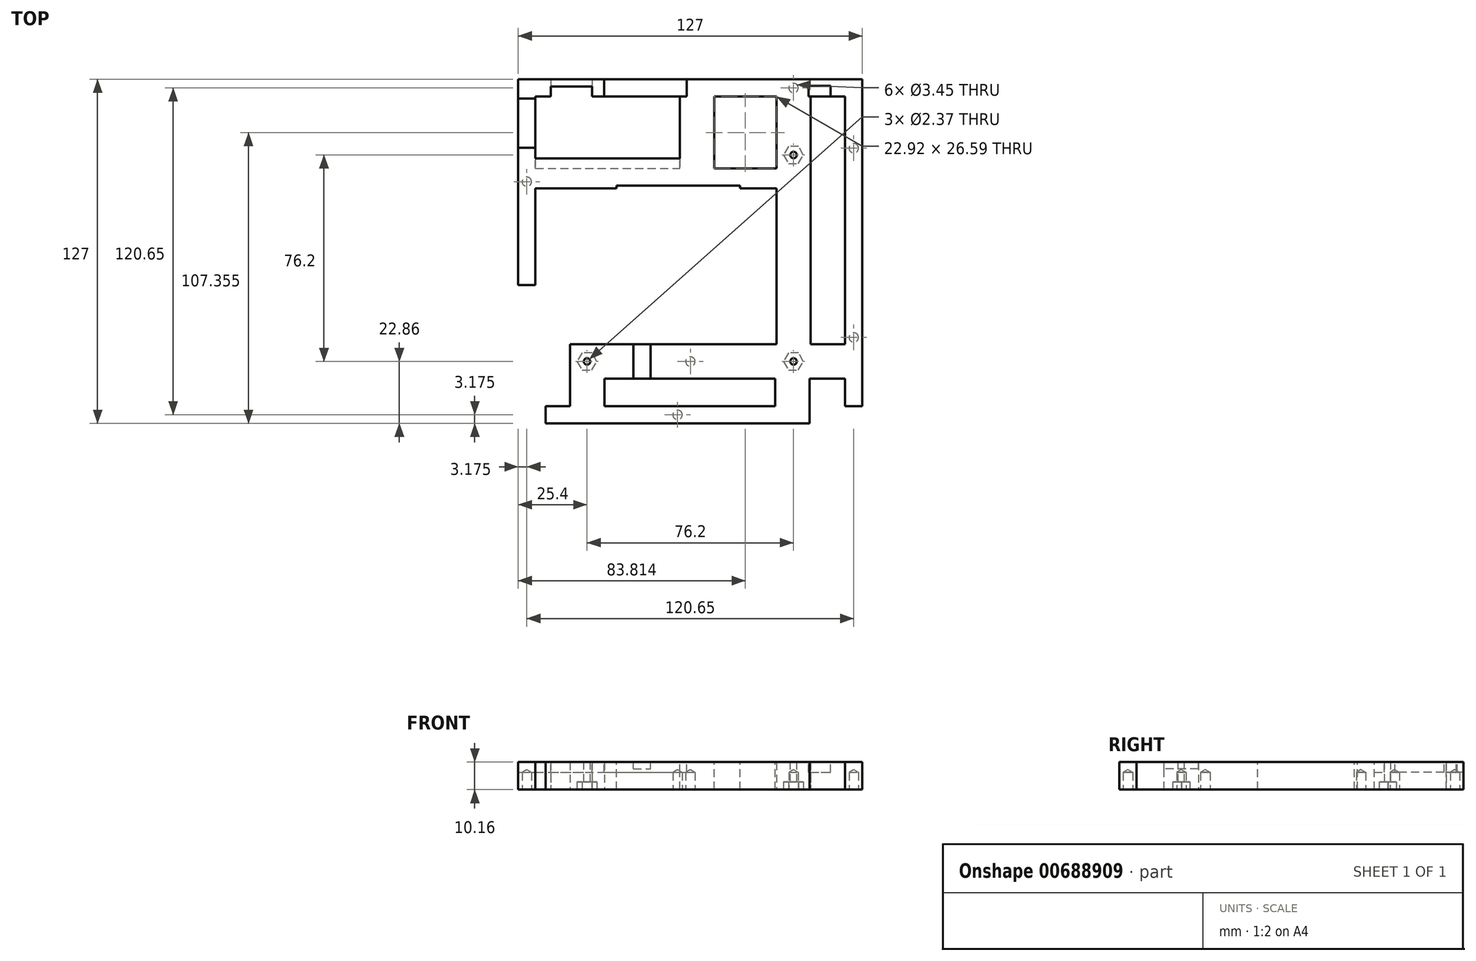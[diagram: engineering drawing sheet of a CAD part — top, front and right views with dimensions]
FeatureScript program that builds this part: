
annotation { "Feature Type Name" : "Feature", "Feature Type Description" : "" }
export const myFeature = defineFeature(function(context is Context, id is Id, definition is map)
    precondition{}
    {
        {
            var Q0;
            Q0=qCreatedBy(makeId("Top.planeOp"),FACE);
            var sketch = newSketch(context, id + "F0", { "sketchPlane" : qUnion([Q0])});
            skLineSegment(sketch, "E0", {"start": v(-9.04, 13.82) * mm, "end": v(-9.04, 13.7) * mm});
            skLineSegment(sketch, "E1", {"start": v(-9.04, 13.7) * mm, "end": v(-9.28, 13.35) * mm});
            skLineSegment(sketch, "E2", {"start": v(-9.28, 13.35) * mm, "end": v(-9.32, 13.32) * mm});
            skLineSegment(sketch, "E3", {"start": v(-9.32, 13.32) * mm, "end": v(-9.37, 13.3) * mm});
            skLineSegment(sketch, "E4", {"start": v(-9.37, 13.3) * mm, "end": v(-9.85, 13.3) * mm});
            skLineSegment(sketch, "E5", {"start": v(-9.85, 13.3) * mm, "end": v(-9.9, 13.32) * mm});
            skLineSegment(sketch, "E6", {"start": v(-9.9, 13.32) * mm, "end": v(-9.94, 13.35) * mm});
            skLineSegment(sketch, "E7", {"start": v(-9.94, 13.35) * mm, "end": v(-10.18, 13.7) * mm});
            skLineSegment(sketch, "E8", {"start": v(-10.18, 13.7) * mm, "end": v(-10.18, 13.82) * mm});
            skLineSegment(sketch, "E9", {"start": v(-10.18, 13.82) * mm, "end": v(-10.18, 13.94) * mm});
            skLineSegment(sketch, "E10", {"start": v(-10.18, 13.94) * mm, "end": v(-9.94, 14.3) * mm});
            skLineSegment(sketch, "E11", {"start": v(-9.94, 14.3) * mm, "end": v(-9.9, 14.31) * mm});
            skLineSegment(sketch, "E12", {"start": v(-9.9, 14.31) * mm, "end": v(-9.85, 14.34) * mm});
            skLineSegment(sketch, "E13", {"start": v(-9.85, 14.34) * mm, "end": v(-9.37, 14.34) * mm});
            skLineSegment(sketch, "E14", {"start": v(-9.37, 14.34) * mm, "end": v(-9.32, 14.31) * mm});
            skLineSegment(sketch, "E15", {"start": v(-9.32, 14.31) * mm, "end": v(-9.28, 14.3) * mm});
            skLineSegment(sketch, "E16", {"start": v(-9.28, 14.3) * mm, "end": v(-9.04, 13.94) * mm});
            skLineSegment(sketch, "E17", {"start": v(-9.04, 13.94) * mm, "end": v(-9.04, 13.82) * mm});
            skLineSegment(sketch, "E18", {"start": v(-52.06, -1.27) * mm, "end": v(-52.06, -1.46) * mm});
            skLineSegment(sketch, "E19", {"start": v(-52.06, -1.46) * mm, "end": v(-52.26, -2.02) * mm});
            skLineSegment(sketch, "E20", {"start": v(-52.26, -2.02) * mm, "end": v(-52.7, -2.5) * mm});
            skLineSegment(sketch, "E21", {"start": v(-52.7, -2.5) * mm, "end": v(-52.8, -2.57) * mm});
            skLineSegment(sketch, "E22", {"start": v(-52.8, -2.57) * mm, "end": v(-52.93, -2.63) * mm});
            skLineSegment(sketch, "E23", {"start": v(-52.93, -2.63) * mm, "end": v(-53.56, -2.77) * mm});
            skLineSegment(sketch, "E24", {"start": v(-53.56, -2.77) * mm, "end": v(-54.2, -2.63) * mm});
            skLineSegment(sketch, "E25", {"start": v(-54.2, -2.63) * mm, "end": v(-54.3, -2.57) * mm});
            skLineSegment(sketch, "E26", {"start": v(-54.3, -2.57) * mm, "end": v(-54.43, -2.5) * mm});
            skLineSegment(sketch, "E27", {"start": v(-54.43, -2.5) * mm, "end": v(-54.86, -2.02) * mm});
            skLineSegment(sketch, "E28", {"start": v(-54.86, -2.02) * mm, "end": v(-55.06, -1.46) * mm});
            skLineSegment(sketch, "E29", {"start": v(-55.06, -1.46) * mm, "end": v(-55.06, -1.27) * mm});
            skLineSegment(sketch, "E30", {"start": v(-55.06, -1.27) * mm, "end": v(-55.06, -1.08) * mm});
            skLineSegment(sketch, "E31", {"start": v(-55.06, -1.08) * mm, "end": v(-54.86, -0.52) * mm});
            skLineSegment(sketch, "E32", {"start": v(-54.86, -0.52) * mm, "end": v(-54.43, -0.04) * mm});
            skLineSegment(sketch, "E33", {"start": v(-54.43, -0.04) * mm, "end": v(-54.3, 0.03) * mm});
            skLineSegment(sketch, "E34", {"start": v(-54.3, 0.03) * mm, "end": v(-54.2, 0.1) * mm});
            skLineSegment(sketch, "E35", {"start": v(-54.2, 0.1) * mm, "end": v(-53.56, 0.23) * mm});
            skLineSegment(sketch, "E36", {"start": v(-53.56, 0.23) * mm, "end": v(-52.93, 0.1) * mm});
            skLineSegment(sketch, "E37", {"start": v(-52.93, 0.1) * mm, "end": v(-52.8, 0.03) * mm});
            skLineSegment(sketch, "E38", {"start": v(-52.8, 0.03) * mm, "end": v(-52.7, -0.04) * mm});
            skLineSegment(sketch, "E39", {"start": v(-52.7, -0.04) * mm, "end": v(-52.26, -0.52) * mm});
            skLineSegment(sketch, "E40", {"start": v(-52.26, -0.52) * mm, "end": v(-52.06, -1.08) * mm});
            skLineSegment(sketch, "E41", {"start": v(-52.06, -1.08) * mm, "end": v(-52.06, -1.27) * mm});
            skLineSegment(sketch, "E42", {"start": v(-52.06, -9.17) * mm, "end": v(-52.06, -9.36) * mm});
            skLineSegment(sketch, "E43", {"start": v(-52.06, -9.36) * mm, "end": v(-52.26, -9.92) * mm});
            skLineSegment(sketch, "E44", {"start": v(-52.26, -9.92) * mm, "end": v(-52.7, -10.4) * mm});
            skLineSegment(sketch, "E45", {"start": v(-52.7, -10.4) * mm, "end": v(-52.8, -10.47) * mm});
            skLineSegment(sketch, "E46", {"start": v(-52.8, -10.47) * mm, "end": v(-52.93, -10.54) * mm});
            skLineSegment(sketch, "E47", {"start": v(-52.93, -10.54) * mm, "end": v(-53.56, -10.67) * mm});
            skLineSegment(sketch, "E48", {"start": v(-53.56, -10.67) * mm, "end": v(-54.2, -10.54) * mm});
            skLineSegment(sketch, "E49", {"start": v(-54.2, -10.54) * mm, "end": v(-54.3, -10.47) * mm});
            skLineSegment(sketch, "E50", {"start": v(-54.3, -10.47) * mm, "end": v(-54.43, -10.4) * mm});
            skLineSegment(sketch, "E51", {"start": v(-54.43, -10.4) * mm, "end": v(-54.86, -9.92) * mm});
            skLineSegment(sketch, "E52", {"start": v(-54.86, -9.92) * mm, "end": v(-55.06, -9.36) * mm});
            skLineSegment(sketch, "E53", {"start": v(-55.06, -9.36) * mm, "end": v(-55.06, -9.17) * mm});
            skLineSegment(sketch, "E54", {"start": v(-55.06, -9.17) * mm, "end": v(-55.06, -8.98) * mm});
            skLineSegment(sketch, "E55", {"start": v(-55.06, -8.98) * mm, "end": v(-54.86, -8.42) * mm});
            skLineSegment(sketch, "E56", {"start": v(-54.86, -8.42) * mm, "end": v(-54.43, -7.94) * mm});
            skLineSegment(sketch, "E57", {"start": v(-54.43, -7.94) * mm, "end": v(-54.3, -7.87) * mm});
            skLineSegment(sketch, "E58", {"start": v(-54.3, -7.87) * mm, "end": v(-54.2, -7.8) * mm});
            skLineSegment(sketch, "E59", {"start": v(-54.2, -7.8) * mm, "end": v(-53.56, -7.67) * mm});
            skLineSegment(sketch, "E60", {"start": v(-53.56, -7.67) * mm, "end": v(-52.93, -7.8) * mm});
            skLineSegment(sketch, "E61", {"start": v(-52.93, -7.8) * mm, "end": v(-52.8, -7.87) * mm});
            skLineSegment(sketch, "E62", {"start": v(-52.8, -7.87) * mm, "end": v(-52.7, -7.94) * mm});
            skLineSegment(sketch, "E63", {"start": v(-52.7, -7.94) * mm, "end": v(-52.26, -8.42) * mm});
            skLineSegment(sketch, "E64", {"start": v(-52.26, -8.42) * mm, "end": v(-52.06, -8.98) * mm});
            skLineSegment(sketch, "E65", {"start": v(-52.06, -8.98) * mm, "end": v(-52.06, -9.17) * mm});
            skLineSegment(sketch, "E66", {"start": v(-38.7, 57.1) * mm, "end": v(-38.7, 56.77) * mm});
            skLineSegment(sketch, "E67", {"start": v(-38.7, 56.77) * mm, "end": v(-38.87, 55.78) * mm});
            skLineSegment(sketch, "E68", {"start": v(-38.87, 55.78) * mm, "end": v(-39.38, 54.56) * mm});
            skLineSegment(sketch, "E69", {"start": v(-39.38, 54.56) * mm, "end": v(-40.18, 53.52) * mm});
            skLineSegment(sketch, "E70", {"start": v(-40.18, 53.52) * mm, "end": v(-40.95, 52.87) * mm});
            skLineSegment(sketch, "E71", {"start": v(-40.95, 52.87) * mm, "end": v(-41.24, 52.7) * mm});
            skLineSegment(sketch, "E72", {"start": v(-41.24, 52.7) * mm, "end": v(-41.52, 52.53) * mm});
            skLineSegment(sketch, "E73", {"start": v(-41.52, 52.53) * mm, "end": v(-42.47, 52.2) * mm});
            skLineSegment(sketch, "E74", {"start": v(-42.47, 52.2) * mm, "end": v(-43.78, 52.02) * mm});
            skLineSegment(sketch, "E75", {"start": v(-43.78, 52.02) * mm, "end": v(-45.08, 52.2) * mm});
            skLineSegment(sketch, "E76", {"start": v(-45.08, 52.2) * mm, "end": v(-46.03, 52.53) * mm});
            skLineSegment(sketch, "E77", {"start": v(-46.03, 52.53) * mm, "end": v(-46.32, 52.7) * mm});
            skLineSegment(sketch, "E78", {"start": v(-46.32, 52.7) * mm, "end": v(-46.6, 52.87) * mm});
            skLineSegment(sketch, "E79", {"start": v(-46.6, 52.87) * mm, "end": v(-47.38, 53.52) * mm});
            skLineSegment(sketch, "E80", {"start": v(-47.38, 53.52) * mm, "end": v(-48.18, 54.56) * mm});
            skLineSegment(sketch, "E81", {"start": v(-48.18, 54.56) * mm, "end": v(-48.68, 55.78) * mm});
            skLineSegment(sketch, "E82", {"start": v(-48.68, 55.78) * mm, "end": v(-48.86, 56.77) * mm});
            skLineSegment(sketch, "E83", {"start": v(-48.86, 56.77) * mm, "end": v(-48.86, 57.1) * mm});
            skLineSegment(sketch, "E84", {"start": v(-48.86, 57.1) * mm, "end": v(-48.86, 57.43) * mm});
            skLineSegment(sketch, "E85", {"start": v(-48.86, 57.43) * mm, "end": v(-48.68, 58.43) * mm});
            skLineSegment(sketch, "E86", {"start": v(-48.68, 58.43) * mm, "end": v(-48.18, 59.64) * mm});
            skLineSegment(sketch, "E87", {"start": v(-48.18, 59.64) * mm, "end": v(-47.38, 60.68) * mm});
            skLineSegment(sketch, "E88", {"start": v(-47.38, 60.68) * mm, "end": v(-46.6, 61.33) * mm});
            skLineSegment(sketch, "E89", {"start": v(-46.6, 61.33) * mm, "end": v(-46.32, 61.5) * mm});
            skLineSegment(sketch, "E90", {"start": v(-46.32, 61.5) * mm, "end": v(-46.03, 61.67) * mm});
            skLineSegment(sketch, "E91", {"start": v(-46.03, 61.67) * mm, "end": v(-45.08, 62.01) * mm});
            skLineSegment(sketch, "E92", {"start": v(-45.08, 62.01) * mm, "end": v(-43.78, 62.18) * mm});
            skLineSegment(sketch, "E93", {"start": v(-43.78, 62.18) * mm, "end": v(-42.47, 62.01) * mm});
            skLineSegment(sketch, "E94", {"start": v(-42.47, 62.01) * mm, "end": v(-41.52, 61.67) * mm});
            skLineSegment(sketch, "E95", {"start": v(-41.52, 61.67) * mm, "end": v(-41.24, 61.5) * mm});
            skLineSegment(sketch, "E96", {"start": v(-41.24, 61.5) * mm, "end": v(-40.95, 61.33) * mm});
            skLineSegment(sketch, "E97", {"start": v(-40.95, 61.33) * mm, "end": v(-40.18, 60.68) * mm});
            skLineSegment(sketch, "E98", {"start": v(-40.18, 60.68) * mm, "end": v(-39.38, 59.64) * mm});
            skLineSegment(sketch, "E99", {"start": v(-39.38, 59.64) * mm, "end": v(-38.87, 58.43) * mm});
            skLineSegment(sketch, "E100", {"start": v(-38.87, 58.43) * mm, "end": v(-38.7, 57.43) * mm});
            skLineSegment(sketch, "E101", {"start": v(-38.7, 57.43) * mm, "end": v(-38.7, 57.1) * mm});
            skLineSegment(sketch, "E102", {"start": v(-38.78, 38.1) * mm, "end": v(-38.78, 37.77) * mm});
            skLineSegment(sketch, "E103", {"start": v(-38.78, 37.77) * mm, "end": v(-38.95, 36.8) * mm});
            skLineSegment(sketch, "E104", {"start": v(-38.95, 36.8) * mm, "end": v(-39.45, 35.6) * mm});
            skLineSegment(sketch, "E105", {"start": v(-39.45, 35.6) * mm, "end": v(-40.23, 34.57) * mm});
            skLineSegment(sketch, "E106", {"start": v(-40.23, 34.57) * mm, "end": v(-41, 33.93) * mm});
            skLineSegment(sketch, "E107", {"start": v(-41, 33.93) * mm, "end": v(-41.28, 33.77) * mm});
            skLineSegment(sketch, "E108", {"start": v(-41.28, 33.77) * mm, "end": v(-41.56, 33.6) * mm});
            skLineSegment(sketch, "E109", {"start": v(-41.56, 33.6) * mm, "end": v(-42.5, 33.27) * mm});
            skLineSegment(sketch, "E110", {"start": v(-42.5, 33.27) * mm, "end": v(-43.78, 33.1) * mm});
            skLineSegment(sketch, "E111", {"start": v(-43.78, 33.1) * mm, "end": v(-45.06, 33.27) * mm});
            skLineSegment(sketch, "E112", {"start": v(-45.06, 33.27) * mm, "end": v(-46, 33.6) * mm});
            skLineSegment(sketch, "E113", {"start": v(-46, 33.6) * mm, "end": v(-46.28, 33.77) * mm});
            skLineSegment(sketch, "E114", {"start": v(-46.28, 33.77) * mm, "end": v(-46.56, 33.93) * mm});
            skLineSegment(sketch, "E115", {"start": v(-46.56, 33.93) * mm, "end": v(-47.32, 34.57) * mm});
            skLineSegment(sketch, "E116", {"start": v(-47.32, 34.57) * mm, "end": v(-48.1, 35.6) * mm});
            skLineSegment(sketch, "E117", {"start": v(-48.1, 35.6) * mm, "end": v(-48.6, 36.8) * mm});
            skLineSegment(sketch, "E118", {"start": v(-48.6, 36.8) * mm, "end": v(-48.78, 37.77) * mm});
            skLineSegment(sketch, "E119", {"start": v(-48.78, 37.77) * mm, "end": v(-48.78, 38.1) * mm});
            skLineSegment(sketch, "E120", {"start": v(-48.78, 38.1) * mm, "end": v(-48.78, 38.43) * mm});
            skLineSegment(sketch, "E121", {"start": v(-48.78, 38.43) * mm, "end": v(-48.6, 39.4) * mm});
            skLineSegment(sketch, "E122", {"start": v(-48.6, 39.4) * mm, "end": v(-48.1, 40.6) * mm});
            skLineSegment(sketch, "E123", {"start": v(-48.1, 40.6) * mm, "end": v(-47.32, 41.63) * mm});
            skLineSegment(sketch, "E124", {"start": v(-47.32, 41.63) * mm, "end": v(-46.56, 42.27) * mm});
            skLineSegment(sketch, "E125", {"start": v(-46.56, 42.27) * mm, "end": v(-46.28, 42.43) * mm});
            skLineSegment(sketch, "E126", {"start": v(-46.28, 42.43) * mm, "end": v(-46, 42.6) * mm});
            skLineSegment(sketch, "E127", {"start": v(-46, 42.6) * mm, "end": v(-45.06, 42.93) * mm});
            skLineSegment(sketch, "E128", {"start": v(-45.06, 42.93) * mm, "end": v(-43.78, 43.1) * mm});
            skLineSegment(sketch, "E129", {"start": v(-43.78, 43.1) * mm, "end": v(-42.5, 42.93) * mm});
            skLineSegment(sketch, "E130", {"start": v(-42.5, 42.93) * mm, "end": v(-41.56, 42.6) * mm});
            skLineSegment(sketch, "E131", {"start": v(-41.56, 42.6) * mm, "end": v(-41.28, 42.43) * mm});
            skLineSegment(sketch, "E132", {"start": v(-41.28, 42.43) * mm, "end": v(-41, 42.27) * mm});
            skLineSegment(sketch, "E133", {"start": v(-41, 42.27) * mm, "end": v(-40.23, 41.63) * mm});
            skLineSegment(sketch, "E134", {"start": v(-40.23, 41.63) * mm, "end": v(-39.45, 40.6) * mm});
            skLineSegment(sketch, "E135", {"start": v(-39.45, 40.6) * mm, "end": v(-38.95, 39.4) * mm});
            skLineSegment(sketch, "E136", {"start": v(-38.95, 39.4) * mm, "end": v(-38.78, 38.43) * mm});
            skLineSegment(sketch, "E137", {"start": v(-38.78, 38.43) * mm, "end": v(-38.78, 38.1) * mm});
            skLineSegment(sketch, "E138", {"start": v(50.96, 58.44) * mm, "end": v(49.45, 58.44) * mm});
            skLineSegment(sketch, "E139", {"start": v(46.74, 53.34) * mm, "end": v(46.74, 53.24) * mm});
            skLineSegment(sketch, "E140", {"start": v(46.74, 53.24) * mm, "end": v(46.63, 52.94) * mm});
            skLineSegment(sketch, "E141", {"start": v(46.63, 52.94) * mm, "end": v(46.4, 52.68) * mm});
            skLineSegment(sketch, "E142", {"start": v(46.4, 52.68) * mm, "end": v(46.34, 52.65) * mm});
            skLineSegment(sketch, "E143", {"start": v(46.34, 52.65) * mm, "end": v(46.28, 52.61) * mm});
            skLineSegment(sketch, "E144", {"start": v(46.28, 52.61) * mm, "end": v(45.6, 52.61) * mm});
            skLineSegment(sketch, "E145", {"start": v(45.6, 52.61) * mm, "end": v(45.54, 52.65) * mm});
            skLineSegment(sketch, "E146", {"start": v(45.54, 52.65) * mm, "end": v(45.48, 52.68) * mm});
            skLineSegment(sketch, "E147", {"start": v(45.48, 52.68) * mm, "end": v(45.25, 52.94) * mm});
            skLineSegment(sketch, "E148", {"start": v(45.25, 52.94) * mm, "end": v(45.14, 53.24) * mm});
            skLineSegment(sketch, "E149", {"start": v(45.14, 53.24) * mm, "end": v(45.14, 53.34) * mm});
            skLineSegment(sketch, "E150", {"start": v(45.14, 53.34) * mm, "end": v(45.14, 53.44) * mm});
            skLineSegment(sketch, "E151", {"start": v(45.14, 53.44) * mm, "end": v(45.25, 53.74) * mm});
            skLineSegment(sketch, "E152", {"start": v(45.25, 53.74) * mm, "end": v(45.48, 54) * mm});
            skLineSegment(sketch, "E153", {"start": v(45.48, 54) * mm, "end": v(45.54, 54.03) * mm});
            skLineSegment(sketch, "E154", {"start": v(45.54, 54.03) * mm, "end": v(45.6, 54.07) * mm});
            skLineSegment(sketch, "E155", {"start": v(45.6, 54.07) * mm, "end": v(46.28, 54.07) * mm});
            skLineSegment(sketch, "E156", {"start": v(46.28, 54.07) * mm, "end": v(46.34, 54.03) * mm});
            skLineSegment(sketch, "E157", {"start": v(46.34, 54.03) * mm, "end": v(46.4, 54) * mm});
            skLineSegment(sketch, "E158", {"start": v(46.4, 54) * mm, "end": v(46.63, 53.74) * mm});
            skLineSegment(sketch, "E159", {"start": v(46.63, 53.74) * mm, "end": v(46.74, 53.44) * mm});
            skLineSegment(sketch, "E160", {"start": v(46.74, 53.44) * mm, "end": v(46.74, 53.34) * mm});
            skLineSegment(sketch, "E161", {"start": v(50.96, 48.24) * mm, "end": v(49.45, 48.24) * mm});
            skLineSegment(sketch, "E162", {"start": v(46.74, 55.84) * mm, "end": v(46.74, 55.74) * mm});
            skLineSegment(sketch, "E163", {"start": v(46.74, 55.74) * mm, "end": v(46.63, 55.44) * mm});
            skLineSegment(sketch, "E164", {"start": v(46.63, 55.44) * mm, "end": v(46.4, 55.18) * mm});
            skLineSegment(sketch, "E165", {"start": v(46.4, 55.18) * mm, "end": v(46.34, 55.15) * mm});
            skLineSegment(sketch, "E166", {"start": v(46.34, 55.15) * mm, "end": v(46.28, 55.11) * mm});
            skLineSegment(sketch, "E167", {"start": v(46.28, 55.11) * mm, "end": v(45.6, 55.11) * mm});
            skLineSegment(sketch, "E168", {"start": v(45.6, 55.11) * mm, "end": v(45.54, 55.15) * mm});
            skLineSegment(sketch, "E169", {"start": v(45.54, 55.15) * mm, "end": v(45.48, 55.18) * mm});
            skLineSegment(sketch, "E170", {"start": v(45.48, 55.18) * mm, "end": v(45.25, 55.44) * mm});
            skLineSegment(sketch, "E171", {"start": v(45.25, 55.44) * mm, "end": v(45.14, 55.74) * mm});
            skLineSegment(sketch, "E172", {"start": v(45.14, 55.74) * mm, "end": v(45.14, 55.84) * mm});
            skLineSegment(sketch, "E173", {"start": v(45.14, 55.84) * mm, "end": v(45.14, 55.94) * mm});
            skLineSegment(sketch, "E174", {"start": v(45.14, 55.94) * mm, "end": v(45.25, 56.24) * mm});
            skLineSegment(sketch, "E175", {"start": v(45.25, 56.24) * mm, "end": v(45.48, 56.5) * mm});
            skLineSegment(sketch, "E176", {"start": v(45.48, 56.5) * mm, "end": v(45.54, 56.53) * mm});
            skLineSegment(sketch, "E177", {"start": v(45.54, 56.53) * mm, "end": v(45.6, 56.57) * mm});
            skLineSegment(sketch, "E178", {"start": v(45.6, 56.57) * mm, "end": v(46.28, 56.57) * mm});
            skLineSegment(sketch, "E179", {"start": v(46.28, 56.57) * mm, "end": v(46.34, 56.53) * mm});
            skLineSegment(sketch, "E180", {"start": v(46.34, 56.53) * mm, "end": v(46.4, 56.5) * mm});
            skLineSegment(sketch, "E181", {"start": v(46.4, 56.5) * mm, "end": v(46.63, 56.24) * mm});
            skLineSegment(sketch, "E182", {"start": v(46.63, 56.24) * mm, "end": v(46.74, 55.94) * mm});
            skLineSegment(sketch, "E183", {"start": v(46.74, 55.94) * mm, "end": v(46.74, 55.84) * mm});
            skLineSegment(sketch, "E184", {"start": v(49.7, -59.2) * mm, "end": v(49.7, -59.51) * mm});
            skLineSegment(sketch, "E185", {"start": v(52.24, -59.2) * mm, "end": v(52.24, -59.51) * mm});
            skLineSegment(sketch, "E186", {"start": v(54.77, -59.2) * mm, "end": v(54.77, -59.51) * mm});
            skLineSegment(sketch, "E187", {"start": v(57.31, -59.2) * mm, "end": v(57.31, -59.51) * mm});
            skLineSegment(sketch, "E188", {"start": v(59.85, -59.2) * mm, "end": v(59.85, -59.51) * mm});
            skLineSegment(sketch, "E189", {"start": v(50.96, 40.66) * mm, "end": v(49.45, 40.66) * mm});
            skLineSegment(sketch, "E190", {"start": v(46.74, 35.56) * mm, "end": v(46.74, 35.46) * mm});
            skLineSegment(sketch, "E191", {"start": v(46.74, 35.46) * mm, "end": v(46.63, 35.16) * mm});
            skLineSegment(sketch, "E192", {"start": v(46.63, 35.16) * mm, "end": v(46.4, 34.9) * mm});
            skLineSegment(sketch, "E193", {"start": v(46.4, 34.9) * mm, "end": v(46.34, 34.87) * mm});
            skLineSegment(sketch, "E194", {"start": v(46.34, 34.87) * mm, "end": v(46.28, 34.83) * mm});
            skLineSegment(sketch, "E195", {"start": v(46.28, 34.83) * mm, "end": v(45.6, 34.83) * mm});
            skLineSegment(sketch, "E196", {"start": v(45.6, 34.83) * mm, "end": v(45.54, 34.87) * mm});
            skLineSegment(sketch, "E197", {"start": v(45.54, 34.87) * mm, "end": v(45.48, 34.9) * mm});
            skLineSegment(sketch, "E198", {"start": v(45.48, 34.9) * mm, "end": v(45.25, 35.16) * mm});
            skLineSegment(sketch, "E199", {"start": v(45.25, 35.16) * mm, "end": v(45.14, 35.46) * mm});
            skLineSegment(sketch, "E200", {"start": v(45.14, 35.46) * mm, "end": v(45.14, 35.56) * mm});
            skLineSegment(sketch, "E201", {"start": v(45.14, 35.56) * mm, "end": v(45.14, 35.66) * mm});
            skLineSegment(sketch, "E202", {"start": v(45.14, 35.66) * mm, "end": v(45.25, 35.96) * mm});
            skLineSegment(sketch, "E203", {"start": v(45.25, 35.96) * mm, "end": v(45.48, 36.22) * mm});
            skLineSegment(sketch, "E204", {"start": v(45.48, 36.22) * mm, "end": v(45.54, 36.25) * mm});
            skLineSegment(sketch, "E205", {"start": v(45.54, 36.25) * mm, "end": v(45.6, 36.29) * mm});
            skLineSegment(sketch, "E206", {"start": v(45.6, 36.29) * mm, "end": v(46.28, 36.29) * mm});
            skLineSegment(sketch, "E207", {"start": v(46.28, 36.29) * mm, "end": v(46.34, 36.25) * mm});
            skLineSegment(sketch, "E208", {"start": v(46.34, 36.25) * mm, "end": v(46.4, 36.22) * mm});
            skLineSegment(sketch, "E209", {"start": v(46.4, 36.22) * mm, "end": v(46.63, 35.96) * mm});
            skLineSegment(sketch, "E210", {"start": v(46.63, 35.96) * mm, "end": v(46.74, 35.66) * mm});
            skLineSegment(sketch, "E211", {"start": v(46.74, 35.66) * mm, "end": v(46.74, 35.56) * mm});
            skLineSegment(sketch, "E212", {"start": v(50.96, 30.46) * mm, "end": v(49.45, 30.46) * mm});
            skLineSegment(sketch, "E213", {"start": v(46.74, 38.06) * mm, "end": v(46.74, 37.96) * mm});
            skLineSegment(sketch, "E214", {"start": v(46.74, 37.96) * mm, "end": v(46.63, 37.66) * mm});
            skLineSegment(sketch, "E215", {"start": v(46.63, 37.66) * mm, "end": v(46.4, 37.4) * mm});
            skLineSegment(sketch, "E216", {"start": v(46.4, 37.4) * mm, "end": v(46.34, 37.37) * mm});
            skLineSegment(sketch, "E217", {"start": v(46.34, 37.37) * mm, "end": v(46.28, 37.33) * mm});
            skLineSegment(sketch, "E218", {"start": v(46.28, 37.33) * mm, "end": v(45.6, 37.33) * mm});
            skLineSegment(sketch, "E219", {"start": v(45.6, 37.33) * mm, "end": v(45.54, 37.37) * mm});
            skLineSegment(sketch, "E220", {"start": v(45.54, 37.37) * mm, "end": v(45.48, 37.4) * mm});
            skLineSegment(sketch, "E221", {"start": v(45.48, 37.4) * mm, "end": v(45.25, 37.66) * mm});
            skLineSegment(sketch, "E222", {"start": v(45.25, 37.66) * mm, "end": v(45.14, 37.96) * mm});
            skLineSegment(sketch, "E223", {"start": v(45.14, 37.96) * mm, "end": v(45.14, 38.06) * mm});
            skLineSegment(sketch, "E224", {"start": v(45.14, 38.06) * mm, "end": v(45.14, 38.16) * mm});
            skLineSegment(sketch, "E225", {"start": v(45.14, 38.16) * mm, "end": v(45.25, 38.46) * mm});
            skLineSegment(sketch, "E226", {"start": v(45.25, 38.46) * mm, "end": v(45.48, 38.72) * mm});
            skLineSegment(sketch, "E227", {"start": v(45.48, 38.72) * mm, "end": v(45.54, 38.75) * mm});
            skLineSegment(sketch, "E228", {"start": v(45.54, 38.75) * mm, "end": v(45.6, 38.79) * mm});
            skLineSegment(sketch, "E229", {"start": v(45.6, 38.79) * mm, "end": v(46.28, 38.79) * mm});
            skLineSegment(sketch, "E230", {"start": v(46.28, 38.79) * mm, "end": v(46.34, 38.75) * mm});
            skLineSegment(sketch, "E231", {"start": v(46.34, 38.75) * mm, "end": v(46.4, 38.72) * mm});
            skLineSegment(sketch, "E232", {"start": v(46.4, 38.72) * mm, "end": v(46.63, 38.46) * mm});
            skLineSegment(sketch, "E233", {"start": v(46.63, 38.46) * mm, "end": v(46.74, 38.16) * mm});
            skLineSegment(sketch, "E234", {"start": v(46.74, 38.16) * mm, "end": v(46.74, 38.06) * mm});
            skLineSegment(sketch, "E235", {"start": v(-60.14, 41.76) * mm, "end": v(-60.14, 41.62) * mm});
            skLineSegment(sketch, "E236", {"start": v(-60.14, 41.62) * mm, "end": v(-60.43, 41.21) * mm});
            skLineSegment(sketch, "E237", {"start": v(-60.43, 41.21) * mm, "end": v(-60.48, 41.18) * mm});
            skLineSegment(sketch, "E238", {"start": v(-60.48, 41.18) * mm, "end": v(-60.53, 41.15) * mm});
            skLineSegment(sketch, "E239", {"start": v(-60.53, 41.15) * mm, "end": v(-61.1, 41.15) * mm});
            skLineSegment(sketch, "E240", {"start": v(-61.1, 41.15) * mm, "end": v(-61.16, 41.18) * mm});
            skLineSegment(sketch, "E241", {"start": v(-61.16, 41.18) * mm, "end": v(-61.2, 41.21) * mm});
            skLineSegment(sketch, "E242", {"start": v(-61.2, 41.21) * mm, "end": v(-61.5, 41.63) * mm});
            skLineSegment(sketch, "E243", {"start": v(-61.5, 41.63) * mm, "end": v(-61.5, 41.76) * mm});
            skLineSegment(sketch, "E244", {"start": v(-61.5, 41.76) * mm, "end": v(-61.5, 41.91) * mm});
            skLineSegment(sketch, "E245", {"start": v(-61.5, 41.91) * mm, "end": v(-61.2, 42.32) * mm});
            skLineSegment(sketch, "E246", {"start": v(-61.2, 42.32) * mm, "end": v(-61.16, 42.35) * mm});
            skLineSegment(sketch, "E247", {"start": v(-61.16, 42.35) * mm, "end": v(-61.1, 42.38) * mm});
            skLineSegment(sketch, "E248", {"start": v(-61.1, 42.38) * mm, "end": v(-60.53, 42.38) * mm});
            skLineSegment(sketch, "E249", {"start": v(-60.53, 42.38) * mm, "end": v(-60.48, 42.35) * mm});
            skLineSegment(sketch, "E250", {"start": v(-60.48, 42.35) * mm, "end": v(-60.43, 42.32) * mm});
            skLineSegment(sketch, "E251", {"start": v(-60.43, 42.32) * mm, "end": v(-60.14, 41.9) * mm});
            skLineSegment(sketch, "E252", {"start": v(-60.14, 41.9) * mm, "end": v(-60.14, 41.76) * mm});
            skLineSegment(sketch, "E253", {"start": v(-60.14, 52.8) * mm, "end": v(-60.14, 52.65) * mm});
            skLineSegment(sketch, "E254", {"start": v(-60.14, 52.65) * mm, "end": v(-60.43, 52.25) * mm});
            skLineSegment(sketch, "E255", {"start": v(-60.43, 52.25) * mm, "end": v(-60.48, 52.22) * mm});
            skLineSegment(sketch, "E256", {"start": v(-60.48, 52.22) * mm, "end": v(-60.53, 52.19) * mm});
            skLineSegment(sketch, "E257", {"start": v(-60.53, 52.19) * mm, "end": v(-61.1, 52.19) * mm});
            skLineSegment(sketch, "E258", {"start": v(-61.1, 52.19) * mm, "end": v(-61.16, 52.22) * mm});
            skLineSegment(sketch, "E259", {"start": v(-61.16, 52.22) * mm, "end": v(-61.2, 52.25) * mm});
            skLineSegment(sketch, "E260", {"start": v(-61.2, 52.25) * mm, "end": v(-61.5, 52.66) * mm});
            skLineSegment(sketch, "E261", {"start": v(-61.5, 52.66) * mm, "end": v(-61.5, 52.8) * mm});
            skLineSegment(sketch, "E262", {"start": v(-61.5, 52.8) * mm, "end": v(-61.5, 52.95) * mm});
            skLineSegment(sketch, "E263", {"start": v(-61.5, 52.95) * mm, "end": v(-61.2, 53.35) * mm});
            skLineSegment(sketch, "E264", {"start": v(-61.2, 53.35) * mm, "end": v(-61.16, 53.39) * mm});
            skLineSegment(sketch, "E265", {"start": v(-61.16, 53.39) * mm, "end": v(-61.1, 53.42) * mm});
            skLineSegment(sketch, "E266", {"start": v(-61.1, 53.42) * mm, "end": v(-60.53, 53.42) * mm});
            skLineSegment(sketch, "E267", {"start": v(-60.53, 53.42) * mm, "end": v(-60.48, 53.39) * mm});
            skLineSegment(sketch, "E268", {"start": v(-60.48, 53.39) * mm, "end": v(-60.43, 53.35) * mm});
            skLineSegment(sketch, "E269", {"start": v(-60.43, 53.35) * mm, "end": v(-60.14, 52.94) * mm});
            skLineSegment(sketch, "E270", {"start": v(-60.14, 52.94) * mm, "end": v(-60.14, 52.8) * mm});
            skLineSegment(sketch, "E271", {"start": v(-3.08, -52.07) * mm, "end": v(-3.08, -52.4) * mm});
            skLineSegment(sketch, "E272", {"start": v(-3.08, -52.4) * mm, "end": v(-3.26, -53.4) * mm});
            skLineSegment(sketch, "E273", {"start": v(-3.26, -53.4) * mm, "end": v(-3.77, -54.61) * mm});
            skLineSegment(sketch, "E274", {"start": v(-3.77, -54.61) * mm, "end": v(-4.56, -55.65) * mm});
            skLineSegment(sketch, "E275", {"start": v(-4.56, -55.65) * mm, "end": v(-5.34, -56.3) * mm});
            skLineSegment(sketch, "E276", {"start": v(-5.34, -56.3) * mm, "end": v(-5.62, -56.47) * mm});
            skLineSegment(sketch, "E277", {"start": v(-5.62, -56.47) * mm, "end": v(-5.91, -56.63) * mm});
            skLineSegment(sketch, "E278", {"start": v(-5.91, -56.63) * mm, "end": v(-6.86, -56.98) * mm});
            skLineSegment(sketch, "E279", {"start": v(-6.86, -56.98) * mm, "end": v(-8.16, -57.15) * mm});
            skLineSegment(sketch, "E280", {"start": v(-8.16, -57.15) * mm, "end": v(-9.47, -56.98) * mm});
            skLineSegment(sketch, "E281", {"start": v(-9.47, -56.98) * mm, "end": v(-10.42, -56.63) * mm});
            skLineSegment(sketch, "E282", {"start": v(-10.42, -56.63) * mm, "end": v(-10.7, -56.47) * mm});
            skLineSegment(sketch, "E283", {"start": v(-10.7, -56.47) * mm, "end": v(-11, -56.3) * mm});
            skLineSegment(sketch, "E284", {"start": v(-11, -56.3) * mm, "end": v(-11.76, -55.65) * mm});
            skLineSegment(sketch, "E285", {"start": v(-11.76, -55.65) * mm, "end": v(-12.56, -54.61) * mm});
            skLineSegment(sketch, "E286", {"start": v(-12.56, -54.61) * mm, "end": v(-13.07, -53.4) * mm});
            skLineSegment(sketch, "E287", {"start": v(-13.07, -53.4) * mm, "end": v(-13.24, -52.4) * mm});
            skLineSegment(sketch, "E288", {"start": v(-13.24, -52.4) * mm, "end": v(-13.24, -52.07) * mm});
            skLineSegment(sketch, "E289", {"start": v(-13.24, -52.07) * mm, "end": v(-13.24, -51.74) * mm});
            skLineSegment(sketch, "E290", {"start": v(-13.24, -51.74) * mm, "end": v(-13.07, -50.74) * mm});
            skLineSegment(sketch, "E291", {"start": v(-13.07, -50.74) * mm, "end": v(-12.56, -49.53) * mm});
            skLineSegment(sketch, "E292", {"start": v(-12.56, -49.53) * mm, "end": v(-11.76, -48.48) * mm});
            skLineSegment(sketch, "E293", {"start": v(-11.76, -48.48) * mm, "end": v(-11, -47.84) * mm});
            skLineSegment(sketch, "E294", {"start": v(-11, -47.84) * mm, "end": v(-10.7, -47.67) * mm});
            skLineSegment(sketch, "E295", {"start": v(-10.7, -47.67) * mm, "end": v(-10.42, -47.5) * mm});
            skLineSegment(sketch, "E296", {"start": v(-10.42, -47.5) * mm, "end": v(-9.47, -47.16) * mm});
            skLineSegment(sketch, "E297", {"start": v(-9.47, -47.16) * mm, "end": v(-8.16, -46.99) * mm});
            skLineSegment(sketch, "E298", {"start": v(-8.16, -46.99) * mm, "end": v(-6.86, -47.16) * mm});
            skLineSegment(sketch, "E299", {"start": v(-6.86, -47.16) * mm, "end": v(-5.91, -47.5) * mm});
            skLineSegment(sketch, "E300", {"start": v(-5.91, -47.5) * mm, "end": v(-5.62, -47.67) * mm});
            skLineSegment(sketch, "E301", {"start": v(-5.62, -47.67) * mm, "end": v(-5.34, -47.84) * mm});
            skLineSegment(sketch, "E302", {"start": v(-5.34, -47.84) * mm, "end": v(-4.56, -48.48) * mm});
            skLineSegment(sketch, "E303", {"start": v(-4.56, -48.48) * mm, "end": v(-3.77, -49.53) * mm});
            skLineSegment(sketch, "E304", {"start": v(-3.77, -49.53) * mm, "end": v(-3.26, -50.74) * mm});
            skLineSegment(sketch, "E305", {"start": v(-3.26, -50.74) * mm, "end": v(-3.08, -51.74) * mm});
            skLineSegment(sketch, "E306", {"start": v(-3.08, -51.74) * mm, "end": v(-3.08, -52.07) * mm});
            skLineSegment(sketch, "E307", {"start": v(-22.16, -52.07) * mm, "end": v(-22.16, -52.4) * mm});
            skLineSegment(sketch, "E308", {"start": v(-22.16, -52.4) * mm, "end": v(-22.34, -53.37) * mm});
            skLineSegment(sketch, "E309", {"start": v(-22.34, -53.37) * mm, "end": v(-22.83, -54.57) * mm});
            skLineSegment(sketch, "E310", {"start": v(-22.83, -54.57) * mm, "end": v(-23.62, -55.6) * mm});
            skLineSegment(sketch, "E311", {"start": v(-23.62, -55.6) * mm, "end": v(-24.38, -56.24) * mm});
            skLineSegment(sketch, "E312", {"start": v(-24.38, -56.24) * mm, "end": v(-24.67, -56.4) * mm});
            skLineSegment(sketch, "E313", {"start": v(-24.67, -56.4) * mm, "end": v(-24.95, -56.56) * mm});
            skLineSegment(sketch, "E314", {"start": v(-24.95, -56.56) * mm, "end": v(-25.88, -56.9) * mm});
            skLineSegment(sketch, "E315", {"start": v(-25.88, -56.9) * mm, "end": v(-27.16, -57.07) * mm});
            skLineSegment(sketch, "E316", {"start": v(-27.16, -57.07) * mm, "end": v(-28.45, -56.9) * mm});
            skLineSegment(sketch, "E317", {"start": v(-28.45, -56.9) * mm, "end": v(-29.38, -56.56) * mm});
            skLineSegment(sketch, "E318", {"start": v(-29.38, -56.56) * mm, "end": v(-29.66, -56.4) * mm});
            skLineSegment(sketch, "E319", {"start": v(-29.66, -56.4) * mm, "end": v(-29.95, -56.24) * mm});
            skLineSegment(sketch, "E320", {"start": v(-29.95, -56.24) * mm, "end": v(-30.7, -55.6) * mm});
            skLineSegment(sketch, "E321", {"start": v(-30.7, -55.6) * mm, "end": v(-31.5, -54.57) * mm});
            skLineSegment(sketch, "E322", {"start": v(-31.5, -54.57) * mm, "end": v(-32, -53.37) * mm});
            skLineSegment(sketch, "E323", {"start": v(-32, -53.37) * mm, "end": v(-32.16, -52.4) * mm});
            skLineSegment(sketch, "E324", {"start": v(-32.16, -52.4) * mm, "end": v(-32.16, -52.07) * mm});
            skLineSegment(sketch, "E325", {"start": v(-32.16, -52.07) * mm, "end": v(-32.16, -51.74) * mm});
            skLineSegment(sketch, "E326", {"start": v(-32.16, -51.74) * mm, "end": v(-32, -50.77) * mm});
            skLineSegment(sketch, "E327", {"start": v(-32, -50.77) * mm, "end": v(-31.5, -49.57) * mm});
            skLineSegment(sketch, "E328", {"start": v(-31.5, -49.57) * mm, "end": v(-30.7, -48.54) * mm});
            skLineSegment(sketch, "E329", {"start": v(-30.7, -48.54) * mm, "end": v(-29.95, -47.9) * mm});
            skLineSegment(sketch, "E330", {"start": v(-29.95, -47.9) * mm, "end": v(-29.66, -47.74) * mm});
            skLineSegment(sketch, "E331", {"start": v(-29.66, -47.74) * mm, "end": v(-29.38, -47.58) * mm});
            skLineSegment(sketch, "E332", {"start": v(-29.38, -47.58) * mm, "end": v(-28.45, -47.24) * mm});
            skLineSegment(sketch, "E333", {"start": v(-28.45, -47.24) * mm, "end": v(-27.16, -47.07) * mm});
            skLineSegment(sketch, "E334", {"start": v(-27.16, -47.07) * mm, "end": v(-25.88, -47.24) * mm});
            skLineSegment(sketch, "E335", {"start": v(-25.88, -47.24) * mm, "end": v(-24.95, -47.58) * mm});
            skLineSegment(sketch, "E336", {"start": v(-24.95, -47.58) * mm, "end": v(-24.67, -47.74) * mm});
            skLineSegment(sketch, "E337", {"start": v(-24.67, -47.74) * mm, "end": v(-24.38, -47.9) * mm});
            skLineSegment(sketch, "E338", {"start": v(-24.38, -47.9) * mm, "end": v(-23.62, -48.54) * mm});
            skLineSegment(sketch, "E339", {"start": v(-23.62, -48.54) * mm, "end": v(-22.83, -49.57) * mm});
            skLineSegment(sketch, "E340", {"start": v(-22.83, -49.57) * mm, "end": v(-22.34, -50.77) * mm});
            skLineSegment(sketch, "E341", {"start": v(-22.34, -50.77) * mm, "end": v(-22.16, -51.74) * mm});
            skLineSegment(sketch, "E342", {"start": v(-22.16, -51.74) * mm, "end": v(-22.16, -52.07) * mm});
            skLineSegment(sketch, "E343", {"start": v(50.96, 5.1) * mm, "end": v(49.45, 5.1) * mm});
            skLineSegment(sketch, "E344", {"start": v(46.74, 0) * mm, "end": v(46.74, -0.1) * mm});
            skLineSegment(sketch, "E345", {"start": v(46.74, -0.1) * mm, "end": v(46.63, -0.4) * mm});
            skLineSegment(sketch, "E346", {"start": v(46.63, -0.4) * mm, "end": v(46.4, -0.66) * mm});
            skLineSegment(sketch, "E347", {"start": v(46.4, -0.66) * mm, "end": v(46.34, -0.7) * mm});
            skLineSegment(sketch, "E348", {"start": v(46.34, -0.7) * mm, "end": v(46.28, -0.73) * mm});
            skLineSegment(sketch, "E349", {"start": v(46.28, -0.73) * mm, "end": v(45.6, -0.73) * mm});
            skLineSegment(sketch, "E350", {"start": v(45.6, -0.73) * mm, "end": v(45.54, -0.7) * mm});
            skLineSegment(sketch, "E351", {"start": v(45.54, -0.7) * mm, "end": v(45.48, -0.66) * mm});
            skLineSegment(sketch, "E352", {"start": v(45.48, -0.66) * mm, "end": v(45.25, -0.4) * mm});
            skLineSegment(sketch, "E353", {"start": v(45.25, -0.4) * mm, "end": v(45.14, -0.1) * mm});
            skLineSegment(sketch, "E354", {"start": v(45.14, -0.1) * mm, "end": v(45.14, 0) * mm});
            skLineSegment(sketch, "E355", {"start": v(45.14, 0) * mm, "end": v(45.14, 0.1) * mm});
            skLineSegment(sketch, "E356", {"start": v(45.14, 0.1) * mm, "end": v(45.25, 0.4) * mm});
            skLineSegment(sketch, "E357", {"start": v(45.25, 0.4) * mm, "end": v(45.48, 0.66) * mm});
            skLineSegment(sketch, "E358", {"start": v(45.48, 0.66) * mm, "end": v(45.54, 0.7) * mm});
            skLineSegment(sketch, "E359", {"start": v(45.54, 0.7) * mm, "end": v(45.6, 0.73) * mm});
            skLineSegment(sketch, "E360", {"start": v(45.6, 0.73) * mm, "end": v(46.28, 0.73) * mm});
            skLineSegment(sketch, "E361", {"start": v(46.28, 0.73) * mm, "end": v(46.34, 0.7) * mm});
            skLineSegment(sketch, "E362", {"start": v(46.34, 0.7) * mm, "end": v(46.4, 0.66) * mm});
            skLineSegment(sketch, "E363", {"start": v(46.4, 0.66) * mm, "end": v(46.63, 0.4) * mm});
            skLineSegment(sketch, "E364", {"start": v(46.63, 0.4) * mm, "end": v(46.74, 0.1) * mm});
            skLineSegment(sketch, "E365", {"start": v(46.74, 0.1) * mm, "end": v(46.74, 0) * mm});
            skLineSegment(sketch, "E366", {"start": v(50.96, -5.1) * mm, "end": v(49.45, -5.1) * mm});
            skLineSegment(sketch, "E367", {"start": v(46.74, 2.5) * mm, "end": v(46.74, 2.4) * mm});
            skLineSegment(sketch, "E368", {"start": v(46.74, 2.4) * mm, "end": v(46.63, 2.1) * mm});
            skLineSegment(sketch, "E369", {"start": v(46.63, 2.1) * mm, "end": v(46.4, 1.84) * mm});
            skLineSegment(sketch, "E370", {"start": v(46.4, 1.84) * mm, "end": v(46.34, 1.8) * mm});
            skLineSegment(sketch, "E371", {"start": v(46.34, 1.8) * mm, "end": v(46.28, 1.77) * mm});
            skLineSegment(sketch, "E372", {"start": v(46.28, 1.77) * mm, "end": v(45.6, 1.77) * mm});
            skLineSegment(sketch, "E373", {"start": v(45.6, 1.77) * mm, "end": v(45.54, 1.8) * mm});
            skLineSegment(sketch, "E374", {"start": v(45.54, 1.8) * mm, "end": v(45.48, 1.84) * mm});
            skLineSegment(sketch, "E375", {"start": v(45.48, 1.84) * mm, "end": v(45.25, 2.1) * mm});
            skLineSegment(sketch, "E376", {"start": v(45.25, 2.1) * mm, "end": v(45.14, 2.4) * mm});
            skLineSegment(sketch, "E377", {"start": v(45.14, 2.4) * mm, "end": v(45.14, 2.5) * mm});
            skLineSegment(sketch, "E378", {"start": v(45.14, 2.5) * mm, "end": v(45.14, 2.6) * mm});
            skLineSegment(sketch, "E379", {"start": v(45.14, 2.6) * mm, "end": v(45.25, 2.9) * mm});
            skLineSegment(sketch, "E380", {"start": v(45.25, 2.9) * mm, "end": v(45.48, 3.16) * mm});
            skLineSegment(sketch, "E381", {"start": v(45.48, 3.16) * mm, "end": v(45.54, 3.2) * mm});
            skLineSegment(sketch, "E382", {"start": v(45.54, 3.2) * mm, "end": v(45.6, 3.23) * mm});
            skLineSegment(sketch, "E383", {"start": v(45.6, 3.23) * mm, "end": v(46.28, 3.23) * mm});
            skLineSegment(sketch, "E384", {"start": v(46.28, 3.23) * mm, "end": v(46.34, 3.2) * mm});
            skLineSegment(sketch, "E385", {"start": v(46.34, 3.2) * mm, "end": v(46.4, 3.16) * mm});
            skLineSegment(sketch, "E386", {"start": v(46.4, 3.16) * mm, "end": v(46.63, 2.9) * mm});
            skLineSegment(sketch, "E387", {"start": v(46.63, 2.9) * mm, "end": v(46.74, 2.6) * mm});
            skLineSegment(sketch, "E388", {"start": v(46.74, 2.6) * mm, "end": v(46.74, 2.5) * mm});
            skLineSegment(sketch, "E389", {"start": v(-22.42, 13.9) * mm, "end": v(-22.42, 13.77) * mm});
            skLineSegment(sketch, "E390", {"start": v(-22.42, 13.77) * mm, "end": v(-22.66, 13.43) * mm});
            skLineSegment(sketch, "E391", {"start": v(-22.66, 13.43) * mm, "end": v(-22.7, 13.4) * mm});
            skLineSegment(sketch, "E392", {"start": v(-22.7, 13.4) * mm, "end": v(-22.75, 13.38) * mm});
            skLineSegment(sketch, "E393", {"start": v(-22.75, 13.38) * mm, "end": v(-23.24, 13.38) * mm});
            skLineSegment(sketch, "E394", {"start": v(-23.24, 13.38) * mm, "end": v(-23.28, 13.4) * mm});
            skLineSegment(sketch, "E395", {"start": v(-23.28, 13.4) * mm, "end": v(-23.32, 13.43) * mm});
            skLineSegment(sketch, "E396", {"start": v(-23.32, 13.43) * mm, "end": v(-23.56, 13.78) * mm});
            skLineSegment(sketch, "E397", {"start": v(-23.56, 13.78) * mm, "end": v(-23.56, 13.9) * mm});
            skLineSegment(sketch, "E398", {"start": v(-23.56, 13.9) * mm, "end": v(-23.56, 14.02) * mm});
            skLineSegment(sketch, "E399", {"start": v(-23.56, 14.02) * mm, "end": v(-23.32, 14.37) * mm});
            skLineSegment(sketch, "E400", {"start": v(-23.32, 14.37) * mm, "end": v(-23.28, 14.4) * mm});
            skLineSegment(sketch, "E401", {"start": v(-23.28, 14.4) * mm, "end": v(-23.24, 14.42) * mm});
            skLineSegment(sketch, "E402", {"start": v(-23.24, 14.42) * mm, "end": v(-22.75, 14.42) * mm});
            skLineSegment(sketch, "E403", {"start": v(-22.75, 14.42) * mm, "end": v(-22.7, 14.4) * mm});
            skLineSegment(sketch, "E404", {"start": v(-22.7, 14.4) * mm, "end": v(-22.66, 14.37) * mm});
            skLineSegment(sketch, "E405", {"start": v(-22.66, 14.37) * mm, "end": v(-22.42, 14.01) * mm});
            skLineSegment(sketch, "E406", {"start": v(-22.42, 14.01) * mm, "end": v(-22.42, 13.9) * mm});
            skLineSegment(sketch, "E407", {"start": v(-22.04, 12.44) * mm, "end": v(-22.04, 12.31) * mm});
            skLineSegment(sketch, "E408", {"start": v(-22.04, 12.31) * mm, "end": v(-22.28, 11.97) * mm});
            skLineSegment(sketch, "E409", {"start": v(-22.28, 11.97) * mm, "end": v(-22.33, 11.94) * mm});
            skLineSegment(sketch, "E410", {"start": v(-22.33, 11.94) * mm, "end": v(-22.37, 11.92) * mm});
            skLineSegment(sketch, "E411", {"start": v(-22.37, 11.92) * mm, "end": v(-22.86, 11.92) * mm});
            skLineSegment(sketch, "E412", {"start": v(-22.86, 11.92) * mm, "end": v(-22.9, 11.94) * mm});
            skLineSegment(sketch, "E413", {"start": v(-22.9, 11.94) * mm, "end": v(-22.94, 11.97) * mm});
            skLineSegment(sketch, "E414", {"start": v(-22.94, 11.97) * mm, "end": v(-23.18, 12.32) * mm});
            skLineSegment(sketch, "E415", {"start": v(-23.18, 12.32) * mm, "end": v(-23.18, 12.44) * mm});
            skLineSegment(sketch, "E416", {"start": v(-23.18, 12.44) * mm, "end": v(-23.18, 12.56) * mm});
            skLineSegment(sketch, "E417", {"start": v(-23.18, 12.56) * mm, "end": v(-22.94, 12.9) * mm});
            skLineSegment(sketch, "E418", {"start": v(-22.94, 12.9) * mm, "end": v(-22.9, 12.93) * mm});
            skLineSegment(sketch, "E419", {"start": v(-22.9, 12.93) * mm, "end": v(-22.86, 12.96) * mm});
            skLineSegment(sketch, "E420", {"start": v(-22.86, 12.96) * mm, "end": v(-22.37, 12.96) * mm});
            skLineSegment(sketch, "E421", {"start": v(-22.37, 12.96) * mm, "end": v(-22.33, 12.93) * mm});
            skLineSegment(sketch, "E422", {"start": v(-22.33, 12.93) * mm, "end": v(-22.28, 12.9) * mm});
            skLineSegment(sketch, "E423", {"start": v(-22.28, 12.9) * mm, "end": v(-22.04, 12.55) * mm});
            skLineSegment(sketch, "E424", {"start": v(-22.04, 12.55) * mm, "end": v(-22.04, 12.44) * mm});
            skLineSegment(sketch, "E425", {"start": v(5.26, 12.63) * mm, "end": v(5.26, 12.5) * mm});
            skLineSegment(sketch, "E426", {"start": v(5.26, 12.5) * mm, "end": v(5.02, 12.16) * mm});
            skLineSegment(sketch, "E427", {"start": v(5.02, 12.16) * mm, "end": v(4.98, 12.13) * mm});
            skLineSegment(sketch, "E428", {"start": v(4.98, 12.13) * mm, "end": v(4.93, 12.1) * mm});
            skLineSegment(sketch, "E429", {"start": v(4.93, 12.1) * mm, "end": v(4.45, 12.1) * mm});
            skLineSegment(sketch, "E430", {"start": v(4.45, 12.1) * mm, "end": v(4.4, 12.13) * mm});
            skLineSegment(sketch, "E431", {"start": v(4.4, 12.13) * mm, "end": v(4.36, 12.16) * mm});
            skLineSegment(sketch, "E432", {"start": v(4.36, 12.16) * mm, "end": v(4.12, 12.5) * mm});
            skLineSegment(sketch, "E433", {"start": v(4.12, 12.5) * mm, "end": v(4.12, 12.63) * mm});
            skLineSegment(sketch, "E434", {"start": v(4.12, 12.63) * mm, "end": v(4.12, 12.75) * mm});
            skLineSegment(sketch, "E435", {"start": v(4.12, 12.75) * mm, "end": v(4.36, 13.1) * mm});
            skLineSegment(sketch, "E436", {"start": v(4.36, 13.1) * mm, "end": v(4.4, 13.12) * mm});
            skLineSegment(sketch, "E437", {"start": v(4.4, 13.12) * mm, "end": v(4.45, 13.15) * mm});
            skLineSegment(sketch, "E438", {"start": v(4.45, 13.15) * mm, "end": v(4.93, 13.15) * mm});
            skLineSegment(sketch, "E439", {"start": v(4.93, 13.15) * mm, "end": v(4.98, 13.12) * mm});
            skLineSegment(sketch, "E440", {"start": v(4.98, 13.12) * mm, "end": v(5.02, 13.1) * mm});
            skLineSegment(sketch, "E441", {"start": v(5.02, 13.1) * mm, "end": v(5.26, 12.74) * mm});
            skLineSegment(sketch, "E442", {"start": v(5.26, 12.74) * mm, "end": v(5.26, 12.63) * mm});
            skLineSegment(sketch, "E443", {"start": v(0.87, 17.98) * mm, "end": v(0.87, 17.86) * mm});
            skLineSegment(sketch, "E444", {"start": v(0.87, 17.86) * mm, "end": v(0.63, 17.52) * mm});
            skLineSegment(sketch, "E445", {"start": v(0.63, 17.52) * mm, "end": v(0.58, 17.49) * mm});
            skLineSegment(sketch, "E446", {"start": v(0.58, 17.49) * mm, "end": v(0.54, 17.47) * mm});
            skLineSegment(sketch, "E447", {"start": v(0.54, 17.47) * mm, "end": v(0.06, 17.47) * mm});
            skLineSegment(sketch, "E448", {"start": v(0.06, 17.47) * mm, "end": v(0.01, 17.49) * mm});
            skLineSegment(sketch, "E449", {"start": v(0.01, 17.49) * mm, "end": v(-0.03, 17.52) * mm});
            skLineSegment(sketch, "E450", {"start": v(-0.03, 17.52) * mm, "end": v(-0.27, 17.87) * mm});
            skLineSegment(sketch, "E451", {"start": v(-0.27, 17.87) * mm, "end": v(-0.27, 17.98) * mm});
            skLineSegment(sketch, "E452", {"start": v(-0.27, 17.98) * mm, "end": v(-0.27, 18.1) * mm});
            skLineSegment(sketch, "E453", {"start": v(-0.27, 18.1) * mm, "end": v(-0.03, 18.45) * mm});
            skLineSegment(sketch, "E454", {"start": v(-0.03, 18.45) * mm, "end": v(0.01, 18.48) * mm});
            skLineSegment(sketch, "E455", {"start": v(0.01, 18.48) * mm, "end": v(0.06, 18.5) * mm});
            skLineSegment(sketch, "E456", {"start": v(0.06, 18.5) * mm, "end": v(0.54, 18.5) * mm});
            skLineSegment(sketch, "E457", {"start": v(0.54, 18.5) * mm, "end": v(0.58, 18.48) * mm});
            skLineSegment(sketch, "E458", {"start": v(0.58, 18.48) * mm, "end": v(0.63, 18.45) * mm});
            skLineSegment(sketch, "E459", {"start": v(0.63, 18.45) * mm, "end": v(0.87, 18.1) * mm});
            skLineSegment(sketch, "E460", {"start": v(0.87, 18.1) * mm, "end": v(0.87, 17.98) * mm});
            skLineSegment(sketch, "E461", {"start": v(-1.21, 19.93) * mm, "end": v(-1.21, 19.8) * mm});
            skLineSegment(sketch, "E462", {"start": v(-1.21, 19.8) * mm, "end": v(-1.46, 19.46) * mm});
            skLineSegment(sketch, "E463", {"start": v(-1.46, 19.46) * mm, "end": v(-1.5, 19.43) * mm});
            skLineSegment(sketch, "E464", {"start": v(-1.5, 19.43) * mm, "end": v(-1.54, 19.4) * mm});
            skLineSegment(sketch, "E465", {"start": v(-1.54, 19.4) * mm, "end": v(-2.03, 19.4) * mm});
            skLineSegment(sketch, "E466", {"start": v(-2.03, 19.4) * mm, "end": v(-2.07, 19.43) * mm});
            skLineSegment(sketch, "E467", {"start": v(-2.07, 19.43) * mm, "end": v(-2.12, 19.46) * mm});
            skLineSegment(sketch, "E468", {"start": v(-2.12, 19.46) * mm, "end": v(-2.36, 19.81) * mm});
            skLineSegment(sketch, "E469", {"start": v(-2.36, 19.81) * mm, "end": v(-2.36, 19.93) * mm});
            skLineSegment(sketch, "E470", {"start": v(-2.36, 19.93) * mm, "end": v(-2.36, 20.05) * mm});
            skLineSegment(sketch, "E471", {"start": v(-2.36, 20.05) * mm, "end": v(-2.12, 20.4) * mm});
            skLineSegment(sketch, "E472", {"start": v(-2.12, 20.4) * mm, "end": v(-2.07, 20.42) * mm});
            skLineSegment(sketch, "E473", {"start": v(-2.07, 20.42) * mm, "end": v(-2.03, 20.45) * mm});
            skLineSegment(sketch, "E474", {"start": v(-2.03, 20.45) * mm, "end": v(-1.54, 20.45) * mm});
            skLineSegment(sketch, "E475", {"start": v(-1.54, 20.45) * mm, "end": v(-1.5, 20.42) * mm});
            skLineSegment(sketch, "E476", {"start": v(-1.5, 20.42) * mm, "end": v(-1.46, 20.4) * mm});
            skLineSegment(sketch, "E477", {"start": v(-1.46, 20.4) * mm, "end": v(-1.21, 20.05) * mm});
            skLineSegment(sketch, "E478", {"start": v(-1.21, 20.05) * mm, "end": v(-1.21, 19.93) * mm});
            skLineSegment(sketch, "E479", {"start": v(2.79, 21.77) * mm, "end": v(2.79, 21.65) * mm});
            skLineSegment(sketch, "E480", {"start": v(2.79, 21.65) * mm, "end": v(2.54, 21.3) * mm});
            skLineSegment(sketch, "E481", {"start": v(2.54, 21.3) * mm, "end": v(2.5, 21.28) * mm});
            skLineSegment(sketch, "E482", {"start": v(2.5, 21.28) * mm, "end": v(2.46, 21.25) * mm});
            skLineSegment(sketch, "E483", {"start": v(2.46, 21.25) * mm, "end": v(1.97, 21.25) * mm});
            skLineSegment(sketch, "E484", {"start": v(1.97, 21.25) * mm, "end": v(1.93, 21.28) * mm});
            skLineSegment(sketch, "E485", {"start": v(1.93, 21.28) * mm, "end": v(1.88, 21.3) * mm});
            skLineSegment(sketch, "E486", {"start": v(1.88, 21.3) * mm, "end": v(1.64, 21.65) * mm});
            skLineSegment(sketch, "E487", {"start": v(1.64, 21.65) * mm, "end": v(1.64, 21.77) * mm});
            skLineSegment(sketch, "E488", {"start": v(1.64, 21.77) * mm, "end": v(1.64, 21.9) * mm});
            skLineSegment(sketch, "E489", {"start": v(1.64, 21.9) * mm, "end": v(1.88, 22.24) * mm});
            skLineSegment(sketch, "E490", {"start": v(1.88, 22.24) * mm, "end": v(1.93, 22.26) * mm});
            skLineSegment(sketch, "E491", {"start": v(1.93, 22.26) * mm, "end": v(1.97, 22.3) * mm});
            skLineSegment(sketch, "E492", {"start": v(1.97, 22.3) * mm, "end": v(2.46, 22.3) * mm});
            skLineSegment(sketch, "E493", {"start": v(2.46, 22.3) * mm, "end": v(2.5, 22.26) * mm});
            skLineSegment(sketch, "E494", {"start": v(2.5, 22.26) * mm, "end": v(2.54, 22.24) * mm});
            skLineSegment(sketch, "E495", {"start": v(2.54, 22.24) * mm, "end": v(2.79, 21.89) * mm});
            skLineSegment(sketch, "E496", {"start": v(2.79, 21.89) * mm, "end": v(2.79, 21.77) * mm});
            skLineSegment(sketch, "E497", {"start": v(12.63, 12.88) * mm, "end": v(12.63, 12.76) * mm});
            skLineSegment(sketch, "E498", {"start": v(12.63, 12.76) * mm, "end": v(12.39, 12.41) * mm});
            skLineSegment(sketch, "E499", {"start": v(12.39, 12.41) * mm, "end": v(12.34, 12.38) * mm});
            skLineSegment(sketch, "E500", {"start": v(12.34, 12.38) * mm, "end": v(12.3, 12.36) * mm});
            skLineSegment(sketch, "E501", {"start": v(12.3, 12.36) * mm, "end": v(11.82, 12.36) * mm});
            skLineSegment(sketch, "E502", {"start": v(11.82, 12.36) * mm, "end": v(11.77, 12.38) * mm});
            skLineSegment(sketch, "E503", {"start": v(11.77, 12.38) * mm, "end": v(11.73, 12.41) * mm});
            skLineSegment(sketch, "E504", {"start": v(11.73, 12.41) * mm, "end": v(11.49, 12.76) * mm});
            skLineSegment(sketch, "E505", {"start": v(11.49, 12.76) * mm, "end": v(11.49, 12.88) * mm});
            skLineSegment(sketch, "E506", {"start": v(11.49, 12.88) * mm, "end": v(11.49, 13) * mm});
            skLineSegment(sketch, "E507", {"start": v(11.49, 13) * mm, "end": v(11.73, 13.35) * mm});
            skLineSegment(sketch, "E508", {"start": v(11.73, 13.35) * mm, "end": v(11.77, 13.38) * mm});
            skLineSegment(sketch, "E509", {"start": v(11.77, 13.38) * mm, "end": v(11.82, 13.4) * mm});
            skLineSegment(sketch, "E510", {"start": v(11.82, 13.4) * mm, "end": v(12.3, 13.4) * mm});
            skLineSegment(sketch, "E511", {"start": v(12.3, 13.4) * mm, "end": v(12.34, 13.38) * mm});
            skLineSegment(sketch, "E512", {"start": v(12.34, 13.38) * mm, "end": v(12.39, 13.35) * mm});
            skLineSegment(sketch, "E513", {"start": v(12.39, 13.35) * mm, "end": v(12.63, 13) * mm});
            skLineSegment(sketch, "E514", {"start": v(12.63, 13) * mm, "end": v(12.63, 12.88) * mm});
            skLineSegment(sketch, "E515", {"start": v(8.44, 22.79) * mm, "end": v(8.44, 22.66) * mm});
            skLineSegment(sketch, "E516", {"start": v(8.44, 22.66) * mm, "end": v(8.2, 22.32) * mm});
            skLineSegment(sketch, "E517", {"start": v(8.2, 22.32) * mm, "end": v(8.15, 22.3) * mm});
            skLineSegment(sketch, "E518", {"start": v(8.15, 22.3) * mm, "end": v(8.1, 22.27) * mm});
            skLineSegment(sketch, "E519", {"start": v(8.1, 22.27) * mm, "end": v(7.63, 22.27) * mm});
            skLineSegment(sketch, "E520", {"start": v(7.63, 22.27) * mm, "end": v(7.58, 22.3) * mm});
            skLineSegment(sketch, "E521", {"start": v(7.58, 22.3) * mm, "end": v(7.54, 22.32) * mm});
            skLineSegment(sketch, "E522", {"start": v(7.54, 22.32) * mm, "end": v(7.3, 22.67) * mm});
            skLineSegment(sketch, "E523", {"start": v(7.3, 22.67) * mm, "end": v(7.3, 22.79) * mm});
            skLineSegment(sketch, "E524", {"start": v(7.3, 22.79) * mm, "end": v(7.3, 22.9) * mm});
            skLineSegment(sketch, "E525", {"start": v(7.3, 22.9) * mm, "end": v(7.54, 23.26) * mm});
            skLineSegment(sketch, "E526", {"start": v(7.54, 23.26) * mm, "end": v(7.58, 23.28) * mm});
            skLineSegment(sketch, "E527", {"start": v(7.58, 23.28) * mm, "end": v(7.63, 23.3) * mm});
            skLineSegment(sketch, "E528", {"start": v(7.63, 23.3) * mm, "end": v(8.1, 23.3) * mm});
            skLineSegment(sketch, "E529", {"start": v(8.1, 23.3) * mm, "end": v(8.15, 23.28) * mm});
            skLineSegment(sketch, "E530", {"start": v(8.15, 23.28) * mm, "end": v(8.2, 23.26) * mm});
            skLineSegment(sketch, "E531", {"start": v(8.2, 23.26) * mm, "end": v(8.44, 22.9) * mm});
            skLineSegment(sketch, "E532", {"start": v(8.44, 22.9) * mm, "end": v(8.44, 22.79) * mm});
            skLineSegment(sketch, "E533", {"start": v(1, 23.3) * mm, "end": v(1, 23.17) * mm});
            skLineSegment(sketch, "E534", {"start": v(1, 23.17) * mm, "end": v(0.77, 22.82) * mm});
            skLineSegment(sketch, "E535", {"start": v(0.77, 22.82) * mm, "end": v(0.72, 22.8) * mm});
            skLineSegment(sketch, "E536", {"start": v(0.72, 22.8) * mm, "end": v(0.68, 22.77) * mm});
            skLineSegment(sketch, "E537", {"start": v(0.68, 22.77) * mm, "end": v(0.2, 22.77) * mm});
            skLineSegment(sketch, "E538", {"start": v(0.2, 22.77) * mm, "end": v(0.15, 22.8) * mm});
            skLineSegment(sketch, "E539", {"start": v(0.15, 22.8) * mm, "end": v(0.1, 22.82) * mm});
            skLineSegment(sketch, "E540", {"start": v(0.1, 22.82) * mm, "end": v(-0.13, 23.18) * mm});
            skLineSegment(sketch, "E541", {"start": v(-0.13, 23.18) * mm, "end": v(-0.13, 23.3) * mm});
            skLineSegment(sketch, "E542", {"start": v(-0.13, 23.3) * mm, "end": v(-0.13, 23.42) * mm});
            skLineSegment(sketch, "E543", {"start": v(-0.13, 23.42) * mm, "end": v(0.1, 23.76) * mm});
            skLineSegment(sketch, "E544", {"start": v(0.1, 23.76) * mm, "end": v(0.15, 23.79) * mm});
            skLineSegment(sketch, "E545", {"start": v(0.15, 23.79) * mm, "end": v(0.2, 23.82) * mm});
            skLineSegment(sketch, "E546", {"start": v(0.2, 23.82) * mm, "end": v(0.68, 23.82) * mm});
            skLineSegment(sketch, "E547", {"start": v(0.68, 23.82) * mm, "end": v(0.72, 23.79) * mm});
            skLineSegment(sketch, "E548", {"start": v(0.72, 23.79) * mm, "end": v(0.77, 23.76) * mm});
            skLineSegment(sketch, "E549", {"start": v(0.77, 23.76) * mm, "end": v(1, 23.41) * mm});
            skLineSegment(sketch, "E550", {"start": v(1, 23.41) * mm, "end": v(1, 23.3) * mm});
            skLineSegment(sketch, "E551", {"start": v(-3.06, 17.83) * mm, "end": v(-3.06, 17.71) * mm});
            skLineSegment(sketch, "E552", {"start": v(-3.06, 17.71) * mm, "end": v(-3.3, 17.36) * mm});
            skLineSegment(sketch, "E553", {"start": v(-3.3, 17.36) * mm, "end": v(-3.34, 17.34) * mm});
            skLineSegment(sketch, "E554", {"start": v(-3.34, 17.34) * mm, "end": v(-3.39, 17.31) * mm});
            skLineSegment(sketch, "E555", {"start": v(-3.39, 17.31) * mm, "end": v(-3.87, 17.31) * mm});
            skLineSegment(sketch, "E556", {"start": v(-3.87, 17.31) * mm, "end": v(-3.91, 17.34) * mm});
            skLineSegment(sketch, "E557", {"start": v(-3.91, 17.34) * mm, "end": v(-3.96, 17.36) * mm});
            skLineSegment(sketch, "E558", {"start": v(-3.96, 17.36) * mm, "end": v(-4.2, 17.72) * mm});
            skLineSegment(sketch, "E559", {"start": v(-4.2, 17.72) * mm, "end": v(-4.2, 17.83) * mm});
            skLineSegment(sketch, "E560", {"start": v(-4.2, 17.83) * mm, "end": v(-4.2, 17.96) * mm});
            skLineSegment(sketch, "E561", {"start": v(-4.2, 17.96) * mm, "end": v(-3.96, 18.3) * mm});
            skLineSegment(sketch, "E562", {"start": v(-3.96, 18.3) * mm, "end": v(-3.91, 18.33) * mm});
            skLineSegment(sketch, "E563", {"start": v(-3.91, 18.33) * mm, "end": v(-3.87, 18.35) * mm});
            skLineSegment(sketch, "E564", {"start": v(-3.87, 18.35) * mm, "end": v(-3.39, 18.35) * mm});
            skLineSegment(sketch, "E565", {"start": v(-3.39, 18.35) * mm, "end": v(-3.34, 18.33) * mm});
            skLineSegment(sketch, "E566", {"start": v(-3.34, 18.33) * mm, "end": v(-3.3, 18.3) * mm});
            skLineSegment(sketch, "E567", {"start": v(-3.3, 18.3) * mm, "end": v(-3.06, 17.95) * mm});
            skLineSegment(sketch, "E568", {"start": v(-3.06, 17.95) * mm, "end": v(-3.06, 17.83) * mm});
            skLineSegment(sketch, "E569", {"start": v(-20.52, 16.18) * mm, "end": v(-20.52, 16.06) * mm});
            skLineSegment(sketch, "E570", {"start": v(-20.52, 16.06) * mm, "end": v(-20.76, 15.71) * mm});
            skLineSegment(sketch, "E571", {"start": v(-20.76, 15.71) * mm, "end": v(-20.8, 15.69) * mm});
            skLineSegment(sketch, "E572", {"start": v(-20.8, 15.69) * mm, "end": v(-20.85, 15.66) * mm});
            skLineSegment(sketch, "E573", {"start": v(-20.85, 15.66) * mm, "end": v(-21.33, 15.66) * mm});
            skLineSegment(sketch, "E574", {"start": v(-21.33, 15.66) * mm, "end": v(-21.38, 15.69) * mm});
            skLineSegment(sketch, "E575", {"start": v(-21.38, 15.69) * mm, "end": v(-21.42, 15.71) * mm});
            skLineSegment(sketch, "E576", {"start": v(-21.42, 15.71) * mm, "end": v(-21.66, 16.07) * mm});
            skLineSegment(sketch, "E577", {"start": v(-21.66, 16.07) * mm, "end": v(-21.66, 16.18) * mm});
            skLineSegment(sketch, "E578", {"start": v(-21.66, 16.18) * mm, "end": v(-21.66, 16.3) * mm});
            skLineSegment(sketch, "E579", {"start": v(-21.66, 16.3) * mm, "end": v(-21.42, 16.65) * mm});
            skLineSegment(sketch, "E580", {"start": v(-21.42, 16.65) * mm, "end": v(-21.38, 16.68) * mm});
            skLineSegment(sketch, "E581", {"start": v(-21.38, 16.68) * mm, "end": v(-21.33, 16.7) * mm});
            skLineSegment(sketch, "E582", {"start": v(-21.33, 16.7) * mm, "end": v(-20.85, 16.7) * mm});
            skLineSegment(sketch, "E583", {"start": v(-20.85, 16.7) * mm, "end": v(-20.8, 16.68) * mm});
            skLineSegment(sketch, "E584", {"start": v(-20.8, 16.68) * mm, "end": v(-20.76, 16.65) * mm});
            skLineSegment(sketch, "E585", {"start": v(-20.76, 16.65) * mm, "end": v(-20.52, 16.3) * mm});
            skLineSegment(sketch, "E586", {"start": v(-20.52, 16.3) * mm, "end": v(-20.52, 16.18) * mm});
            skLineSegment(sketch, "E587", {"start": v(-11.88, 14.66) * mm, "end": v(-11.88, 14.54) * mm});
            skLineSegment(sketch, "E588", {"start": v(-11.88, 14.54) * mm, "end": v(-12.12, 14.19) * mm});
            skLineSegment(sketch, "E589", {"start": v(-12.12, 14.19) * mm, "end": v(-12.17, 14.16) * mm});
            skLineSegment(sketch, "E590", {"start": v(-12.17, 14.16) * mm, "end": v(-12.21, 14.14) * mm});
            skLineSegment(sketch, "E591", {"start": v(-12.21, 14.14) * mm, "end": v(-12.7, 14.14) * mm});
            skLineSegment(sketch, "E592", {"start": v(-12.7, 14.14) * mm, "end": v(-12.74, 14.16) * mm});
            skLineSegment(sketch, "E593", {"start": v(-12.74, 14.16) * mm, "end": v(-12.78, 14.19) * mm});
            skLineSegment(sketch, "E594", {"start": v(-12.78, 14.19) * mm, "end": v(-13.02, 14.54) * mm});
            skLineSegment(sketch, "E595", {"start": v(-13.02, 14.54) * mm, "end": v(-13.02, 14.66) * mm});
            skLineSegment(sketch, "E596", {"start": v(-13.02, 14.66) * mm, "end": v(-13.02, 14.78) * mm});
            skLineSegment(sketch, "E597", {"start": v(-13.02, 14.78) * mm, "end": v(-12.78, 15.13) * mm});
            skLineSegment(sketch, "E598", {"start": v(-12.78, 15.13) * mm, "end": v(-12.74, 15.15) * mm});
            skLineSegment(sketch, "E599", {"start": v(-12.74, 15.15) * mm, "end": v(-12.7, 15.18) * mm});
            skLineSegment(sketch, "E600", {"start": v(-12.7, 15.18) * mm, "end": v(-12.21, 15.18) * mm});
            skLineSegment(sketch, "E601", {"start": v(-12.21, 15.18) * mm, "end": v(-12.17, 15.15) * mm});
            skLineSegment(sketch, "E602", {"start": v(-12.17, 15.15) * mm, "end": v(-12.12, 15.13) * mm});
            skLineSegment(sketch, "E603", {"start": v(-12.12, 15.13) * mm, "end": v(-11.88, 14.78) * mm});
            skLineSegment(sketch, "E604", {"start": v(-11.88, 14.78) * mm, "end": v(-11.88, 14.66) * mm});
            skLineSegment(sketch, "E605", {"start": v(-7.3, 17.13) * mm, "end": v(-7.3, 17.01) * mm});
            skLineSegment(sketch, "E606", {"start": v(-7.3, 17.01) * mm, "end": v(-7.55, 16.67) * mm});
            skLineSegment(sketch, "E607", {"start": v(-7.55, 16.67) * mm, "end": v(-7.6, 16.64) * mm});
            skLineSegment(sketch, "E608", {"start": v(-7.6, 16.64) * mm, "end": v(-7.64, 16.62) * mm});
            skLineSegment(sketch, "E609", {"start": v(-7.64, 16.62) * mm, "end": v(-8.12, 16.62) * mm});
            skLineSegment(sketch, "E610", {"start": v(-8.12, 16.62) * mm, "end": v(-8.17, 16.64) * mm});
            skLineSegment(sketch, "E611", {"start": v(-8.17, 16.64) * mm, "end": v(-8.21, 16.67) * mm});
            skLineSegment(sketch, "E612", {"start": v(-8.21, 16.67) * mm, "end": v(-8.45, 17.02) * mm});
            skLineSegment(sketch, "E613", {"start": v(-8.45, 17.02) * mm, "end": v(-8.45, 17.13) * mm});
            skLineSegment(sketch, "E614", {"start": v(-8.45, 17.13) * mm, "end": v(-8.45, 17.26) * mm});
            skLineSegment(sketch, "E615", {"start": v(-8.45, 17.26) * mm, "end": v(-8.21, 17.6) * mm});
            skLineSegment(sketch, "E616", {"start": v(-8.21, 17.6) * mm, "end": v(-8.17, 17.63) * mm});
            skLineSegment(sketch, "E617", {"start": v(-8.17, 17.63) * mm, "end": v(-8.12, 17.66) * mm});
            skLineSegment(sketch, "E618", {"start": v(-8.12, 17.66) * mm, "end": v(-7.64, 17.66) * mm});
            skLineSegment(sketch, "E619", {"start": v(-7.64, 17.66) * mm, "end": v(-7.6, 17.63) * mm});
            skLineSegment(sketch, "E620", {"start": v(-7.6, 17.63) * mm, "end": v(-7.55, 17.6) * mm});
            skLineSegment(sketch, "E621", {"start": v(-7.55, 17.6) * mm, "end": v(-7.3, 17.25) * mm});
            skLineSegment(sketch, "E622", {"start": v(-7.3, 17.25) * mm, "end": v(-7.3, 17.13) * mm});
            skLineSegment(sketch, "E623", {"start": v(-10.86, 18.98) * mm, "end": v(-10.86, 18.85) * mm});
            skLineSegment(sketch, "E624", {"start": v(-10.86, 18.85) * mm, "end": v(-11.1, 18.5) * mm});
            skLineSegment(sketch, "E625", {"start": v(-11.1, 18.5) * mm, "end": v(-11.15, 18.48) * mm});
            skLineSegment(sketch, "E626", {"start": v(-11.15, 18.48) * mm, "end": v(-11.2, 18.46) * mm});
            skLineSegment(sketch, "E627", {"start": v(-11.2, 18.46) * mm, "end": v(-11.68, 18.46) * mm});
            skLineSegment(sketch, "E628", {"start": v(-11.68, 18.46) * mm, "end": v(-11.72, 18.48) * mm});
            skLineSegment(sketch, "E629", {"start": v(-11.72, 18.48) * mm, "end": v(-11.77, 18.5) * mm});
            skLineSegment(sketch, "E630", {"start": v(-11.77, 18.5) * mm, "end": v(-12, 18.86) * mm});
            skLineSegment(sketch, "E631", {"start": v(-12, 18.86) * mm, "end": v(-12, 18.98) * mm});
            skLineSegment(sketch, "E632", {"start": v(-12, 18.98) * mm, "end": v(-12, 19.1) * mm});
            skLineSegment(sketch, "E633", {"start": v(-12, 19.1) * mm, "end": v(-11.77, 19.45) * mm});
            skLineSegment(sketch, "E634", {"start": v(-11.77, 19.45) * mm, "end": v(-11.72, 19.47) * mm});
            skLineSegment(sketch, "E635", {"start": v(-11.72, 19.47) * mm, "end": v(-11.68, 19.5) * mm});
            skLineSegment(sketch, "E636", {"start": v(-11.68, 19.5) * mm, "end": v(-11.2, 19.5) * mm});
            skLineSegment(sketch, "E637", {"start": v(-11.2, 19.5) * mm, "end": v(-11.15, 19.47) * mm});
            skLineSegment(sketch, "E638", {"start": v(-11.15, 19.47) * mm, "end": v(-11.1, 19.45) * mm});
            skLineSegment(sketch, "E639", {"start": v(-11.1, 19.45) * mm, "end": v(-10.86, 19.1) * mm});
            skLineSegment(sketch, "E640", {"start": v(-10.86, 19.1) * mm, "end": v(-10.86, 18.98) * mm});
            skLineSegment(sketch, "E641", {"start": v(-6.1, 18.91) * mm, "end": v(-6.1, 18.79) * mm});
            skLineSegment(sketch, "E642", {"start": v(-6.1, 18.79) * mm, "end": v(-6.35, 18.44) * mm});
            skLineSegment(sketch, "E643", {"start": v(-6.35, 18.44) * mm, "end": v(-6.39, 18.42) * mm});
            skLineSegment(sketch, "E644", {"start": v(-6.39, 18.42) * mm, "end": v(-6.43, 18.4) * mm});
            skLineSegment(sketch, "E645", {"start": v(-6.43, 18.4) * mm, "end": v(-6.92, 18.4) * mm});
            skLineSegment(sketch, "E646", {"start": v(-6.92, 18.4) * mm, "end": v(-6.96, 18.42) * mm});
            skLineSegment(sketch, "E647", {"start": v(-6.96, 18.42) * mm, "end": v(-7, 18.44) * mm});
            skLineSegment(sketch, "E648", {"start": v(-7, 18.44) * mm, "end": v(-7.25, 18.8) * mm});
            skLineSegment(sketch, "E649", {"start": v(-7.25, 18.8) * mm, "end": v(-7.25, 18.91) * mm});
            skLineSegment(sketch, "E650", {"start": v(-7.25, 18.91) * mm, "end": v(-7.25, 19.04) * mm});
            skLineSegment(sketch, "E651", {"start": v(-7.25, 19.04) * mm, "end": v(-7, 19.38) * mm});
            skLineSegment(sketch, "E652", {"start": v(-7, 19.38) * mm, "end": v(-6.96, 19.4) * mm});
            skLineSegment(sketch, "E653", {"start": v(-6.96, 19.4) * mm, "end": v(-6.92, 19.43) * mm});
            skLineSegment(sketch, "E654", {"start": v(-6.92, 19.43) * mm, "end": v(-6.43, 19.43) * mm});
            skLineSegment(sketch, "E655", {"start": v(-6.43, 19.43) * mm, "end": v(-6.39, 19.4) * mm});
            skLineSegment(sketch, "E656", {"start": v(-6.39, 19.4) * mm, "end": v(-6.35, 19.38) * mm});
            skLineSegment(sketch, "E657", {"start": v(-6.35, 19.38) * mm, "end": v(-6.1, 19.03) * mm});
            skLineSegment(sketch, "E658", {"start": v(-6.1, 19.03) * mm, "end": v(-6.1, 18.91) * mm});
            skLineSegment(sketch, "E659", {"start": v(13.14, 22.66) * mm, "end": v(13.14, 22.54) * mm});
            skLineSegment(sketch, "E660", {"start": v(13.14, 22.54) * mm, "end": v(12.9, 22.2) * mm});
            skLineSegment(sketch, "E661", {"start": v(12.9, 22.2) * mm, "end": v(12.85, 22.16) * mm});
            skLineSegment(sketch, "E662", {"start": v(12.85, 22.16) * mm, "end": v(12.8, 22.14) * mm});
            skLineSegment(sketch, "E663", {"start": v(12.8, 22.14) * mm, "end": v(12.32, 22.14) * mm});
            skLineSegment(sketch, "E664", {"start": v(12.32, 22.14) * mm, "end": v(12.28, 22.16) * mm});
            skLineSegment(sketch, "E665", {"start": v(12.28, 22.16) * mm, "end": v(12.23, 22.2) * mm});
            skLineSegment(sketch, "E666", {"start": v(12.23, 22.2) * mm, "end": v(12, 22.54) * mm});
            skLineSegment(sketch, "E667", {"start": v(12, 22.54) * mm, "end": v(12, 22.66) * mm});
            skLineSegment(sketch, "E668", {"start": v(12, 22.66) * mm, "end": v(12, 22.78) * mm});
            skLineSegment(sketch, "E669", {"start": v(12, 22.78) * mm, "end": v(12.23, 23.13) * mm});
            skLineSegment(sketch, "E670", {"start": v(12.23, 23.13) * mm, "end": v(12.28, 23.15) * mm});
            skLineSegment(sketch, "E671", {"start": v(12.28, 23.15) * mm, "end": v(12.32, 23.18) * mm});
            skLineSegment(sketch, "E672", {"start": v(12.32, 23.18) * mm, "end": v(12.8, 23.18) * mm});
            skLineSegment(sketch, "E673", {"start": v(12.8, 23.18) * mm, "end": v(12.85, 23.15) * mm});
            skLineSegment(sketch, "E674", {"start": v(12.85, 23.15) * mm, "end": v(12.9, 23.13) * mm});
            skLineSegment(sketch, "E675", {"start": v(12.9, 23.13) * mm, "end": v(13.14, 22.78) * mm});
            skLineSegment(sketch, "E676", {"start": v(13.14, 22.78) * mm, "end": v(13.14, 22.66) * mm});
            skLineSegment(sketch, "E677", {"start": v(-8.64, 22.21) * mm, "end": v(-8.64, 22.1) * mm});
            skLineSegment(sketch, "E678", {"start": v(-8.64, 22.1) * mm, "end": v(-8.88, 21.75) * mm});
            skLineSegment(sketch, "E679", {"start": v(-8.88, 21.75) * mm, "end": v(-8.93, 21.72) * mm});
            skLineSegment(sketch, "E680", {"start": v(-8.93, 21.72) * mm, "end": v(-8.97, 21.7) * mm});
            skLineSegment(sketch, "E681", {"start": v(-8.97, 21.7) * mm, "end": v(-9.46, 21.7) * mm});
            skLineSegment(sketch, "E682", {"start": v(-9.46, 21.7) * mm, "end": v(-9.5, 21.72) * mm});
            skLineSegment(sketch, "E683", {"start": v(-9.5, 21.72) * mm, "end": v(-9.54, 21.75) * mm});
            skLineSegment(sketch, "E684", {"start": v(-9.54, 21.75) * mm, "end": v(-9.79, 22.1) * mm});
            skLineSegment(sketch, "E685", {"start": v(-9.79, 22.1) * mm, "end": v(-9.79, 22.21) * mm});
            skLineSegment(sketch, "E686", {"start": v(-9.79, 22.21) * mm, "end": v(-9.79, 22.34) * mm});
            skLineSegment(sketch, "E687", {"start": v(-9.79, 22.34) * mm, "end": v(-9.54, 22.68) * mm});
            skLineSegment(sketch, "E688", {"start": v(-9.54, 22.68) * mm, "end": v(-9.5, 22.7) * mm});
            skLineSegment(sketch, "E689", {"start": v(-9.5, 22.7) * mm, "end": v(-9.46, 22.73) * mm});
            skLineSegment(sketch, "E690", {"start": v(-9.46, 22.73) * mm, "end": v(-8.97, 22.73) * mm});
            skLineSegment(sketch, "E691", {"start": v(-8.97, 22.73) * mm, "end": v(-8.93, 22.7) * mm});
            skLineSegment(sketch, "E692", {"start": v(-8.93, 22.7) * mm, "end": v(-8.88, 22.68) * mm});
            skLineSegment(sketch, "E693", {"start": v(-8.88, 22.68) * mm, "end": v(-8.64, 22.33) * mm});
            skLineSegment(sketch, "E694", {"start": v(-8.64, 22.33) * mm, "end": v(-8.64, 22.21) * mm});
            skLineSegment(sketch, "E695", {"start": v(-12.2, 21.7) * mm, "end": v(-12.2, 21.58) * mm});
            skLineSegment(sketch, "E696", {"start": v(-12.2, 21.58) * mm, "end": v(-12.44, 21.24) * mm});
            skLineSegment(sketch, "E697", {"start": v(-12.44, 21.24) * mm, "end": v(-12.49, 21.21) * mm});
            skLineSegment(sketch, "E698", {"start": v(-12.49, 21.21) * mm, "end": v(-12.53, 21.19) * mm});
            skLineSegment(sketch, "E699", {"start": v(-12.53, 21.19) * mm, "end": v(-13.01, 21.19) * mm});
            skLineSegment(sketch, "E700", {"start": v(-13.01, 21.19) * mm, "end": v(-13.06, 21.21) * mm});
            skLineSegment(sketch, "E701", {"start": v(-13.06, 21.21) * mm, "end": v(-13.1, 21.24) * mm});
            skLineSegment(sketch, "E702", {"start": v(-13.1, 21.24) * mm, "end": v(-13.34, 21.59) * mm});
            skLineSegment(sketch, "E703", {"start": v(-13.34, 21.59) * mm, "end": v(-13.34, 21.7) * mm});
            skLineSegment(sketch, "E704", {"start": v(-13.34, 21.7) * mm, "end": v(-13.34, 21.83) * mm});
            skLineSegment(sketch, "E705", {"start": v(-13.34, 21.83) * mm, "end": v(-13.1, 22.18) * mm});
            skLineSegment(sketch, "E706", {"start": v(-13.1, 22.18) * mm, "end": v(-13.06, 22.2) * mm});
            skLineSegment(sketch, "E707", {"start": v(-13.06, 22.2) * mm, "end": v(-13.01, 22.23) * mm});
            skLineSegment(sketch, "E708", {"start": v(-13.01, 22.23) * mm, "end": v(-12.53, 22.23) * mm});
            skLineSegment(sketch, "E709", {"start": v(-12.53, 22.23) * mm, "end": v(-12.49, 22.2) * mm});
            skLineSegment(sketch, "E710", {"start": v(-12.49, 22.2) * mm, "end": v(-12.44, 22.18) * mm});
            skLineSegment(sketch, "E711", {"start": v(-12.44, 22.18) * mm, "end": v(-12.2, 21.83) * mm});
            skLineSegment(sketch, "E712", {"start": v(-12.2, 21.83) * mm, "end": v(-12.2, 21.7) * mm});
            skLineSegment(sketch, "E713", {"start": v(-22.17, 21.7) * mm, "end": v(-22.17, 21.58) * mm});
            skLineSegment(sketch, "E714", {"start": v(-22.17, 21.58) * mm, "end": v(-22.41, 21.24) * mm});
            skLineSegment(sketch, "E715", {"start": v(-22.41, 21.24) * mm, "end": v(-22.45, 21.21) * mm});
            skLineSegment(sketch, "E716", {"start": v(-22.45, 21.21) * mm, "end": v(-22.5, 21.19) * mm});
            skLineSegment(sketch, "E717", {"start": v(-22.5, 21.19) * mm, "end": v(-22.98, 21.19) * mm});
            skLineSegment(sketch, "E718", {"start": v(-22.98, 21.19) * mm, "end": v(-23.03, 21.21) * mm});
            skLineSegment(sketch, "E719", {"start": v(-23.03, 21.21) * mm, "end": v(-23.07, 21.24) * mm});
            skLineSegment(sketch, "E720", {"start": v(-23.07, 21.24) * mm, "end": v(-23.31, 21.59) * mm});
            skLineSegment(sketch, "E721", {"start": v(-23.31, 21.59) * mm, "end": v(-23.31, 21.7) * mm});
            skLineSegment(sketch, "E722", {"start": v(-23.31, 21.7) * mm, "end": v(-23.31, 21.83) * mm});
            skLineSegment(sketch, "E723", {"start": v(-23.31, 21.83) * mm, "end": v(-23.07, 22.18) * mm});
            skLineSegment(sketch, "E724", {"start": v(-23.07, 22.18) * mm, "end": v(-23.03, 22.2) * mm});
            skLineSegment(sketch, "E725", {"start": v(-23.03, 22.2) * mm, "end": v(-22.98, 22.23) * mm});
            skLineSegment(sketch, "E726", {"start": v(-22.98, 22.23) * mm, "end": v(-22.5, 22.23) * mm});
            skLineSegment(sketch, "E727", {"start": v(-22.5, 22.23) * mm, "end": v(-22.45, 22.2) * mm});
            skLineSegment(sketch, "E728", {"start": v(-22.45, 22.2) * mm, "end": v(-22.41, 22.18) * mm});
            skLineSegment(sketch, "E729", {"start": v(-22.41, 22.18) * mm, "end": v(-22.17, 21.83) * mm});
            skLineSegment(sketch, "E730", {"start": v(-22.17, 21.83) * mm, "end": v(-22.17, 21.7) * mm});
            skLineSegment(sketch, "E731", {"start": v(-22.04, 19.67) * mm, "end": v(-22.04, 19.55) * mm});
            skLineSegment(sketch, "E732", {"start": v(-22.04, 19.55) * mm, "end": v(-22.28, 19.2) * mm});
            skLineSegment(sketch, "E733", {"start": v(-22.28, 19.2) * mm, "end": v(-22.33, 19.18) * mm});
            skLineSegment(sketch, "E734", {"start": v(-22.33, 19.18) * mm, "end": v(-22.37, 19.15) * mm});
            skLineSegment(sketch, "E735", {"start": v(-22.37, 19.15) * mm, "end": v(-22.86, 19.15) * mm});
            skLineSegment(sketch, "E736", {"start": v(-22.86, 19.15) * mm, "end": v(-22.9, 19.18) * mm});
            skLineSegment(sketch, "E737", {"start": v(-22.9, 19.18) * mm, "end": v(-22.94, 19.2) * mm});
            skLineSegment(sketch, "E738", {"start": v(-22.94, 19.2) * mm, "end": v(-23.18, 19.56) * mm});
            skLineSegment(sketch, "E739", {"start": v(-23.18, 19.56) * mm, "end": v(-23.18, 19.67) * mm});
            skLineSegment(sketch, "E740", {"start": v(-23.18, 19.67) * mm, "end": v(-23.18, 19.8) * mm});
            skLineSegment(sketch, "E741", {"start": v(-23.18, 19.8) * mm, "end": v(-22.94, 20.14) * mm});
            skLineSegment(sketch, "E742", {"start": v(-22.94, 20.14) * mm, "end": v(-22.9, 20.17) * mm});
            skLineSegment(sketch, "E743", {"start": v(-22.9, 20.17) * mm, "end": v(-22.86, 20.2) * mm});
            skLineSegment(sketch, "E744", {"start": v(-22.86, 20.2) * mm, "end": v(-22.37, 20.2) * mm});
            skLineSegment(sketch, "E745", {"start": v(-22.37, 20.2) * mm, "end": v(-22.33, 20.17) * mm});
            skLineSegment(sketch, "E746", {"start": v(-22.33, 20.17) * mm, "end": v(-22.28, 20.14) * mm});
            skLineSegment(sketch, "E747", {"start": v(-22.28, 20.14) * mm, "end": v(-22.04, 19.8) * mm});
            skLineSegment(sketch, "E748", {"start": v(-22.04, 19.8) * mm, "end": v(-22.04, 19.67) * mm});
            skLineSegment(sketch, "E749", {"start": v(-22.3, 23.42) * mm, "end": v(-22.3, 23.3) * mm});
            skLineSegment(sketch, "E750", {"start": v(-22.3, 23.3) * mm, "end": v(-22.54, 22.95) * mm});
            skLineSegment(sketch, "E751", {"start": v(-22.54, 22.95) * mm, "end": v(-22.58, 22.93) * mm});
            skLineSegment(sketch, "E752", {"start": v(-22.58, 22.93) * mm, "end": v(-22.63, 22.9) * mm});
            skLineSegment(sketch, "E753", {"start": v(-22.63, 22.9) * mm, "end": v(-23.1, 22.9) * mm});
            skLineSegment(sketch, "E754", {"start": v(-23.1, 22.9) * mm, "end": v(-23.15, 22.93) * mm});
            skLineSegment(sketch, "E755", {"start": v(-23.15, 22.93) * mm, "end": v(-23.2, 22.95) * mm});
            skLineSegment(sketch, "E756", {"start": v(-23.2, 22.95) * mm, "end": v(-23.44, 23.3) * mm});
            skLineSegment(sketch, "E757", {"start": v(-23.44, 23.3) * mm, "end": v(-23.44, 23.42) * mm});
            skLineSegment(sketch, "E758", {"start": v(-23.44, 23.42) * mm, "end": v(-23.44, 23.55) * mm});
            skLineSegment(sketch, "E759", {"start": v(-23.44, 23.55) * mm, "end": v(-23.2, 23.9) * mm});
            skLineSegment(sketch, "E760", {"start": v(-23.2, 23.9) * mm, "end": v(-23.15, 23.92) * mm});
            skLineSegment(sketch, "E761", {"start": v(-23.15, 23.92) * mm, "end": v(-23.1, 23.94) * mm});
            skLineSegment(sketch, "E762", {"start": v(-23.1, 23.94) * mm, "end": v(-22.63, 23.94) * mm});
            skLineSegment(sketch, "E763", {"start": v(-22.63, 23.94) * mm, "end": v(-22.58, 23.92) * mm});
            skLineSegment(sketch, "E764", {"start": v(-22.58, 23.92) * mm, "end": v(-22.54, 23.9) * mm});
            skLineSegment(sketch, "E765", {"start": v(-22.54, 23.9) * mm, "end": v(-22.3, 23.54) * mm});
            skLineSegment(sketch, "E766", {"start": v(-22.3, 23.54) * mm, "end": v(-22.3, 23.42) * mm});
            skLineSegment(sketch, "E767", {"start": v(-52.06, 15.24) * mm, "end": v(-52.06, 15.05) * mm});
            skLineSegment(sketch, "E768", {"start": v(-52.06, 15.05) * mm, "end": v(-52.26, 14.49) * mm});
            skLineSegment(sketch, "E769", {"start": v(-52.26, 14.49) * mm, "end": v(-52.7, 14) * mm});
            skLineSegment(sketch, "E770", {"start": v(-52.7, 14) * mm, "end": v(-52.8, 13.94) * mm});
            skLineSegment(sketch, "E771", {"start": v(-52.8, 13.94) * mm, "end": v(-52.93, 13.88) * mm});
            skLineSegment(sketch, "E772", {"start": v(-52.93, 13.88) * mm, "end": v(-53.56, 13.74) * mm});
            skLineSegment(sketch, "E773", {"start": v(-53.56, 13.74) * mm, "end": v(-54.2, 13.88) * mm});
            skLineSegment(sketch, "E774", {"start": v(-54.2, 13.88) * mm, "end": v(-54.3, 13.94) * mm});
            skLineSegment(sketch, "E775", {"start": v(-54.3, 13.94) * mm, "end": v(-54.43, 14) * mm});
            skLineSegment(sketch, "E776", {"start": v(-54.43, 14) * mm, "end": v(-54.86, 14.49) * mm});
            skLineSegment(sketch, "E777", {"start": v(-54.86, 14.49) * mm, "end": v(-55.06, 15.05) * mm});
            skLineSegment(sketch, "E778", {"start": v(-55.06, 15.05) * mm, "end": v(-55.06, 15.24) * mm});
            skLineSegment(sketch, "E779", {"start": v(-55.06, 15.24) * mm, "end": v(-55.06, 15.43) * mm});
            skLineSegment(sketch, "E780", {"start": v(-55.06, 15.43) * mm, "end": v(-54.86, 16) * mm});
            skLineSegment(sketch, "E781", {"start": v(-54.86, 16) * mm, "end": v(-54.43, 16.47) * mm});
            skLineSegment(sketch, "E782", {"start": v(-54.43, 16.47) * mm, "end": v(-54.3, 16.54) * mm});
            skLineSegment(sketch, "E783", {"start": v(-54.3, 16.54) * mm, "end": v(-54.2, 16.6) * mm});
            skLineSegment(sketch, "E784", {"start": v(-54.2, 16.6) * mm, "end": v(-53.56, 16.74) * mm});
            skLineSegment(sketch, "E785", {"start": v(-53.56, 16.74) * mm, "end": v(-52.93, 16.6) * mm});
            skLineSegment(sketch, "E786", {"start": v(-52.93, 16.6) * mm, "end": v(-52.8, 16.54) * mm});
            skLineSegment(sketch, "E787", {"start": v(-52.8, 16.54) * mm, "end": v(-52.7, 16.47) * mm});
            skLineSegment(sketch, "E788", {"start": v(-52.7, 16.47) * mm, "end": v(-52.26, 16) * mm});
            skLineSegment(sketch, "E789", {"start": v(-52.26, 16) * mm, "end": v(-52.06, 15.43) * mm});
            skLineSegment(sketch, "E790", {"start": v(-52.06, 15.43) * mm, "end": v(-52.06, 15.24) * mm});
            skLineSegment(sketch, "E791", {"start": v(-52.06, 7.34) * mm, "end": v(-52.06, 7.15) * mm});
            skLineSegment(sketch, "E792", {"start": v(-52.06, 7.15) * mm, "end": v(-52.26, 6.6) * mm});
            skLineSegment(sketch, "E793", {"start": v(-52.26, 6.6) * mm, "end": v(-52.7, 6.1) * mm});
            skLineSegment(sketch, "E794", {"start": v(-52.7, 6.1) * mm, "end": v(-52.8, 6.04) * mm});
            skLineSegment(sketch, "E795", {"start": v(-52.8, 6.04) * mm, "end": v(-52.93, 5.98) * mm});
            skLineSegment(sketch, "E796", {"start": v(-52.93, 5.98) * mm, "end": v(-53.56, 5.84) * mm});
            skLineSegment(sketch, "E797", {"start": v(-53.56, 5.84) * mm, "end": v(-54.2, 5.98) * mm});
            skLineSegment(sketch, "E798", {"start": v(-54.2, 5.98) * mm, "end": v(-54.3, 6.04) * mm});
            skLineSegment(sketch, "E799", {"start": v(-54.3, 6.04) * mm, "end": v(-54.43, 6.1) * mm});
            skLineSegment(sketch, "E800", {"start": v(-54.43, 6.1) * mm, "end": v(-54.86, 6.6) * mm});
            skLineSegment(sketch, "E801", {"start": v(-54.86, 6.6) * mm, "end": v(-55.06, 7.15) * mm});
            skLineSegment(sketch, "E802", {"start": v(-55.06, 7.15) * mm, "end": v(-55.06, 7.34) * mm});
            skLineSegment(sketch, "E803", {"start": v(-55.06, 7.34) * mm, "end": v(-55.06, 7.53) * mm});
            skLineSegment(sketch, "E804", {"start": v(-55.06, 7.53) * mm, "end": v(-54.86, 8.1) * mm});
            skLineSegment(sketch, "E805", {"start": v(-54.86, 8.1) * mm, "end": v(-54.43, 8.57) * mm});
            skLineSegment(sketch, "E806", {"start": v(-54.43, 8.57) * mm, "end": v(-54.3, 8.64) * mm});
            skLineSegment(sketch, "E807", {"start": v(-54.3, 8.64) * mm, "end": v(-54.2, 8.7) * mm});
            skLineSegment(sketch, "E808", {"start": v(-54.2, 8.7) * mm, "end": v(-53.56, 8.84) * mm});
            skLineSegment(sketch, "E809", {"start": v(-53.56, 8.84) * mm, "end": v(-52.93, 8.7) * mm});
            skLineSegment(sketch, "E810", {"start": v(-52.93, 8.7) * mm, "end": v(-52.8, 8.64) * mm});
            skLineSegment(sketch, "E811", {"start": v(-52.8, 8.64) * mm, "end": v(-52.7, 8.57) * mm});
            skLineSegment(sketch, "E812", {"start": v(-52.7, 8.57) * mm, "end": v(-52.26, 8.1) * mm});
            skLineSegment(sketch, "E813", {"start": v(-52.26, 8.1) * mm, "end": v(-52.06, 7.53) * mm});
            skLineSegment(sketch, "E814", {"start": v(-52.06, 7.53) * mm, "end": v(-52.06, 7.34) * mm});
            skLineSegment(sketch, "E815", {"start": v(50.96, 23.26) * mm, "end": v(49.45, 23.26) * mm});
            skLineSegment(sketch, "E816", {"start": v(46.74, 18.16) * mm, "end": v(46.74, 18.06) * mm});
            skLineSegment(sketch, "E817", {"start": v(46.74, 18.06) * mm, "end": v(46.63, 17.76) * mm});
            skLineSegment(sketch, "E818", {"start": v(46.63, 17.76) * mm, "end": v(46.4, 17.5) * mm});
            skLineSegment(sketch, "E819", {"start": v(46.4, 17.5) * mm, "end": v(46.34, 17.47) * mm});
            skLineSegment(sketch, "E820", {"start": v(46.34, 17.47) * mm, "end": v(46.28, 17.43) * mm});
            skLineSegment(sketch, "E821", {"start": v(46.28, 17.43) * mm, "end": v(45.6, 17.43) * mm});
            skLineSegment(sketch, "E822", {"start": v(45.6, 17.43) * mm, "end": v(45.54, 17.47) * mm});
            skLineSegment(sketch, "E823", {"start": v(45.54, 17.47) * mm, "end": v(45.48, 17.5) * mm});
            skLineSegment(sketch, "E824", {"start": v(45.48, 17.5) * mm, "end": v(45.25, 17.76) * mm});
            skLineSegment(sketch, "E825", {"start": v(45.25, 17.76) * mm, "end": v(45.14, 18.06) * mm});
            skLineSegment(sketch, "E826", {"start": v(45.14, 18.06) * mm, "end": v(45.14, 18.16) * mm});
            skLineSegment(sketch, "E827", {"start": v(45.14, 18.16) * mm, "end": v(45.14, 18.26) * mm});
            skLineSegment(sketch, "E828", {"start": v(45.14, 18.26) * mm, "end": v(45.25, 18.56) * mm});
            skLineSegment(sketch, "E829", {"start": v(45.25, 18.56) * mm, "end": v(45.48, 18.82) * mm});
            skLineSegment(sketch, "E830", {"start": v(45.48, 18.82) * mm, "end": v(45.54, 18.85) * mm});
            skLineSegment(sketch, "E831", {"start": v(45.54, 18.85) * mm, "end": v(45.6, 18.9) * mm});
            skLineSegment(sketch, "E832", {"start": v(45.6, 18.9) * mm, "end": v(46.28, 18.9) * mm});
            skLineSegment(sketch, "E833", {"start": v(46.28, 18.9) * mm, "end": v(46.34, 18.85) * mm});
            skLineSegment(sketch, "E834", {"start": v(46.34, 18.85) * mm, "end": v(46.4, 18.82) * mm});
            skLineSegment(sketch, "E835", {"start": v(46.4, 18.82) * mm, "end": v(46.63, 18.56) * mm});
            skLineSegment(sketch, "E836", {"start": v(46.63, 18.56) * mm, "end": v(46.74, 18.26) * mm});
            skLineSegment(sketch, "E837", {"start": v(46.74, 18.26) * mm, "end": v(46.74, 18.16) * mm});
            skLineSegment(sketch, "E838", {"start": v(50.96, 13.06) * mm, "end": v(49.45, 13.06) * mm});
            skLineSegment(sketch, "E839", {"start": v(46.74, 20.66) * mm, "end": v(46.74, 20.56) * mm});
            skLineSegment(sketch, "E840", {"start": v(46.74, 20.56) * mm, "end": v(46.63, 20.26) * mm});
            skLineSegment(sketch, "E841", {"start": v(46.63, 20.26) * mm, "end": v(46.4, 20) * mm});
            skLineSegment(sketch, "E842", {"start": v(46.4, 20) * mm, "end": v(46.34, 19.97) * mm});
            skLineSegment(sketch, "E843", {"start": v(46.34, 19.97) * mm, "end": v(46.28, 19.93) * mm});
            skLineSegment(sketch, "E844", {"start": v(46.28, 19.93) * mm, "end": v(45.6, 19.93) * mm});
            skLineSegment(sketch, "E845", {"start": v(45.6, 19.93) * mm, "end": v(45.54, 19.97) * mm});
            skLineSegment(sketch, "E846", {"start": v(45.54, 19.97) * mm, "end": v(45.48, 20) * mm});
            skLineSegment(sketch, "E847", {"start": v(45.48, 20) * mm, "end": v(45.25, 20.26) * mm});
            skLineSegment(sketch, "E848", {"start": v(45.25, 20.26) * mm, "end": v(45.14, 20.56) * mm});
            skLineSegment(sketch, "E849", {"start": v(45.14, 20.56) * mm, "end": v(45.14, 20.66) * mm});
            skLineSegment(sketch, "E850", {"start": v(45.14, 20.66) * mm, "end": v(45.14, 20.76) * mm});
            skLineSegment(sketch, "E851", {"start": v(45.14, 20.76) * mm, "end": v(45.25, 21.06) * mm});
            skLineSegment(sketch, "E852", {"start": v(45.25, 21.06) * mm, "end": v(45.48, 21.32) * mm});
            skLineSegment(sketch, "E853", {"start": v(45.48, 21.32) * mm, "end": v(45.54, 21.35) * mm});
            skLineSegment(sketch, "E854", {"start": v(45.54, 21.35) * mm, "end": v(45.6, 21.39) * mm});
            skLineSegment(sketch, "E855", {"start": v(45.6, 21.39) * mm, "end": v(46.28, 21.39) * mm});
            skLineSegment(sketch, "E856", {"start": v(46.28, 21.39) * mm, "end": v(46.34, 21.35) * mm});
            skLineSegment(sketch, "E857", {"start": v(46.34, 21.35) * mm, "end": v(46.4, 21.32) * mm});
            skLineSegment(sketch, "E858", {"start": v(46.4, 21.32) * mm, "end": v(46.63, 21.06) * mm});
            skLineSegment(sketch, "E859", {"start": v(46.63, 21.06) * mm, "end": v(46.74, 20.76) * mm});
            skLineSegment(sketch, "E860", {"start": v(46.74, 20.76) * mm, "end": v(46.74, 20.66) * mm});
            skLineSegment(sketch, "E861", {"start": v(21.42, -2.25) * mm, "end": v(21.42, -2.4) * mm});
            skLineSegment(sketch, "E862", {"start": v(21.42, -2.4) * mm, "end": v(21.14, -2.8) * mm});
            skLineSegment(sketch, "E863", {"start": v(21.14, -2.8) * mm, "end": v(21.08, -2.84) * mm});
            skLineSegment(sketch, "E864", {"start": v(21.08, -2.84) * mm, "end": v(21.03, -2.87) * mm});
            skLineSegment(sketch, "E865", {"start": v(21.03, -2.87) * mm, "end": v(20.46, -2.87) * mm});
            skLineSegment(sketch, "E866", {"start": v(20.46, -2.87) * mm, "end": v(20.4, -2.84) * mm});
            skLineSegment(sketch, "E867", {"start": v(20.4, -2.84) * mm, "end": v(20.36, -2.8) * mm});
            skLineSegment(sketch, "E868", {"start": v(20.36, -2.8) * mm, "end": v(20.07, -2.4) * mm});
            skLineSegment(sketch, "E869", {"start": v(20.07, -2.4) * mm, "end": v(20.07, -2.25) * mm});
            skLineSegment(sketch, "E870", {"start": v(20.07, -2.25) * mm, "end": v(20.07, -2.1) * mm});
            skLineSegment(sketch, "E871", {"start": v(20.07, -2.1) * mm, "end": v(20.36, -1.7) * mm});
            skLineSegment(sketch, "E872", {"start": v(20.36, -1.7) * mm, "end": v(20.4, -1.67) * mm});
            skLineSegment(sketch, "E873", {"start": v(20.4, -1.67) * mm, "end": v(20.46, -1.64) * mm});
            skLineSegment(sketch, "E874", {"start": v(20.46, -1.64) * mm, "end": v(21.03, -1.64) * mm});
            skLineSegment(sketch, "E875", {"start": v(21.03, -1.64) * mm, "end": v(21.08, -1.67) * mm});
            skLineSegment(sketch, "E876", {"start": v(21.08, -1.67) * mm, "end": v(21.14, -1.7) * mm});
            skLineSegment(sketch, "E877", {"start": v(21.14, -1.7) * mm, "end": v(21.42, -2.12) * mm});
            skLineSegment(sketch, "E878", {"start": v(21.42, -2.12) * mm, "end": v(21.42, -2.25) * mm});
            skLineSegment(sketch, "E879", {"start": v(-59.45, 13.97) * mm, "end": v(-59.45, 13.95) * mm});
            skLineSegment(sketch, "E880", {"start": v(-59.45, 13.95) * mm, "end": v(-59.5, 13.89) * mm});
            skLineSegment(sketch, "E881", {"start": v(-59.5, 13.89) * mm, "end": v(-59.5, 13.88) * mm});
            skLineSegment(sketch, "E882", {"start": v(-59.5, 13.88) * mm, "end": v(-59.5, 13.88) * mm});
            skLineSegment(sketch, "E883", {"start": v(-59.5, 13.88) * mm, "end": v(-59.6, 13.88) * mm});
            skLineSegment(sketch, "E884", {"start": v(-59.6, 13.88) * mm, "end": v(-59.6, 13.88) * mm});
            skLineSegment(sketch, "E885", {"start": v(-59.6, 13.88) * mm, "end": v(-59.6, 13.89) * mm});
            skLineSegment(sketch, "E886", {"start": v(-59.6, 13.89) * mm, "end": v(-59.65, 13.95) * mm});
            skLineSegment(sketch, "E887", {"start": v(-59.65, 13.95) * mm, "end": v(-59.65, 13.97) * mm});
            skLineSegment(sketch, "E888", {"start": v(-59.65, 13.97) * mm, "end": v(-59.65, 14) * mm});
            skLineSegment(sketch, "E889", {"start": v(-59.65, 14) * mm, "end": v(-59.58, 14.07) * mm});
            skLineSegment(sketch, "E890", {"start": v(-59.58, 14.07) * mm, "end": v(-59.55, 14.07) * mm});
            skLineSegment(sketch, "E891", {"start": v(-59.55, 14.07) * mm, "end": v(-59.53, 14.07) * mm});
            skLineSegment(sketch, "E892", {"start": v(-59.53, 14.07) * mm, "end": v(-59.45, 14) * mm});
            skLineSegment(sketch, "E893", {"start": v(-59.45, 14) * mm, "end": v(-59.45, 13.97) * mm});
            skLineSegment(sketch, "E894", {"start": v(-52.59, 30.02) * mm, "end": v(-52.59, 30) * mm});
            skLineSegment(sketch, "E895", {"start": v(-52.59, 30) * mm, "end": v(-52.63, 29.94) * mm});
            skLineSegment(sketch, "E896", {"start": v(-52.63, 29.94) * mm, "end": v(-52.64, 29.93) * mm});
            skLineSegment(sketch, "E897", {"start": v(-52.64, 29.93) * mm, "end": v(-52.65, 29.93) * mm});
            skLineSegment(sketch, "E898", {"start": v(-52.65, 29.93) * mm, "end": v(-52.74, 29.93) * mm});
            skLineSegment(sketch, "E899", {"start": v(-52.74, 29.93) * mm, "end": v(-52.74, 29.93) * mm});
            skLineSegment(sketch, "E900", {"start": v(-52.74, 29.93) * mm, "end": v(-52.75, 29.94) * mm});
            skLineSegment(sketch, "E901", {"start": v(-52.75, 29.94) * mm, "end": v(-52.8, 30) * mm});
            skLineSegment(sketch, "E902", {"start": v(-52.8, 30) * mm, "end": v(-52.8, 30.02) * mm});
            skLineSegment(sketch, "E903", {"start": v(-52.8, 30.02) * mm, "end": v(-52.8, 30.05) * mm});
            skLineSegment(sketch, "E904", {"start": v(-52.8, 30.05) * mm, "end": v(-52.75, 30.1) * mm});
            skLineSegment(sketch, "E905", {"start": v(-52.75, 30.1) * mm, "end": v(-52.74, 30.11) * mm});
            skLineSegment(sketch, "E906", {"start": v(-52.74, 30.11) * mm, "end": v(-52.74, 30.12) * mm});
            skLineSegment(sketch, "E907", {"start": v(-52.74, 30.12) * mm, "end": v(-52.65, 30.12) * mm});
            skLineSegment(sketch, "E908", {"start": v(-52.65, 30.12) * mm, "end": v(-52.64, 30.11) * mm});
            skLineSegment(sketch, "E909", {"start": v(-52.64, 30.11) * mm, "end": v(-52.63, 30.1) * mm});
            skLineSegment(sketch, "E910", {"start": v(-52.63, 30.1) * mm, "end": v(-52.59, 30.04) * mm});
            skLineSegment(sketch, "E911", {"start": v(-52.59, 30.04) * mm, "end": v(-52.59, 30.02) * mm});
            skLineSegment(sketch, "E912", {"start": v(-31.2, 49.2) * mm, "end": v(-31.2, 49.2) * mm});
            skLineSegment(sketch, "E913", {"start": v(-31.2, 49.2) * mm, "end": v(-31.21, 49.18) * mm});
            skLineSegment(sketch, "E914", {"start": v(-31.21, 49.18) * mm, "end": v(-31.22, 49.18) * mm});
            skLineSegment(sketch, "E915", {"start": v(-31.22, 49.18) * mm, "end": v(-31.22, 49.18) * mm});
            skLineSegment(sketch, "E916", {"start": v(-31.22, 49.18) * mm, "end": v(-31.24, 49.18) * mm});
            skLineSegment(sketch, "E917", {"start": v(-31.24, 49.18) * mm, "end": v(-31.24, 49.18) * mm});
            skLineSegment(sketch, "E918", {"start": v(-31.24, 49.18) * mm, "end": v(-31.25, 49.2) * mm});
            skLineSegment(sketch, "E919", {"start": v(-31.25, 49.2) * mm, "end": v(-31.25, 49.2) * mm});
            skLineSegment(sketch, "E920", {"start": v(-31.25, 49.2) * mm, "end": v(-31.24, 49.22) * mm});
            skLineSegment(sketch, "E921", {"start": v(-31.24, 49.22) * mm, "end": v(-31.24, 49.22) * mm});
            skLineSegment(sketch, "E922", {"start": v(-31.24, 49.22) * mm, "end": v(-31.22, 49.22) * mm});
            skLineSegment(sketch, "E923", {"start": v(-31.22, 49.22) * mm, "end": v(-31.22, 49.22) * mm});
            skLineSegment(sketch, "E924", {"start": v(-31.22, 49.22) * mm, "end": v(-31.21, 49.22) * mm});
            skLineSegment(sketch, "E925", {"start": v(-31.21, 49.22) * mm, "end": v(-31.2, 49.2) * mm});
            skLineSegment(sketch, "E926", {"start": v(-42.18, -49.66) * mm, "end": v(-42.18, -49.67) * mm});
            skLineSegment(sketch, "E927", {"start": v(-42.18, -49.67) * mm, "end": v(-42.19, -49.68) * mm});
            skLineSegment(sketch, "E928", {"start": v(-42.19, -49.68) * mm, "end": v(-42.19, -49.68) * mm});
            skLineSegment(sketch, "E929", {"start": v(-42.19, -49.68) * mm, "end": v(-42.2, -49.68) * mm});
            skLineSegment(sketch, "E930", {"start": v(-42.2, -49.68) * mm, "end": v(-42.21, -49.68) * mm});
            skLineSegment(sketch, "E931", {"start": v(-42.21, -49.68) * mm, "end": v(-42.21, -49.68) * mm});
            skLineSegment(sketch, "E932", {"start": v(-42.21, -49.68) * mm, "end": v(-42.22, -49.68) * mm});
            skLineSegment(sketch, "E933", {"start": v(-42.22, -49.68) * mm, "end": v(-42.23, -49.66) * mm});
            skLineSegment(sketch, "E934", {"start": v(-42.23, -49.66) * mm, "end": v(-42.23, -49.66) * mm});
            skLineSegment(sketch, "E935", {"start": v(-42.23, -49.66) * mm, "end": v(-42.23, -49.65) * mm});
            skLineSegment(sketch, "E936", {"start": v(-42.23, -49.65) * mm, "end": v(-42.22, -49.64) * mm});
            skLineSegment(sketch, "E937", {"start": v(-42.22, -49.64) * mm, "end": v(-42.21, -49.64) * mm});
            skLineSegment(sketch, "E938", {"start": v(-42.21, -49.64) * mm, "end": v(-42.21, -49.64) * mm});
            skLineSegment(sketch, "E939", {"start": v(-42.21, -49.64) * mm, "end": v(-42.2, -49.64) * mm});
            skLineSegment(sketch, "E940", {"start": v(-42.2, -49.64) * mm, "end": v(-42.19, -49.64) * mm});
            skLineSegment(sketch, "E941", {"start": v(-42.19, -49.64) * mm, "end": v(-42.19, -49.64) * mm});
            skLineSegment(sketch, "E942", {"start": v(-42.19, -49.64) * mm, "end": v(-42.18, -49.65) * mm});
            skLineSegment(sketch, "E943", {"start": v(-42.18, -49.65) * mm, "end": v(-42.18, -49.66) * mm});
            skLineSegment(sketch, "E944", {"start": v(-46.24, -45.72) * mm, "end": v(-46.24, -45.74) * mm});
            skLineSegment(sketch, "E945", {"start": v(-46.24, -45.74) * mm, "end": v(-46.29, -45.8) * mm});
            skLineSegment(sketch, "E946", {"start": v(-46.29, -45.8) * mm, "end": v(-46.3, -45.8) * mm});
            skLineSegment(sketch, "E947", {"start": v(-46.3, -45.8) * mm, "end": v(-46.3, -45.8) * mm});
            skLineSegment(sketch, "E948", {"start": v(-46.3, -45.8) * mm, "end": v(-46.39, -45.8) * mm});
            skLineSegment(sketch, "E949", {"start": v(-46.39, -45.8) * mm, "end": v(-46.4, -45.8) * mm});
            skLineSegment(sketch, "E950", {"start": v(-46.4, -45.8) * mm, "end": v(-46.4, -45.8) * mm});
            skLineSegment(sketch, "E951", {"start": v(-46.4, -45.8) * mm, "end": v(-46.45, -45.74) * mm});
            skLineSegment(sketch, "E952", {"start": v(-46.45, -45.74) * mm, "end": v(-46.45, -45.72) * mm});
            skLineSegment(sketch, "E953", {"start": v(-46.45, -45.72) * mm, "end": v(-46.45, -45.7) * mm});
            skLineSegment(sketch, "E954", {"start": v(-46.45, -45.7) * mm, "end": v(-46.4, -45.63) * mm});
            skLineSegment(sketch, "E955", {"start": v(-46.4, -45.63) * mm, "end": v(-46.4, -45.63) * mm});
            skLineSegment(sketch, "E956", {"start": v(-46.4, -45.63) * mm, "end": v(-46.39, -45.62) * mm});
            skLineSegment(sketch, "E957", {"start": v(-46.39, -45.62) * mm, "end": v(-46.3, -45.62) * mm});
            skLineSegment(sketch, "E958", {"start": v(-46.3, -45.62) * mm, "end": v(-46.3, -45.63) * mm});
            skLineSegment(sketch, "E959", {"start": v(-46.3, -45.63) * mm, "end": v(-46.29, -45.63) * mm});
            skLineSegment(sketch, "E960", {"start": v(-46.29, -45.63) * mm, "end": v(-46.24, -45.7) * mm});
            skLineSegment(sketch, "E961", {"start": v(-46.24, -45.7) * mm, "end": v(-46.24, -45.72) * mm});
            skLineSegment(sketch, "E962", {"start": v(16.5, 17.3) * mm, "end": v(16.5, 17.3) * mm});
            skLineSegment(sketch, "E963", {"start": v(16.5, 17.3) * mm, "end": v(16.49, 17.28) * mm});
            skLineSegment(sketch, "E964", {"start": v(16.49, 17.28) * mm, "end": v(16.49, 17.28) * mm});
            skLineSegment(sketch, "E965", {"start": v(16.49, 17.28) * mm, "end": v(16.48, 17.28) * mm});
            skLineSegment(sketch, "E966", {"start": v(16.48, 17.28) * mm, "end": v(16.46, 17.28) * mm});
            skLineSegment(sketch, "E967", {"start": v(16.46, 17.28) * mm, "end": v(16.46, 17.28) * mm});
            skLineSegment(sketch, "E968", {"start": v(16.46, 17.28) * mm, "end": v(16.45, 17.3) * mm});
            skLineSegment(sketch, "E969", {"start": v(16.45, 17.3) * mm, "end": v(16.45, 17.3) * mm});
            skLineSegment(sketch, "E970", {"start": v(16.45, 17.3) * mm, "end": v(16.46, 17.32) * mm});
            skLineSegment(sketch, "E971", {"start": v(16.46, 17.32) * mm, "end": v(16.46, 17.32) * mm});
            skLineSegment(sketch, "E972", {"start": v(16.46, 17.32) * mm, "end": v(16.48, 17.32) * mm});
            skLineSegment(sketch, "E973", {"start": v(16.48, 17.32) * mm, "end": v(16.49, 17.32) * mm});
            skLineSegment(sketch, "E974", {"start": v(16.49, 17.32) * mm, "end": v(16.49, 17.32) * mm});
            skLineSegment(sketch, "E975", {"start": v(16.49, 17.32) * mm, "end": v(16.5, 17.3) * mm});
            skLineSegment(sketch, "E976", {"start": v(15.26, -56.34) * mm, "end": v(15.26, -56.34) * mm});
            skLineSegment(sketch, "E977", {"start": v(15.26, -56.34) * mm, "end": v(15.25, -56.36) * mm});
            skLineSegment(sketch, "E978", {"start": v(15.25, -56.36) * mm, "end": v(15.25, -56.36) * mm});
            skLineSegment(sketch, "E979", {"start": v(15.25, -56.36) * mm, "end": v(15.23, -56.36) * mm});
            skLineSegment(sketch, "E980", {"start": v(15.23, -56.36) * mm, "end": v(15.22, -56.36) * mm});
            skLineSegment(sketch, "E981", {"start": v(15.22, -56.36) * mm, "end": v(15.22, -56.36) * mm});
            skLineSegment(sketch, "E982", {"start": v(15.22, -56.36) * mm, "end": v(15.21, -56.34) * mm});
            skLineSegment(sketch, "E983", {"start": v(15.21, -56.34) * mm, "end": v(15.21, -56.34) * mm});
            skLineSegment(sketch, "E984", {"start": v(15.21, -56.34) * mm, "end": v(15.21, -56.33) * mm});
            skLineSegment(sketch, "E985", {"start": v(15.21, -56.33) * mm, "end": v(15.22, -56.32) * mm});
            skLineSegment(sketch, "E986", {"start": v(15.22, -56.32) * mm, "end": v(15.22, -56.31) * mm});
            skLineSegment(sketch, "E987", {"start": v(15.22, -56.31) * mm, "end": v(15.23, -56.31) * mm});
            skLineSegment(sketch, "E988", {"start": v(15.23, -56.31) * mm, "end": v(15.25, -56.31) * mm});
            skLineSegment(sketch, "E989", {"start": v(15.25, -56.31) * mm, "end": v(15.25, -56.31) * mm});
            skLineSegment(sketch, "E990", {"start": v(15.25, -56.31) * mm, "end": v(15.26, -56.33) * mm});
            skLineSegment(sketch, "E991", {"start": v(15.26, -56.33) * mm, "end": v(15.26, -56.34) * mm});
            skLineSegment(sketch, "E992", {"start": v(53.5, -34.29) * mm, "end": v(53.5, -34.3) * mm});
            skLineSegment(sketch, "E993", {"start": v(53.5, -34.3) * mm, "end": v(53.5, -34.31) * mm});
            skLineSegment(sketch, "E994", {"start": v(53.5, -34.31) * mm, "end": v(53.5, -34.31) * mm});
            skLineSegment(sketch, "E995", {"start": v(53.5, -34.31) * mm, "end": v(53.47, -34.31) * mm});
            skLineSegment(sketch, "E996", {"start": v(53.47, -34.31) * mm, "end": v(53.47, -34.31) * mm});
            skLineSegment(sketch, "E997", {"start": v(53.47, -34.31) * mm, "end": v(53.45, -34.3) * mm});
            skLineSegment(sketch, "E998", {"start": v(53.45, -34.3) * mm, "end": v(53.45, -34.29) * mm});
            skLineSegment(sketch, "E999", {"start": v(53.45, -34.29) * mm, "end": v(53.45, -34.28) * mm});
            skLineSegment(sketch, "E1000", {"start": v(53.45, -34.28) * mm, "end": v(53.47, -34.27) * mm});
            skLineSegment(sketch, "E1001", {"start": v(53.47, -34.27) * mm, "end": v(53.47, -34.27) * mm});
            skLineSegment(sketch, "E1002", {"start": v(53.47, -34.27) * mm, "end": v(53.5, -34.27) * mm});
            skLineSegment(sketch, "E1003", {"start": v(53.5, -34.27) * mm, "end": v(53.5, -34.27) * mm});
            skLineSegment(sketch, "E1004", {"start": v(53.5, -34.27) * mm, "end": v(53.5, -34.28) * mm});
            skLineSegment(sketch, "E1005", {"start": v(53.5, -34.28) * mm, "end": v(53.5, -34.29) * mm});
            skLineSegment(sketch, "E1006", {"start": v(13.63, -40.39) * mm, "end": v(13.63, -40.4) * mm});
            skLineSegment(sketch, "E1007", {"start": v(13.63, -40.4) * mm, "end": v(13.62, -40.4) * mm});
            skLineSegment(sketch, "E1008", {"start": v(13.62, -40.4) * mm, "end": v(13.62, -40.4) * mm});
            skLineSegment(sketch, "E1009", {"start": v(13.62, -40.4) * mm, "end": v(13.61, -40.4) * mm});
            skLineSegment(sketch, "E1010", {"start": v(13.61, -40.4) * mm, "end": v(13.6, -40.4) * mm});
            skLineSegment(sketch, "E1011", {"start": v(13.6, -40.4) * mm, "end": v(13.59, -40.4) * mm});
            skLineSegment(sketch, "E1012", {"start": v(13.59, -40.4) * mm, "end": v(13.59, -40.4) * mm});
            skLineSegment(sketch, "E1013", {"start": v(13.59, -40.4) * mm, "end": v(13.58, -40.4) * mm});
            skLineSegment(sketch, "E1014", {"start": v(13.58, -40.4) * mm, "end": v(13.58, -40.39) * mm});
            skLineSegment(sketch, "E1015", {"start": v(13.58, -40.39) * mm, "end": v(13.58, -40.38) * mm});
            skLineSegment(sketch, "E1016", {"start": v(13.58, -40.38) * mm, "end": v(13.59, -40.36) * mm});
            skLineSegment(sketch, "E1017", {"start": v(13.59, -40.36) * mm, "end": v(13.59, -40.36) * mm});
            skLineSegment(sketch, "E1018", {"start": v(13.59, -40.36) * mm, "end": v(13.6, -40.36) * mm});
            skLineSegment(sketch, "E1019", {"start": v(13.6, -40.36) * mm, "end": v(13.61, -40.36) * mm});
            skLineSegment(sketch, "E1020", {"start": v(13.61, -40.36) * mm, "end": v(13.62, -40.36) * mm});
            skLineSegment(sketch, "E1021", {"start": v(13.62, -40.36) * mm, "end": v(13.62, -40.36) * mm});
            skLineSegment(sketch, "E1022", {"start": v(13.62, -40.36) * mm, "end": v(13.63, -40.38) * mm});
            skLineSegment(sketch, "E1023", {"start": v(13.63, -40.38) * mm, "end": v(13.63, -40.39) * mm});
            skLineSegment(sketch, "E1024", {"start": v(-17.38, 35.33) * mm, "end": v(-17.38, 35.33) * mm});
            skLineSegment(sketch, "E1025", {"start": v(-17.38, 35.33) * mm, "end": v(-17.4, 35.31) * mm});
            skLineSegment(sketch, "E1026", {"start": v(-17.4, 35.31) * mm, "end": v(-17.4, 35.3) * mm});
            skLineSegment(sketch, "E1027", {"start": v(-17.4, 35.3) * mm, "end": v(-17.4, 35.3) * mm});
            skLineSegment(sketch, "E1028", {"start": v(-17.4, 35.3) * mm, "end": v(-17.42, 35.3) * mm});
            skLineSegment(sketch, "E1029", {"start": v(-17.42, 35.3) * mm, "end": v(-17.42, 35.3) * mm});
            skLineSegment(sketch, "E1030", {"start": v(-17.42, 35.3) * mm, "end": v(-17.43, 35.31) * mm});
            skLineSegment(sketch, "E1031", {"start": v(-17.43, 35.31) * mm, "end": v(-17.44, 35.33) * mm});
            skLineSegment(sketch, "E1032", {"start": v(-17.44, 35.33) * mm, "end": v(-17.44, 35.33) * mm});
            skLineSegment(sketch, "E1033", {"start": v(-17.44, 35.33) * mm, "end": v(-17.44, 35.34) * mm});
            skLineSegment(sketch, "E1034", {"start": v(-17.44, 35.34) * mm, "end": v(-17.43, 35.35) * mm});
            skLineSegment(sketch, "E1035", {"start": v(-17.43, 35.35) * mm, "end": v(-17.42, 35.35) * mm});
            skLineSegment(sketch, "E1036", {"start": v(-17.42, 35.35) * mm, "end": v(-17.42, 35.36) * mm});
            skLineSegment(sketch, "E1037", {"start": v(-17.42, 35.36) * mm, "end": v(-17.4, 35.36) * mm});
            skLineSegment(sketch, "E1038", {"start": v(-17.4, 35.36) * mm, "end": v(-17.4, 35.35) * mm});
            skLineSegment(sketch, "E1039", {"start": v(-17.4, 35.35) * mm, "end": v(-17.4, 35.35) * mm});
            skLineSegment(sketch, "E1040", {"start": v(-17.4, 35.35) * mm, "end": v(-17.38, 35.34) * mm});
            skLineSegment(sketch, "E1041", {"start": v(-17.38, 35.34) * mm, "end": v(-17.38, 35.33) * mm});
            skLineSegment(sketch, "E1042", {"start": v(-53.94, -17.27) * mm, "end": v(-53.94, -17.28) * mm});
            skLineSegment(sketch, "E1043", {"start": v(-53.94, -17.28) * mm, "end": v(-53.95, -17.3) * mm});
            skLineSegment(sketch, "E1044", {"start": v(-53.95, -17.3) * mm, "end": v(-53.95, -17.3) * mm});
            skLineSegment(sketch, "E1045", {"start": v(-53.95, -17.3) * mm, "end": v(-53.97, -17.3) * mm});
            skLineSegment(sketch, "E1046", {"start": v(-53.97, -17.3) * mm, "end": v(-53.97, -17.3) * mm});
            skLineSegment(sketch, "E1047", {"start": v(-53.97, -17.3) * mm, "end": v(-53.98, -17.3) * mm});
            skLineSegment(sketch, "E1048", {"start": v(-53.98, -17.3) * mm, "end": v(-53.99, -17.28) * mm});
            skLineSegment(sketch, "E1049", {"start": v(-53.99, -17.28) * mm, "end": v(-53.99, -17.27) * mm});
            skLineSegment(sketch, "E1050", {"start": v(-53.99, -17.27) * mm, "end": v(-53.99, -17.27) * mm});
            skLineSegment(sketch, "E1051", {"start": v(-53.99, -17.27) * mm, "end": v(-53.98, -17.25) * mm});
            skLineSegment(sketch, "E1052", {"start": v(-53.98, -17.25) * mm, "end": v(-53.97, -17.25) * mm});
            skLineSegment(sketch, "E1053", {"start": v(-53.97, -17.25) * mm, "end": v(-53.97, -17.25) * mm});
            skLineSegment(sketch, "E1054", {"start": v(-53.97, -17.25) * mm, "end": v(-53.95, -17.25) * mm});
            skLineSegment(sketch, "E1055", {"start": v(-53.95, -17.25) * mm, "end": v(-53.95, -17.25) * mm});
            skLineSegment(sketch, "E1056", {"start": v(-53.95, -17.25) * mm, "end": v(-53.94, -17.27) * mm});
            skLineSegment(sketch, "E1057", {"start": v(-53.94, -17.27) * mm, "end": v(-53.94, -17.27) * mm});
            skLineSegment(sketch, "E1058", {"start": v(12.82, 20.7) * mm, "end": v(12.82, 20.7) * mm});
            skLineSegment(sketch, "E1059", {"start": v(12.82, 20.7) * mm, "end": v(12.8, 20.68) * mm});
            skLineSegment(sketch, "E1060", {"start": v(12.8, 20.68) * mm, "end": v(12.8, 20.68) * mm});
            skLineSegment(sketch, "E1061", {"start": v(12.8, 20.68) * mm, "end": v(12.78, 20.68) * mm});
            skLineSegment(sketch, "E1062", {"start": v(12.78, 20.68) * mm, "end": v(12.78, 20.68) * mm});
            skLineSegment(sketch, "E1063", {"start": v(12.78, 20.68) * mm, "end": v(12.76, 20.7) * mm});
            skLineSegment(sketch, "E1064", {"start": v(12.76, 20.7) * mm, "end": v(12.76, 20.7) * mm});
            skLineSegment(sketch, "E1065", {"start": v(12.76, 20.7) * mm, "end": v(12.78, 20.72) * mm});
            skLineSegment(sketch, "E1066", {"start": v(12.78, 20.72) * mm, "end": v(12.78, 20.72) * mm});
            skLineSegment(sketch, "E1067", {"start": v(12.78, 20.72) * mm, "end": v(12.8, 20.72) * mm});
            skLineSegment(sketch, "E1068", {"start": v(12.8, 20.72) * mm, "end": v(12.8, 20.72) * mm});
            skLineSegment(sketch, "E1069", {"start": v(12.8, 20.72) * mm, "end": v(12.82, 20.7) * mm});
            skLineSegment(sketch, "E1070", {"start": v(-51.9, -23.62) * mm, "end": v(-51.9, -23.63) * mm});
            skLineSegment(sketch, "E1071", {"start": v(-51.9, -23.63) * mm, "end": v(-51.92, -23.64) * mm});
            skLineSegment(sketch, "E1072", {"start": v(-51.92, -23.64) * mm, "end": v(-51.92, -23.64) * mm});
            skLineSegment(sketch, "E1073", {"start": v(-51.92, -23.64) * mm, "end": v(-51.94, -23.64) * mm});
            skLineSegment(sketch, "E1074", {"start": v(-51.94, -23.64) * mm, "end": v(-51.94, -23.64) * mm});
            skLineSegment(sketch, "E1075", {"start": v(-51.94, -23.64) * mm, "end": v(-51.95, -23.63) * mm});
            skLineSegment(sketch, "E1076", {"start": v(-51.95, -23.63) * mm, "end": v(-51.95, -23.62) * mm});
            skLineSegment(sketch, "E1077", {"start": v(-51.95, -23.62) * mm, "end": v(-51.95, -23.62) * mm});
            skLineSegment(sketch, "E1078", {"start": v(-51.95, -23.62) * mm, "end": v(-51.94, -23.6) * mm});
            skLineSegment(sketch, "E1079", {"start": v(-51.94, -23.6) * mm, "end": v(-51.94, -23.6) * mm});
            skLineSegment(sketch, "E1080", {"start": v(-51.94, -23.6) * mm, "end": v(-51.92, -23.6) * mm});
            skLineSegment(sketch, "E1081", {"start": v(-51.92, -23.6) * mm, "end": v(-51.92, -23.6) * mm});
            skLineSegment(sketch, "E1082", {"start": v(-51.92, -23.6) * mm, "end": v(-51.9, -23.62) * mm});
            skLineSegment(sketch, "E1083", {"start": v(-51.9, -23.62) * mm, "end": v(-51.9, -23.62) * mm});
            skLineSegment(sketch, "E1084", {"start": v(-16.2, 33.14) * mm, "end": v(-16.2, 33.13) * mm});
            skLineSegment(sketch, "E1085", {"start": v(-16.2, 33.13) * mm, "end": v(-16.2, 33.12) * mm});
            skLineSegment(sketch, "E1086", {"start": v(-16.2, 33.12) * mm, "end": v(-16.2, 33.12) * mm});
            skLineSegment(sketch, "E1087", {"start": v(-16.2, 33.12) * mm, "end": v(-16.23, 33.12) * mm});
            skLineSegment(sketch, "E1088", {"start": v(-16.23, 33.12) * mm, "end": v(-16.23, 33.12) * mm});
            skLineSegment(sketch, "E1089", {"start": v(-16.23, 33.12) * mm, "end": v(-16.24, 33.13) * mm});
            skLineSegment(sketch, "E1090", {"start": v(-16.24, 33.13) * mm, "end": v(-16.24, 33.14) * mm});
            skLineSegment(sketch, "E1091", {"start": v(-16.24, 33.14) * mm, "end": v(-16.24, 33.14) * mm});
            skLineSegment(sketch, "E1092", {"start": v(-16.24, 33.14) * mm, "end": v(-16.23, 33.16) * mm});
            skLineSegment(sketch, "E1093", {"start": v(-16.23, 33.16) * mm, "end": v(-16.23, 33.16) * mm});
            skLineSegment(sketch, "E1094", {"start": v(-16.23, 33.16) * mm, "end": v(-16.2, 33.16) * mm});
            skLineSegment(sketch, "E1095", {"start": v(-16.2, 33.16) * mm, "end": v(-16.2, 33.16) * mm});
            skLineSegment(sketch, "E1096", {"start": v(-16.2, 33.16) * mm, "end": v(-16.2, 33.14) * mm});
            skLineSegment(sketch, "E1097", {"start": v(-16.2, 33.14) * mm, "end": v(-16.2, 33.14) * mm});
            skLineSegment(sketch, "E1098", {"start": v(-31.63, 32.36) * mm, "end": v(-31.63, 32.35) * mm});
            skLineSegment(sketch, "E1099", {"start": v(-31.63, 32.35) * mm, "end": v(-31.65, 32.34) * mm});
            skLineSegment(sketch, "E1100", {"start": v(-31.65, 32.34) * mm, "end": v(-31.65, 32.34) * mm});
            skLineSegment(sketch, "E1101", {"start": v(-31.65, 32.34) * mm, "end": v(-31.67, 32.34) * mm});
            skLineSegment(sketch, "E1102", {"start": v(-31.67, 32.34) * mm, "end": v(-31.67, 32.34) * mm});
            skLineSegment(sketch, "E1103", {"start": v(-31.67, 32.34) * mm, "end": v(-31.69, 32.36) * mm});
            skLineSegment(sketch, "E1104", {"start": v(-31.69, 32.36) * mm, "end": v(-31.69, 32.36) * mm});
            skLineSegment(sketch, "E1105", {"start": v(-31.69, 32.36) * mm, "end": v(-31.67, 32.38) * mm});
            skLineSegment(sketch, "E1106", {"start": v(-31.67, 32.38) * mm, "end": v(-31.67, 32.38) * mm});
            skLineSegment(sketch, "E1107", {"start": v(-31.67, 32.38) * mm, "end": v(-31.65, 32.38) * mm});
            skLineSegment(sketch, "E1108", {"start": v(-31.65, 32.38) * mm, "end": v(-31.65, 32.38) * mm});
            skLineSegment(sketch, "E1109", {"start": v(-31.65, 32.38) * mm, "end": v(-31.63, 32.36) * mm});
            skLineSegment(sketch, "E1110", {"start": v(-31.63, 32.36) * mm, "end": v(-31.63, 32.36) * mm});
            skLineSegment(sketch, "E1111", {"start": v(-1.76, 23.04) * mm, "end": v(-1.76, 23.03) * mm});
            skLineSegment(sketch, "E1112", {"start": v(-1.76, 23.03) * mm, "end": v(-1.77, 23.02) * mm});
            skLineSegment(sketch, "E1113", {"start": v(-1.77, 23.02) * mm, "end": v(-1.77, 23.02) * mm});
            skLineSegment(sketch, "E1114", {"start": v(-1.77, 23.02) * mm, "end": v(-1.78, 23.02) * mm});
            skLineSegment(sketch, "E1115", {"start": v(-1.78, 23.02) * mm, "end": v(-1.8, 23.02) * mm});
            skLineSegment(sketch, "E1116", {"start": v(-1.8, 23.02) * mm, "end": v(-1.8, 23.02) * mm});
            skLineSegment(sketch, "E1117", {"start": v(-1.8, 23.02) * mm, "end": v(-1.8, 23.03) * mm});
            skLineSegment(sketch, "E1118", {"start": v(-1.8, 23.03) * mm, "end": v(-1.8, 23.04) * mm});
            skLineSegment(sketch, "E1119", {"start": v(-1.8, 23.04) * mm, "end": v(-1.8, 23.04) * mm});
            skLineSegment(sketch, "E1120", {"start": v(-1.8, 23.04) * mm, "end": v(-1.8, 23.06) * mm});
            skLineSegment(sketch, "E1121", {"start": v(-1.8, 23.06) * mm, "end": v(-1.8, 23.06) * mm});
            skLineSegment(sketch, "E1122", {"start": v(-1.8, 23.06) * mm, "end": v(-1.78, 23.06) * mm});
            skLineSegment(sketch, "E1123", {"start": v(-1.78, 23.06) * mm, "end": v(-1.77, 23.06) * mm});
            skLineSegment(sketch, "E1124", {"start": v(-1.77, 23.06) * mm, "end": v(-1.77, 23.06) * mm});
            skLineSegment(sketch, "E1125", {"start": v(-1.77, 23.06) * mm, "end": v(-1.76, 23.04) * mm});
            skLineSegment(sketch, "E1126", {"start": v(-1.76, 23.04) * mm, "end": v(-1.76, 23.04) * mm});
            skLineSegment(sketch, "E1127", {"start": v(-31.74, 34.57) * mm, "end": v(-31.74, 34.56) * mm});
            skLineSegment(sketch, "E1128", {"start": v(-31.74, 34.56) * mm, "end": v(-31.75, 34.55) * mm});
            skLineSegment(sketch, "E1129", {"start": v(-31.75, 34.55) * mm, "end": v(-31.75, 34.55) * mm});
            skLineSegment(sketch, "E1130", {"start": v(-31.75, 34.55) * mm, "end": v(-31.77, 34.55) * mm});
            skLineSegment(sketch, "E1131", {"start": v(-31.77, 34.55) * mm, "end": v(-31.77, 34.55) * mm});
            skLineSegment(sketch, "E1132", {"start": v(-31.77, 34.55) * mm, "end": v(-31.78, 34.55) * mm});
            skLineSegment(sketch, "E1133", {"start": v(-31.78, 34.55) * mm, "end": v(-31.79, 34.57) * mm});
            skLineSegment(sketch, "E1134", {"start": v(-31.79, 34.57) * mm, "end": v(-31.79, 34.57) * mm});
            skLineSegment(sketch, "E1135", {"start": v(-31.79, 34.57) * mm, "end": v(-31.79, 34.58) * mm});
            skLineSegment(sketch, "E1136", {"start": v(-31.79, 34.58) * mm, "end": v(-31.78, 34.6) * mm});
            skLineSegment(sketch, "E1137", {"start": v(-31.78, 34.6) * mm, "end": v(-31.77, 34.6) * mm});
            skLineSegment(sketch, "E1138", {"start": v(-31.77, 34.6) * mm, "end": v(-31.77, 34.6) * mm});
            skLineSegment(sketch, "E1139", {"start": v(-31.77, 34.6) * mm, "end": v(-31.75, 34.6) * mm});
            skLineSegment(sketch, "E1140", {"start": v(-31.75, 34.6) * mm, "end": v(-31.75, 34.6) * mm});
            skLineSegment(sketch, "E1141", {"start": v(-31.75, 34.6) * mm, "end": v(-31.74, 34.58) * mm});
            skLineSegment(sketch, "E1142", {"start": v(-31.74, 34.58) * mm, "end": v(-31.74, 34.57) * mm});
            skLineSegment(sketch, "E1143", {"start": v(55.28, -32) * mm, "end": v(55.28, -32) * mm});
            skLineSegment(sketch, "E1144", {"start": v(55.28, -32) * mm, "end": v(55.27, -32.02) * mm});
            skLineSegment(sketch, "E1145", {"start": v(55.27, -32.02) * mm, "end": v(55.27, -32.03) * mm});
            skLineSegment(sketch, "E1146", {"start": v(55.27, -32.03) * mm, "end": v(55.27, -32.03) * mm});
            skLineSegment(sketch, "E1147", {"start": v(55.27, -32.03) * mm, "end": v(55.25, -32.03) * mm});
            skLineSegment(sketch, "E1148", {"start": v(55.25, -32.03) * mm, "end": v(55.25, -32.03) * mm});
            skLineSegment(sketch, "E1149", {"start": v(55.25, -32.03) * mm, "end": v(55.24, -32.02) * mm});
            skLineSegment(sketch, "E1150", {"start": v(55.24, -32.02) * mm, "end": v(55.23, -32) * mm});
            skLineSegment(sketch, "E1151", {"start": v(55.23, -32) * mm, "end": v(55.23, -32) * mm});
            skLineSegment(sketch, "E1152", {"start": v(55.23, -32) * mm, "end": v(55.24, -31.98) * mm});
            skLineSegment(sketch, "E1153", {"start": v(55.24, -31.98) * mm, "end": v(55.25, -31.98) * mm});
            skLineSegment(sketch, "E1154", {"start": v(55.25, -31.98) * mm, "end": v(55.25, -31.98) * mm});
            skLineSegment(sketch, "E1155", {"start": v(55.25, -31.98) * mm, "end": v(55.27, -31.98) * mm});
            skLineSegment(sketch, "E1156", {"start": v(55.27, -31.98) * mm, "end": v(55.27, -31.98) * mm});
            skLineSegment(sketch, "E1157", {"start": v(55.27, -31.98) * mm, "end": v(55.28, -32) * mm});
            skLineSegment(sketch, "E1158", {"start": v(13.88, -41.91) * mm, "end": v(13.88, -41.92) * mm});
            skLineSegment(sketch, "E1159", {"start": v(13.88, -41.92) * mm, "end": v(13.87, -41.93) * mm});
            skLineSegment(sketch, "E1160", {"start": v(13.87, -41.93) * mm, "end": v(13.87, -41.93) * mm});
            skLineSegment(sketch, "E1161", {"start": v(13.87, -41.93) * mm, "end": v(13.85, -41.93) * mm});
            skLineSegment(sketch, "E1162", {"start": v(13.85, -41.93) * mm, "end": v(13.84, -41.93) * mm});
            skLineSegment(sketch, "E1163", {"start": v(13.84, -41.93) * mm, "end": v(13.84, -41.93) * mm});
            skLineSegment(sketch, "E1164", {"start": v(13.84, -41.93) * mm, "end": v(13.83, -41.91) * mm});
            skLineSegment(sketch, "E1165", {"start": v(13.83, -41.91) * mm, "end": v(13.83, -41.91) * mm});
            skLineSegment(sketch, "E1166", {"start": v(13.83, -41.91) * mm, "end": v(13.83, -41.9) * mm});
            skLineSegment(sketch, "E1167", {"start": v(13.83, -41.9) * mm, "end": v(13.84, -41.89) * mm});
            skLineSegment(sketch, "E1168", {"start": v(13.84, -41.89) * mm, "end": v(13.84, -41.89) * mm});
            skLineSegment(sketch, "E1169", {"start": v(13.84, -41.89) * mm, "end": v(13.85, -41.89) * mm});
            skLineSegment(sketch, "E1170", {"start": v(13.85, -41.89) * mm, "end": v(13.87, -41.89) * mm});
            skLineSegment(sketch, "E1171", {"start": v(13.87, -41.89) * mm, "end": v(13.87, -41.89) * mm});
            skLineSegment(sketch, "E1172", {"start": v(13.87, -41.89) * mm, "end": v(13.88, -41.9) * mm});
            skLineSegment(sketch, "E1173", {"start": v(13.88, -41.9) * mm, "end": v(13.88, -41.91) * mm});
            skLineSegment(sketch, "E1174", {"start": v(-41.95, -49.66) * mm, "end": v(-34.97, -56.64) * mm});
            skLineSegment(sketch, "E1175", {"start": v(49.7, -59.36) * mm, "end": v(49.7, -59.2) * mm});
            skLineSegment(sketch, "E1176", {"start": v(49.7, -59.2) * mm, "end": v(47.9, -57.4) * mm});
            skLineSegment(sketch, "E1177", {"start": v(47.9, -57.4) * mm, "end": v(-34.2, -57.4) * mm});
            skLineSegment(sketch, "E1178", {"start": v(-34.2, -57.4) * mm, "end": v(-34.97, -56.64) * mm});
            skLineSegment(sketch, "E1179", {"start": v(-52.7, 30.02) * mm, "end": v(-52.7, 20.83) * mm});
            skLineSegment(sketch, "E1180", {"start": v(-52.7, 20.83) * mm, "end": v(-59.55, 13.97) * mm});
            skLineSegment(sketch, "E1181", {"start": v(-59.55, -13.97) * mm, "end": v(-59.55, -16.51) * mm});
            skLineSegment(sketch, "E1182", {"start": v(-43.04, -44.45) * mm, "end": v(-43.04, -30.48) * mm});
            skLineSegment(sketch, "E1183", {"start": v(-43.04, -30.48) * mm, "end": v(-59.55, -13.97) * mm});
            skLineSegment(sketch, "E1184", {"start": v(-42.2, -49.66) * mm, "end": v(-41.95, -49.66) * mm});
            skLineSegment(sketch, "E1185", {"start": v(-22.72, 58.42) * mm, "end": v(-31.23, 49.91) * mm});
            skLineSegment(sketch, "E1186", {"start": v(-31.23, 49.91) * mm, "end": v(-31.23, 49.2) * mm});
            skLineSegment(sketch, "E1187", {"start": v(-60.6, -32.26) * mm, "end": v(-60.06, -32.8) * mm});
            skLineSegment(sketch, "E1188", {"start": v(-60.6, -25.62) * mm, "end": v(-60.6, -32.26) * mm});
            skLineSegment(sketch, "E1189", {"start": v(-60.06, -32.8) * mm, "end": v(-59.26, -32.8) * mm});
            skLineSegment(sketch, "E1190", {"start": v(-62.1, -24.13) * mm, "end": v(-60.6, -25.62) * mm});
            skLineSegment(sketch, "E1191", {"start": v(-59.26, -32.8) * mm, "end": v(-46.45, -45.61) * mm});
            skLineSegment(sketch, "E1192", {"start": v(-46.45, -45.61) * mm, "end": v(-46.35, -45.71) * mm});
            skLineSegment(sketch, "E1193", {"start": v(-4.94, 60.96) * mm, "end": v(-6.36, 59.54) * mm});
            skLineSegment(sketch, "E1194", {"start": v(-6.36, 59.54) * mm, "end": v(-10.56, 59.54) * mm});
            skLineSegment(sketch, "E1195", {"start": v(-10.56, 59.54) * mm, "end": v(-11.44, 58.65) * mm});
            skLineSegment(sketch, "E1196", {"start": v(-11.44, 58.65) * mm, "end": v(-11.44, 57.88) * mm});
            skLineSegment(sketch, "E1197", {"start": v(-20.5, 48.82) * mm, "end": v(-31.39, 48.82) * mm});
            skLineSegment(sketch, "E1198", {"start": v(-11.44, 57.88) * mm, "end": v(-20.5, 48.82) * mm});
            skLineSegment(sketch, "E1199", {"start": v(-31.39, 48.82) * mm, "end": v(-31.61, 49.04) * mm});
            skLineSegment(sketch, "E1200", {"start": v(-31.61, 49.04) * mm, "end": v(-31.61, 53.5) * mm});
            skLineSegment(sketch, "E1201", {"start": v(-31.61, 53.5) * mm, "end": v(-27.8, 57.3) * mm});
            skLineSegment(sketch, "E1202", {"start": v(-27.8, 57.3) * mm, "end": v(-27.8, 58.42) * mm});
            skLineSegment(sketch, "E1203", {"start": v(-4.94, 60.96) * mm, "end": v(16.47, 39.55) * mm});
            skLineSegment(sketch, "E1204", {"start": v(16.47, 39.55) * mm, "end": v(16.47, 17.3) * mm});
            skLineSegment(sketch, "E1205", {"start": v(50.2, 5.1) * mm, "end": v(50.2, -5.1) * mm});
            skLineSegment(sketch, "E1206", {"start": v(45.94, 2.5) * mm, "end": v(45.94, 5.48) * mm});
            skLineSegment(sketch, "E1207", {"start": v(45.94, 2.5) * mm, "end": v(48.54, 5.1) * mm});
            skLineSegment(sketch, "E1208", {"start": v(48.54, 5.1) * mm, "end": v(50.2, 5.1) * mm});
            skLineSegment(sketch, "E1209", {"start": v(13.6, -40.39) * mm, "end": v(19.19, -34.8) * mm});
            skLineSegment(sketch, "E1210", {"start": v(19.19, -34.8) * mm, "end": v(52.97, -34.8) * mm});
            skLineSegment(sketch, "E1211", {"start": v(52.97, -34.8) * mm, "end": v(53.48, -34.29) * mm});
            skLineSegment(sketch, "E1212", {"start": v(-17.41, 35.33) * mm, "end": v(-11.67, 29.59) * mm});
            skLineSegment(sketch, "E1213", {"start": v(-11.67, 29.59) * mm, "end": v(-11.67, 21.59) * mm});
            skLineSegment(sketch, "E1214", {"start": v(-11.67, 21.59) * mm, "end": v(-12.64, 20.61) * mm});
            skLineSegment(sketch, "E1215", {"start": v(-12.64, 20.61) * mm, "end": v(-12.64, 18.42) * mm});
            skLineSegment(sketch, "E1216", {"start": v(-12.64, 18.42) * mm, "end": v(-10.53, 16.3) * mm});
            skLineSegment(sketch, "E1217", {"start": v(-10.53, 16.3) * mm, "end": v(1, 16.3) * mm});
            skLineSegment(sketch, "E1218", {"start": v(1, 16.3) * mm, "end": v(4.7, 12.63) * mm});
            skLineSegment(sketch, "E1219", {"start": v(-25.1, 23.72) * mm, "end": v(-23.17, 23.72) * mm});
            skLineSegment(sketch, "E1220", {"start": v(-23.17, 23.72) * mm, "end": v(-22.87, 23.42) * mm});
            skLineSegment(sketch, "E1221", {"start": v(-25.18, 20.57) * mm, "end": v(-23.87, 20.57) * mm});
            skLineSegment(sketch, "E1222", {"start": v(-23.87, 20.57) * mm, "end": v(-22.74, 21.7) * mm});
            skLineSegment(sketch, "E1223", {"start": v(-43.78, 39.06) * mm, "end": v(-55.51, 50.8) * mm});
            skLineSegment(sketch, "E1224", {"start": v(-55.51, 50.8) * mm, "end": v(-60.82, 50.8) * mm});
            skLineSegment(sketch, "E1225", {"start": v(7.87, 22.79) * mm, "end": v(-8.41, 39.06) * mm});
            skLineSegment(sketch, "E1226", {"start": v(-8.41, 39.06) * mm, "end": v(-43.78, 39.06) * mm});
            skLineSegment(sketch, "E1227", {"start": v(-43.78, 58.07) * mm, "end": v(-55.55, 58.07) * mm});
            skLineSegment(sketch, "E1228", {"start": v(-55.55, 58.07) * mm, "end": v(-60.82, 52.8) * mm});
            skLineSegment(sketch, "E1229", {"start": v(12.57, 22.66) * mm, "end": v(-5.24, 40.46) * mm});
            skLineSegment(sketch, "E1230", {"start": v(-5.24, 40.46) * mm, "end": v(-26.18, 40.46) * mm});
            skLineSegment(sketch, "E1231", {"start": v(-26.18, 40.46) * mm, "end": v(-38.7, 52.98) * mm});
            skLineSegment(sketch, "E1232", {"start": v(-38.7, 52.98) * mm, "end": v(-43.78, 58.07) * mm});
            skLineSegment(sketch, "E1233", {"start": v(49.31, -61.67) * mm, "end": v(47.15, -59.51) * mm});
            skLineSegment(sketch, "E1234", {"start": v(60.72, -61.67) * mm, "end": v(49.31, -61.67) * mm});
            skLineSegment(sketch, "E1235", {"start": v(61.35, -61.04) * mm, "end": v(60.72, -61.67) * mm});
            skLineSegment(sketch, "E1236", {"start": v(61.35, -29.88) * mm, "end": v(61.35, -61.04) * mm});
            skLineSegment(sketch, "E1237", {"start": v(47.15, -59.51) * mm, "end": v(47.15, -59.36) * mm});
            skLineSegment(sketch, "E1238", {"start": v(60.56, -29.08) * mm, "end": v(61.35, -29.88) * mm});
            skLineSegment(sketch, "E1239", {"start": v(60.56, -29.08) * mm, "end": v(10.1, 21.37) * mm});
            skLineSegment(sketch, "E1240", {"start": v(60.67, -29.2) * mm, "end": v(60.56, -29.08) * mm});
            skLineSegment(sketch, "E1241", {"start": v(-10.5, 21.13) * mm, "end": v(-12.26, 19.37) * mm});
            skLineSegment(sketch, "E1242", {"start": v(-10.82, 17.13) * mm, "end": v(-8.69, 17.13) * mm});
            skLineSegment(sketch, "E1243", {"start": v(3.83, 21.37) * mm, "end": v(2.61, 22.6) * mm});
            skLineSegment(sketch, "E1244", {"start": v(-12.26, 19.37) * mm, "end": v(-12.26, 18.58) * mm});
            skLineSegment(sketch, "E1245", {"start": v(10.1, 21.37) * mm, "end": v(3.83, 21.37) * mm});
            skLineSegment(sketch, "E1246", {"start": v(2.61, 22.6) * mm, "end": v(0.96, 22.6) * mm});
            skLineSegment(sketch, "E1247", {"start": v(0.96, 22.6) * mm, "end": v(-0.5, 21.13) * mm});
            skLineSegment(sketch, "E1248", {"start": v(-8.69, 17.13) * mm, "end": v(-7.88, 17.13) * mm});
            skLineSegment(sketch, "E1249", {"start": v(-0.5, 21.13) * mm, "end": v(-10.5, 21.13) * mm});
            skLineSegment(sketch, "E1250", {"start": v(-12.26, 18.58) * mm, "end": v(-10.82, 17.13) * mm});
            skLineSegment(sketch, "E1251", {"start": v(60.95, -30) * mm, "end": v(60.7, -29.77) * mm});
            skLineSegment(sketch, "E1252", {"start": v(60.7, -29.77) * mm, "end": v(10.18, 20.75) * mm});
            skLineSegment(sketch, "E1253", {"start": v(54.77, -59.36) * mm, "end": v(54.77, -59.51) * mm});
            skLineSegment(sketch, "E1254", {"start": v(55.9, -60.63) * mm, "end": v(60.32, -60.63) * mm});
            skLineSegment(sketch, "E1255", {"start": v(54.77, -59.51) * mm, "end": v(55.9, -60.63) * mm});
            skLineSegment(sketch, "E1256", {"start": v(60.32, -60.63) * mm, "end": v(60.97, -59.97) * mm});
            skLineSegment(sketch, "E1257", {"start": v(60.97, -59.97) * mm, "end": v(60.97, -30.04) * mm});
            skLineSegment(sketch, "E1258", {"start": v(60.97, -30.04) * mm, "end": v(60.7, -29.77) * mm});
            skLineSegment(sketch, "E1259", {"start": v(10.18, 20.75) * mm, "end": v(-9.66, 20.75) * mm});
            skLineSegment(sketch, "E1260", {"start": v(-9.66, 20.75) * mm, "end": v(-10.87, 19.55) * mm});
            skLineSegment(sketch, "E1261", {"start": v(-10.87, 19.55) * mm, "end": v(-11.44, 18.98) * mm});
            skLineSegment(sketch, "E1262", {"start": v(59.9, -29.5) * mm, "end": v(59.84, -29.44) * mm});
            skLineSegment(sketch, "E1263", {"start": v(60.6, -30.2) * mm, "end": v(59.84, -29.44) * mm});
            skLineSegment(sketch, "E1264", {"start": v(59.84, -29.44) * mm, "end": v(11.48, 18.91) * mm});
            skLineSegment(sketch, "E1265", {"start": v(60.6, -55.93) * mm, "end": v(60.6, -30.2) * mm});
            skLineSegment(sketch, "E1266", {"start": v(57.31, -59.2) * mm, "end": v(60.6, -55.93) * mm});
            skLineSegment(sketch, "E1267", {"start": v(11.48, 18.91) * mm, "end": v(-6.68, 18.91) * mm});
            skLineSegment(sketch, "E1268", {"start": v(57.31, -59.36) * mm, "end": v(57.31, -59.2) * mm});
            skLineSegment(sketch, "E1269", {"start": v(-24.22, 9.7) * mm, "end": v(-26.99, 9.7) * mm});
            skLineSegment(sketch, "E1270", {"start": v(-26.99, 9.7) * mm, "end": v(-53.96, -17.27) * mm});
            skLineSegment(sketch, "E1271", {"start": v(-21.1, 16.18) * mm, "end": v(-21.1, 12.83) * mm});
            skLineSegment(sketch, "E1272", {"start": v(-21.1, 12.83) * mm, "end": v(-24.22, 9.7) * mm});
            skLineSegment(sketch, "E1273", {"start": v(-7.48, 58.42) * mm, "end": v(13.45, 37.49) * mm});
            skLineSegment(sketch, "E1274", {"start": v(13.45, 37.49) * mm, "end": v(13.45, 21.37) * mm});
            skLineSegment(sketch, "E1275", {"start": v(13.45, 21.37) * mm, "end": v(12.79, 20.7) * mm});
            skLineSegment(sketch, "E1276", {"start": v(-9.6, 13.82) * mm, "end": v(6.46, -2.25) * mm});
            skLineSegment(sketch, "E1277", {"start": v(6.46, -2.25) * mm, "end": v(20.75, -2.25) * mm});
            skLineSegment(sketch, "E1278", {"start": v(-10.02, 60.96) * mm, "end": v(-11.14, 59.84) * mm});
            skLineSegment(sketch, "E1279", {"start": v(-11.14, 59.84) * mm, "end": v(-28.34, 59.84) * mm});
            skLineSegment(sketch, "E1280", {"start": v(-28.34, 59.84) * mm, "end": v(-30.93, 62.44) * mm});
            skLineSegment(sketch, "E1281", {"start": v(-30.93, 62.44) * mm, "end": v(-58.1, 62.44) * mm});
            skLineSegment(sketch, "E1282", {"start": v(-58.1, 62.44) * mm, "end": v(-61.75, 58.8) * mm});
            skLineSegment(sketch, "E1283", {"start": v(-61.75, 58.8) * mm, "end": v(-61.75, -7.28) * mm});
            skLineSegment(sketch, "E1284", {"start": v(-61.75, -7.28) * mm, "end": v(-62.1, -7.62) * mm});
            skLineSegment(sketch, "E1285", {"start": v(-62.1, -19.05) * mm, "end": v(-60.97, -20.17) * mm});
            skLineSegment(sketch, "E1286", {"start": v(-60.97, -20.17) * mm, "end": v(-55.39, -20.17) * mm});
            skLineSegment(sketch, "E1287", {"start": v(-55.39, -20.17) * mm, "end": v(-51.93, -23.62) * mm});
            skLineSegment(sketch, "E1288", {"start": v(-31.66, 32.36) * mm, "end": v(-30.88, 33.14) * mm});
            skLineSegment(sketch, "E1289", {"start": v(-30.88, 33.14) * mm, "end": v(-16.22, 33.14) * mm});
            skLineSegment(sketch, "E1290", {"start": v(-31.76, 34.57) * mm, "end": v(-30.62, 35.71) * mm});
            skLineSegment(sketch, "E1291", {"start": v(-30.62, 35.71) * mm, "end": v(-14.46, 35.71) * mm});
            skLineSegment(sketch, "E1292", {"start": v(-14.46, 35.71) * mm, "end": v(-1.79, 23.04) * mm});
            skLineSegment(sketch, "E1293", {"start": v(-3.63, 17.83) * mm, "end": v(-2.42, 16.63) * mm});
            skLineSegment(sketch, "E1294", {"start": v(-2.42, 16.63) * mm, "end": v(1.82, 16.63) * mm});
            skLineSegment(sketch, "E1295", {"start": v(1.82, 16.63) * mm, "end": v(5.45, 13) * mm});
            skLineSegment(sketch, "E1296", {"start": v(5.45, 13) * mm, "end": v(5.45, 12.26) * mm});
            skLineSegment(sketch, "E1297", {"start": v(5.45, 12.26) * mm, "end": v(5.06, 11.86) * mm});
            skLineSegment(sketch, "E1298", {"start": v(-42.09, -17.53) * mm, "end": v(-42.09, -44.9) * mm});
            skLineSegment(sketch, "E1299", {"start": v(-42.09, -44.9) * mm, "end": v(-55.82, -58.64) * mm});
            skLineSegment(sketch, "E1300", {"start": v(-61.04, -58.64) * mm, "end": v(-61.23, -58.83) * mm});
            skLineSegment(sketch, "E1301", {"start": v(5.06, 11.86) * mm, "end": v(-6.53, 11.86) * mm});
            skLineSegment(sketch, "E1302", {"start": v(-6.53, 11.86) * mm, "end": v(-9.24, 14.58) * mm});
            skLineSegment(sketch, "E1303", {"start": v(-9.24, 14.58) * mm, "end": v(-9.97, 14.58) * mm});
            skLineSegment(sketch, "E1304", {"start": v(-9.97, 14.58) * mm, "end": v(-42.09, -17.53) * mm});
            skLineSegment(sketch, "E1305", {"start": v(-61.23, -58.83) * mm, "end": v(-62.1, -59.69) * mm});
            skLineSegment(sketch, "E1306", {"start": v(-55.82, -58.64) * mm, "end": v(-61.04, -58.64) * mm});
            skLineSegment(sketch, "E1307", {"start": v(45.94, 53.34) * mm, "end": v(44.8, 53.34) * mm});
            skLineSegment(sketch, "E1308", {"start": v(44.8, 53.34) * mm, "end": v(36.07, 62.08) * mm});
            skLineSegment(sketch, "E1309", {"start": v(36.07, 62.08) * mm, "end": v(-16.52, 62.08) * mm});
            skLineSegment(sketch, "E1310", {"start": v(-16.52, 62.08) * mm, "end": v(-16.78, 61.82) * mm});
            skLineSegment(sketch, "E1311", {"start": v(-16.78, 61.82) * mm, "end": v(-17.64, 60.96) * mm});
            skLineSegment(sketch, "E1312", {"start": v(20.59, -35.18) * mm, "end": v(53.13, -35.18) * mm});
            skLineSegment(sketch, "E1313", {"start": v(53.13, -35.18) * mm, "end": v(55.26, -33.05) * mm});
            skLineSegment(sketch, "E1314", {"start": v(55.26, -33.05) * mm, "end": v(55.26, -32) * mm});
            skLineSegment(sketch, "E1315", {"start": v(-59.49, 13.97) * mm, "end": v(-59.49, 13.96) * mm});
            skLineSegment(sketch, "E1316", {"start": v(-59.49, 13.96) * mm, "end": v(-59.51, 13.92) * mm});
            skLineSegment(sketch, "E1317", {"start": v(-59.51, 13.92) * mm, "end": v(-59.52, 13.92) * mm});
            skLineSegment(sketch, "E1318", {"start": v(-59.52, 13.92) * mm, "end": v(-59.52, 13.91) * mm});
            skLineSegment(sketch, "E1319", {"start": v(-59.52, 13.91) * mm, "end": v(-59.58, 13.91) * mm});
            skLineSegment(sketch, "E1320", {"start": v(-59.58, 13.91) * mm, "end": v(-59.58, 13.92) * mm});
            skLineSegment(sketch, "E1321", {"start": v(-59.58, 13.92) * mm, "end": v(-59.59, 13.92) * mm});
            skLineSegment(sketch, "E1322", {"start": v(-59.59, 13.92) * mm, "end": v(-59.61, 13.96) * mm});
            skLineSegment(sketch, "E1323", {"start": v(-59.61, 13.96) * mm, "end": v(-59.61, 13.97) * mm});
            skLineSegment(sketch, "E1324", {"start": v(-59.61, 13.97) * mm, "end": v(-59.61, 13.98) * mm});
            skLineSegment(sketch, "E1325", {"start": v(-59.61, 13.98) * mm, "end": v(-59.59, 14.02) * mm});
            skLineSegment(sketch, "E1326", {"start": v(-59.59, 14.02) * mm, "end": v(-59.58, 14.02) * mm});
            skLineSegment(sketch, "E1327", {"start": v(-59.58, 14.02) * mm, "end": v(-59.58, 14.03) * mm});
            skLineSegment(sketch, "E1328", {"start": v(-59.58, 14.03) * mm, "end": v(-59.52, 14.03) * mm});
            skLineSegment(sketch, "E1329", {"start": v(-59.52, 14.03) * mm, "end": v(-59.52, 14.02) * mm});
            skLineSegment(sketch, "E1330", {"start": v(-59.52, 14.02) * mm, "end": v(-59.51, 14.02) * mm});
            skLineSegment(sketch, "E1331", {"start": v(-59.51, 14.02) * mm, "end": v(-59.49, 13.98) * mm});
            skLineSegment(sketch, "E1332", {"start": v(-59.49, 13.98) * mm, "end": v(-59.49, 13.97) * mm});
            skLineSegment(sketch, "E1333", {"start": v(13.86, -41.91) * mm, "end": v(20.59, -35.18) * mm});
            skLineSegment(sketch, "E1334", {"start": v(-52.63, 30.02) * mm, "end": v(-52.63, 30) * mm});
            skLineSegment(sketch, "E1335", {"start": v(-52.63, 30) * mm, "end": v(-52.66, 29.97) * mm});
            skLineSegment(sketch, "E1336", {"start": v(-52.66, 29.97) * mm, "end": v(-52.66, 29.97) * mm});
            skLineSegment(sketch, "E1337", {"start": v(-52.66, 29.97) * mm, "end": v(-52.67, 29.97) * mm});
            skLineSegment(sketch, "E1338", {"start": v(-52.67, 29.97) * mm, "end": v(-52.72, 29.97) * mm});
            skLineSegment(sketch, "E1339", {"start": v(-52.72, 29.97) * mm, "end": v(-52.72, 29.97) * mm});
            skLineSegment(sketch, "E1340", {"start": v(-52.72, 29.97) * mm, "end": v(-52.73, 29.97) * mm});
            skLineSegment(sketch, "E1341", {"start": v(-52.73, 29.97) * mm, "end": v(-52.75, 30.01) * mm});
            skLineSegment(sketch, "E1342", {"start": v(-52.75, 30.01) * mm, "end": v(-52.75, 30.02) * mm});
            skLineSegment(sketch, "E1343", {"start": v(-52.75, 30.02) * mm, "end": v(-52.75, 30.04) * mm});
            skLineSegment(sketch, "E1344", {"start": v(-52.75, 30.04) * mm, "end": v(-52.73, 30.08) * mm});
            skLineSegment(sketch, "E1345", {"start": v(-52.73, 30.08) * mm, "end": v(-52.72, 30.08) * mm});
            skLineSegment(sketch, "E1346", {"start": v(-52.72, 30.08) * mm, "end": v(-52.72, 30.08) * mm});
            skLineSegment(sketch, "E1347", {"start": v(-52.72, 30.08) * mm, "end": v(-52.67, 30.08) * mm});
            skLineSegment(sketch, "E1348", {"start": v(-52.67, 30.08) * mm, "end": v(-52.66, 30.08) * mm});
            skLineSegment(sketch, "E1349", {"start": v(-52.66, 30.08) * mm, "end": v(-52.66, 30.08) * mm});
            skLineSegment(sketch, "E1350", {"start": v(-52.66, 30.08) * mm, "end": v(-52.63, 30.04) * mm});
            skLineSegment(sketch, "E1351", {"start": v(-52.63, 30.04) * mm, "end": v(-52.63, 30.02) * mm});
            skLineSegment(sketch, "E1352", {"start": v(-31.22, 49.2) * mm, "end": v(-31.22, 49.2) * mm});
            skLineSegment(sketch, "E1353", {"start": v(-31.22, 49.2) * mm, "end": v(-31.22, 49.19) * mm});
            skLineSegment(sketch, "E1354", {"start": v(-31.22, 49.19) * mm, "end": v(-31.22, 49.19) * mm});
            skLineSegment(sketch, "E1355", {"start": v(-31.22, 49.19) * mm, "end": v(-31.23, 49.19) * mm});
            skLineSegment(sketch, "E1356", {"start": v(-31.23, 49.19) * mm, "end": v(-31.24, 49.2) * mm});
            skLineSegment(sketch, "E1357", {"start": v(-31.24, 49.2) * mm, "end": v(-31.24, 49.2) * mm});
            skLineSegment(sketch, "E1358", {"start": v(-31.24, 49.2) * mm, "end": v(-31.24, 49.21) * mm});
            skLineSegment(sketch, "E1359", {"start": v(-31.24, 49.21) * mm, "end": v(-31.23, 49.21) * mm});
            skLineSegment(sketch, "E1360", {"start": v(-31.23, 49.21) * mm, "end": v(-31.23, 49.21) * mm});
            skLineSegment(sketch, "E1361", {"start": v(-31.23, 49.21) * mm, "end": v(-31.22, 49.21) * mm});
            skLineSegment(sketch, "E1362", {"start": v(-31.22, 49.21) * mm, "end": v(-31.22, 49.21) * mm});
            skLineSegment(sketch, "E1363", {"start": v(-31.22, 49.21) * mm, "end": v(-31.22, 49.2) * mm});
            skLineSegment(sketch, "E1364", {"start": v(-42.19, -49.66) * mm, "end": v(-42.19, -49.66) * mm});
            skLineSegment(sketch, "E1365", {"start": v(-42.19, -49.66) * mm, "end": v(-42.2, -49.67) * mm});
            skLineSegment(sketch, "E1366", {"start": v(-42.2, -49.67) * mm, "end": v(-42.2, -49.67) * mm});
            skLineSegment(sketch, "E1367", {"start": v(-42.2, -49.67) * mm, "end": v(-42.21, -49.66) * mm});
            skLineSegment(sketch, "E1368", {"start": v(-42.21, -49.66) * mm, "end": v(-42.21, -49.66) * mm});
            skLineSegment(sketch, "E1369", {"start": v(-42.21, -49.66) * mm, "end": v(-42.2, -49.65) * mm});
            skLineSegment(sketch, "E1370", {"start": v(-42.2, -49.65) * mm, "end": v(-42.2, -49.65) * mm});
            skLineSegment(sketch, "E1371", {"start": v(-42.2, -49.65) * mm, "end": v(-42.19, -49.66) * mm});
            skLineSegment(sketch, "E1372", {"start": v(-46.28, -45.72) * mm, "end": v(-46.28, -45.73) * mm});
            skLineSegment(sketch, "E1373", {"start": v(-46.28, -45.73) * mm, "end": v(-46.31, -45.77) * mm});
            skLineSegment(sketch, "E1374", {"start": v(-46.31, -45.77) * mm, "end": v(-46.32, -45.77) * mm});
            skLineSegment(sketch, "E1375", {"start": v(-46.32, -45.77) * mm, "end": v(-46.32, -45.77) * mm});
            skLineSegment(sketch, "E1376", {"start": v(-46.32, -45.77) * mm, "end": v(-46.37, -45.77) * mm});
            skLineSegment(sketch, "E1377", {"start": v(-46.37, -45.77) * mm, "end": v(-46.38, -45.77) * mm});
            skLineSegment(sketch, "E1378", {"start": v(-46.38, -45.77) * mm, "end": v(-46.38, -45.77) * mm});
            skLineSegment(sketch, "E1379", {"start": v(-46.38, -45.77) * mm, "end": v(-46.41, -45.73) * mm});
            skLineSegment(sketch, "E1380", {"start": v(-46.41, -45.73) * mm, "end": v(-46.41, -45.72) * mm});
            skLineSegment(sketch, "E1381", {"start": v(-46.41, -45.72) * mm, "end": v(-46.41, -45.7) * mm});
            skLineSegment(sketch, "E1382", {"start": v(-46.41, -45.7) * mm, "end": v(-46.38, -45.66) * mm});
            skLineSegment(sketch, "E1383", {"start": v(-46.38, -45.66) * mm, "end": v(-46.38, -45.66) * mm});
            skLineSegment(sketch, "E1384", {"start": v(-46.38, -45.66) * mm, "end": v(-46.37, -45.66) * mm});
            skLineSegment(sketch, "E1385", {"start": v(-46.37, -45.66) * mm, "end": v(-46.32, -45.66) * mm});
            skLineSegment(sketch, "E1386", {"start": v(-46.32, -45.66) * mm, "end": v(-46.32, -45.66) * mm});
            skLineSegment(sketch, "E1387", {"start": v(-46.32, -45.66) * mm, "end": v(-46.31, -45.66) * mm});
            skLineSegment(sketch, "E1388", {"start": v(-46.31, -45.66) * mm, "end": v(-46.28, -45.7) * mm});
            skLineSegment(sketch, "E1389", {"start": v(-46.28, -45.7) * mm, "end": v(-46.28, -45.72) * mm});
            skLineSegment(sketch, "E1390", {"start": v(16.49, 17.3) * mm, "end": v(16.49, 17.3) * mm});
            skLineSegment(sketch, "E1391", {"start": v(16.49, 17.3) * mm, "end": v(16.48, 17.29) * mm});
            skLineSegment(sketch, "E1392", {"start": v(16.48, 17.29) * mm, "end": v(16.48, 17.29) * mm});
            skLineSegment(sketch, "E1393", {"start": v(16.48, 17.29) * mm, "end": v(16.47, 17.29) * mm});
            skLineSegment(sketch, "E1394", {"start": v(16.47, 17.29) * mm, "end": v(16.47, 17.29) * mm});
            skLineSegment(sketch, "E1395", {"start": v(16.47, 17.29) * mm, "end": v(16.46, 17.3) * mm});
            skLineSegment(sketch, "E1396", {"start": v(16.46, 17.3) * mm, "end": v(16.46, 17.3) * mm});
            skLineSegment(sketch, "E1397", {"start": v(16.46, 17.3) * mm, "end": v(16.47, 17.3) * mm});
            skLineSegment(sketch, "E1398", {"start": v(16.47, 17.3) * mm, "end": v(16.47, 17.3) * mm});
            skLineSegment(sketch, "E1399", {"start": v(16.47, 17.3) * mm, "end": v(16.48, 17.3) * mm});
            skLineSegment(sketch, "E1400", {"start": v(16.48, 17.3) * mm, "end": v(16.48, 17.3) * mm});
            skLineSegment(sketch, "E1401", {"start": v(16.48, 17.3) * mm, "end": v(16.49, 17.3) * mm});
            skLineSegment(sketch, "E1402", {"start": v(15.25, -56.34) * mm, "end": v(15.25, -56.34) * mm});
            skLineSegment(sketch, "E1403", {"start": v(15.25, -56.34) * mm, "end": v(15.24, -56.35) * mm});
            skLineSegment(sketch, "E1404", {"start": v(15.24, -56.35) * mm, "end": v(15.24, -56.35) * mm});
            skLineSegment(sketch, "E1405", {"start": v(15.24, -56.35) * mm, "end": v(15.23, -56.35) * mm});
            skLineSegment(sketch, "E1406", {"start": v(15.23, -56.35) * mm, "end": v(15.23, -56.35) * mm});
            skLineSegment(sketch, "E1407", {"start": v(15.23, -56.35) * mm, "end": v(15.22, -56.34) * mm});
            skLineSegment(sketch, "E1408", {"start": v(15.22, -56.34) * mm, "end": v(15.22, -56.34) * mm});
            skLineSegment(sketch, "E1409", {"start": v(15.22, -56.34) * mm, "end": v(15.22, -56.33) * mm});
            skLineSegment(sketch, "E1410", {"start": v(15.22, -56.33) * mm, "end": v(15.23, -56.33) * mm});
            skLineSegment(sketch, "E1411", {"start": v(15.23, -56.33) * mm, "end": v(15.23, -56.33) * mm});
            skLineSegment(sketch, "E1412", {"start": v(15.23, -56.33) * mm, "end": v(15.23, -56.32) * mm});
            skLineSegment(sketch, "E1413", {"start": v(15.23, -56.32) * mm, "end": v(15.24, -56.32) * mm});
            skLineSegment(sketch, "E1414", {"start": v(15.24, -56.32) * mm, "end": v(15.24, -56.33) * mm});
            skLineSegment(sketch, "E1415", {"start": v(15.24, -56.33) * mm, "end": v(15.25, -56.33) * mm});
            skLineSegment(sketch, "E1416", {"start": v(15.25, -56.33) * mm, "end": v(15.25, -56.34) * mm});
            skLineSegment(sketch, "E1417", {"start": v(53.5, -34.3) * mm, "end": v(53.49, -34.3) * mm});
            skLineSegment(sketch, "E1418", {"start": v(53.49, -34.3) * mm, "end": v(53.49, -34.3) * mm});
            skLineSegment(sketch, "E1419", {"start": v(53.49, -34.3) * mm, "end": v(53.47, -34.3) * mm});
            skLineSegment(sketch, "E1420", {"start": v(53.47, -34.3) * mm, "end": v(53.47, -34.3) * mm});
            skLineSegment(sketch, "E1421", {"start": v(53.47, -34.3) * mm, "end": v(53.47, -34.29) * mm});
            skLineSegment(sketch, "E1422", {"start": v(53.47, -34.29) * mm, "end": v(53.47, -34.29) * mm});
            skLineSegment(sketch, "E1423", {"start": v(53.47, -34.29) * mm, "end": v(53.47, -34.28) * mm});
            skLineSegment(sketch, "E1424", {"start": v(53.47, -34.28) * mm, "end": v(53.47, -34.28) * mm});
            skLineSegment(sketch, "E1425", {"start": v(53.47, -34.28) * mm, "end": v(53.49, -34.28) * mm});
            skLineSegment(sketch, "E1426", {"start": v(53.49, -34.28) * mm, "end": v(53.49, -34.28) * mm});
            skLineSegment(sketch, "E1427", {"start": v(53.49, -34.28) * mm, "end": v(53.5, -34.29) * mm});
            skLineSegment(sketch, "E1428", {"start": v(53.5, -34.29) * mm, "end": v(53.5, -34.29) * mm});
            skLineSegment(sketch, "E1429", {"start": v(13.62, -40.39) * mm, "end": v(13.62, -40.39) * mm});
            skLineSegment(sketch, "E1430", {"start": v(13.62, -40.39) * mm, "end": v(13.6, -40.4) * mm});
            skLineSegment(sketch, "E1431", {"start": v(13.6, -40.4) * mm, "end": v(13.6, -40.4) * mm});
            skLineSegment(sketch, "E1432", {"start": v(13.6, -40.4) * mm, "end": v(13.59, -40.39) * mm});
            skLineSegment(sketch, "E1433", {"start": v(13.59, -40.39) * mm, "end": v(13.59, -40.39) * mm});
            skLineSegment(sketch, "E1434", {"start": v(13.59, -40.39) * mm, "end": v(13.59, -40.38) * mm});
            skLineSegment(sketch, "E1435", {"start": v(13.59, -40.38) * mm, "end": v(13.6, -40.38) * mm});
            skLineSegment(sketch, "E1436", {"start": v(13.6, -40.38) * mm, "end": v(13.6, -40.38) * mm});
            skLineSegment(sketch, "E1437", {"start": v(13.6, -40.38) * mm, "end": v(13.6, -40.37) * mm});
            skLineSegment(sketch, "E1438", {"start": v(13.6, -40.37) * mm, "end": v(13.6, -40.37) * mm});
            skLineSegment(sketch, "E1439", {"start": v(13.6, -40.37) * mm, "end": v(13.6, -40.38) * mm});
            skLineSegment(sketch, "E1440", {"start": v(13.6, -40.38) * mm, "end": v(13.62, -40.38) * mm});
            skLineSegment(sketch, "E1441", {"start": v(13.62, -40.38) * mm, "end": v(13.62, -40.39) * mm});
            skLineSegment(sketch, "E1442", {"start": v(-17.4, 35.33) * mm, "end": v(-17.4, 35.33) * mm});
            skLineSegment(sketch, "E1443", {"start": v(-17.4, 35.33) * mm, "end": v(-17.4, 35.32) * mm});
            skLineSegment(sketch, "E1444", {"start": v(-17.4, 35.32) * mm, "end": v(-17.4, 35.32) * mm});
            skLineSegment(sketch, "E1445", {"start": v(-17.4, 35.32) * mm, "end": v(-17.42, 35.32) * mm});
            skLineSegment(sketch, "E1446", {"start": v(-17.42, 35.32) * mm, "end": v(-17.42, 35.32) * mm});
            skLineSegment(sketch, "E1447", {"start": v(-17.42, 35.32) * mm, "end": v(-17.42, 35.33) * mm});
            skLineSegment(sketch, "E1448", {"start": v(-17.42, 35.33) * mm, "end": v(-17.42, 35.33) * mm});
            skLineSegment(sketch, "E1449", {"start": v(-17.42, 35.33) * mm, "end": v(-17.42, 35.34) * mm});
            skLineSegment(sketch, "E1450", {"start": v(-17.42, 35.34) * mm, "end": v(-17.42, 35.34) * mm});
            skLineSegment(sketch, "E1451", {"start": v(-17.42, 35.34) * mm, "end": v(-17.4, 35.34) * mm});
            skLineSegment(sketch, "E1452", {"start": v(-17.4, 35.34) * mm, "end": v(-17.4, 35.34) * mm});
            skLineSegment(sketch, "E1453", {"start": v(-17.4, 35.34) * mm, "end": v(-17.4, 35.33) * mm});
            skLineSegment(sketch, "E1454", {"start": v(-53.95, -17.27) * mm, "end": v(-53.95, -17.28) * mm});
            skLineSegment(sketch, "E1455", {"start": v(-53.95, -17.28) * mm, "end": v(-53.96, -17.28) * mm});
            skLineSegment(sketch, "E1456", {"start": v(-53.96, -17.28) * mm, "end": v(-53.96, -17.28) * mm});
            skLineSegment(sketch, "E1457", {"start": v(-53.96, -17.28) * mm, "end": v(-53.97, -17.28) * mm});
            skLineSegment(sketch, "E1458", {"start": v(-53.97, -17.28) * mm, "end": v(-53.97, -17.28) * mm});
            skLineSegment(sketch, "E1459", {"start": v(-53.97, -17.28) * mm, "end": v(-53.97, -17.27) * mm});
            skLineSegment(sketch, "E1460", {"start": v(-53.97, -17.27) * mm, "end": v(-53.97, -17.27) * mm});
            skLineSegment(sketch, "E1461", {"start": v(-53.97, -17.27) * mm, "end": v(-53.97, -17.26) * mm});
            skLineSegment(sketch, "E1462", {"start": v(-53.97, -17.26) * mm, "end": v(-53.97, -17.26) * mm});
            skLineSegment(sketch, "E1463", {"start": v(-53.97, -17.26) * mm, "end": v(-53.96, -17.26) * mm});
            skLineSegment(sketch, "E1464", {"start": v(-53.96, -17.26) * mm, "end": v(-53.96, -17.26) * mm});
            skLineSegment(sketch, "E1465", {"start": v(-53.96, -17.26) * mm, "end": v(-53.95, -17.27) * mm});
            skLineSegment(sketch, "E1466", {"start": v(-53.95, -17.27) * mm, "end": v(-53.95, -17.27) * mm});
            skLineSegment(sketch, "E1467", {"start": v(12.8, 20.7) * mm, "end": v(12.8, 20.7) * mm});
            skLineSegment(sketch, "E1468", {"start": v(12.8, 20.7) * mm, "end": v(12.8, 20.69) * mm});
            skLineSegment(sketch, "E1469", {"start": v(12.8, 20.69) * mm, "end": v(12.8, 20.69) * mm});
            skLineSegment(sketch, "E1470", {"start": v(12.8, 20.69) * mm, "end": v(12.78, 20.69) * mm});
            skLineSegment(sketch, "E1471", {"start": v(12.78, 20.69) * mm, "end": v(12.78, 20.7) * mm});
            skLineSegment(sketch, "E1472", {"start": v(12.78, 20.7) * mm, "end": v(12.78, 20.7) * mm});
            skLineSegment(sketch, "E1473", {"start": v(12.78, 20.7) * mm, "end": v(12.78, 20.71) * mm});
            skLineSegment(sketch, "E1474", {"start": v(12.78, 20.71) * mm, "end": v(12.78, 20.71) * mm});
            skLineSegment(sketch, "E1475", {"start": v(12.78, 20.71) * mm, "end": v(12.8, 20.71) * mm});
            skLineSegment(sketch, "E1476", {"start": v(12.8, 20.71) * mm, "end": v(12.8, 20.71) * mm});
            skLineSegment(sketch, "E1477", {"start": v(12.8, 20.71) * mm, "end": v(12.8, 20.7) * mm});
            skLineSegment(sketch, "E1478", {"start": v(-51.92, -23.62) * mm, "end": v(-51.92, -23.63) * mm});
            skLineSegment(sketch, "E1479", {"start": v(-51.92, -23.63) * mm, "end": v(-51.92, -23.63) * mm});
            skLineSegment(sketch, "E1480", {"start": v(-51.92, -23.63) * mm, "end": v(-51.94, -23.63) * mm});
            skLineSegment(sketch, "E1481", {"start": v(-51.94, -23.63) * mm, "end": v(-51.94, -23.63) * mm});
            skLineSegment(sketch, "E1482", {"start": v(-51.94, -23.63) * mm, "end": v(-51.94, -23.62) * mm});
            skLineSegment(sketch, "E1483", {"start": v(-51.94, -23.62) * mm, "end": v(-51.94, -23.62) * mm});
            skLineSegment(sketch, "E1484", {"start": v(-51.94, -23.62) * mm, "end": v(-51.94, -23.61) * mm});
            skLineSegment(sketch, "E1485", {"start": v(-51.94, -23.61) * mm, "end": v(-51.94, -23.61) * mm});
            skLineSegment(sketch, "E1486", {"start": v(-51.94, -23.61) * mm, "end": v(-51.92, -23.61) * mm});
            skLineSegment(sketch, "E1487", {"start": v(-51.92, -23.61) * mm, "end": v(-51.92, -23.61) * mm});
            skLineSegment(sketch, "E1488", {"start": v(-51.92, -23.61) * mm, "end": v(-51.92, -23.62) * mm});
            skLineSegment(sketch, "E1489", {"start": v(-51.92, -23.62) * mm, "end": v(-51.92, -23.62) * mm});
            skLineSegment(sketch, "E1490", {"start": v(-16.2, 33.14) * mm, "end": v(-16.21, 33.13) * mm});
            skLineSegment(sketch, "E1491", {"start": v(-16.21, 33.13) * mm, "end": v(-16.21, 33.13) * mm});
            skLineSegment(sketch, "E1492", {"start": v(-16.21, 33.13) * mm, "end": v(-16.22, 33.13) * mm});
            skLineSegment(sketch, "E1493", {"start": v(-16.22, 33.13) * mm, "end": v(-16.22, 33.13) * mm});
            skLineSegment(sketch, "E1494", {"start": v(-16.22, 33.13) * mm, "end": v(-16.23, 33.14) * mm});
            skLineSegment(sketch, "E1495", {"start": v(-16.23, 33.14) * mm, "end": v(-16.23, 33.14) * mm});
            skLineSegment(sketch, "E1496", {"start": v(-16.23, 33.14) * mm, "end": v(-16.22, 33.15) * mm});
            skLineSegment(sketch, "E1497", {"start": v(-16.22, 33.15) * mm, "end": v(-16.22, 33.15) * mm});
            skLineSegment(sketch, "E1498", {"start": v(-16.22, 33.15) * mm, "end": v(-16.21, 33.15) * mm});
            skLineSegment(sketch, "E1499", {"start": v(-16.21, 33.15) * mm, "end": v(-16.21, 33.15) * mm});
            skLineSegment(sketch, "E1500", {"start": v(-16.21, 33.15) * mm, "end": v(-16.2, 33.14) * mm});
            skLineSegment(sketch, "E1501", {"start": v(-31.65, 32.36) * mm, "end": v(-31.65, 32.36) * mm});
            skLineSegment(sketch, "E1502", {"start": v(-31.65, 32.36) * mm, "end": v(-31.65, 32.35) * mm});
            skLineSegment(sketch, "E1503", {"start": v(-31.65, 32.35) * mm, "end": v(-31.65, 32.35) * mm});
            skLineSegment(sketch, "E1504", {"start": v(-31.65, 32.35) * mm, "end": v(-31.66, 32.35) * mm});
            skLineSegment(sketch, "E1505", {"start": v(-31.66, 32.35) * mm, "end": v(-31.67, 32.35) * mm});
            skLineSegment(sketch, "E1506", {"start": v(-31.67, 32.35) * mm, "end": v(-31.67, 32.35) * mm});
            skLineSegment(sketch, "E1507", {"start": v(-31.67, 32.35) * mm, "end": v(-31.67, 32.36) * mm});
            skLineSegment(sketch, "E1508", {"start": v(-31.67, 32.36) * mm, "end": v(-31.67, 32.36) * mm});
            skLineSegment(sketch, "E1509", {"start": v(-31.67, 32.36) * mm, "end": v(-31.67, 32.37) * mm});
            skLineSegment(sketch, "E1510", {"start": v(-31.67, 32.37) * mm, "end": v(-31.67, 32.37) * mm});
            skLineSegment(sketch, "E1511", {"start": v(-31.67, 32.37) * mm, "end": v(-31.66, 32.37) * mm});
            skLineSegment(sketch, "E1512", {"start": v(-31.66, 32.37) * mm, "end": v(-31.65, 32.37) * mm});
            skLineSegment(sketch, "E1513", {"start": v(-31.65, 32.37) * mm, "end": v(-31.65, 32.36) * mm});
            skLineSegment(sketch, "E1514", {"start": v(-1.77, 23.04) * mm, "end": v(-1.77, 23.04) * mm});
            skLineSegment(sketch, "E1515", {"start": v(-1.77, 23.04) * mm, "end": v(-1.78, 23.03) * mm});
            skLineSegment(sketch, "E1516", {"start": v(-1.78, 23.03) * mm, "end": v(-1.78, 23.03) * mm});
            skLineSegment(sketch, "E1517", {"start": v(-1.78, 23.03) * mm, "end": v(-1.8, 23.03) * mm});
            skLineSegment(sketch, "E1518", {"start": v(-1.8, 23.03) * mm, "end": v(-1.8, 23.03) * mm});
            skLineSegment(sketch, "E1519", {"start": v(-1.8, 23.04) * mm, "end": v(-1.8, 23.05) * mm});
            skLineSegment(sketch, "E1520", {"start": v(-1.8, 23.05) * mm, "end": v(-1.8, 23.05) * mm});
            skLineSegment(sketch, "E1521", {"start": v(-1.8, 23.05) * mm, "end": v(-1.78, 23.05) * mm});
            skLineSegment(sketch, "E1522", {"start": v(-1.78, 23.05) * mm, "end": v(-1.78, 23.05) * mm});
            skLineSegment(sketch, "E1523", {"start": v(-1.78, 23.05) * mm, "end": v(-1.77, 23.04) * mm});
            skLineSegment(sketch, "E1524", {"start": v(-31.75, 34.57) * mm, "end": v(-31.75, 34.57) * mm});
            skLineSegment(sketch, "E1525", {"start": v(-31.75, 34.57) * mm, "end": v(-31.75, 34.56) * mm});
            skLineSegment(sketch, "E1526", {"start": v(-31.75, 34.56) * mm, "end": v(-31.75, 34.56) * mm});
            skLineSegment(sketch, "E1527", {"start": v(-31.75, 34.56) * mm, "end": v(-31.76, 34.56) * mm});
            skLineSegment(sketch, "E1528", {"start": v(-31.76, 34.56) * mm, "end": v(-31.77, 34.56) * mm});
            skLineSegment(sketch, "E1529", {"start": v(-31.77, 34.56) * mm, "end": v(-31.77, 34.56) * mm});
            skLineSegment(sketch, "E1530", {"start": v(-31.77, 34.56) * mm, "end": v(-31.77, 34.57) * mm});
            skLineSegment(sketch, "E1531", {"start": v(-31.77, 34.57) * mm, "end": v(-31.77, 34.57) * mm});
            skLineSegment(sketch, "E1532", {"start": v(-31.77, 34.57) * mm, "end": v(-31.77, 34.58) * mm});
            skLineSegment(sketch, "E1533", {"start": v(-31.77, 34.58) * mm, "end": v(-31.77, 34.58) * mm});
            skLineSegment(sketch, "E1534", {"start": v(-31.77, 34.58) * mm, "end": v(-31.76, 34.58) * mm});
            skLineSegment(sketch, "E1535", {"start": v(-31.76, 34.58) * mm, "end": v(-31.75, 34.58) * mm});
            skLineSegment(sketch, "E1536", {"start": v(-31.75, 34.58) * mm, "end": v(-31.75, 34.57) * mm});
            skLineSegment(sketch, "E1537", {"start": v(55.27, -32) * mm, "end": v(55.27, -32) * mm});
            skLineSegment(sketch, "E1538", {"start": v(55.27, -32) * mm, "end": v(55.27, -32.01) * mm});
            skLineSegment(sketch, "E1539", {"start": v(55.27, -32.01) * mm, "end": v(55.27, -32.01) * mm});
            skLineSegment(sketch, "E1540", {"start": v(55.27, -32.01) * mm, "end": v(55.26, -32.01) * mm});
            skLineSegment(sketch, "E1541", {"start": v(55.26, -32.01) * mm, "end": v(55.25, -32.01) * mm});
            skLineSegment(sketch, "E1542", {"start": v(55.25, -32.01) * mm, "end": v(55.25, -32.01) * mm});
            skLineSegment(sketch, "E1543", {"start": v(55.25, -32.01) * mm, "end": v(55.25, -32) * mm});
            skLineSegment(sketch, "E1544", {"start": v(55.25, -32) * mm, "end": v(55.25, -32) * mm});
            skLineSegment(sketch, "E1545", {"start": v(55.25, -32) * mm, "end": v(55.26, -32) * mm});
            skLineSegment(sketch, "E1546", {"start": v(55.26, -32) * mm, "end": v(55.27, -32) * mm});
            skLineSegment(sketch, "E1547", {"start": v(13.87, -41.91) * mm, "end": v(13.87, -41.91) * mm});
            skLineSegment(sketch, "E1548", {"start": v(13.87, -41.91) * mm, "end": v(13.86, -41.92) * mm});
            skLineSegment(sketch, "E1549", {"start": v(13.86, -41.92) * mm, "end": v(13.86, -41.92) * mm});
            skLineSegment(sketch, "E1550", {"start": v(13.86, -41.92) * mm, "end": v(13.85, -41.92) * mm});
            skLineSegment(sketch, "E1551", {"start": v(13.85, -41.92) * mm, "end": v(13.85, -41.92) * mm});
            skLineSegment(sketch, "E1552", {"start": v(13.85, -41.92) * mm, "end": v(13.84, -41.91) * mm});
            skLineSegment(sketch, "E1553", {"start": v(13.84, -41.91) * mm, "end": v(13.84, -41.91) * mm});
            skLineSegment(sketch, "E1554", {"start": v(13.84, -41.91) * mm, "end": v(13.84, -41.9) * mm});
            skLineSegment(sketch, "E1555", {"start": v(13.84, -41.9) * mm, "end": v(13.85, -41.9) * mm});
            skLineSegment(sketch, "E1556", {"start": v(13.85, -41.9) * mm, "end": v(13.85, -41.9) * mm});
            skLineSegment(sketch, "E1557", {"start": v(13.85, -41.9) * mm, "end": v(13.86, -41.9) * mm});
            skLineSegment(sketch, "E1558", {"start": v(13.86, -41.9) * mm, "end": v(13.86, -41.9) * mm});
            skLineSegment(sketch, "E1559", {"start": v(13.86, -41.9) * mm, "end": v(13.87, -41.9) * mm});
            skLineSegment(sketch, "E1560", {"start": v(13.87, -41.9) * mm, "end": v(13.87, -41.91) * mm});
            skLineSegment(sketch, "E1561", {"start": v(-24.67, 20.57) * mm, "end": v(-24.67, 20.47) * mm});
            skLineSegment(sketch, "E1562", {"start": v(-24.67, 20.47) * mm, "end": v(-24.9, 20.16) * mm});
            skLineSegment(sketch, "E1563", {"start": v(-24.9, 20.16) * mm, "end": v(-24.93, 20.13) * mm});
            skLineSegment(sketch, "E1564", {"start": v(-24.93, 20.13) * mm, "end": v(-24.97, 20.11) * mm});
            skLineSegment(sketch, "E1565", {"start": v(-24.97, 20.11) * mm, "end": v(-25.4, 20.11) * mm});
            skLineSegment(sketch, "E1566", {"start": v(-25.4, 20.11) * mm, "end": v(-25.44, 20.13) * mm});
            skLineSegment(sketch, "E1567", {"start": v(-25.44, 20.13) * mm, "end": v(-25.48, 20.16) * mm});
            skLineSegment(sketch, "E1568", {"start": v(-25.48, 20.16) * mm, "end": v(-25.7, 20.47) * mm});
            skLineSegment(sketch, "E1569", {"start": v(-25.7, 20.47) * mm, "end": v(-25.7, 20.57) * mm});
            skLineSegment(sketch, "E1570", {"start": v(-25.7, 20.57) * mm, "end": v(-25.7, 20.68) * mm});
            skLineSegment(sketch, "E1571", {"start": v(-25.7, 20.68) * mm, "end": v(-25.48, 21) * mm});
            skLineSegment(sketch, "E1572", {"start": v(-25.48, 21) * mm, "end": v(-25.44, 21.01) * mm});
            skLineSegment(sketch, "E1573", {"start": v(-25.44, 21.01) * mm, "end": v(-25.4, 21.04) * mm});
            skLineSegment(sketch, "E1574", {"start": v(-25.4, 21.04) * mm, "end": v(-24.97, 21.04) * mm});
            skLineSegment(sketch, "E1575", {"start": v(-24.97, 21.04) * mm, "end": v(-24.93, 21.01) * mm});
            skLineSegment(sketch, "E1576", {"start": v(-24.93, 21.01) * mm, "end": v(-24.9, 21) * mm});
            skLineSegment(sketch, "E1577", {"start": v(-24.9, 21) * mm, "end": v(-24.67, 20.68) * mm});
            skLineSegment(sketch, "E1578", {"start": v(-24.67, 20.68) * mm, "end": v(-24.67, 20.57) * mm});
            skLineSegment(sketch, "E1579", {"start": v(-9.23, 13.82) * mm, "end": v(-9.23, 13.74) * mm});
            skLineSegment(sketch, "E1580", {"start": v(-9.23, 13.74) * mm, "end": v(-9.39, 13.5) * mm});
            skLineSegment(sketch, "E1581", {"start": v(-9.39, 13.5) * mm, "end": v(-9.42, 13.49) * mm});
            skLineSegment(sketch, "E1582", {"start": v(-9.42, 13.49) * mm, "end": v(-9.45, 13.47) * mm});
            skLineSegment(sketch, "E1583", {"start": v(-9.45, 13.47) * mm, "end": v(-9.77, 13.47) * mm});
            skLineSegment(sketch, "E1584", {"start": v(-9.77, 13.47) * mm, "end": v(-9.8, 13.49) * mm});
            skLineSegment(sketch, "E1585", {"start": v(-9.8, 13.49) * mm, "end": v(-9.83, 13.5) * mm});
            skLineSegment(sketch, "E1586", {"start": v(-9.83, 13.5) * mm, "end": v(-10, 13.74) * mm});
            skLineSegment(sketch, "E1587", {"start": v(-10, 13.74) * mm, "end": v(-10, 13.82) * mm});
            skLineSegment(sketch, "E1588", {"start": v(-10, 13.82) * mm, "end": v(-10, 13.9) * mm});
            skLineSegment(sketch, "E1589", {"start": v(-10, 13.9) * mm, "end": v(-9.83, 14.13) * mm});
            skLineSegment(sketch, "E1590", {"start": v(-9.83, 14.13) * mm, "end": v(-9.8, 14.15) * mm});
            skLineSegment(sketch, "E1591", {"start": v(-9.8, 14.15) * mm, "end": v(-9.77, 14.17) * mm});
            skLineSegment(sketch, "E1592", {"start": v(-9.77, 14.17) * mm, "end": v(-9.45, 14.17) * mm});
            skLineSegment(sketch, "E1593", {"start": v(-9.45, 14.17) * mm, "end": v(-9.42, 14.15) * mm});
            skLineSegment(sketch, "E1594", {"start": v(-9.42, 14.15) * mm, "end": v(-9.39, 14.13) * mm});
            skLineSegment(sketch, "E1595", {"start": v(-9.39, 14.13) * mm, "end": v(-9.23, 13.9) * mm});
            skLineSegment(sketch, "E1596", {"start": v(-9.23, 13.9) * mm, "end": v(-9.23, 13.82) * mm});
            skLineSegment(sketch, "E1597", {"start": v(-52.56, -1.27) * mm, "end": v(-52.56, -1.4) * mm});
            skLineSegment(sketch, "E1598", {"start": v(-52.56, -1.4) * mm, "end": v(-52.7, -1.77) * mm});
            skLineSegment(sketch, "E1599", {"start": v(-52.7, -1.77) * mm, "end": v(-52.98, -2.1) * mm});
            skLineSegment(sketch, "E1600", {"start": v(-52.98, -2.1) * mm, "end": v(-53.06, -2.14) * mm});
            skLineSegment(sketch, "E1601", {"start": v(-53.06, -2.14) * mm, "end": v(-53.14, -2.18) * mm});
            skLineSegment(sketch, "E1602", {"start": v(-53.14, -2.18) * mm, "end": v(-53.56, -2.27) * mm});
            skLineSegment(sketch, "E1603", {"start": v(-53.56, -2.27) * mm, "end": v(-53.98, -2.18) * mm});
            skLineSegment(sketch, "E1604", {"start": v(-53.98, -2.18) * mm, "end": v(-54.06, -2.14) * mm});
            skLineSegment(sketch, "E1605", {"start": v(-54.06, -2.14) * mm, "end": v(-54.14, -2.1) * mm});
            skLineSegment(sketch, "E1606", {"start": v(-54.14, -2.1) * mm, "end": v(-54.42, -1.77) * mm});
            skLineSegment(sketch, "E1607", {"start": v(-54.42, -1.77) * mm, "end": v(-54.56, -1.4) * mm});
            skLineSegment(sketch, "E1608", {"start": v(-54.56, -1.4) * mm, "end": v(-54.56, -1.27) * mm});
            skLineSegment(sketch, "E1609", {"start": v(-54.56, -1.27) * mm, "end": v(-54.56, -1.15) * mm});
            skLineSegment(sketch, "E1610", {"start": v(-54.56, -1.15) * mm, "end": v(-54.42, -0.77) * mm});
            skLineSegment(sketch, "E1611", {"start": v(-54.42, -0.77) * mm, "end": v(-54.14, -0.45) * mm});
            skLineSegment(sketch, "E1612", {"start": v(-54.14, -0.45) * mm, "end": v(-54.06, -0.4) * mm});
            skLineSegment(sketch, "E1613", {"start": v(-54.06, -0.4) * mm, "end": v(-53.98, -0.36) * mm});
            skLineSegment(sketch, "E1614", {"start": v(-53.98, -0.36) * mm, "end": v(-53.56, -0.27) * mm});
            skLineSegment(sketch, "E1615", {"start": v(-53.56, -0.27) * mm, "end": v(-53.14, -0.36) * mm});
            skLineSegment(sketch, "E1616", {"start": v(-53.14, -0.36) * mm, "end": v(-53.06, -0.4) * mm});
            skLineSegment(sketch, "E1617", {"start": v(-53.06, -0.4) * mm, "end": v(-52.98, -0.45) * mm});
            skLineSegment(sketch, "E1618", {"start": v(-52.98, -0.45) * mm, "end": v(-52.7, -0.77) * mm});
            skLineSegment(sketch, "E1619", {"start": v(-52.7, -0.77) * mm, "end": v(-52.56, -1.15) * mm});
            skLineSegment(sketch, "E1620", {"start": v(-52.56, -1.15) * mm, "end": v(-52.56, -1.27) * mm});
            skLineSegment(sketch, "E1621", {"start": v(-52.56, -9.17) * mm, "end": v(-52.56, -9.3) * mm});
            skLineSegment(sketch, "E1622", {"start": v(-52.56, -9.3) * mm, "end": v(-52.7, -9.67) * mm});
            skLineSegment(sketch, "E1623", {"start": v(-52.7, -9.67) * mm, "end": v(-52.98, -10) * mm});
            skLineSegment(sketch, "E1624", {"start": v(-52.98, -10) * mm, "end": v(-53.06, -10.04) * mm});
            skLineSegment(sketch, "E1625", {"start": v(-53.06, -10.04) * mm, "end": v(-53.14, -10.08) * mm});
            skLineSegment(sketch, "E1626", {"start": v(-53.14, -10.08) * mm, "end": v(-53.56, -10.17) * mm});
            skLineSegment(sketch, "E1627", {"start": v(-53.56, -10.17) * mm, "end": v(-53.98, -10.08) * mm});
            skLineSegment(sketch, "E1628", {"start": v(-53.98, -10.08) * mm, "end": v(-54.06, -10.04) * mm});
            skLineSegment(sketch, "E1629", {"start": v(-54.06, -10.04) * mm, "end": v(-54.14, -10) * mm});
            skLineSegment(sketch, "E1630", {"start": v(-54.14, -10) * mm, "end": v(-54.42, -9.67) * mm});
            skLineSegment(sketch, "E1631", {"start": v(-54.42, -9.67) * mm, "end": v(-54.56, -9.3) * mm});
            skLineSegment(sketch, "E1632", {"start": v(-54.56, -9.3) * mm, "end": v(-54.56, -9.17) * mm});
            skLineSegment(sketch, "E1633", {"start": v(-54.56, -9.17) * mm, "end": v(-54.56, -9.04) * mm});
            skLineSegment(sketch, "E1634", {"start": v(-54.56, -9.04) * mm, "end": v(-54.42, -8.67) * mm});
            skLineSegment(sketch, "E1635", {"start": v(-54.42, -8.67) * mm, "end": v(-54.14, -8.35) * mm});
            skLineSegment(sketch, "E1636", {"start": v(-54.14, -8.35) * mm, "end": v(-54.06, -8.3) * mm});
            skLineSegment(sketch, "E1637", {"start": v(-54.06, -8.3) * mm, "end": v(-53.98, -8.26) * mm});
            skLineSegment(sketch, "E1638", {"start": v(-53.98, -8.26) * mm, "end": v(-53.56, -8.17) * mm});
            skLineSegment(sketch, "E1639", {"start": v(-53.56, -8.17) * mm, "end": v(-53.14, -8.26) * mm});
            skLineSegment(sketch, "E1640", {"start": v(-53.14, -8.26) * mm, "end": v(-53.06, -8.3) * mm});
            skLineSegment(sketch, "E1641", {"start": v(-53.06, -8.3) * mm, "end": v(-52.98, -8.35) * mm});
            skLineSegment(sketch, "E1642", {"start": v(-52.98, -8.35) * mm, "end": v(-52.7, -8.67) * mm});
            skLineSegment(sketch, "E1643", {"start": v(-52.7, -8.67) * mm, "end": v(-52.56, -9.04) * mm});
            skLineSegment(sketch, "E1644", {"start": v(-52.56, -9.04) * mm, "end": v(-52.56, -9.17) * mm});
            skLineSegment(sketch, "E1645", {"start": v(-41.28, 57.1) * mm, "end": v(-41.28, 56.79) * mm});
            skLineSegment(sketch, "E1646", {"start": v(-41.28, 56.79) * mm, "end": v(-41.61, 55.85) * mm});
            skLineSegment(sketch, "E1647", {"start": v(-41.61, 55.85) * mm, "end": v(-42.33, 55.05) * mm});
            skLineSegment(sketch, "E1648", {"start": v(-42.33, 55.05) * mm, "end": v(-42.53, 54.94) * mm});
            skLineSegment(sketch, "E1649", {"start": v(-42.53, 54.94) * mm, "end": v(-42.72, 54.82) * mm});
            skLineSegment(sketch, "E1650", {"start": v(-42.72, 54.82) * mm, "end": v(-43.78, 54.6) * mm});
            skLineSegment(sketch, "E1651", {"start": v(-43.78, 54.6) * mm, "end": v(-44.83, 54.82) * mm});
            skLineSegment(sketch, "E1652", {"start": v(-44.83, 54.82) * mm, "end": v(-45.03, 54.94) * mm});
            skLineSegment(sketch, "E1653", {"start": v(-45.03, 54.94) * mm, "end": v(-45.22, 55.05) * mm});
            skLineSegment(sketch, "E1654", {"start": v(-45.22, 55.05) * mm, "end": v(-45.94, 55.85) * mm});
            skLineSegment(sketch, "E1655", {"start": v(-45.94, 55.85) * mm, "end": v(-46.28, 56.79) * mm});
            skLineSegment(sketch, "E1656", {"start": v(-46.28, 56.79) * mm, "end": v(-46.28, 57.1) * mm});
            skLineSegment(sketch, "E1657", {"start": v(-46.28, 57.1) * mm, "end": v(-46.28, 57.41) * mm});
            skLineSegment(sketch, "E1658", {"start": v(-46.28, 57.41) * mm, "end": v(-45.94, 58.35) * mm});
            skLineSegment(sketch, "E1659", {"start": v(-45.94, 58.35) * mm, "end": v(-45.22, 59.15) * mm});
            skLineSegment(sketch, "E1660", {"start": v(-45.22, 59.15) * mm, "end": v(-45.03, 59.27) * mm});
            skLineSegment(sketch, "E1661", {"start": v(-45.03, 59.27) * mm, "end": v(-44.83, 59.38) * mm});
            skLineSegment(sketch, "E1662", {"start": v(-44.83, 59.38) * mm, "end": v(-43.78, 59.6) * mm});
            skLineSegment(sketch, "E1663", {"start": v(-43.78, 59.6) * mm, "end": v(-42.72, 59.38) * mm});
            skLineSegment(sketch, "E1664", {"start": v(-42.72, 59.38) * mm, "end": v(-42.53, 59.27) * mm});
            skLineSegment(sketch, "E1665", {"start": v(-42.53, 59.27) * mm, "end": v(-42.33, 59.15) * mm});
            skLineSegment(sketch, "E1666", {"start": v(-42.33, 59.15) * mm, "end": v(-41.61, 58.35) * mm});
            skLineSegment(sketch, "E1667", {"start": v(-41.61, 58.35) * mm, "end": v(-41.28, 57.41) * mm});
            skLineSegment(sketch, "E1668", {"start": v(-41.28, 57.41) * mm, "end": v(-41.28, 57.1) * mm});
            skLineSegment(sketch, "E1669", {"start": v(-41.28, 38.1) * mm, "end": v(-41.28, 37.79) * mm});
            skLineSegment(sketch, "E1670", {"start": v(-41.28, 37.79) * mm, "end": v(-41.61, 36.85) * mm});
            skLineSegment(sketch, "E1671", {"start": v(-41.61, 36.85) * mm, "end": v(-42.33, 36.05) * mm});
            skLineSegment(sketch, "E1672", {"start": v(-42.33, 36.05) * mm, "end": v(-42.53, 35.93) * mm});
            skLineSegment(sketch, "E1673", {"start": v(-42.53, 35.93) * mm, "end": v(-42.72, 35.82) * mm});
            skLineSegment(sketch, "E1674", {"start": v(-42.72, 35.82) * mm, "end": v(-43.78, 35.6) * mm});
            skLineSegment(sketch, "E1675", {"start": v(-43.78, 35.6) * mm, "end": v(-44.83, 35.82) * mm});
            skLineSegment(sketch, "E1676", {"start": v(-44.83, 35.82) * mm, "end": v(-45.03, 35.93) * mm});
            skLineSegment(sketch, "E1677", {"start": v(-45.03, 35.93) * mm, "end": v(-45.22, 36.05) * mm});
            skLineSegment(sketch, "E1678", {"start": v(-45.22, 36.05) * mm, "end": v(-45.94, 36.85) * mm});
            skLineSegment(sketch, "E1679", {"start": v(-45.94, 36.85) * mm, "end": v(-46.28, 37.79) * mm});
            skLineSegment(sketch, "E1680", {"start": v(-46.28, 37.79) * mm, "end": v(-46.28, 38.1) * mm});
            skLineSegment(sketch, "E1681", {"start": v(-46.28, 38.1) * mm, "end": v(-46.28, 38.41) * mm});
            skLineSegment(sketch, "E1682", {"start": v(-46.28, 38.41) * mm, "end": v(-45.94, 39.35) * mm});
            skLineSegment(sketch, "E1683", {"start": v(-45.94, 39.35) * mm, "end": v(-45.22, 40.15) * mm});
            skLineSegment(sketch, "E1684", {"start": v(-45.22, 40.15) * mm, "end": v(-45.03, 40.26) * mm});
            skLineSegment(sketch, "E1685", {"start": v(-45.03, 40.26) * mm, "end": v(-44.83, 40.38) * mm});
            skLineSegment(sketch, "E1686", {"start": v(-44.83, 40.38) * mm, "end": v(-43.78, 40.6) * mm});
            skLineSegment(sketch, "E1687", {"start": v(-43.78, 40.6) * mm, "end": v(-42.72, 40.38) * mm});
            skLineSegment(sketch, "E1688", {"start": v(-42.72, 40.38) * mm, "end": v(-42.53, 40.26) * mm});
            skLineSegment(sketch, "E1689", {"start": v(-42.53, 40.26) * mm, "end": v(-42.33, 40.15) * mm});
            skLineSegment(sketch, "E1690", {"start": v(-42.33, 40.15) * mm, "end": v(-41.61, 39.35) * mm});
            skLineSegment(sketch, "E1691", {"start": v(-41.61, 39.35) * mm, "end": v(-41.28, 38.41) * mm});
            skLineSegment(sketch, "E1692", {"start": v(-41.28, 38.41) * mm, "end": v(-41.28, 38.1) * mm});
            skLineSegment(sketch, "E1693", {"start": v(-27.3, 58.42) * mm, "end": v(-27.3, 58.31) * mm});
            skLineSegment(sketch, "E1694", {"start": v(-27.3, 58.31) * mm, "end": v(-27.5, 58) * mm});
            skLineSegment(sketch, "E1695", {"start": v(-27.5, 58) * mm, "end": v(-27.55, 57.98) * mm});
            skLineSegment(sketch, "E1696", {"start": v(-27.55, 57.98) * mm, "end": v(-27.59, 57.96) * mm});
            skLineSegment(sketch, "E1697", {"start": v(-27.59, 57.96) * mm, "end": v(-28.02, 57.96) * mm});
            skLineSegment(sketch, "E1698", {"start": v(-28.02, 57.96) * mm, "end": v(-28.05, 57.98) * mm});
            skLineSegment(sketch, "E1699", {"start": v(-28.05, 57.98) * mm, "end": v(-28.1, 58) * mm});
            skLineSegment(sketch, "E1700", {"start": v(-28.1, 58) * mm, "end": v(-28.3, 58.32) * mm});
            skLineSegment(sketch, "E1701", {"start": v(-28.3, 58.32) * mm, "end": v(-28.3, 58.42) * mm});
            skLineSegment(sketch, "E1702", {"start": v(-28.3, 58.42) * mm, "end": v(-28.3, 58.53) * mm});
            skLineSegment(sketch, "E1703", {"start": v(-28.3, 58.53) * mm, "end": v(-28.1, 58.84) * mm});
            skLineSegment(sketch, "E1704", {"start": v(-28.1, 58.84) * mm, "end": v(-28.05, 58.86) * mm});
            skLineSegment(sketch, "E1705", {"start": v(-28.05, 58.86) * mm, "end": v(-28.02, 58.88) * mm});
            skLineSegment(sketch, "E1706", {"start": v(-28.02, 58.88) * mm, "end": v(-27.59, 58.88) * mm});
            skLineSegment(sketch, "E1707", {"start": v(-27.59, 58.88) * mm, "end": v(-27.55, 58.86) * mm});
            skLineSegment(sketch, "E1708", {"start": v(-27.55, 58.86) * mm, "end": v(-27.5, 58.84) * mm});
            skLineSegment(sketch, "E1709", {"start": v(-27.5, 58.84) * mm, "end": v(-27.3, 58.53) * mm});
            skLineSegment(sketch, "E1710", {"start": v(-27.3, 58.53) * mm, "end": v(-27.3, 58.42) * mm});
            skLineSegment(sketch, "E1711", {"start": v(-27.3, 60.96) * mm, "end": v(-27.3, 60.85) * mm});
            skLineSegment(sketch, "E1712", {"start": v(-27.3, 60.85) * mm, "end": v(-27.5, 60.54) * mm});
            skLineSegment(sketch, "E1713", {"start": v(-27.5, 60.54) * mm, "end": v(-27.55, 60.52) * mm});
            skLineSegment(sketch, "E1714", {"start": v(-27.55, 60.52) * mm, "end": v(-27.59, 60.5) * mm});
            skLineSegment(sketch, "E1715", {"start": v(-27.59, 60.5) * mm, "end": v(-28.02, 60.5) * mm});
            skLineSegment(sketch, "E1716", {"start": v(-28.02, 60.5) * mm, "end": v(-28.05, 60.52) * mm});
            skLineSegment(sketch, "E1717", {"start": v(-28.05, 60.52) * mm, "end": v(-28.1, 60.54) * mm});
            skLineSegment(sketch, "E1718", {"start": v(-28.1, 60.54) * mm, "end": v(-28.3, 60.86) * mm});
            skLineSegment(sketch, "E1719", {"start": v(-28.3, 60.86) * mm, "end": v(-28.3, 60.96) * mm});
            skLineSegment(sketch, "E1720", {"start": v(-28.3, 60.96) * mm, "end": v(-28.3, 61.07) * mm});
            skLineSegment(sketch, "E1721", {"start": v(-28.3, 61.07) * mm, "end": v(-28.1, 61.38) * mm});
            skLineSegment(sketch, "E1722", {"start": v(-28.1, 61.38) * mm, "end": v(-28.05, 61.4) * mm});
            skLineSegment(sketch, "E1723", {"start": v(-28.05, 61.4) * mm, "end": v(-28.02, 61.42) * mm});
            skLineSegment(sketch, "E1724", {"start": v(-28.02, 61.42) * mm, "end": v(-27.59, 61.42) * mm});
            skLineSegment(sketch, "E1725", {"start": v(-27.59, 61.42) * mm, "end": v(-27.55, 61.4) * mm});
            skLineSegment(sketch, "E1726", {"start": v(-27.55, 61.4) * mm, "end": v(-27.5, 61.38) * mm});
            skLineSegment(sketch, "E1727", {"start": v(-27.5, 61.38) * mm, "end": v(-27.3, 61.07) * mm});
            skLineSegment(sketch, "E1728", {"start": v(-27.3, 61.07) * mm, "end": v(-27.3, 60.96) * mm});
            skLineSegment(sketch, "E1729", {"start": v(-24.75, 58.42) * mm, "end": v(-24.75, 58.31) * mm});
            skLineSegment(sketch, "E1730", {"start": v(-24.75, 58.31) * mm, "end": v(-24.97, 58) * mm});
            skLineSegment(sketch, "E1731", {"start": v(-24.97, 58) * mm, "end": v(-25, 57.98) * mm});
            skLineSegment(sketch, "E1732", {"start": v(-25, 57.98) * mm, "end": v(-25.05, 57.96) * mm});
            skLineSegment(sketch, "E1733", {"start": v(-25.05, 57.96) * mm, "end": v(-25.48, 57.96) * mm});
            skLineSegment(sketch, "E1734", {"start": v(-25.48, 57.96) * mm, "end": v(-25.51, 57.98) * mm});
            skLineSegment(sketch, "E1735", {"start": v(-25.51, 57.98) * mm, "end": v(-25.55, 58) * mm});
            skLineSegment(sketch, "E1736", {"start": v(-25.55, 58) * mm, "end": v(-25.77, 58.32) * mm});
            skLineSegment(sketch, "E1737", {"start": v(-25.77, 58.32) * mm, "end": v(-25.77, 58.42) * mm});
            skLineSegment(sketch, "E1738", {"start": v(-25.77, 58.42) * mm, "end": v(-25.77, 58.53) * mm});
            skLineSegment(sketch, "E1739", {"start": v(-25.77, 58.53) * mm, "end": v(-25.55, 58.84) * mm});
            skLineSegment(sketch, "E1740", {"start": v(-25.55, 58.84) * mm, "end": v(-25.51, 58.86) * mm});
            skLineSegment(sketch, "E1741", {"start": v(-25.51, 58.86) * mm, "end": v(-25.48, 58.88) * mm});
            skLineSegment(sketch, "E1742", {"start": v(-25.48, 58.88) * mm, "end": v(-25.05, 58.88) * mm});
            skLineSegment(sketch, "E1743", {"start": v(-25.05, 58.88) * mm, "end": v(-25, 58.86) * mm});
            skLineSegment(sketch, "E1744", {"start": v(-25, 58.86) * mm, "end": v(-24.97, 58.84) * mm});
            skLineSegment(sketch, "E1745", {"start": v(-24.97, 58.84) * mm, "end": v(-24.75, 58.53) * mm});
            skLineSegment(sketch, "E1746", {"start": v(-24.75, 58.53) * mm, "end": v(-24.75, 58.42) * mm});
            skLineSegment(sketch, "E1747", {"start": v(-24.75, 60.96) * mm, "end": v(-24.75, 60.85) * mm});
            skLineSegment(sketch, "E1748", {"start": v(-24.75, 60.85) * mm, "end": v(-24.97, 60.54) * mm});
            skLineSegment(sketch, "E1749", {"start": v(-24.97, 60.54) * mm, "end": v(-25, 60.52) * mm});
            skLineSegment(sketch, "E1750", {"start": v(-25, 60.52) * mm, "end": v(-25.05, 60.5) * mm});
            skLineSegment(sketch, "E1751", {"start": v(-25.05, 60.5) * mm, "end": v(-25.48, 60.5) * mm});
            skLineSegment(sketch, "E1752", {"start": v(-25.48, 60.5) * mm, "end": v(-25.51, 60.52) * mm});
            skLineSegment(sketch, "E1753", {"start": v(-25.51, 60.52) * mm, "end": v(-25.55, 60.54) * mm});
            skLineSegment(sketch, "E1754", {"start": v(-25.55, 60.54) * mm, "end": v(-25.77, 60.86) * mm});
            skLineSegment(sketch, "E1755", {"start": v(-25.77, 60.86) * mm, "end": v(-25.77, 60.96) * mm});
            skLineSegment(sketch, "E1756", {"start": v(-25.77, 60.96) * mm, "end": v(-25.77, 61.07) * mm});
            skLineSegment(sketch, "E1757", {"start": v(-25.77, 61.07) * mm, "end": v(-25.55, 61.38) * mm});
            skLineSegment(sketch, "E1758", {"start": v(-25.55, 61.38) * mm, "end": v(-25.51, 61.4) * mm});
            skLineSegment(sketch, "E1759", {"start": v(-25.51, 61.4) * mm, "end": v(-25.48, 61.42) * mm});
            skLineSegment(sketch, "E1760", {"start": v(-25.48, 61.42) * mm, "end": v(-25.05, 61.42) * mm});
            skLineSegment(sketch, "E1761", {"start": v(-25.05, 61.42) * mm, "end": v(-25, 61.4) * mm});
            skLineSegment(sketch, "E1762", {"start": v(-25, 61.4) * mm, "end": v(-24.97, 61.38) * mm});
            skLineSegment(sketch, "E1763", {"start": v(-24.97, 61.38) * mm, "end": v(-24.75, 61.07) * mm});
            skLineSegment(sketch, "E1764", {"start": v(-24.75, 61.07) * mm, "end": v(-24.75, 60.96) * mm});
            skLineSegment(sketch, "E1765", {"start": v(-22.21, 58.42) * mm, "end": v(-22.21, 58.31) * mm});
            skLineSegment(sketch, "E1766", {"start": v(-22.21, 58.31) * mm, "end": v(-22.43, 58) * mm});
            skLineSegment(sketch, "E1767", {"start": v(-22.43, 58) * mm, "end": v(-22.47, 57.98) * mm});
            skLineSegment(sketch, "E1768", {"start": v(-22.47, 57.98) * mm, "end": v(-22.5, 57.96) * mm});
            skLineSegment(sketch, "E1769", {"start": v(-22.5, 57.96) * mm, "end": v(-22.93, 57.96) * mm});
            skLineSegment(sketch, "E1770", {"start": v(-22.93, 57.96) * mm, "end": v(-22.97, 57.98) * mm});
            skLineSegment(sketch, "E1771", {"start": v(-22.97, 57.98) * mm, "end": v(-23.01, 58) * mm});
            skLineSegment(sketch, "E1772", {"start": v(-23.01, 58) * mm, "end": v(-23.23, 58.32) * mm});
            skLineSegment(sketch, "E1773", {"start": v(-23.23, 58.32) * mm, "end": v(-23.23, 58.42) * mm});
            skLineSegment(sketch, "E1774", {"start": v(-23.23, 58.42) * mm, "end": v(-23.23, 58.53) * mm});
            skLineSegment(sketch, "E1775", {"start": v(-23.23, 58.53) * mm, "end": v(-23.01, 58.84) * mm});
            skLineSegment(sketch, "E1776", {"start": v(-23.01, 58.84) * mm, "end": v(-22.97, 58.86) * mm});
            skLineSegment(sketch, "E1777", {"start": v(-22.97, 58.86) * mm, "end": v(-22.93, 58.88) * mm});
            skLineSegment(sketch, "E1778", {"start": v(-22.93, 58.88) * mm, "end": v(-22.5, 58.88) * mm});
            skLineSegment(sketch, "E1779", {"start": v(-22.5, 58.88) * mm, "end": v(-22.47, 58.86) * mm});
            skLineSegment(sketch, "E1780", {"start": v(-22.47, 58.86) * mm, "end": v(-22.43, 58.84) * mm});
            skLineSegment(sketch, "E1781", {"start": v(-22.43, 58.84) * mm, "end": v(-22.21, 58.53) * mm});
            skLineSegment(sketch, "E1782", {"start": v(-22.21, 58.53) * mm, "end": v(-22.21, 58.42) * mm});
            skLineSegment(sketch, "E1783", {"start": v(-22.21, 60.96) * mm, "end": v(-22.21, 60.85) * mm});
            skLineSegment(sketch, "E1784", {"start": v(-22.21, 60.85) * mm, "end": v(-22.43, 60.54) * mm});
            skLineSegment(sketch, "E1785", {"start": v(-22.43, 60.54) * mm, "end": v(-22.47, 60.52) * mm});
            skLineSegment(sketch, "E1786", {"start": v(-22.47, 60.52) * mm, "end": v(-22.5, 60.5) * mm});
            skLineSegment(sketch, "E1787", {"start": v(-22.5, 60.5) * mm, "end": v(-22.93, 60.5) * mm});
            skLineSegment(sketch, "E1788", {"start": v(-22.93, 60.5) * mm, "end": v(-22.97, 60.52) * mm});
            skLineSegment(sketch, "E1789", {"start": v(-22.97, 60.52) * mm, "end": v(-23.01, 60.54) * mm});
            skLineSegment(sketch, "E1790", {"start": v(-23.01, 60.54) * mm, "end": v(-23.23, 60.86) * mm});
            skLineSegment(sketch, "E1791", {"start": v(-23.23, 60.86) * mm, "end": v(-23.23, 60.96) * mm});
            skLineSegment(sketch, "E1792", {"start": v(-23.23, 60.96) * mm, "end": v(-23.23, 61.07) * mm});
            skLineSegment(sketch, "E1793", {"start": v(-23.23, 61.07) * mm, "end": v(-23.01, 61.38) * mm});
            skLineSegment(sketch, "E1794", {"start": v(-23.01, 61.38) * mm, "end": v(-22.97, 61.4) * mm});
            skLineSegment(sketch, "E1795", {"start": v(-22.97, 61.4) * mm, "end": v(-22.93, 61.42) * mm});
            skLineSegment(sketch, "E1796", {"start": v(-22.93, 61.42) * mm, "end": v(-22.5, 61.42) * mm});
            skLineSegment(sketch, "E1797", {"start": v(-22.5, 61.42) * mm, "end": v(-22.47, 61.4) * mm});
            skLineSegment(sketch, "E1798", {"start": v(-22.47, 61.4) * mm, "end": v(-22.43, 61.38) * mm});
            skLineSegment(sketch, "E1799", {"start": v(-22.43, 61.38) * mm, "end": v(-22.21, 61.07) * mm});
            skLineSegment(sketch, "E1800", {"start": v(-22.21, 61.07) * mm, "end": v(-22.21, 60.96) * mm});
            skLineSegment(sketch, "E1801", {"start": v(-19.67, 58.42) * mm, "end": v(-19.67, 58.31) * mm});
            skLineSegment(sketch, "E1802", {"start": v(-19.67, 58.31) * mm, "end": v(-19.89, 58) * mm});
            skLineSegment(sketch, "E1803", {"start": v(-19.89, 58) * mm, "end": v(-19.93, 57.98) * mm});
            skLineSegment(sketch, "E1804", {"start": v(-19.93, 57.98) * mm, "end": v(-19.97, 57.96) * mm});
            skLineSegment(sketch, "E1805", {"start": v(-19.97, 57.96) * mm, "end": v(-20.4, 57.96) * mm});
            skLineSegment(sketch, "E1806", {"start": v(-20.4, 57.96) * mm, "end": v(-20.43, 57.98) * mm});
            skLineSegment(sketch, "E1807", {"start": v(-20.43, 57.98) * mm, "end": v(-20.47, 58) * mm});
            skLineSegment(sketch, "E1808", {"start": v(-20.47, 58) * mm, "end": v(-20.69, 58.32) * mm});
            skLineSegment(sketch, "E1809", {"start": v(-20.69, 58.32) * mm, "end": v(-20.69, 58.42) * mm});
            skLineSegment(sketch, "E1810", {"start": v(-20.69, 58.42) * mm, "end": v(-20.69, 58.53) * mm});
            skLineSegment(sketch, "E1811", {"start": v(-20.69, 58.53) * mm, "end": v(-20.47, 58.84) * mm});
            skLineSegment(sketch, "E1812", {"start": v(-20.47, 58.84) * mm, "end": v(-20.43, 58.86) * mm});
            skLineSegment(sketch, "E1813", {"start": v(-20.43, 58.86) * mm, "end": v(-20.4, 58.88) * mm});
            skLineSegment(sketch, "E1814", {"start": v(-20.4, 58.88) * mm, "end": v(-19.97, 58.88) * mm});
            skLineSegment(sketch, "E1815", {"start": v(-19.97, 58.88) * mm, "end": v(-19.93, 58.86) * mm});
            skLineSegment(sketch, "E1816", {"start": v(-19.93, 58.86) * mm, "end": v(-19.89, 58.84) * mm});
            skLineSegment(sketch, "E1817", {"start": v(-19.89, 58.84) * mm, "end": v(-19.67, 58.53) * mm});
            skLineSegment(sketch, "E1818", {"start": v(-19.67, 58.53) * mm, "end": v(-19.67, 58.42) * mm});
            skLineSegment(sketch, "E1819", {"start": v(-19.67, 60.96) * mm, "end": v(-19.67, 60.85) * mm});
            skLineSegment(sketch, "E1820", {"start": v(-19.67, 60.85) * mm, "end": v(-19.89, 60.54) * mm});
            skLineSegment(sketch, "E1821", {"start": v(-19.89, 60.54) * mm, "end": v(-19.93, 60.52) * mm});
            skLineSegment(sketch, "E1822", {"start": v(-19.93, 60.52) * mm, "end": v(-19.97, 60.5) * mm});
            skLineSegment(sketch, "E1823", {"start": v(-19.97, 60.5) * mm, "end": v(-20.4, 60.5) * mm});
            skLineSegment(sketch, "E1824", {"start": v(-20.4, 60.5) * mm, "end": v(-20.43, 60.52) * mm});
            skLineSegment(sketch, "E1825", {"start": v(-20.43, 60.52) * mm, "end": v(-20.47, 60.54) * mm});
            skLineSegment(sketch, "E1826", {"start": v(-20.47, 60.54) * mm, "end": v(-20.69, 60.86) * mm});
            skLineSegment(sketch, "E1827", {"start": v(-20.69, 60.86) * mm, "end": v(-20.69, 60.96) * mm});
            skLineSegment(sketch, "E1828", {"start": v(-20.69, 60.96) * mm, "end": v(-20.69, 61.07) * mm});
            skLineSegment(sketch, "E1829", {"start": v(-20.69, 61.07) * mm, "end": v(-20.47, 61.38) * mm});
            skLineSegment(sketch, "E1830", {"start": v(-20.47, 61.38) * mm, "end": v(-20.43, 61.4) * mm});
            skLineSegment(sketch, "E1831", {"start": v(-20.43, 61.4) * mm, "end": v(-20.4, 61.42) * mm});
            skLineSegment(sketch, "E1832", {"start": v(-20.4, 61.42) * mm, "end": v(-19.97, 61.42) * mm});
            skLineSegment(sketch, "E1833", {"start": v(-19.97, 61.42) * mm, "end": v(-19.93, 61.4) * mm});
            skLineSegment(sketch, "E1834", {"start": v(-19.93, 61.4) * mm, "end": v(-19.89, 61.38) * mm});
            skLineSegment(sketch, "E1835", {"start": v(-19.89, 61.38) * mm, "end": v(-19.67, 61.07) * mm});
            skLineSegment(sketch, "E1836", {"start": v(-19.67, 61.07) * mm, "end": v(-19.67, 60.96) * mm});
            skLineSegment(sketch, "E1837", {"start": v(-17.13, 58.42) * mm, "end": v(-17.13, 58.31) * mm});
            skLineSegment(sketch, "E1838", {"start": v(-17.13, 58.31) * mm, "end": v(-17.35, 58) * mm});
            skLineSegment(sketch, "E1839", {"start": v(-17.35, 58) * mm, "end": v(-17.38, 57.98) * mm});
            skLineSegment(sketch, "E1840", {"start": v(-17.38, 57.98) * mm, "end": v(-17.42, 57.96) * mm});
            skLineSegment(sketch, "E1841", {"start": v(-17.42, 57.96) * mm, "end": v(-17.85, 57.96) * mm});
            skLineSegment(sketch, "E1842", {"start": v(-17.85, 57.96) * mm, "end": v(-17.9, 57.98) * mm});
            skLineSegment(sketch, "E1843", {"start": v(-17.9, 57.98) * mm, "end": v(-17.93, 58) * mm});
            skLineSegment(sketch, "E1844", {"start": v(-17.93, 58) * mm, "end": v(-18.15, 58.32) * mm});
            skLineSegment(sketch, "E1845", {"start": v(-18.15, 58.32) * mm, "end": v(-18.15, 58.42) * mm});
            skLineSegment(sketch, "E1846", {"start": v(-18.15, 58.42) * mm, "end": v(-18.15, 58.53) * mm});
            skLineSegment(sketch, "E1847", {"start": v(-18.15, 58.53) * mm, "end": v(-17.93, 58.84) * mm});
            skLineSegment(sketch, "E1848", {"start": v(-17.93, 58.84) * mm, "end": v(-17.9, 58.86) * mm});
            skLineSegment(sketch, "E1849", {"start": v(-17.9, 58.86) * mm, "end": v(-17.85, 58.88) * mm});
            skLineSegment(sketch, "E1850", {"start": v(-17.85, 58.88) * mm, "end": v(-17.42, 58.88) * mm});
            skLineSegment(sketch, "E1851", {"start": v(-17.42, 58.88) * mm, "end": v(-17.38, 58.86) * mm});
            skLineSegment(sketch, "E1852", {"start": v(-17.38, 58.86) * mm, "end": v(-17.35, 58.84) * mm});
            skLineSegment(sketch, "E1853", {"start": v(-17.35, 58.84) * mm, "end": v(-17.13, 58.53) * mm});
            skLineSegment(sketch, "E1854", {"start": v(-17.13, 58.53) * mm, "end": v(-17.13, 58.42) * mm});
            skLineSegment(sketch, "E1855", {"start": v(-17.13, 60.96) * mm, "end": v(-17.13, 60.85) * mm});
            skLineSegment(sketch, "E1856", {"start": v(-17.13, 60.85) * mm, "end": v(-17.35, 60.54) * mm});
            skLineSegment(sketch, "E1857", {"start": v(-17.35, 60.54) * mm, "end": v(-17.38, 60.52) * mm});
            skLineSegment(sketch, "E1858", {"start": v(-17.38, 60.52) * mm, "end": v(-17.42, 60.5) * mm});
            skLineSegment(sketch, "E1859", {"start": v(-17.42, 60.5) * mm, "end": v(-17.85, 60.5) * mm});
            skLineSegment(sketch, "E1860", {"start": v(-17.85, 60.5) * mm, "end": v(-17.9, 60.52) * mm});
            skLineSegment(sketch, "E1861", {"start": v(-17.9, 60.52) * mm, "end": v(-17.93, 60.54) * mm});
            skLineSegment(sketch, "E1862", {"start": v(-17.93, 60.54) * mm, "end": v(-18.15, 60.86) * mm});
            skLineSegment(sketch, "E1863", {"start": v(-18.15, 60.86) * mm, "end": v(-18.15, 60.96) * mm});
            skLineSegment(sketch, "E1864", {"start": v(-18.15, 60.96) * mm, "end": v(-18.15, 61.07) * mm});
            skLineSegment(sketch, "E1865", {"start": v(-18.15, 61.07) * mm, "end": v(-17.93, 61.38) * mm});
            skLineSegment(sketch, "E1866", {"start": v(-17.93, 61.38) * mm, "end": v(-17.9, 61.4) * mm});
            skLineSegment(sketch, "E1867", {"start": v(-17.9, 61.4) * mm, "end": v(-17.85, 61.42) * mm});
            skLineSegment(sketch, "E1868", {"start": v(-17.85, 61.42) * mm, "end": v(-17.42, 61.42) * mm});
            skLineSegment(sketch, "E1869", {"start": v(-17.42, 61.42) * mm, "end": v(-17.38, 61.4) * mm});
            skLineSegment(sketch, "E1870", {"start": v(-17.38, 61.4) * mm, "end": v(-17.35, 61.38) * mm});
            skLineSegment(sketch, "E1871", {"start": v(-17.35, 61.38) * mm, "end": v(-17.13, 61.07) * mm});
            skLineSegment(sketch, "E1872", {"start": v(-17.13, 61.07) * mm, "end": v(-17.13, 60.96) * mm});
            skLineSegment(sketch, "E1873", {"start": v(-14.6, 58.42) * mm, "end": v(-14.6, 58.31) * mm});
            skLineSegment(sketch, "E1874", {"start": v(-14.6, 58.31) * mm, "end": v(-14.8, 58) * mm});
            skLineSegment(sketch, "E1875", {"start": v(-14.8, 58) * mm, "end": v(-14.85, 57.98) * mm});
            skLineSegment(sketch, "E1876", {"start": v(-14.85, 57.98) * mm, "end": v(-14.89, 57.96) * mm});
            skLineSegment(sketch, "E1877", {"start": v(-14.89, 57.96) * mm, "end": v(-15.32, 57.96) * mm});
            skLineSegment(sketch, "E1878", {"start": v(-15.32, 57.96) * mm, "end": v(-15.35, 57.98) * mm});
            skLineSegment(sketch, "E1879", {"start": v(-15.35, 57.98) * mm, "end": v(-15.4, 58) * mm});
            skLineSegment(sketch, "E1880", {"start": v(-15.4, 58) * mm, "end": v(-15.6, 58.32) * mm});
            skLineSegment(sketch, "E1881", {"start": v(-15.6, 58.32) * mm, "end": v(-15.6, 58.42) * mm});
            skLineSegment(sketch, "E1882", {"start": v(-15.6, 58.42) * mm, "end": v(-15.6, 58.53) * mm});
            skLineSegment(sketch, "E1883", {"start": v(-15.6, 58.53) * mm, "end": v(-15.4, 58.84) * mm});
            skLineSegment(sketch, "E1884", {"start": v(-15.4, 58.84) * mm, "end": v(-15.35, 58.86) * mm});
            skLineSegment(sketch, "E1885", {"start": v(-15.35, 58.86) * mm, "end": v(-15.32, 58.88) * mm});
            skLineSegment(sketch, "E1886", {"start": v(-15.32, 58.88) * mm, "end": v(-14.89, 58.88) * mm});
            skLineSegment(sketch, "E1887", {"start": v(-14.89, 58.88) * mm, "end": v(-14.85, 58.86) * mm});
            skLineSegment(sketch, "E1888", {"start": v(-14.85, 58.86) * mm, "end": v(-14.8, 58.84) * mm});
            skLineSegment(sketch, "E1889", {"start": v(-14.8, 58.84) * mm, "end": v(-14.6, 58.53) * mm});
            skLineSegment(sketch, "E1890", {"start": v(-14.6, 58.53) * mm, "end": v(-14.6, 58.42) * mm});
            skLineSegment(sketch, "E1891", {"start": v(-14.6, 60.96) * mm, "end": v(-14.6, 60.85) * mm});
            skLineSegment(sketch, "E1892", {"start": v(-14.6, 60.85) * mm, "end": v(-14.8, 60.54) * mm});
            skLineSegment(sketch, "E1893", {"start": v(-14.8, 60.54) * mm, "end": v(-14.85, 60.52) * mm});
            skLineSegment(sketch, "E1894", {"start": v(-14.85, 60.52) * mm, "end": v(-14.89, 60.5) * mm});
            skLineSegment(sketch, "E1895", {"start": v(-14.89, 60.5) * mm, "end": v(-15.32, 60.5) * mm});
            skLineSegment(sketch, "E1896", {"start": v(-15.32, 60.5) * mm, "end": v(-15.35, 60.52) * mm});
            skLineSegment(sketch, "E1897", {"start": v(-15.35, 60.52) * mm, "end": v(-15.4, 60.54) * mm});
            skLineSegment(sketch, "E1898", {"start": v(-15.4, 60.54) * mm, "end": v(-15.6, 60.86) * mm});
            skLineSegment(sketch, "E1899", {"start": v(-15.6, 60.86) * mm, "end": v(-15.6, 60.96) * mm});
            skLineSegment(sketch, "E1900", {"start": v(-15.6, 60.96) * mm, "end": v(-15.6, 61.07) * mm});
            skLineSegment(sketch, "E1901", {"start": v(-15.6, 61.07) * mm, "end": v(-15.4, 61.38) * mm});
            skLineSegment(sketch, "E1902", {"start": v(-15.4, 61.38) * mm, "end": v(-15.35, 61.4) * mm});
            skLineSegment(sketch, "E1903", {"start": v(-15.35, 61.4) * mm, "end": v(-15.32, 61.42) * mm});
            skLineSegment(sketch, "E1904", {"start": v(-15.32, 61.42) * mm, "end": v(-14.89, 61.42) * mm});
            skLineSegment(sketch, "E1905", {"start": v(-14.89, 61.42) * mm, "end": v(-14.85, 61.4) * mm});
            skLineSegment(sketch, "E1906", {"start": v(-14.85, 61.4) * mm, "end": v(-14.8, 61.38) * mm});
            skLineSegment(sketch, "E1907", {"start": v(-14.8, 61.38) * mm, "end": v(-14.6, 61.07) * mm});
            skLineSegment(sketch, "E1908", {"start": v(-14.6, 61.07) * mm, "end": v(-14.6, 60.96) * mm});
            skLineSegment(sketch, "E1909", {"start": v(-12.05, 58.42) * mm, "end": v(-12.05, 58.31) * mm});
            skLineSegment(sketch, "E1910", {"start": v(-12.05, 58.31) * mm, "end": v(-12.27, 58) * mm});
            skLineSegment(sketch, "E1911", {"start": v(-12.27, 58) * mm, "end": v(-12.3, 57.98) * mm});
            skLineSegment(sketch, "E1912", {"start": v(-12.3, 57.98) * mm, "end": v(-12.35, 57.96) * mm});
            skLineSegment(sketch, "E1913", {"start": v(-12.35, 57.96) * mm, "end": v(-12.78, 57.96) * mm});
            skLineSegment(sketch, "E1914", {"start": v(-12.78, 57.96) * mm, "end": v(-12.81, 57.98) * mm});
            skLineSegment(sketch, "E1915", {"start": v(-12.81, 57.98) * mm, "end": v(-12.85, 58) * mm});
            skLineSegment(sketch, "E1916", {"start": v(-12.85, 58) * mm, "end": v(-13.07, 58.32) * mm});
            skLineSegment(sketch, "E1917", {"start": v(-13.07, 58.32) * mm, "end": v(-13.07, 58.42) * mm});
            skLineSegment(sketch, "E1918", {"start": v(-13.07, 58.42) * mm, "end": v(-13.07, 58.53) * mm});
            skLineSegment(sketch, "E1919", {"start": v(-13.07, 58.53) * mm, "end": v(-12.85, 58.84) * mm});
            skLineSegment(sketch, "E1920", {"start": v(-12.85, 58.84) * mm, "end": v(-12.81, 58.86) * mm});
            skLineSegment(sketch, "E1921", {"start": v(-12.81, 58.86) * mm, "end": v(-12.78, 58.88) * mm});
            skLineSegment(sketch, "E1922", {"start": v(-12.78, 58.88) * mm, "end": v(-12.35, 58.88) * mm});
            skLineSegment(sketch, "E1923", {"start": v(-12.35, 58.88) * mm, "end": v(-12.3, 58.86) * mm});
            skLineSegment(sketch, "E1924", {"start": v(-12.3, 58.86) * mm, "end": v(-12.27, 58.84) * mm});
            skLineSegment(sketch, "E1925", {"start": v(-12.27, 58.84) * mm, "end": v(-12.05, 58.53) * mm});
            skLineSegment(sketch, "E1926", {"start": v(-12.05, 58.53) * mm, "end": v(-12.05, 58.42) * mm});
            skLineSegment(sketch, "E1927", {"start": v(-12.05, 60.96) * mm, "end": v(-12.05, 60.85) * mm});
            skLineSegment(sketch, "E1928", {"start": v(-12.05, 60.85) * mm, "end": v(-12.27, 60.54) * mm});
            skLineSegment(sketch, "E1929", {"start": v(-12.27, 60.54) * mm, "end": v(-12.3, 60.52) * mm});
            skLineSegment(sketch, "E1930", {"start": v(-12.3, 60.52) * mm, "end": v(-12.35, 60.5) * mm});
            skLineSegment(sketch, "E1931", {"start": v(-12.35, 60.5) * mm, "end": v(-12.78, 60.5) * mm});
            skLineSegment(sketch, "E1932", {"start": v(-12.78, 60.5) * mm, "end": v(-12.81, 60.52) * mm});
            skLineSegment(sketch, "E1933", {"start": v(-12.81, 60.52) * mm, "end": v(-12.85, 60.54) * mm});
            skLineSegment(sketch, "E1934", {"start": v(-12.85, 60.54) * mm, "end": v(-13.07, 60.86) * mm});
            skLineSegment(sketch, "E1935", {"start": v(-13.07, 60.86) * mm, "end": v(-13.07, 60.96) * mm});
            skLineSegment(sketch, "E1936", {"start": v(-13.07, 60.96) * mm, "end": v(-13.07, 61.07) * mm});
            skLineSegment(sketch, "E1937", {"start": v(-13.07, 61.07) * mm, "end": v(-12.85, 61.38) * mm});
            skLineSegment(sketch, "E1938", {"start": v(-12.85, 61.38) * mm, "end": v(-12.81, 61.4) * mm});
            skLineSegment(sketch, "E1939", {"start": v(-12.81, 61.4) * mm, "end": v(-12.78, 61.42) * mm});
            skLineSegment(sketch, "E1940", {"start": v(-12.78, 61.42) * mm, "end": v(-12.35, 61.42) * mm});
            skLineSegment(sketch, "E1941", {"start": v(-12.35, 61.42) * mm, "end": v(-12.3, 61.4) * mm});
            skLineSegment(sketch, "E1942", {"start": v(-12.3, 61.4) * mm, "end": v(-12.27, 61.38) * mm});
            skLineSegment(sketch, "E1943", {"start": v(-12.27, 61.38) * mm, "end": v(-12.05, 61.07) * mm});
            skLineSegment(sketch, "E1944", {"start": v(-12.05, 61.07) * mm, "end": v(-12.05, 60.96) * mm});
            skLineSegment(sketch, "E1945", {"start": v(-9.51, 58.42) * mm, "end": v(-9.51, 58.33) * mm});
            skLineSegment(sketch, "E1946", {"start": v(-9.51, 58.33) * mm, "end": v(-9.66, 58.06) * mm});
            skLineSegment(sketch, "E1947", {"start": v(-9.66, 58.06) * mm, "end": v(-9.93, 57.91) * mm});
            skLineSegment(sketch, "E1948", {"start": v(-9.93, 57.91) * mm, "end": v(-10.02, 57.91) * mm});
            skLineSegment(sketch, "E1949", {"start": v(-10.02, 57.91) * mm, "end": v(-10.11, 57.91) * mm});
            skLineSegment(sketch, "E1950", {"start": v(-10.11, 57.91) * mm, "end": v(-10.38, 58.06) * mm});
            skLineSegment(sketch, "E1951", {"start": v(-10.38, 58.06) * mm, "end": v(-10.53, 58.33) * mm});
            skLineSegment(sketch, "E1952", {"start": v(-10.53, 58.33) * mm, "end": v(-10.53, 58.42) * mm});
            skLineSegment(sketch, "E1953", {"start": v(-10.53, 58.42) * mm, "end": v(-10.53, 58.53) * mm});
            skLineSegment(sketch, "E1954", {"start": v(-10.53, 58.53) * mm, "end": v(-10.31, 58.84) * mm});
            skLineSegment(sketch, "E1955", {"start": v(-10.31, 58.84) * mm, "end": v(-10.27, 58.86) * mm});
            skLineSegment(sketch, "E1956", {"start": v(-10.27, 58.86) * mm, "end": v(-10.23, 58.88) * mm});
            skLineSegment(sketch, "E1957", {"start": v(-10.23, 58.88) * mm, "end": v(-9.8, 58.88) * mm});
            skLineSegment(sketch, "E1958", {"start": v(-9.8, 58.88) * mm, "end": v(-9.77, 58.86) * mm});
            skLineSegment(sketch, "E1959", {"start": v(-9.77, 58.86) * mm, "end": v(-9.73, 58.84) * mm});
            skLineSegment(sketch, "E1960", {"start": v(-9.73, 58.84) * mm, "end": v(-9.51, 58.53) * mm});
            skLineSegment(sketch, "E1961", {"start": v(-9.51, 58.53) * mm, "end": v(-9.51, 58.42) * mm});
            skLineSegment(sketch, "E1962", {"start": v(-9.51, 60.96) * mm, "end": v(-9.51, 60.87) * mm});
            skLineSegment(sketch, "E1963", {"start": v(-9.51, 60.87) * mm, "end": v(-9.66, 60.6) * mm});
            skLineSegment(sketch, "E1964", {"start": v(-9.66, 60.6) * mm, "end": v(-9.93, 60.45) * mm});
            skLineSegment(sketch, "E1965", {"start": v(-9.93, 60.45) * mm, "end": v(-10.02, 60.45) * mm});
            skLineSegment(sketch, "E1966", {"start": v(-10.02, 60.45) * mm, "end": v(-10.11, 60.45) * mm});
            skLineSegment(sketch, "E1967", {"start": v(-10.11, 60.45) * mm, "end": v(-10.38, 60.6) * mm});
            skLineSegment(sketch, "E1968", {"start": v(-10.38, 60.6) * mm, "end": v(-10.53, 60.87) * mm});
            skLineSegment(sketch, "E1969", {"start": v(-10.53, 60.87) * mm, "end": v(-10.53, 60.96) * mm});
            skLineSegment(sketch, "E1970", {"start": v(-10.53, 60.96) * mm, "end": v(-10.53, 61.07) * mm});
            skLineSegment(sketch, "E1971", {"start": v(-10.53, 61.07) * mm, "end": v(-10.31, 61.38) * mm});
            skLineSegment(sketch, "E1972", {"start": v(-10.31, 61.38) * mm, "end": v(-10.27, 61.4) * mm});
            skLineSegment(sketch, "E1973", {"start": v(-10.27, 61.4) * mm, "end": v(-10.23, 61.42) * mm});
            skLineSegment(sketch, "E1974", {"start": v(-10.23, 61.42) * mm, "end": v(-9.8, 61.42) * mm});
            skLineSegment(sketch, "E1975", {"start": v(-9.8, 61.42) * mm, "end": v(-9.77, 61.4) * mm});
            skLineSegment(sketch, "E1976", {"start": v(-9.77, 61.4) * mm, "end": v(-9.73, 61.38) * mm});
            skLineSegment(sketch, "E1977", {"start": v(-9.73, 61.38) * mm, "end": v(-9.51, 61.07) * mm});
            skLineSegment(sketch, "E1978", {"start": v(-9.51, 61.07) * mm, "end": v(-9.51, 60.96) * mm});
            skLineSegment(sketch, "E1979", {"start": v(-6.97, 58.42) * mm, "end": v(-6.97, 58.31) * mm});
            skLineSegment(sketch, "E1980", {"start": v(-6.97, 58.31) * mm, "end": v(-7.19, 58) * mm});
            skLineSegment(sketch, "E1981", {"start": v(-7.19, 58) * mm, "end": v(-7.23, 57.98) * mm});
            skLineSegment(sketch, "E1982", {"start": v(-7.23, 57.98) * mm, "end": v(-7.27, 57.96) * mm});
            skLineSegment(sketch, "E1983", {"start": v(-7.27, 57.96) * mm, "end": v(-7.7, 57.96) * mm});
            skLineSegment(sketch, "E1984", {"start": v(-7.7, 57.96) * mm, "end": v(-7.73, 57.98) * mm});
            skLineSegment(sketch, "E1985", {"start": v(-7.73, 57.98) * mm, "end": v(-7.77, 58) * mm});
            skLineSegment(sketch, "E1986", {"start": v(-7.77, 58) * mm, "end": v(-7.99, 58.32) * mm});
            skLineSegment(sketch, "E1987", {"start": v(-7.99, 58.32) * mm, "end": v(-7.99, 58.42) * mm});
            skLineSegment(sketch, "E1988", {"start": v(-7.99, 58.42) * mm, "end": v(-7.99, 58.53) * mm});
            skLineSegment(sketch, "E1989", {"start": v(-7.99, 58.53) * mm, "end": v(-7.77, 58.84) * mm});
            skLineSegment(sketch, "E1990", {"start": v(-7.77, 58.84) * mm, "end": v(-7.73, 58.86) * mm});
            skLineSegment(sketch, "E1991", {"start": v(-7.73, 58.86) * mm, "end": v(-7.7, 58.88) * mm});
            skLineSegment(sketch, "E1992", {"start": v(-7.7, 58.88) * mm, "end": v(-7.27, 58.88) * mm});
            skLineSegment(sketch, "E1993", {"start": v(-7.27, 58.88) * mm, "end": v(-7.23, 58.86) * mm});
            skLineSegment(sketch, "E1994", {"start": v(-7.23, 58.86) * mm, "end": v(-7.19, 58.84) * mm});
            skLineSegment(sketch, "E1995", {"start": v(-7.19, 58.84) * mm, "end": v(-6.97, 58.53) * mm});
            skLineSegment(sketch, "E1996", {"start": v(-6.97, 58.53) * mm, "end": v(-6.97, 58.42) * mm});
            skLineSegment(sketch, "E1997", {"start": v(-6.97, 60.96) * mm, "end": v(-6.97, 60.85) * mm});
            skLineSegment(sketch, "E1998", {"start": v(-6.97, 60.85) * mm, "end": v(-7.19, 60.54) * mm});
            skLineSegment(sketch, "E1999", {"start": v(-7.19, 60.54) * mm, "end": v(-7.23, 60.52) * mm});
            skLineSegment(sketch, "E2000", {"start": v(-7.23, 60.52) * mm, "end": v(-7.27, 60.5) * mm});
            skLineSegment(sketch, "E2001", {"start": v(-7.27, 60.5) * mm, "end": v(-7.7, 60.5) * mm});
            skLineSegment(sketch, "E2002", {"start": v(-7.7, 60.5) * mm, "end": v(-7.73, 60.52) * mm});
            skLineSegment(sketch, "E2003", {"start": v(-7.73, 60.52) * mm, "end": v(-7.77, 60.54) * mm});
            skLineSegment(sketch, "E2004", {"start": v(-7.77, 60.54) * mm, "end": v(-7.99, 60.86) * mm});
            skLineSegment(sketch, "E2005", {"start": v(-7.99, 60.86) * mm, "end": v(-7.99, 60.96) * mm});
            skLineSegment(sketch, "E2006", {"start": v(-7.99, 60.96) * mm, "end": v(-7.99, 61.07) * mm});
            skLineSegment(sketch, "E2007", {"start": v(-7.99, 61.07) * mm, "end": v(-7.77, 61.38) * mm});
            skLineSegment(sketch, "E2008", {"start": v(-7.77, 61.38) * mm, "end": v(-7.73, 61.4) * mm});
            skLineSegment(sketch, "E2009", {"start": v(-7.73, 61.4) * mm, "end": v(-7.7, 61.42) * mm});
            skLineSegment(sketch, "E2010", {"start": v(-7.7, 61.42) * mm, "end": v(-7.27, 61.42) * mm});
            skLineSegment(sketch, "E2011", {"start": v(-7.27, 61.42) * mm, "end": v(-7.23, 61.4) * mm});
            skLineSegment(sketch, "E2012", {"start": v(-7.23, 61.4) * mm, "end": v(-7.19, 61.38) * mm});
            skLineSegment(sketch, "E2013", {"start": v(-7.19, 61.38) * mm, "end": v(-6.97, 61.07) * mm});
            skLineSegment(sketch, "E2014", {"start": v(-6.97, 61.07) * mm, "end": v(-6.97, 60.96) * mm});
            skLineSegment(sketch, "E2015", {"start": v(-4.43, 58.42) * mm, "end": v(-4.43, 58.31) * mm});
            skLineSegment(sketch, "E2016", {"start": v(-4.43, 58.31) * mm, "end": v(-4.65, 58) * mm});
            skLineSegment(sketch, "E2017", {"start": v(-4.65, 58) * mm, "end": v(-4.68, 57.98) * mm});
            skLineSegment(sketch, "E2018", {"start": v(-4.68, 57.98) * mm, "end": v(-4.72, 57.96) * mm});
            skLineSegment(sketch, "E2019", {"start": v(-4.72, 57.96) * mm, "end": v(-5.15, 57.96) * mm});
            skLineSegment(sketch, "E2020", {"start": v(-5.15, 57.96) * mm, "end": v(-5.2, 57.98) * mm});
            skLineSegment(sketch, "E2021", {"start": v(-5.2, 57.98) * mm, "end": v(-5.23, 58) * mm});
            skLineSegment(sketch, "E2022", {"start": v(-5.23, 58) * mm, "end": v(-5.45, 58.32) * mm});
            skLineSegment(sketch, "E2023", {"start": v(-5.45, 58.32) * mm, "end": v(-5.45, 58.42) * mm});
            skLineSegment(sketch, "E2024", {"start": v(-5.45, 58.42) * mm, "end": v(-5.45, 58.53) * mm});
            skLineSegment(sketch, "E2025", {"start": v(-5.45, 58.53) * mm, "end": v(-5.23, 58.84) * mm});
            skLineSegment(sketch, "E2026", {"start": v(-5.23, 58.84) * mm, "end": v(-5.2, 58.86) * mm});
            skLineSegment(sketch, "E2027", {"start": v(-5.2, 58.86) * mm, "end": v(-5.15, 58.88) * mm});
            skLineSegment(sketch, "E2028", {"start": v(-5.15, 58.88) * mm, "end": v(-4.72, 58.88) * mm});
            skLineSegment(sketch, "E2029", {"start": v(-4.72, 58.88) * mm, "end": v(-4.68, 58.86) * mm});
            skLineSegment(sketch, "E2030", {"start": v(-4.68, 58.86) * mm, "end": v(-4.65, 58.84) * mm});
            skLineSegment(sketch, "E2031", {"start": v(-4.65, 58.84) * mm, "end": v(-4.43, 58.53) * mm});
            skLineSegment(sketch, "E2032", {"start": v(-4.43, 58.53) * mm, "end": v(-4.43, 58.42) * mm});
            skLineSegment(sketch, "E2033", {"start": v(-4.43, 60.96) * mm, "end": v(-4.43, 60.85) * mm});
            skLineSegment(sketch, "E2034", {"start": v(-4.43, 60.85) * mm, "end": v(-4.65, 60.54) * mm});
            skLineSegment(sketch, "E2035", {"start": v(-4.65, 60.54) * mm, "end": v(-4.68, 60.52) * mm});
            skLineSegment(sketch, "E2036", {"start": v(-4.68, 60.52) * mm, "end": v(-4.72, 60.5) * mm});
            skLineSegment(sketch, "E2037", {"start": v(-4.72, 60.5) * mm, "end": v(-5.15, 60.5) * mm});
            skLineSegment(sketch, "E2038", {"start": v(-5.15, 60.5) * mm, "end": v(-5.2, 60.52) * mm});
            skLineSegment(sketch, "E2039", {"start": v(-5.2, 60.52) * mm, "end": v(-5.23, 60.54) * mm});
            skLineSegment(sketch, "E2040", {"start": v(-5.23, 60.54) * mm, "end": v(-5.45, 60.86) * mm});
            skLineSegment(sketch, "E2041", {"start": v(-5.45, 60.86) * mm, "end": v(-5.45, 60.96) * mm});
            skLineSegment(sketch, "E2042", {"start": v(-5.45, 60.96) * mm, "end": v(-5.45, 61.07) * mm});
            skLineSegment(sketch, "E2043", {"start": v(-5.45, 61.07) * mm, "end": v(-5.23, 61.38) * mm});
            skLineSegment(sketch, "E2044", {"start": v(-5.23, 61.38) * mm, "end": v(-5.2, 61.4) * mm});
            skLineSegment(sketch, "E2045", {"start": v(-5.2, 61.4) * mm, "end": v(-5.15, 61.42) * mm});
            skLineSegment(sketch, "E2046", {"start": v(-5.15, 61.42) * mm, "end": v(-4.72, 61.42) * mm});
            skLineSegment(sketch, "E2047", {"start": v(-4.72, 61.42) * mm, "end": v(-4.68, 61.4) * mm});
            skLineSegment(sketch, "E2048", {"start": v(-4.68, 61.4) * mm, "end": v(-4.65, 61.38) * mm});
            skLineSegment(sketch, "E2049", {"start": v(-4.65, 61.38) * mm, "end": v(-4.43, 61.07) * mm});
            skLineSegment(sketch, "E2050", {"start": v(-4.43, 61.07) * mm, "end": v(-4.43, 60.96) * mm});
            skLineSegment(sketch, "E2051", {"start": v(51.3, 58.44) * mm, "end": v(51.3, 58.3) * mm});
            skLineSegment(sketch, "E2052", {"start": v(51.3, 58.3) * mm, "end": v(51.16, 57.89) * mm});
            skLineSegment(sketch, "E2053", {"start": v(51.16, 57.89) * mm, "end": v(50.84, 57.53) * mm});
            skLineSegment(sketch, "E2054", {"start": v(50.84, 57.53) * mm, "end": v(50.75, 57.48) * mm});
            skLineSegment(sketch, "E2055", {"start": v(50.75, 57.48) * mm, "end": v(50.67, 57.44) * mm});
            skLineSegment(sketch, "E2056", {"start": v(50.67, 57.44) * mm, "end": v(50.2, 57.34) * mm});
            skLineSegment(sketch, "E2057", {"start": v(50.2, 57.34) * mm, "end": v(49.74, 57.44) * mm});
            skLineSegment(sketch, "E2058", {"start": v(49.74, 57.44) * mm, "end": v(49.65, 57.48) * mm});
            skLineSegment(sketch, "E2059", {"start": v(49.65, 57.48) * mm, "end": v(49.57, 57.53) * mm});
            skLineSegment(sketch, "E2060", {"start": v(49.57, 57.53) * mm, "end": v(49.25, 57.89) * mm});
            skLineSegment(sketch, "E2061", {"start": v(49.25, 57.89) * mm, "end": v(49.1, 58.3) * mm});
            skLineSegment(sketch, "E2062", {"start": v(49.1, 58.3) * mm, "end": v(49.1, 58.44) * mm});
            skLineSegment(sketch, "E2063", {"start": v(49.1, 58.44) * mm, "end": v(49.1, 58.58) * mm});
            skLineSegment(sketch, "E2064", {"start": v(49.1, 58.58) * mm, "end": v(49.25, 58.99) * mm});
            skLineSegment(sketch, "E2065", {"start": v(49.25, 58.99) * mm, "end": v(49.57, 59.34) * mm});
            skLineSegment(sketch, "E2066", {"start": v(49.57, 59.34) * mm, "end": v(49.65, 59.4) * mm});
            skLineSegment(sketch, "E2067", {"start": v(49.65, 59.4) * mm, "end": v(49.74, 59.44) * mm});
            skLineSegment(sketch, "E2068", {"start": v(49.74, 59.44) * mm, "end": v(50.2, 59.54) * mm});
            skLineSegment(sketch, "E2069", {"start": v(50.2, 59.54) * mm, "end": v(50.67, 59.44) * mm});
            skLineSegment(sketch, "E2070", {"start": v(50.67, 59.44) * mm, "end": v(50.75, 59.4) * mm});
            skLineSegment(sketch, "E2071", {"start": v(50.75, 59.4) * mm, "end": v(50.84, 59.34) * mm});
            skLineSegment(sketch, "E2072", {"start": v(50.84, 59.34) * mm, "end": v(51.16, 58.99) * mm});
            skLineSegment(sketch, "E2073", {"start": v(51.16, 58.99) * mm, "end": v(51.3, 58.58) * mm});
            skLineSegment(sketch, "E2074", {"start": v(51.3, 58.58) * mm, "end": v(51.3, 58.44) * mm});
            skLineSegment(sketch, "E2075", {"start": v(51.3, 48.24) * mm, "end": v(51.3, 48.1) * mm});
            skLineSegment(sketch, "E2076", {"start": v(51.3, 48.1) * mm, "end": v(51.16, 47.69) * mm});
            skLineSegment(sketch, "E2077", {"start": v(51.16, 47.69) * mm, "end": v(50.84, 47.34) * mm});
            skLineSegment(sketch, "E2078", {"start": v(50.84, 47.34) * mm, "end": v(50.75, 47.29) * mm});
            skLineSegment(sketch, "E2079", {"start": v(50.75, 47.29) * mm, "end": v(50.67, 47.24) * mm});
            skLineSegment(sketch, "E2080", {"start": v(50.67, 47.24) * mm, "end": v(50.2, 47.14) * mm});
            skLineSegment(sketch, "E2081", {"start": v(50.2, 47.14) * mm, "end": v(49.74, 47.24) * mm});
            skLineSegment(sketch, "E2082", {"start": v(49.74, 47.24) * mm, "end": v(49.65, 47.29) * mm});
            skLineSegment(sketch, "E2083", {"start": v(49.65, 47.29) * mm, "end": v(49.57, 47.34) * mm});
            skLineSegment(sketch, "E2084", {"start": v(49.57, 47.34) * mm, "end": v(49.25, 47.69) * mm});
            skLineSegment(sketch, "E2085", {"start": v(49.25, 47.69) * mm, "end": v(49.1, 48.1) * mm});
            skLineSegment(sketch, "E2086", {"start": v(49.1, 48.1) * mm, "end": v(49.1, 48.24) * mm});
            skLineSegment(sketch, "E2087", {"start": v(49.1, 48.24) * mm, "end": v(49.1, 48.38) * mm});
            skLineSegment(sketch, "E2088", {"start": v(49.1, 48.38) * mm, "end": v(49.25, 48.8) * mm});
            skLineSegment(sketch, "E2089", {"start": v(49.25, 48.8) * mm, "end": v(49.57, 49.14) * mm});
            skLineSegment(sketch, "E2090", {"start": v(49.57, 49.14) * mm, "end": v(49.65, 49.2) * mm});
            skLineSegment(sketch, "E2091", {"start": v(49.65, 49.2) * mm, "end": v(49.74, 49.24) * mm});
            skLineSegment(sketch, "E2092", {"start": v(49.74, 49.24) * mm, "end": v(50.2, 49.34) * mm});
            skLineSegment(sketch, "E2093", {"start": v(50.2, 49.34) * mm, "end": v(50.67, 49.24) * mm});
            skLineSegment(sketch, "E2094", {"start": v(50.67, 49.24) * mm, "end": v(50.75, 49.2) * mm});
            skLineSegment(sketch, "E2095", {"start": v(50.75, 49.2) * mm, "end": v(50.84, 49.14) * mm});
            skLineSegment(sketch, "E2096", {"start": v(50.84, 49.14) * mm, "end": v(51.16, 48.8) * mm});
            skLineSegment(sketch, "E2097", {"start": v(51.16, 48.8) * mm, "end": v(51.3, 48.38) * mm});
            skLineSegment(sketch, "E2098", {"start": v(51.3, 48.38) * mm, "end": v(51.3, 48.24) * mm});
            skLineSegment(sketch, "E2099", {"start": v(46.44, 53.34) * mm, "end": v(46.44, 53.23) * mm});
            skLineSegment(sketch, "E2100", {"start": v(46.44, 53.23) * mm, "end": v(46.23, 52.93) * mm});
            skLineSegment(sketch, "E2101", {"start": v(46.23, 52.93) * mm, "end": v(46.19, 52.9) * mm});
            skLineSegment(sketch, "E2102", {"start": v(46.19, 52.9) * mm, "end": v(46.15, 52.88) * mm});
            skLineSegment(sketch, "E2103", {"start": v(46.15, 52.88) * mm, "end": v(45.73, 52.88) * mm});
            skLineSegment(sketch, "E2104", {"start": v(45.73, 52.88) * mm, "end": v(45.69, 52.9) * mm});
            skLineSegment(sketch, "E2105", {"start": v(45.69, 52.9) * mm, "end": v(45.65, 52.93) * mm});
            skLineSegment(sketch, "E2106", {"start": v(45.65, 52.93) * mm, "end": v(45.44, 53.24) * mm});
            skLineSegment(sketch, "E2107", {"start": v(45.44, 53.24) * mm, "end": v(45.44, 53.34) * mm});
            skLineSegment(sketch, "E2108", {"start": v(45.44, 53.34) * mm, "end": v(45.44, 53.45) * mm});
            skLineSegment(sketch, "E2109", {"start": v(45.44, 53.45) * mm, "end": v(45.65, 53.75) * mm});
            skLineSegment(sketch, "E2110", {"start": v(45.65, 53.75) * mm, "end": v(45.69, 53.77) * mm});
            skLineSegment(sketch, "E2111", {"start": v(45.69, 53.77) * mm, "end": v(45.73, 53.8) * mm});
            skLineSegment(sketch, "E2112", {"start": v(45.73, 53.8) * mm, "end": v(46.15, 53.8) * mm});
            skLineSegment(sketch, "E2113", {"start": v(46.15, 53.8) * mm, "end": v(46.19, 53.77) * mm});
            skLineSegment(sketch, "E2114", {"start": v(46.19, 53.77) * mm, "end": v(46.23, 53.75) * mm});
            skLineSegment(sketch, "E2115", {"start": v(46.23, 53.75) * mm, "end": v(46.44, 53.44) * mm});
            skLineSegment(sketch, "E2116", {"start": v(46.44, 53.44) * mm, "end": v(46.44, 53.34) * mm});
            skLineSegment(sketch, "E2117", {"start": v(46.44, 55.84) * mm, "end": v(46.44, 55.73) * mm});
            skLineSegment(sketch, "E2118", {"start": v(46.44, 55.73) * mm, "end": v(46.23, 55.43) * mm});
            skLineSegment(sketch, "E2119", {"start": v(46.23, 55.43) * mm, "end": v(46.19, 55.4) * mm});
            skLineSegment(sketch, "E2120", {"start": v(46.19, 55.4) * mm, "end": v(46.15, 55.38) * mm});
            skLineSegment(sketch, "E2121", {"start": v(46.15, 55.38) * mm, "end": v(45.73, 55.38) * mm});
            skLineSegment(sketch, "E2122", {"start": v(45.73, 55.38) * mm, "end": v(45.69, 55.4) * mm});
            skLineSegment(sketch, "E2123", {"start": v(45.69, 55.4) * mm, "end": v(45.65, 55.43) * mm});
            skLineSegment(sketch, "E2124", {"start": v(45.65, 55.43) * mm, "end": v(45.44, 55.74) * mm});
            skLineSegment(sketch, "E2125", {"start": v(45.44, 55.74) * mm, "end": v(45.44, 55.84) * mm});
            skLineSegment(sketch, "E2126", {"start": v(45.44, 55.84) * mm, "end": v(45.44, 55.95) * mm});
            skLineSegment(sketch, "E2127", {"start": v(45.44, 55.95) * mm, "end": v(45.65, 56.25) * mm});
            skLineSegment(sketch, "E2128", {"start": v(45.65, 56.25) * mm, "end": v(45.69, 56.27) * mm});
            skLineSegment(sketch, "E2129", {"start": v(45.69, 56.27) * mm, "end": v(45.73, 56.3) * mm});
            skLineSegment(sketch, "E2130", {"start": v(45.73, 56.3) * mm, "end": v(46.15, 56.3) * mm});
            skLineSegment(sketch, "E2131", {"start": v(46.15, 56.3) * mm, "end": v(46.19, 56.27) * mm});
            skLineSegment(sketch, "E2132", {"start": v(46.19, 56.27) * mm, "end": v(46.23, 56.25) * mm});
            skLineSegment(sketch, "E2133", {"start": v(46.23, 56.25) * mm, "end": v(46.44, 55.94) * mm});
            skLineSegment(sketch, "E2134", {"start": v(46.44, 55.94) * mm, "end": v(46.44, 55.84) * mm});
            skLineSegment(sketch, "E2135", {"start": v(47.66, -59.36) * mm, "end": v(47.66, -59.47) * mm});
            skLineSegment(sketch, "E2136", {"start": v(47.66, -59.47) * mm, "end": v(47.45, -59.78) * mm});
            skLineSegment(sketch, "E2137", {"start": v(47.45, -59.78) * mm, "end": v(47.41, -59.8) * mm});
            skLineSegment(sketch, "E2138", {"start": v(47.41, -59.8) * mm, "end": v(47.37, -59.82) * mm});
            skLineSegment(sketch, "E2139", {"start": v(47.37, -59.82) * mm, "end": v(46.94, -59.82) * mm});
            skLineSegment(sketch, "E2140", {"start": v(46.94, -59.82) * mm, "end": v(46.9, -59.8) * mm});
            skLineSegment(sketch, "E2141", {"start": v(46.9, -59.8) * mm, "end": v(46.86, -59.78) * mm});
            skLineSegment(sketch, "E2142", {"start": v(46.86, -59.78) * mm, "end": v(46.65, -59.46) * mm});
            skLineSegment(sketch, "E2143", {"start": v(46.65, -59.46) * mm, "end": v(46.65, -59.36) * mm});
            skLineSegment(sketch, "E2144", {"start": v(46.65, -59.36) * mm, "end": v(46.65, -59.25) * mm});
            skLineSegment(sketch, "E2145", {"start": v(46.65, -59.25) * mm, "end": v(46.86, -58.94) * mm});
            skLineSegment(sketch, "E2146", {"start": v(46.86, -58.94) * mm, "end": v(46.9, -58.92) * mm});
            skLineSegment(sketch, "E2147", {"start": v(46.9, -58.92) * mm, "end": v(46.94, -58.9) * mm});
            skLineSegment(sketch, "E2148", {"start": v(46.94, -58.9) * mm, "end": v(47.37, -58.9) * mm});
            skLineSegment(sketch, "E2149", {"start": v(47.37, -58.9) * mm, "end": v(47.41, -58.92) * mm});
            skLineSegment(sketch, "E2150", {"start": v(47.41, -58.92) * mm, "end": v(47.45, -58.94) * mm});
            skLineSegment(sketch, "E2151", {"start": v(47.45, -58.94) * mm, "end": v(47.66, -59.26) * mm});
            skLineSegment(sketch, "E2152", {"start": v(47.66, -59.26) * mm, "end": v(47.66, -59.36) * mm});
            skLineSegment(sketch, "E2153", {"start": v(50.2, -59.36) * mm, "end": v(50.2, -59.47) * mm});
            skLineSegment(sketch, "E2154", {"start": v(50.2, -59.47) * mm, "end": v(49.99, -59.78) * mm});
            skLineSegment(sketch, "E2155", {"start": v(49.99, -59.78) * mm, "end": v(49.95, -59.8) * mm});
            skLineSegment(sketch, "E2156", {"start": v(49.95, -59.8) * mm, "end": v(49.91, -59.82) * mm});
            skLineSegment(sketch, "E2157", {"start": v(49.91, -59.82) * mm, "end": v(49.48, -59.82) * mm});
            skLineSegment(sketch, "E2158", {"start": v(49.48, -59.82) * mm, "end": v(49.44, -59.8) * mm});
            skLineSegment(sketch, "E2159", {"start": v(49.44, -59.8) * mm, "end": v(49.4, -59.78) * mm});
            skLineSegment(sketch, "E2160", {"start": v(49.4, -59.78) * mm, "end": v(49.19, -59.46) * mm});
            skLineSegment(sketch, "E2161", {"start": v(49.19, -59.46) * mm, "end": v(49.19, -59.36) * mm});
            skLineSegment(sketch, "E2162", {"start": v(49.19, -59.36) * mm, "end": v(49.19, -59.25) * mm});
            skLineSegment(sketch, "E2163", {"start": v(49.19, -59.25) * mm, "end": v(49.4, -58.94) * mm});
            skLineSegment(sketch, "E2164", {"start": v(49.4, -58.94) * mm, "end": v(49.44, -58.92) * mm});
            skLineSegment(sketch, "E2165", {"start": v(49.44, -58.92) * mm, "end": v(49.48, -58.9) * mm});
            skLineSegment(sketch, "E2166", {"start": v(49.48, -58.9) * mm, "end": v(49.91, -58.9) * mm});
            skLineSegment(sketch, "E2167", {"start": v(49.91, -58.9) * mm, "end": v(49.95, -58.92) * mm});
            skLineSegment(sketch, "E2168", {"start": v(49.95, -58.92) * mm, "end": v(49.99, -58.94) * mm});
            skLineSegment(sketch, "E2169", {"start": v(49.99, -58.94) * mm, "end": v(50.2, -59.26) * mm});
            skLineSegment(sketch, "E2170", {"start": v(50.2, -59.26) * mm, "end": v(50.2, -59.36) * mm});
            skLineSegment(sketch, "E2171", {"start": v(52.74, -59.36) * mm, "end": v(52.74, -59.47) * mm});
            skLineSegment(sketch, "E2172", {"start": v(52.74, -59.47) * mm, "end": v(52.53, -59.78) * mm});
            skLineSegment(sketch, "E2173", {"start": v(52.53, -59.78) * mm, "end": v(52.5, -59.8) * mm});
            skLineSegment(sketch, "E2174", {"start": v(52.5, -59.8) * mm, "end": v(52.45, -59.82) * mm});
            skLineSegment(sketch, "E2175", {"start": v(52.45, -59.82) * mm, "end": v(52.02, -59.82) * mm});
            skLineSegment(sketch, "E2176", {"start": v(52.02, -59.82) * mm, "end": v(51.98, -59.8) * mm});
            skLineSegment(sketch, "E2177", {"start": v(51.98, -59.8) * mm, "end": v(51.94, -59.78) * mm});
            skLineSegment(sketch, "E2178", {"start": v(51.94, -59.78) * mm, "end": v(51.73, -59.46) * mm});
            skLineSegment(sketch, "E2179", {"start": v(51.73, -59.46) * mm, "end": v(51.73, -59.36) * mm});
            skLineSegment(sketch, "E2180", {"start": v(51.73, -59.36) * mm, "end": v(51.73, -59.25) * mm});
            skLineSegment(sketch, "E2181", {"start": v(51.73, -59.25) * mm, "end": v(51.94, -58.94) * mm});
            skLineSegment(sketch, "E2182", {"start": v(51.94, -58.94) * mm, "end": v(51.98, -58.92) * mm});
            skLineSegment(sketch, "E2183", {"start": v(51.98, -58.92) * mm, "end": v(52.02, -58.9) * mm});
            skLineSegment(sketch, "E2184", {"start": v(52.02, -58.9) * mm, "end": v(52.45, -58.9) * mm});
            skLineSegment(sketch, "E2185", {"start": v(52.45, -58.9) * mm, "end": v(52.5, -58.92) * mm});
            skLineSegment(sketch, "E2186", {"start": v(52.5, -58.92) * mm, "end": v(52.53, -58.94) * mm});
            skLineSegment(sketch, "E2187", {"start": v(52.53, -58.94) * mm, "end": v(52.74, -59.26) * mm});
            skLineSegment(sketch, "E2188", {"start": v(52.74, -59.26) * mm, "end": v(52.74, -59.36) * mm});
            skLineSegment(sketch, "E2189", {"start": v(55.28, -59.36) * mm, "end": v(55.28, -59.47) * mm});
            skLineSegment(sketch, "E2190", {"start": v(55.28, -59.47) * mm, "end": v(55.07, -59.78) * mm});
            skLineSegment(sketch, "E2191", {"start": v(55.07, -59.78) * mm, "end": v(55.03, -59.8) * mm});
            skLineSegment(sketch, "E2192", {"start": v(55.03, -59.8) * mm, "end": v(54.99, -59.82) * mm});
            skLineSegment(sketch, "E2193", {"start": v(54.99, -59.82) * mm, "end": v(54.56, -59.82) * mm});
            skLineSegment(sketch, "E2194", {"start": v(54.56, -59.82) * mm, "end": v(54.52, -59.8) * mm});
            skLineSegment(sketch, "E2195", {"start": v(54.52, -59.8) * mm, "end": v(54.48, -59.78) * mm});
            skLineSegment(sketch, "E2196", {"start": v(54.48, -59.78) * mm, "end": v(54.27, -59.46) * mm});
            skLineSegment(sketch, "E2197", {"start": v(54.27, -59.46) * mm, "end": v(54.27, -59.36) * mm});
            skLineSegment(sketch, "E2198", {"start": v(54.27, -59.36) * mm, "end": v(54.27, -59.25) * mm});
            skLineSegment(sketch, "E2199", {"start": v(54.27, -59.25) * mm, "end": v(54.48, -58.94) * mm});
            skLineSegment(sketch, "E2200", {"start": v(54.48, -58.94) * mm, "end": v(54.52, -58.92) * mm});
            skLineSegment(sketch, "E2201", {"start": v(54.52, -58.92) * mm, "end": v(54.56, -58.9) * mm});
            skLineSegment(sketch, "E2202", {"start": v(54.56, -58.9) * mm, "end": v(54.99, -58.9) * mm});
            skLineSegment(sketch, "E2203", {"start": v(54.99, -58.9) * mm, "end": v(55.03, -58.92) * mm});
            skLineSegment(sketch, "E2204", {"start": v(55.03, -58.92) * mm, "end": v(55.07, -58.94) * mm});
            skLineSegment(sketch, "E2205", {"start": v(55.07, -58.94) * mm, "end": v(55.28, -59.26) * mm});
            skLineSegment(sketch, "E2206", {"start": v(55.28, -59.26) * mm, "end": v(55.28, -59.36) * mm});
            skLineSegment(sketch, "E2207", {"start": v(57.82, -59.36) * mm, "end": v(57.82, -59.47) * mm});
            skLineSegment(sketch, "E2208", {"start": v(57.82, -59.47) * mm, "end": v(57.6, -59.78) * mm});
            skLineSegment(sketch, "E2209", {"start": v(57.6, -59.78) * mm, "end": v(57.57, -59.8) * mm});
            skLineSegment(sketch, "E2210", {"start": v(57.57, -59.8) * mm, "end": v(57.53, -59.82) * mm});
            skLineSegment(sketch, "E2211", {"start": v(57.53, -59.82) * mm, "end": v(57.1, -59.82) * mm});
            skLineSegment(sketch, "E2212", {"start": v(57.1, -59.82) * mm, "end": v(57.06, -59.8) * mm});
            skLineSegment(sketch, "E2213", {"start": v(57.06, -59.8) * mm, "end": v(57.02, -59.78) * mm});
            skLineSegment(sketch, "E2214", {"start": v(57.02, -59.78) * mm, "end": v(56.8, -59.46) * mm});
            skLineSegment(sketch, "E2215", {"start": v(56.8, -59.46) * mm, "end": v(56.8, -59.36) * mm});
            skLineSegment(sketch, "E2216", {"start": v(56.8, -59.36) * mm, "end": v(56.8, -59.25) * mm});
            skLineSegment(sketch, "E2217", {"start": v(56.8, -59.25) * mm, "end": v(57.02, -58.94) * mm});
            skLineSegment(sketch, "E2218", {"start": v(57.02, -58.94) * mm, "end": v(57.06, -58.92) * mm});
            skLineSegment(sketch, "E2219", {"start": v(57.06, -58.92) * mm, "end": v(57.1, -58.9) * mm});
            skLineSegment(sketch, "E2220", {"start": v(57.1, -58.9) * mm, "end": v(57.53, -58.9) * mm});
            skLineSegment(sketch, "E2221", {"start": v(57.53, -58.9) * mm, "end": v(57.57, -58.92) * mm});
            skLineSegment(sketch, "E2222", {"start": v(57.57, -58.92) * mm, "end": v(57.6, -58.94) * mm});
            skLineSegment(sketch, "E2223", {"start": v(57.6, -58.94) * mm, "end": v(57.82, -59.26) * mm});
            skLineSegment(sketch, "E2224", {"start": v(57.82, -59.26) * mm, "end": v(57.82, -59.36) * mm});
            skLineSegment(sketch, "E2225", {"start": v(60.36, -59.36) * mm, "end": v(60.36, -59.47) * mm});
            skLineSegment(sketch, "E2226", {"start": v(60.36, -59.47) * mm, "end": v(60.15, -59.78) * mm});
            skLineSegment(sketch, "E2227", {"start": v(60.15, -59.78) * mm, "end": v(60.11, -59.8) * mm});
            skLineSegment(sketch, "E2228", {"start": v(60.11, -59.8) * mm, "end": v(60.07, -59.82) * mm});
            skLineSegment(sketch, "E2229", {"start": v(60.07, -59.82) * mm, "end": v(59.64, -59.82) * mm});
            skLineSegment(sketch, "E2230", {"start": v(59.64, -59.82) * mm, "end": v(59.6, -59.8) * mm});
            skLineSegment(sketch, "E2231", {"start": v(59.6, -59.8) * mm, "end": v(59.56, -59.78) * mm});
            skLineSegment(sketch, "E2232", {"start": v(59.56, -59.78) * mm, "end": v(59.35, -59.46) * mm});
            skLineSegment(sketch, "E2233", {"start": v(59.35, -59.46) * mm, "end": v(59.35, -59.36) * mm});
            skLineSegment(sketch, "E2234", {"start": v(59.35, -59.36) * mm, "end": v(59.35, -59.25) * mm});
            skLineSegment(sketch, "E2235", {"start": v(59.35, -59.25) * mm, "end": v(59.56, -58.94) * mm});
            skLineSegment(sketch, "E2236", {"start": v(59.56, -58.94) * mm, "end": v(59.6, -58.92) * mm});
            skLineSegment(sketch, "E2237", {"start": v(59.6, -58.92) * mm, "end": v(59.64, -58.9) * mm});
            skLineSegment(sketch, "E2238", {"start": v(59.64, -58.9) * mm, "end": v(60.07, -58.9) * mm});
            skLineSegment(sketch, "E2239", {"start": v(60.07, -58.9) * mm, "end": v(60.11, -58.92) * mm});
            skLineSegment(sketch, "E2240", {"start": v(60.11, -58.92) * mm, "end": v(60.15, -58.94) * mm});
            skLineSegment(sketch, "E2241", {"start": v(60.15, -58.94) * mm, "end": v(60.36, -59.26) * mm});
            skLineSegment(sketch, "E2242", {"start": v(60.36, -59.26) * mm, "end": v(60.36, -59.36) * mm});
            skLineSegment(sketch, "E2243", {"start": v(-61.58, -13.97) * mm, "end": v(-61.58, -14.08) * mm});
            skLineSegment(sketch, "E2244", {"start": v(-61.58, -14.08) * mm, "end": v(-61.8, -14.39) * mm});
            skLineSegment(sketch, "E2245", {"start": v(-61.8, -14.39) * mm, "end": v(-61.83, -14.41) * mm});
            skLineSegment(sketch, "E2246", {"start": v(-61.83, -14.41) * mm, "end": v(-61.87, -14.43) * mm});
            skLineSegment(sketch, "E2247", {"start": v(-61.87, -14.43) * mm, "end": v(-62.3, -14.43) * mm});
            skLineSegment(sketch, "E2248", {"start": v(-62.3, -14.43) * mm, "end": v(-62.34, -14.41) * mm});
            skLineSegment(sketch, "E2249", {"start": v(-62.34, -14.41) * mm, "end": v(-62.38, -14.39) * mm});
            skLineSegment(sketch, "E2250", {"start": v(-62.38, -14.39) * mm, "end": v(-62.6, -14.07) * mm});
            skLineSegment(sketch, "E2251", {"start": v(-62.6, -14.07) * mm, "end": v(-62.6, -13.97) * mm});
            skLineSegment(sketch, "E2252", {"start": v(-62.6, -13.97) * mm, "end": v(-62.6, -13.86) * mm});
            skLineSegment(sketch, "E2253", {"start": v(-62.6, -13.86) * mm, "end": v(-62.38, -13.55) * mm});
            skLineSegment(sketch, "E2254", {"start": v(-62.38, -13.55) * mm, "end": v(-62.34, -13.53) * mm});
            skLineSegment(sketch, "E2255", {"start": v(-62.34, -13.53) * mm, "end": v(-62.3, -13.5) * mm});
            skLineSegment(sketch, "E2256", {"start": v(-62.3, -13.5) * mm, "end": v(-61.87, -13.5) * mm});
            skLineSegment(sketch, "E2257", {"start": v(-61.87, -13.5) * mm, "end": v(-61.83, -13.53) * mm});
            skLineSegment(sketch, "E2258", {"start": v(-61.83, -13.53) * mm, "end": v(-61.8, -13.55) * mm});
            skLineSegment(sketch, "E2259", {"start": v(-61.8, -13.55) * mm, "end": v(-61.58, -13.87) * mm});
            skLineSegment(sketch, "E2260", {"start": v(-61.58, -13.87) * mm, "end": v(-61.58, -13.97) * mm});
            skLineSegment(sketch, "E2261", {"start": v(-59.04, -13.97) * mm, "end": v(-59.04, -14.08) * mm});
            skLineSegment(sketch, "E2262", {"start": v(-59.04, -14.08) * mm, "end": v(-59.26, -14.39) * mm});
            skLineSegment(sketch, "E2263", {"start": v(-59.26, -14.39) * mm, "end": v(-59.3, -14.41) * mm});
            skLineSegment(sketch, "E2264", {"start": v(-59.3, -14.41) * mm, "end": v(-59.33, -14.43) * mm});
            skLineSegment(sketch, "E2265", {"start": v(-59.33, -14.43) * mm, "end": v(-59.76, -14.43) * mm});
            skLineSegment(sketch, "E2266", {"start": v(-59.76, -14.43) * mm, "end": v(-59.8, -14.41) * mm});
            skLineSegment(sketch, "E2267", {"start": v(-59.8, -14.41) * mm, "end": v(-59.84, -14.39) * mm});
            skLineSegment(sketch, "E2268", {"start": v(-59.84, -14.39) * mm, "end": v(-60.06, -14.07) * mm});
            skLineSegment(sketch, "E2269", {"start": v(-60.06, -14.07) * mm, "end": v(-60.06, -13.97) * mm});
            skLineSegment(sketch, "E2270", {"start": v(-60.06, -13.97) * mm, "end": v(-60.06, -13.86) * mm});
            skLineSegment(sketch, "E2271", {"start": v(-60.06, -13.86) * mm, "end": v(-59.84, -13.55) * mm});
            skLineSegment(sketch, "E2272", {"start": v(-59.84, -13.55) * mm, "end": v(-59.8, -13.53) * mm});
            skLineSegment(sketch, "E2273", {"start": v(-59.8, -13.53) * mm, "end": v(-59.76, -13.5) * mm});
            skLineSegment(sketch, "E2274", {"start": v(-59.76, -13.5) * mm, "end": v(-59.33, -13.5) * mm});
            skLineSegment(sketch, "E2275", {"start": v(-59.33, -13.5) * mm, "end": v(-59.3, -13.53) * mm});
            skLineSegment(sketch, "E2276", {"start": v(-59.3, -13.53) * mm, "end": v(-59.26, -13.55) * mm});
            skLineSegment(sketch, "E2277", {"start": v(-59.26, -13.55) * mm, "end": v(-59.04, -13.87) * mm});
            skLineSegment(sketch, "E2278", {"start": v(-59.04, -13.87) * mm, "end": v(-59.04, -13.97) * mm});
            skLineSegment(sketch, "E2279", {"start": v(-61.58, -16.51) * mm, "end": v(-61.58, -16.62) * mm});
            skLineSegment(sketch, "E2280", {"start": v(-61.58, -16.62) * mm, "end": v(-61.8, -16.93) * mm});
            skLineSegment(sketch, "E2281", {"start": v(-61.8, -16.93) * mm, "end": v(-61.83, -16.95) * mm});
            skLineSegment(sketch, "E2282", {"start": v(-61.83, -16.95) * mm, "end": v(-61.87, -16.97) * mm});
            skLineSegment(sketch, "E2283", {"start": v(-61.87, -16.97) * mm, "end": v(-62.3, -16.97) * mm});
            skLineSegment(sketch, "E2284", {"start": v(-62.3, -16.97) * mm, "end": v(-62.34, -16.95) * mm});
            skLineSegment(sketch, "E2285", {"start": v(-62.34, -16.95) * mm, "end": v(-62.38, -16.93) * mm});
            skLineSegment(sketch, "E2286", {"start": v(-62.38, -16.93) * mm, "end": v(-62.6, -16.61) * mm});
            skLineSegment(sketch, "E2287", {"start": v(-62.6, -16.61) * mm, "end": v(-62.6, -16.51) * mm});
            skLineSegment(sketch, "E2288", {"start": v(-62.6, -16.51) * mm, "end": v(-62.6, -16.4) * mm});
            skLineSegment(sketch, "E2289", {"start": v(-62.6, -16.4) * mm, "end": v(-62.38, -16.1) * mm});
            skLineSegment(sketch, "E2290", {"start": v(-62.38, -16.1) * mm, "end": v(-62.34, -16.07) * mm});
            skLineSegment(sketch, "E2291", {"start": v(-62.34, -16.07) * mm, "end": v(-62.3, -16.05) * mm});
            skLineSegment(sketch, "E2292", {"start": v(-62.3, -16.05) * mm, "end": v(-61.87, -16.05) * mm});
            skLineSegment(sketch, "E2293", {"start": v(-61.87, -16.05) * mm, "end": v(-61.83, -16.07) * mm});
            skLineSegment(sketch, "E2294", {"start": v(-61.83, -16.07) * mm, "end": v(-61.8, -16.1) * mm});
            skLineSegment(sketch, "E2295", {"start": v(-61.8, -16.1) * mm, "end": v(-61.58, -16.4) * mm});
            skLineSegment(sketch, "E2296", {"start": v(-61.58, -16.4) * mm, "end": v(-61.58, -16.51) * mm});
            skLineSegment(sketch, "E2297", {"start": v(-59.04, -16.51) * mm, "end": v(-59.04, -16.62) * mm});
            skLineSegment(sketch, "E2298", {"start": v(-59.04, -16.62) * mm, "end": v(-59.26, -16.93) * mm});
            skLineSegment(sketch, "E2299", {"start": v(-59.26, -16.93) * mm, "end": v(-59.3, -16.95) * mm});
            skLineSegment(sketch, "E2300", {"start": v(-59.3, -16.95) * mm, "end": v(-59.33, -16.97) * mm});
            skLineSegment(sketch, "E2301", {"start": v(-59.33, -16.97) * mm, "end": v(-59.76, -16.97) * mm});
            skLineSegment(sketch, "E2302", {"start": v(-59.76, -16.97) * mm, "end": v(-59.8, -16.95) * mm});
            skLineSegment(sketch, "E2303", {"start": v(-59.8, -16.95) * mm, "end": v(-59.84, -16.93) * mm});
            skLineSegment(sketch, "E2304", {"start": v(-59.84, -16.93) * mm, "end": v(-60.06, -16.61) * mm});
            skLineSegment(sketch, "E2305", {"start": v(-60.06, -16.61) * mm, "end": v(-60.06, -16.51) * mm});
            skLineSegment(sketch, "E2306", {"start": v(-60.06, -16.51) * mm, "end": v(-60.06, -16.4) * mm});
            skLineSegment(sketch, "E2307", {"start": v(-60.06, -16.4) * mm, "end": v(-59.84, -16.1) * mm});
            skLineSegment(sketch, "E2308", {"start": v(-59.84, -16.1) * mm, "end": v(-59.8, -16.07) * mm});
            skLineSegment(sketch, "E2309", {"start": v(-59.8, -16.07) * mm, "end": v(-59.76, -16.05) * mm});
            skLineSegment(sketch, "E2310", {"start": v(-59.76, -16.05) * mm, "end": v(-59.33, -16.05) * mm});
            skLineSegment(sketch, "E2311", {"start": v(-59.33, -16.05) * mm, "end": v(-59.3, -16.07) * mm});
            skLineSegment(sketch, "E2312", {"start": v(-59.3, -16.07) * mm, "end": v(-59.26, -16.1) * mm});
            skLineSegment(sketch, "E2313", {"start": v(-59.26, -16.1) * mm, "end": v(-59.04, -16.4) * mm});
            skLineSegment(sketch, "E2314", {"start": v(-59.04, -16.4) * mm, "end": v(-59.04, -16.51) * mm});
            skLineSegment(sketch, "E2315", {"start": v(-61.58, -19.05) * mm, "end": v(-61.58, -19.16) * mm});
            skLineSegment(sketch, "E2316", {"start": v(-61.58, -19.16) * mm, "end": v(-61.8, -19.47) * mm});
            skLineSegment(sketch, "E2317", {"start": v(-61.8, -19.47) * mm, "end": v(-61.83, -19.49) * mm});
            skLineSegment(sketch, "E2318", {"start": v(-61.83, -19.49) * mm, "end": v(-61.87, -19.51) * mm});
            skLineSegment(sketch, "E2319", {"start": v(-61.87, -19.51) * mm, "end": v(-62.3, -19.51) * mm});
            skLineSegment(sketch, "E2320", {"start": v(-62.3, -19.51) * mm, "end": v(-62.34, -19.49) * mm});
            skLineSegment(sketch, "E2321", {"start": v(-62.34, -19.49) * mm, "end": v(-62.38, -19.47) * mm});
            skLineSegment(sketch, "E2322", {"start": v(-62.38, -19.47) * mm, "end": v(-62.6, -19.15) * mm});
            skLineSegment(sketch, "E2323", {"start": v(-62.6, -19.15) * mm, "end": v(-62.6, -19.05) * mm});
            skLineSegment(sketch, "E2324", {"start": v(-62.6, -19.05) * mm, "end": v(-62.6, -18.94) * mm});
            skLineSegment(sketch, "E2325", {"start": v(-62.6, -18.94) * mm, "end": v(-62.38, -18.63) * mm});
            skLineSegment(sketch, "E2326", {"start": v(-62.38, -18.63) * mm, "end": v(-62.34, -18.61) * mm});
            skLineSegment(sketch, "E2327", {"start": v(-62.34, -18.61) * mm, "end": v(-62.3, -18.59) * mm});
            skLineSegment(sketch, "E2328", {"start": v(-62.3, -18.59) * mm, "end": v(-61.87, -18.59) * mm});
            skLineSegment(sketch, "E2329", {"start": v(-61.87, -18.59) * mm, "end": v(-61.83, -18.61) * mm});
            skLineSegment(sketch, "E2330", {"start": v(-61.83, -18.61) * mm, "end": v(-61.8, -18.63) * mm});
            skLineSegment(sketch, "E2331", {"start": v(-61.8, -18.63) * mm, "end": v(-61.58, -18.95) * mm});
            skLineSegment(sketch, "E2332", {"start": v(-61.58, -18.95) * mm, "end": v(-61.58, -19.05) * mm});
            skLineSegment(sketch, "E2333", {"start": v(-59.04, -19.05) * mm, "end": v(-59.04, -19.16) * mm});
            skLineSegment(sketch, "E2334", {"start": v(-59.04, -19.16) * mm, "end": v(-59.26, -19.47) * mm});
            skLineSegment(sketch, "E2335", {"start": v(-59.26, -19.47) * mm, "end": v(-59.3, -19.49) * mm});
            skLineSegment(sketch, "E2336", {"start": v(-59.3, -19.49) * mm, "end": v(-59.33, -19.51) * mm});
            skLineSegment(sketch, "E2337", {"start": v(-59.33, -19.51) * mm, "end": v(-59.76, -19.51) * mm});
            skLineSegment(sketch, "E2338", {"start": v(-59.76, -19.51) * mm, "end": v(-59.8, -19.49) * mm});
            skLineSegment(sketch, "E2339", {"start": v(-59.8, -19.49) * mm, "end": v(-59.84, -19.47) * mm});
            skLineSegment(sketch, "E2340", {"start": v(-59.84, -19.47) * mm, "end": v(-60.06, -19.15) * mm});
            skLineSegment(sketch, "E2341", {"start": v(-60.06, -19.15) * mm, "end": v(-60.06, -19.05) * mm});
            skLineSegment(sketch, "E2342", {"start": v(-60.06, -19.05) * mm, "end": v(-60.06, -18.94) * mm});
            skLineSegment(sketch, "E2343", {"start": v(-60.06, -18.94) * mm, "end": v(-59.84, -18.63) * mm});
            skLineSegment(sketch, "E2344", {"start": v(-59.84, -18.63) * mm, "end": v(-59.8, -18.61) * mm});
            skLineSegment(sketch, "E2345", {"start": v(-59.8, -18.61) * mm, "end": v(-59.76, -18.59) * mm});
            skLineSegment(sketch, "E2346", {"start": v(-59.76, -18.59) * mm, "end": v(-59.33, -18.59) * mm});
            skLineSegment(sketch, "E2347", {"start": v(-59.33, -18.59) * mm, "end": v(-59.3, -18.61) * mm});
            skLineSegment(sketch, "E2348", {"start": v(-59.3, -18.61) * mm, "end": v(-59.26, -18.63) * mm});
            skLineSegment(sketch, "E2349", {"start": v(-59.26, -18.63) * mm, "end": v(-59.04, -18.95) * mm});
            skLineSegment(sketch, "E2350", {"start": v(-59.04, -18.95) * mm, "end": v(-59.04, -19.05) * mm});
            skLineSegment(sketch, "E2351", {"start": v(-61.58, -21.59) * mm, "end": v(-61.58, -21.7) * mm});
            skLineSegment(sketch, "E2352", {"start": v(-61.58, -21.7) * mm, "end": v(-61.8, -22) * mm});
            skLineSegment(sketch, "E2353", {"start": v(-61.8, -22) * mm, "end": v(-61.83, -22.03) * mm});
            skLineSegment(sketch, "E2354", {"start": v(-61.83, -22.03) * mm, "end": v(-61.87, -22.05) * mm});
            skLineSegment(sketch, "E2355", {"start": v(-61.87, -22.05) * mm, "end": v(-62.3, -22.05) * mm});
            skLineSegment(sketch, "E2356", {"start": v(-62.3, -22.05) * mm, "end": v(-62.34, -22.03) * mm});
            skLineSegment(sketch, "E2357", {"start": v(-62.34, -22.03) * mm, "end": v(-62.38, -22) * mm});
            skLineSegment(sketch, "E2358", {"start": v(-62.38, -22) * mm, "end": v(-62.6, -21.7) * mm});
            skLineSegment(sketch, "E2359", {"start": v(-62.6, -21.7) * mm, "end": v(-62.6, -21.59) * mm});
            skLineSegment(sketch, "E2360", {"start": v(-62.6, -21.59) * mm, "end": v(-62.6, -21.48) * mm});
            skLineSegment(sketch, "E2361", {"start": v(-62.6, -21.48) * mm, "end": v(-62.38, -21.17) * mm});
            skLineSegment(sketch, "E2362", {"start": v(-62.38, -21.17) * mm, "end": v(-62.34, -21.15) * mm});
            skLineSegment(sketch, "E2363", {"start": v(-62.34, -21.15) * mm, "end": v(-62.3, -21.13) * mm});
            skLineSegment(sketch, "E2364", {"start": v(-62.3, -21.13) * mm, "end": v(-61.87, -21.13) * mm});
            skLineSegment(sketch, "E2365", {"start": v(-61.87, -21.13) * mm, "end": v(-61.83, -21.15) * mm});
            skLineSegment(sketch, "E2366", {"start": v(-61.83, -21.15) * mm, "end": v(-61.8, -21.17) * mm});
            skLineSegment(sketch, "E2367", {"start": v(-61.8, -21.17) * mm, "end": v(-61.58, -21.48) * mm});
            skLineSegment(sketch, "E2368", {"start": v(-61.58, -21.48) * mm, "end": v(-61.58, -21.59) * mm});
            skLineSegment(sketch, "E2369", {"start": v(-59.04, -21.59) * mm, "end": v(-59.04, -21.7) * mm});
            skLineSegment(sketch, "E2370", {"start": v(-59.04, -21.7) * mm, "end": v(-59.26, -22) * mm});
            skLineSegment(sketch, "E2371", {"start": v(-59.26, -22) * mm, "end": v(-59.3, -22.03) * mm});
            skLineSegment(sketch, "E2372", {"start": v(-59.3, -22.03) * mm, "end": v(-59.33, -22.05) * mm});
            skLineSegment(sketch, "E2373", {"start": v(-59.33, -22.05) * mm, "end": v(-59.76, -22.05) * mm});
            skLineSegment(sketch, "E2374", {"start": v(-59.76, -22.05) * mm, "end": v(-59.8, -22.03) * mm});
            skLineSegment(sketch, "E2375", {"start": v(-59.8, -22.03) * mm, "end": v(-59.84, -22) * mm});
            skLineSegment(sketch, "E2376", {"start": v(-59.84, -22) * mm, "end": v(-60.06, -21.7) * mm});
            skLineSegment(sketch, "E2377", {"start": v(-60.06, -21.7) * mm, "end": v(-60.06, -21.59) * mm});
            skLineSegment(sketch, "E2378", {"start": v(-60.06, -21.59) * mm, "end": v(-60.06, -21.48) * mm});
            skLineSegment(sketch, "E2379", {"start": v(-60.06, -21.48) * mm, "end": v(-59.84, -21.17) * mm});
            skLineSegment(sketch, "E2380", {"start": v(-59.84, -21.17) * mm, "end": v(-59.8, -21.15) * mm});
            skLineSegment(sketch, "E2381", {"start": v(-59.8, -21.15) * mm, "end": v(-59.76, -21.13) * mm});
            skLineSegment(sketch, "E2382", {"start": v(-59.76, -21.13) * mm, "end": v(-59.33, -21.13) * mm});
            skLineSegment(sketch, "E2383", {"start": v(-59.33, -21.13) * mm, "end": v(-59.3, -21.15) * mm});
            skLineSegment(sketch, "E2384", {"start": v(-59.3, -21.15) * mm, "end": v(-59.26, -21.17) * mm});
            skLineSegment(sketch, "E2385", {"start": v(-59.26, -21.17) * mm, "end": v(-59.04, -21.48) * mm});
            skLineSegment(sketch, "E2386", {"start": v(-59.04, -21.48) * mm, "end": v(-59.04, -21.59) * mm});
            skLineSegment(sketch, "E2387", {"start": v(-61.58, -24.13) * mm, "end": v(-61.58, -24.24) * mm});
            skLineSegment(sketch, "E2388", {"start": v(-61.58, -24.24) * mm, "end": v(-61.8, -24.55) * mm});
            skLineSegment(sketch, "E2389", {"start": v(-61.8, -24.55) * mm, "end": v(-61.83, -24.57) * mm});
            skLineSegment(sketch, "E2390", {"start": v(-61.83, -24.57) * mm, "end": v(-61.87, -24.6) * mm});
            skLineSegment(sketch, "E2391", {"start": v(-61.87, -24.6) * mm, "end": v(-62.3, -24.6) * mm});
            skLineSegment(sketch, "E2392", {"start": v(-62.3, -24.6) * mm, "end": v(-62.34, -24.57) * mm});
            skLineSegment(sketch, "E2393", {"start": v(-62.34, -24.57) * mm, "end": v(-62.38, -24.55) * mm});
            skLineSegment(sketch, "E2394", {"start": v(-62.38, -24.55) * mm, "end": v(-62.6, -24.23) * mm});
            skLineSegment(sketch, "E2395", {"start": v(-62.6, -24.23) * mm, "end": v(-62.6, -24.13) * mm});
            skLineSegment(sketch, "E2396", {"start": v(-62.6, -24.13) * mm, "end": v(-62.6, -24.02) * mm});
            skLineSegment(sketch, "E2397", {"start": v(-62.6, -24.02) * mm, "end": v(-62.38, -23.71) * mm});
            skLineSegment(sketch, "E2398", {"start": v(-62.38, -23.71) * mm, "end": v(-62.34, -23.69) * mm});
            skLineSegment(sketch, "E2399", {"start": v(-62.34, -23.69) * mm, "end": v(-62.3, -23.67) * mm});
            skLineSegment(sketch, "E2400", {"start": v(-62.3, -23.67) * mm, "end": v(-61.87, -23.67) * mm});
            skLineSegment(sketch, "E2401", {"start": v(-61.87, -23.67) * mm, "end": v(-61.83, -23.69) * mm});
            skLineSegment(sketch, "E2402", {"start": v(-61.83, -23.69) * mm, "end": v(-61.8, -23.71) * mm});
            skLineSegment(sketch, "E2403", {"start": v(-61.8, -23.71) * mm, "end": v(-61.58, -24.02) * mm});
            skLineSegment(sketch, "E2404", {"start": v(-61.58, -24.02) * mm, "end": v(-61.58, -24.13) * mm});
            skLineSegment(sketch, "E2405", {"start": v(-59.04, -24.13) * mm, "end": v(-59.04, -24.24) * mm});
            skLineSegment(sketch, "E2406", {"start": v(-59.04, -24.24) * mm, "end": v(-59.26, -24.55) * mm});
            skLineSegment(sketch, "E2407", {"start": v(-59.26, -24.55) * mm, "end": v(-59.3, -24.57) * mm});
            skLineSegment(sketch, "E2408", {"start": v(-59.3, -24.57) * mm, "end": v(-59.33, -24.6) * mm});
            skLineSegment(sketch, "E2409", {"start": v(-59.33, -24.6) * mm, "end": v(-59.76, -24.6) * mm});
            skLineSegment(sketch, "E2410", {"start": v(-59.76, -24.6) * mm, "end": v(-59.8, -24.57) * mm});
            skLineSegment(sketch, "E2411", {"start": v(-59.8, -24.57) * mm, "end": v(-59.84, -24.55) * mm});
            skLineSegment(sketch, "E2412", {"start": v(-59.84, -24.55) * mm, "end": v(-60.06, -24.23) * mm});
            skLineSegment(sketch, "E2413", {"start": v(-60.06, -24.23) * mm, "end": v(-60.06, -24.13) * mm});
            skLineSegment(sketch, "E2414", {"start": v(-60.06, -24.13) * mm, "end": v(-60.06, -24.02) * mm});
            skLineSegment(sketch, "E2415", {"start": v(-60.06, -24.02) * mm, "end": v(-59.84, -23.71) * mm});
            skLineSegment(sketch, "E2416", {"start": v(-59.84, -23.71) * mm, "end": v(-59.8, -23.69) * mm});
            skLineSegment(sketch, "E2417", {"start": v(-59.8, -23.69) * mm, "end": v(-59.76, -23.67) * mm});
            skLineSegment(sketch, "E2418", {"start": v(-59.76, -23.67) * mm, "end": v(-59.33, -23.67) * mm});
            skLineSegment(sketch, "E2419", {"start": v(-59.33, -23.67) * mm, "end": v(-59.3, -23.69) * mm});
            skLineSegment(sketch, "E2420", {"start": v(-59.3, -23.69) * mm, "end": v(-59.26, -23.71) * mm});
            skLineSegment(sketch, "E2421", {"start": v(-59.26, -23.71) * mm, "end": v(-59.04, -24.02) * mm});
            skLineSegment(sketch, "E2422", {"start": v(-59.04, -24.02) * mm, "end": v(-59.04, -24.13) * mm});
            skLineSegment(sketch, "E2423", {"start": v(-61.58, -26.67) * mm, "end": v(-61.58, -26.78) * mm});
            skLineSegment(sketch, "E2424", {"start": v(-61.58, -26.78) * mm, "end": v(-61.8, -27.09) * mm});
            skLineSegment(sketch, "E2425", {"start": v(-61.8, -27.09) * mm, "end": v(-61.83, -27.11) * mm});
            skLineSegment(sketch, "E2426", {"start": v(-61.83, -27.11) * mm, "end": v(-61.87, -27.13) * mm});
            skLineSegment(sketch, "E2427", {"start": v(-61.87, -27.13) * mm, "end": v(-62.3, -27.13) * mm});
            skLineSegment(sketch, "E2428", {"start": v(-62.3, -27.13) * mm, "end": v(-62.34, -27.11) * mm});
            skLineSegment(sketch, "E2429", {"start": v(-62.34, -27.11) * mm, "end": v(-62.38, -27.09) * mm});
            skLineSegment(sketch, "E2430", {"start": v(-62.38, -27.09) * mm, "end": v(-62.6, -26.77) * mm});
            skLineSegment(sketch, "E2431", {"start": v(-62.6, -26.77) * mm, "end": v(-62.6, -26.67) * mm});
            skLineSegment(sketch, "E2432", {"start": v(-62.6, -26.67) * mm, "end": v(-62.6, -26.56) * mm});
            skLineSegment(sketch, "E2433", {"start": v(-62.6, -26.56) * mm, "end": v(-62.38, -26.25) * mm});
            skLineSegment(sketch, "E2434", {"start": v(-62.38, -26.25) * mm, "end": v(-62.34, -26.23) * mm});
            skLineSegment(sketch, "E2435", {"start": v(-62.34, -26.23) * mm, "end": v(-62.3, -26.2) * mm});
            skLineSegment(sketch, "E2436", {"start": v(-62.3, -26.2) * mm, "end": v(-61.87, -26.2) * mm});
            skLineSegment(sketch, "E2437", {"start": v(-61.87, -26.2) * mm, "end": v(-61.83, -26.23) * mm});
            skLineSegment(sketch, "E2438", {"start": v(-61.83, -26.23) * mm, "end": v(-61.8, -26.25) * mm});
            skLineSegment(sketch, "E2439", {"start": v(-61.8, -26.25) * mm, "end": v(-61.58, -26.57) * mm});
            skLineSegment(sketch, "E2440", {"start": v(-61.58, -26.57) * mm, "end": v(-61.58, -26.67) * mm});
            skLineSegment(sketch, "E2441", {"start": v(-59.04, -26.67) * mm, "end": v(-59.04, -26.78) * mm});
            skLineSegment(sketch, "E2442", {"start": v(-59.04, -26.78) * mm, "end": v(-59.26, -27.09) * mm});
            skLineSegment(sketch, "E2443", {"start": v(-59.26, -27.09) * mm, "end": v(-59.3, -27.11) * mm});
            skLineSegment(sketch, "E2444", {"start": v(-59.3, -27.11) * mm, "end": v(-59.33, -27.13) * mm});
            skLineSegment(sketch, "E2445", {"start": v(-59.33, -27.13) * mm, "end": v(-59.76, -27.13) * mm});
            skLineSegment(sketch, "E2446", {"start": v(-59.76, -27.13) * mm, "end": v(-59.8, -27.11) * mm});
            skLineSegment(sketch, "E2447", {"start": v(-59.8, -27.11) * mm, "end": v(-59.84, -27.09) * mm});
            skLineSegment(sketch, "E2448", {"start": v(-59.84, -27.09) * mm, "end": v(-60.06, -26.77) * mm});
            skLineSegment(sketch, "E2449", {"start": v(-60.06, -26.77) * mm, "end": v(-60.06, -26.67) * mm});
            skLineSegment(sketch, "E2450", {"start": v(-60.06, -26.67) * mm, "end": v(-60.06, -26.56) * mm});
            skLineSegment(sketch, "E2451", {"start": v(-60.06, -26.56) * mm, "end": v(-59.84, -26.25) * mm});
            skLineSegment(sketch, "E2452", {"start": v(-59.84, -26.25) * mm, "end": v(-59.8, -26.23) * mm});
            skLineSegment(sketch, "E2453", {"start": v(-59.8, -26.23) * mm, "end": v(-59.76, -26.2) * mm});
            skLineSegment(sketch, "E2454", {"start": v(-59.76, -26.2) * mm, "end": v(-59.33, -26.2) * mm});
            skLineSegment(sketch, "E2455", {"start": v(-59.33, -26.2) * mm, "end": v(-59.3, -26.23) * mm});
            skLineSegment(sketch, "E2456", {"start": v(-59.3, -26.23) * mm, "end": v(-59.26, -26.25) * mm});
            skLineSegment(sketch, "E2457", {"start": v(-59.26, -26.25) * mm, "end": v(-59.04, -26.57) * mm});
            skLineSegment(sketch, "E2458", {"start": v(-59.04, -26.57) * mm, "end": v(-59.04, -26.67) * mm});
            skLineSegment(sketch, "E2459", {"start": v(-61.58, -29.21) * mm, "end": v(-61.58, -29.32) * mm});
            skLineSegment(sketch, "E2460", {"start": v(-61.58, -29.32) * mm, "end": v(-61.8, -29.63) * mm});
            skLineSegment(sketch, "E2461", {"start": v(-61.8, -29.63) * mm, "end": v(-61.83, -29.65) * mm});
            skLineSegment(sketch, "E2462", {"start": v(-61.83, -29.65) * mm, "end": v(-61.87, -29.67) * mm});
            skLineSegment(sketch, "E2463", {"start": v(-61.87, -29.67) * mm, "end": v(-62.3, -29.67) * mm});
            skLineSegment(sketch, "E2464", {"start": v(-62.3, -29.67) * mm, "end": v(-62.34, -29.65) * mm});
            skLineSegment(sketch, "E2465", {"start": v(-62.34, -29.65) * mm, "end": v(-62.38, -29.63) * mm});
            skLineSegment(sketch, "E2466", {"start": v(-62.38, -29.63) * mm, "end": v(-62.6, -29.31) * mm});
            skLineSegment(sketch, "E2467", {"start": v(-62.6, -29.31) * mm, "end": v(-62.6, -29.21) * mm});
            skLineSegment(sketch, "E2468", {"start": v(-62.6, -29.21) * mm, "end": v(-62.6, -29.1) * mm});
            skLineSegment(sketch, "E2469", {"start": v(-62.6, -29.1) * mm, "end": v(-62.38, -28.8) * mm});
            skLineSegment(sketch, "E2470", {"start": v(-62.38, -28.8) * mm, "end": v(-62.34, -28.77) * mm});
            skLineSegment(sketch, "E2471", {"start": v(-62.34, -28.77) * mm, "end": v(-62.3, -28.75) * mm});
            skLineSegment(sketch, "E2472", {"start": v(-62.3, -28.75) * mm, "end": v(-61.87, -28.75) * mm});
            skLineSegment(sketch, "E2473", {"start": v(-61.87, -28.75) * mm, "end": v(-61.83, -28.77) * mm});
            skLineSegment(sketch, "E2474", {"start": v(-61.83, -28.77) * mm, "end": v(-61.8, -28.8) * mm});
            skLineSegment(sketch, "E2475", {"start": v(-61.8, -28.8) * mm, "end": v(-61.58, -29.1) * mm});
            skLineSegment(sketch, "E2476", {"start": v(-61.58, -29.1) * mm, "end": v(-61.58, -29.21) * mm});
            skLineSegment(sketch, "E2477", {"start": v(-59.04, -29.21) * mm, "end": v(-59.04, -29.32) * mm});
            skLineSegment(sketch, "E2478", {"start": v(-59.04, -29.32) * mm, "end": v(-59.26, -29.63) * mm});
            skLineSegment(sketch, "E2479", {"start": v(-59.26, -29.63) * mm, "end": v(-59.3, -29.65) * mm});
            skLineSegment(sketch, "E2480", {"start": v(-59.3, -29.65) * mm, "end": v(-59.33, -29.67) * mm});
            skLineSegment(sketch, "E2481", {"start": v(-59.33, -29.67) * mm, "end": v(-59.76, -29.67) * mm});
            skLineSegment(sketch, "E2482", {"start": v(-59.76, -29.67) * mm, "end": v(-59.8, -29.65) * mm});
            skLineSegment(sketch, "E2483", {"start": v(-59.8, -29.65) * mm, "end": v(-59.84, -29.63) * mm});
            skLineSegment(sketch, "E2484", {"start": v(-59.84, -29.63) * mm, "end": v(-60.06, -29.31) * mm});
            skLineSegment(sketch, "E2485", {"start": v(-60.06, -29.31) * mm, "end": v(-60.06, -29.21) * mm});
            skLineSegment(sketch, "E2486", {"start": v(-60.06, -29.21) * mm, "end": v(-60.06, -29.1) * mm});
            skLineSegment(sketch, "E2487", {"start": v(-60.06, -29.1) * mm, "end": v(-59.84, -28.8) * mm});
            skLineSegment(sketch, "E2488", {"start": v(-59.84, -28.8) * mm, "end": v(-59.8, -28.77) * mm});
            skLineSegment(sketch, "E2489", {"start": v(-59.8, -28.77) * mm, "end": v(-59.76, -28.75) * mm});
            skLineSegment(sketch, "E2490", {"start": v(-59.76, -28.75) * mm, "end": v(-59.33, -28.75) * mm});
            skLineSegment(sketch, "E2491", {"start": v(-59.33, -28.75) * mm, "end": v(-59.3, -28.77) * mm});
            skLineSegment(sketch, "E2492", {"start": v(-59.3, -28.77) * mm, "end": v(-59.26, -28.8) * mm});
            skLineSegment(sketch, "E2493", {"start": v(-59.26, -28.8) * mm, "end": v(-59.04, -29.1) * mm});
            skLineSegment(sketch, "E2494", {"start": v(-59.04, -29.1) * mm, "end": v(-59.04, -29.21) * mm});
            skLineSegment(sketch, "E2495", {"start": v(-61.58, -31.75) * mm, "end": v(-61.58, -31.86) * mm});
            skLineSegment(sketch, "E2496", {"start": v(-61.58, -31.86) * mm, "end": v(-61.8, -32.17) * mm});
            skLineSegment(sketch, "E2497", {"start": v(-61.8, -32.17) * mm, "end": v(-61.83, -32.19) * mm});
            skLineSegment(sketch, "E2498", {"start": v(-61.83, -32.19) * mm, "end": v(-61.87, -32.21) * mm});
            skLineSegment(sketch, "E2499", {"start": v(-61.87, -32.21) * mm, "end": v(-62.3, -32.21) * mm});
            skLineSegment(sketch, "E2500", {"start": v(-62.3, -32.21) * mm, "end": v(-62.34, -32.19) * mm});
            skLineSegment(sketch, "E2501", {"start": v(-62.34, -32.19) * mm, "end": v(-62.38, -32.17) * mm});
            skLineSegment(sketch, "E2502", {"start": v(-62.38, -32.17) * mm, "end": v(-62.6, -31.85) * mm});
            skLineSegment(sketch, "E2503", {"start": v(-62.6, -31.85) * mm, "end": v(-62.6, -31.75) * mm});
            skLineSegment(sketch, "E2504", {"start": v(-62.6, -31.75) * mm, "end": v(-62.6, -31.64) * mm});
            skLineSegment(sketch, "E2505", {"start": v(-62.6, -31.64) * mm, "end": v(-62.38, -31.33) * mm});
            skLineSegment(sketch, "E2506", {"start": v(-62.38, -31.33) * mm, "end": v(-62.34, -31.31) * mm});
            skLineSegment(sketch, "E2507", {"start": v(-62.34, -31.31) * mm, "end": v(-62.3, -31.29) * mm});
            skLineSegment(sketch, "E2508", {"start": v(-62.3, -31.29) * mm, "end": v(-61.87, -31.29) * mm});
            skLineSegment(sketch, "E2509", {"start": v(-61.87, -31.29) * mm, "end": v(-61.83, -31.31) * mm});
            skLineSegment(sketch, "E2510", {"start": v(-61.83, -31.31) * mm, "end": v(-61.8, -31.33) * mm});
            skLineSegment(sketch, "E2511", {"start": v(-61.8, -31.33) * mm, "end": v(-61.58, -31.65) * mm});
            skLineSegment(sketch, "E2512", {"start": v(-61.58, -31.65) * mm, "end": v(-61.58, -31.75) * mm});
            skLineSegment(sketch, "E2513", {"start": v(-59.04, -31.75) * mm, "end": v(-59.04, -31.86) * mm});
            skLineSegment(sketch, "E2514", {"start": v(-59.04, -31.86) * mm, "end": v(-59.26, -32.17) * mm});
            skLineSegment(sketch, "E2515", {"start": v(-59.26, -32.17) * mm, "end": v(-59.3, -32.19) * mm});
            skLineSegment(sketch, "E2516", {"start": v(-59.3, -32.19) * mm, "end": v(-59.33, -32.21) * mm});
            skLineSegment(sketch, "E2517", {"start": v(-59.33, -32.21) * mm, "end": v(-59.76, -32.21) * mm});
            skLineSegment(sketch, "E2518", {"start": v(-59.76, -32.21) * mm, "end": v(-59.8, -32.19) * mm});
            skLineSegment(sketch, "E2519", {"start": v(-59.8, -32.19) * mm, "end": v(-59.84, -32.17) * mm});
            skLineSegment(sketch, "E2520", {"start": v(-59.84, -32.17) * mm, "end": v(-60.06, -31.85) * mm});
            skLineSegment(sketch, "E2521", {"start": v(-60.06, -31.85) * mm, "end": v(-60.06, -31.75) * mm});
            skLineSegment(sketch, "E2522", {"start": v(-60.06, -31.75) * mm, "end": v(-60.06, -31.64) * mm});
            skLineSegment(sketch, "E2523", {"start": v(-60.06, -31.64) * mm, "end": v(-59.84, -31.33) * mm});
            skLineSegment(sketch, "E2524", {"start": v(-59.84, -31.33) * mm, "end": v(-59.8, -31.31) * mm});
            skLineSegment(sketch, "E2525", {"start": v(-59.8, -31.31) * mm, "end": v(-59.76, -31.29) * mm});
            skLineSegment(sketch, "E2526", {"start": v(-59.76, -31.29) * mm, "end": v(-59.33, -31.29) * mm});
            skLineSegment(sketch, "E2527", {"start": v(-59.33, -31.29) * mm, "end": v(-59.3, -31.31) * mm});
            skLineSegment(sketch, "E2528", {"start": v(-59.3, -31.31) * mm, "end": v(-59.26, -31.33) * mm});
            skLineSegment(sketch, "E2529", {"start": v(-59.26, -31.33) * mm, "end": v(-59.04, -31.65) * mm});
            skLineSegment(sketch, "E2530", {"start": v(-59.04, -31.65) * mm, "end": v(-59.04, -31.75) * mm});
            skLineSegment(sketch, "E2531", {"start": v(-61.58, -34.29) * mm, "end": v(-61.58, -34.4) * mm});
            skLineSegment(sketch, "E2532", {"start": v(-61.58, -34.4) * mm, "end": v(-61.8, -34.7) * mm});
            skLineSegment(sketch, "E2533", {"start": v(-61.8, -34.7) * mm, "end": v(-61.83, -34.73) * mm});
            skLineSegment(sketch, "E2534", {"start": v(-61.83, -34.73) * mm, "end": v(-61.87, -34.75) * mm});
            skLineSegment(sketch, "E2535", {"start": v(-61.87, -34.75) * mm, "end": v(-62.3, -34.75) * mm});
            skLineSegment(sketch, "E2536", {"start": v(-62.3, -34.75) * mm, "end": v(-62.34, -34.73) * mm});
            skLineSegment(sketch, "E2537", {"start": v(-62.34, -34.73) * mm, "end": v(-62.38, -34.7) * mm});
            skLineSegment(sketch, "E2538", {"start": v(-62.38, -34.7) * mm, "end": v(-62.6, -34.4) * mm});
            skLineSegment(sketch, "E2539", {"start": v(-62.6, -34.4) * mm, "end": v(-62.6, -34.29) * mm});
            skLineSegment(sketch, "E2540", {"start": v(-62.6, -34.29) * mm, "end": v(-62.6, -34.18) * mm});
            skLineSegment(sketch, "E2541", {"start": v(-62.6, -34.18) * mm, "end": v(-62.38, -33.87) * mm});
            skLineSegment(sketch, "E2542", {"start": v(-62.38, -33.87) * mm, "end": v(-62.34, -33.85) * mm});
            skLineSegment(sketch, "E2543", {"start": v(-62.34, -33.85) * mm, "end": v(-62.3, -33.83) * mm});
            skLineSegment(sketch, "E2544", {"start": v(-62.3, -33.83) * mm, "end": v(-61.87, -33.83) * mm});
            skLineSegment(sketch, "E2545", {"start": v(-61.87, -33.83) * mm, "end": v(-61.83, -33.85) * mm});
            skLineSegment(sketch, "E2546", {"start": v(-61.83, -33.85) * mm, "end": v(-61.8, -33.87) * mm});
            skLineSegment(sketch, "E2547", {"start": v(-61.8, -33.87) * mm, "end": v(-61.58, -34.19) * mm});
            skLineSegment(sketch, "E2548", {"start": v(-61.58, -34.19) * mm, "end": v(-61.58, -34.29) * mm});
            skLineSegment(sketch, "E2549", {"start": v(-59.04, -34.29) * mm, "end": v(-59.04, -34.4) * mm});
            skLineSegment(sketch, "E2550", {"start": v(-59.04, -34.4) * mm, "end": v(-59.26, -34.7) * mm});
            skLineSegment(sketch, "E2551", {"start": v(-59.26, -34.7) * mm, "end": v(-59.3, -34.73) * mm});
            skLineSegment(sketch, "E2552", {"start": v(-59.3, -34.73) * mm, "end": v(-59.33, -34.75) * mm});
            skLineSegment(sketch, "E2553", {"start": v(-59.33, -34.75) * mm, "end": v(-59.76, -34.75) * mm});
            skLineSegment(sketch, "E2554", {"start": v(-59.76, -34.75) * mm, "end": v(-59.8, -34.73) * mm});
            skLineSegment(sketch, "E2555", {"start": v(-59.8, -34.73) * mm, "end": v(-59.84, -34.7) * mm});
            skLineSegment(sketch, "E2556", {"start": v(-59.84, -34.7) * mm, "end": v(-60.06, -34.4) * mm});
            skLineSegment(sketch, "E2557", {"start": v(-60.06, -34.4) * mm, "end": v(-60.06, -34.29) * mm});
            skLineSegment(sketch, "E2558", {"start": v(-60.06, -34.29) * mm, "end": v(-60.06, -34.18) * mm});
            skLineSegment(sketch, "E2559", {"start": v(-60.06, -34.18) * mm, "end": v(-59.84, -33.87) * mm});
            skLineSegment(sketch, "E2560", {"start": v(-59.84, -33.87) * mm, "end": v(-59.8, -33.85) * mm});
            skLineSegment(sketch, "E2561", {"start": v(-59.8, -33.85) * mm, "end": v(-59.76, -33.83) * mm});
            skLineSegment(sketch, "E2562", {"start": v(-59.76, -33.83) * mm, "end": v(-59.33, -33.83) * mm});
            skLineSegment(sketch, "E2563", {"start": v(-59.33, -33.83) * mm, "end": v(-59.3, -33.85) * mm});
            skLineSegment(sketch, "E2564", {"start": v(-59.3, -33.85) * mm, "end": v(-59.26, -33.87) * mm});
            skLineSegment(sketch, "E2565", {"start": v(-59.26, -33.87) * mm, "end": v(-59.04, -34.19) * mm});
            skLineSegment(sketch, "E2566", {"start": v(-59.04, -34.19) * mm, "end": v(-59.04, -34.29) * mm});
            skLineSegment(sketch, "E2567", {"start": v(-61.58, -36.83) * mm, "end": v(-61.58, -36.94) * mm});
            skLineSegment(sketch, "E2568", {"start": v(-61.58, -36.94) * mm, "end": v(-61.8, -37.25) * mm});
            skLineSegment(sketch, "E2569", {"start": v(-61.8, -37.25) * mm, "end": v(-61.83, -37.27) * mm});
            skLineSegment(sketch, "E2570", {"start": v(-61.83, -37.27) * mm, "end": v(-61.87, -37.3) * mm});
            skLineSegment(sketch, "E2571", {"start": v(-61.87, -37.3) * mm, "end": v(-62.3, -37.3) * mm});
            skLineSegment(sketch, "E2572", {"start": v(-62.3, -37.3) * mm, "end": v(-62.34, -37.27) * mm});
            skLineSegment(sketch, "E2573", {"start": v(-62.34, -37.27) * mm, "end": v(-62.38, -37.25) * mm});
            skLineSegment(sketch, "E2574", {"start": v(-62.38, -37.25) * mm, "end": v(-62.6, -36.93) * mm});
            skLineSegment(sketch, "E2575", {"start": v(-62.6, -36.93) * mm, "end": v(-62.6, -36.83) * mm});
            skLineSegment(sketch, "E2576", {"start": v(-62.6, -36.83) * mm, "end": v(-62.6, -36.72) * mm});
            skLineSegment(sketch, "E2577", {"start": v(-62.6, -36.72) * mm, "end": v(-62.38, -36.41) * mm});
            skLineSegment(sketch, "E2578", {"start": v(-62.38, -36.41) * mm, "end": v(-62.34, -36.39) * mm});
            skLineSegment(sketch, "E2579", {"start": v(-62.34, -36.39) * mm, "end": v(-62.3, -36.37) * mm});
            skLineSegment(sketch, "E2580", {"start": v(-62.3, -36.37) * mm, "end": v(-61.87, -36.37) * mm});
            skLineSegment(sketch, "E2581", {"start": v(-61.87, -36.37) * mm, "end": v(-61.83, -36.39) * mm});
            skLineSegment(sketch, "E2582", {"start": v(-61.83, -36.39) * mm, "end": v(-61.8, -36.41) * mm});
            skLineSegment(sketch, "E2583", {"start": v(-61.8, -36.41) * mm, "end": v(-61.58, -36.72) * mm});
            skLineSegment(sketch, "E2584", {"start": v(-61.58, -36.72) * mm, "end": v(-61.58, -36.83) * mm});
            skLineSegment(sketch, "E2585", {"start": v(-59.04, -36.83) * mm, "end": v(-59.04, -36.94) * mm});
            skLineSegment(sketch, "E2586", {"start": v(-59.04, -36.94) * mm, "end": v(-59.26, -37.25) * mm});
            skLineSegment(sketch, "E2587", {"start": v(-59.26, -37.25) * mm, "end": v(-59.3, -37.27) * mm});
            skLineSegment(sketch, "E2588", {"start": v(-59.3, -37.27) * mm, "end": v(-59.33, -37.3) * mm});
            skLineSegment(sketch, "E2589", {"start": v(-59.33, -37.3) * mm, "end": v(-59.76, -37.3) * mm});
            skLineSegment(sketch, "E2590", {"start": v(-59.76, -37.3) * mm, "end": v(-59.8, -37.27) * mm});
            skLineSegment(sketch, "E2591", {"start": v(-59.8, -37.27) * mm, "end": v(-59.84, -37.25) * mm});
            skLineSegment(sketch, "E2592", {"start": v(-59.84, -37.25) * mm, "end": v(-60.06, -36.93) * mm});
            skLineSegment(sketch, "E2593", {"start": v(-60.06, -36.93) * mm, "end": v(-60.06, -36.83) * mm});
            skLineSegment(sketch, "E2594", {"start": v(-60.06, -36.83) * mm, "end": v(-60.06, -36.72) * mm});
            skLineSegment(sketch, "E2595", {"start": v(-60.06, -36.72) * mm, "end": v(-59.84, -36.41) * mm});
            skLineSegment(sketch, "E2596", {"start": v(-59.84, -36.41) * mm, "end": v(-59.8, -36.39) * mm});
            skLineSegment(sketch, "E2597", {"start": v(-59.8, -36.39) * mm, "end": v(-59.76, -36.37) * mm});
            skLineSegment(sketch, "E2598", {"start": v(-59.76, -36.37) * mm, "end": v(-59.33, -36.37) * mm});
            skLineSegment(sketch, "E2599", {"start": v(-59.33, -36.37) * mm, "end": v(-59.3, -36.39) * mm});
            skLineSegment(sketch, "E2600", {"start": v(-59.3, -36.39) * mm, "end": v(-59.26, -36.41) * mm});
            skLineSegment(sketch, "E2601", {"start": v(-59.26, -36.41) * mm, "end": v(-59.04, -36.72) * mm});
            skLineSegment(sketch, "E2602", {"start": v(-59.04, -36.72) * mm, "end": v(-59.04, -36.83) * mm});
            skLineSegment(sketch, "E2603", {"start": v(-61.58, -39.37) * mm, "end": v(-61.58, -39.48) * mm});
            skLineSegment(sketch, "E2604", {"start": v(-61.58, -39.48) * mm, "end": v(-61.8, -39.79) * mm});
            skLineSegment(sketch, "E2605", {"start": v(-61.8, -39.79) * mm, "end": v(-61.83, -39.81) * mm});
            skLineSegment(sketch, "E2606", {"start": v(-61.83, -39.81) * mm, "end": v(-61.87, -39.83) * mm});
            skLineSegment(sketch, "E2607", {"start": v(-61.87, -39.83) * mm, "end": v(-62.3, -39.83) * mm});
            skLineSegment(sketch, "E2608", {"start": v(-62.3, -39.83) * mm, "end": v(-62.34, -39.81) * mm});
            skLineSegment(sketch, "E2609", {"start": v(-62.34, -39.81) * mm, "end": v(-62.38, -39.79) * mm});
            skLineSegment(sketch, "E2610", {"start": v(-62.38, -39.79) * mm, "end": v(-62.6, -39.47) * mm});
            skLineSegment(sketch, "E2611", {"start": v(-62.6, -39.47) * mm, "end": v(-62.6, -39.37) * mm});
            skLineSegment(sketch, "E2612", {"start": v(-62.6, -39.37) * mm, "end": v(-62.6, -39.26) * mm});
            skLineSegment(sketch, "E2613", {"start": v(-62.6, -39.26) * mm, "end": v(-62.38, -38.95) * mm});
            skLineSegment(sketch, "E2614", {"start": v(-62.38, -38.95) * mm, "end": v(-62.34, -38.93) * mm});
            skLineSegment(sketch, "E2615", {"start": v(-62.34, -38.93) * mm, "end": v(-62.3, -38.9) * mm});
            skLineSegment(sketch, "E2616", {"start": v(-62.3, -38.9) * mm, "end": v(-61.87, -38.9) * mm});
            skLineSegment(sketch, "E2617", {"start": v(-61.87, -38.9) * mm, "end": v(-61.83, -38.93) * mm});
            skLineSegment(sketch, "E2618", {"start": v(-61.83, -38.93) * mm, "end": v(-61.8, -38.95) * mm});
            skLineSegment(sketch, "E2619", {"start": v(-61.8, -38.95) * mm, "end": v(-61.58, -39.27) * mm});
            skLineSegment(sketch, "E2620", {"start": v(-61.58, -39.27) * mm, "end": v(-61.58, -39.37) * mm});
            skLineSegment(sketch, "E2621", {"start": v(-59.04, -39.37) * mm, "end": v(-59.04, -39.48) * mm});
            skLineSegment(sketch, "E2622", {"start": v(-59.04, -39.48) * mm, "end": v(-59.26, -39.79) * mm});
            skLineSegment(sketch, "E2623", {"start": v(-59.26, -39.79) * mm, "end": v(-59.3, -39.81) * mm});
            skLineSegment(sketch, "E2624", {"start": v(-59.3, -39.81) * mm, "end": v(-59.33, -39.83) * mm});
            skLineSegment(sketch, "E2625", {"start": v(-59.33, -39.83) * mm, "end": v(-59.76, -39.83) * mm});
            skLineSegment(sketch, "E2626", {"start": v(-59.76, -39.83) * mm, "end": v(-59.8, -39.81) * mm});
            skLineSegment(sketch, "E2627", {"start": v(-59.8, -39.81) * mm, "end": v(-59.84, -39.79) * mm});
            skLineSegment(sketch, "E2628", {"start": v(-59.84, -39.79) * mm, "end": v(-60.06, -39.47) * mm});
            skLineSegment(sketch, "E2629", {"start": v(-60.06, -39.47) * mm, "end": v(-60.06, -39.37) * mm});
            skLineSegment(sketch, "E2630", {"start": v(-60.06, -39.37) * mm, "end": v(-60.06, -39.26) * mm});
            skLineSegment(sketch, "E2631", {"start": v(-60.06, -39.26) * mm, "end": v(-59.84, -38.95) * mm});
            skLineSegment(sketch, "E2632", {"start": v(-59.84, -38.95) * mm, "end": v(-59.8, -38.93) * mm});
            skLineSegment(sketch, "E2633", {"start": v(-59.8, -38.93) * mm, "end": v(-59.76, -38.9) * mm});
            skLineSegment(sketch, "E2634", {"start": v(-59.76, -38.9) * mm, "end": v(-59.33, -38.9) * mm});
            skLineSegment(sketch, "E2635", {"start": v(-59.33, -38.9) * mm, "end": v(-59.3, -38.93) * mm});
            skLineSegment(sketch, "E2636", {"start": v(-59.3, -38.93) * mm, "end": v(-59.26, -38.95) * mm});
            skLineSegment(sketch, "E2637", {"start": v(-59.26, -38.95) * mm, "end": v(-59.04, -39.27) * mm});
            skLineSegment(sketch, "E2638", {"start": v(-59.04, -39.27) * mm, "end": v(-59.04, -39.37) * mm});
            skLineSegment(sketch, "E2639", {"start": v(-61.58, -41.91) * mm, "end": v(-61.58, -42.02) * mm});
            skLineSegment(sketch, "E2640", {"start": v(-61.58, -42.02) * mm, "end": v(-61.8, -42.33) * mm});
            skLineSegment(sketch, "E2641", {"start": v(-61.8, -42.33) * mm, "end": v(-61.83, -42.35) * mm});
            skLineSegment(sketch, "E2642", {"start": v(-61.83, -42.35) * mm, "end": v(-61.87, -42.37) * mm});
            skLineSegment(sketch, "E2643", {"start": v(-61.87, -42.37) * mm, "end": v(-62.3, -42.37) * mm});
            skLineSegment(sketch, "E2644", {"start": v(-62.3, -42.37) * mm, "end": v(-62.34, -42.35) * mm});
            skLineSegment(sketch, "E2645", {"start": v(-62.34, -42.35) * mm, "end": v(-62.38, -42.33) * mm});
            skLineSegment(sketch, "E2646", {"start": v(-62.38, -42.33) * mm, "end": v(-62.6, -42.01) * mm});
            skLineSegment(sketch, "E2647", {"start": v(-62.6, -42.01) * mm, "end": v(-62.6, -41.91) * mm});
            skLineSegment(sketch, "E2648", {"start": v(-62.6, -41.91) * mm, "end": v(-62.6, -41.8) * mm});
            skLineSegment(sketch, "E2649", {"start": v(-62.6, -41.8) * mm, "end": v(-62.38, -41.5) * mm});
            skLineSegment(sketch, "E2650", {"start": v(-62.38, -41.5) * mm, "end": v(-62.34, -41.47) * mm});
            skLineSegment(sketch, "E2651", {"start": v(-62.34, -41.47) * mm, "end": v(-62.3, -41.45) * mm});
            skLineSegment(sketch, "E2652", {"start": v(-62.3, -41.45) * mm, "end": v(-61.87, -41.45) * mm});
            skLineSegment(sketch, "E2653", {"start": v(-61.87, -41.45) * mm, "end": v(-61.83, -41.47) * mm});
            skLineSegment(sketch, "E2654", {"start": v(-61.83, -41.47) * mm, "end": v(-61.8, -41.5) * mm});
            skLineSegment(sketch, "E2655", {"start": v(-61.8, -41.5) * mm, "end": v(-61.58, -41.8) * mm});
            skLineSegment(sketch, "E2656", {"start": v(-61.58, -41.8) * mm, "end": v(-61.58, -41.91) * mm});
            skLineSegment(sketch, "E2657", {"start": v(-59.04, -41.91) * mm, "end": v(-59.04, -42.02) * mm});
            skLineSegment(sketch, "E2658", {"start": v(-59.04, -42.02) * mm, "end": v(-59.26, -42.33) * mm});
            skLineSegment(sketch, "E2659", {"start": v(-59.26, -42.33) * mm, "end": v(-59.3, -42.35) * mm});
            skLineSegment(sketch, "E2660", {"start": v(-59.3, -42.35) * mm, "end": v(-59.33, -42.37) * mm});
            skLineSegment(sketch, "E2661", {"start": v(-59.33, -42.37) * mm, "end": v(-59.76, -42.37) * mm});
            skLineSegment(sketch, "E2662", {"start": v(-59.76, -42.37) * mm, "end": v(-59.8, -42.35) * mm});
            skLineSegment(sketch, "E2663", {"start": v(-59.8, -42.35) * mm, "end": v(-59.84, -42.33) * mm});
            skLineSegment(sketch, "E2664", {"start": v(-59.84, -42.33) * mm, "end": v(-60.06, -42.01) * mm});
            skLineSegment(sketch, "E2665", {"start": v(-60.06, -42.01) * mm, "end": v(-60.06, -41.91) * mm});
            skLineSegment(sketch, "E2666", {"start": v(-60.06, -41.91) * mm, "end": v(-60.06, -41.8) * mm});
            skLineSegment(sketch, "E2667", {"start": v(-60.06, -41.8) * mm, "end": v(-59.84, -41.5) * mm});
            skLineSegment(sketch, "E2668", {"start": v(-59.84, -41.5) * mm, "end": v(-59.8, -41.47) * mm});
            skLineSegment(sketch, "E2669", {"start": v(-59.8, -41.47) * mm, "end": v(-59.76, -41.45) * mm});
            skLineSegment(sketch, "E2670", {"start": v(-59.76, -41.45) * mm, "end": v(-59.33, -41.45) * mm});
            skLineSegment(sketch, "E2671", {"start": v(-59.33, -41.45) * mm, "end": v(-59.3, -41.47) * mm});
            skLineSegment(sketch, "E2672", {"start": v(-59.3, -41.47) * mm, "end": v(-59.26, -41.5) * mm});
            skLineSegment(sketch, "E2673", {"start": v(-59.26, -41.5) * mm, "end": v(-59.04, -41.8) * mm});
            skLineSegment(sketch, "E2674", {"start": v(-59.04, -41.8) * mm, "end": v(-59.04, -41.91) * mm});
            skLineSegment(sketch, "E2675", {"start": v(-61.58, -44.45) * mm, "end": v(-61.58, -44.56) * mm});
            skLineSegment(sketch, "E2676", {"start": v(-61.58, -44.56) * mm, "end": v(-61.8, -44.87) * mm});
            skLineSegment(sketch, "E2677", {"start": v(-61.8, -44.87) * mm, "end": v(-61.83, -44.89) * mm});
            skLineSegment(sketch, "E2678", {"start": v(-61.83, -44.89) * mm, "end": v(-61.87, -44.91) * mm});
            skLineSegment(sketch, "E2679", {"start": v(-61.87, -44.91) * mm, "end": v(-62.3, -44.91) * mm});
            skLineSegment(sketch, "E2680", {"start": v(-62.3, -44.91) * mm, "end": v(-62.34, -44.89) * mm});
            skLineSegment(sketch, "E2681", {"start": v(-62.34, -44.89) * mm, "end": v(-62.38, -44.87) * mm});
            skLineSegment(sketch, "E2682", {"start": v(-62.38, -44.87) * mm, "end": v(-62.6, -44.55) * mm});
            skLineSegment(sketch, "E2683", {"start": v(-62.6, -44.55) * mm, "end": v(-62.6, -44.45) * mm});
            skLineSegment(sketch, "E2684", {"start": v(-62.6, -44.45) * mm, "end": v(-62.6, -44.34) * mm});
            skLineSegment(sketch, "E2685", {"start": v(-62.6, -44.34) * mm, "end": v(-62.38, -44.03) * mm});
            skLineSegment(sketch, "E2686", {"start": v(-62.38, -44.03) * mm, "end": v(-62.34, -44.01) * mm});
            skLineSegment(sketch, "E2687", {"start": v(-62.34, -44.01) * mm, "end": v(-62.3, -43.99) * mm});
            skLineSegment(sketch, "E2688", {"start": v(-62.3, -43.99) * mm, "end": v(-61.87, -43.99) * mm});
            skLineSegment(sketch, "E2689", {"start": v(-61.87, -43.99) * mm, "end": v(-61.83, -44.01) * mm});
            skLineSegment(sketch, "E2690", {"start": v(-61.83, -44.01) * mm, "end": v(-61.8, -44.03) * mm});
            skLineSegment(sketch, "E2691", {"start": v(-61.8, -44.03) * mm, "end": v(-61.58, -44.35) * mm});
            skLineSegment(sketch, "E2692", {"start": v(-61.58, -44.35) * mm, "end": v(-61.58, -44.45) * mm});
            skLineSegment(sketch, "E2693", {"start": v(-59.04, -44.45) * mm, "end": v(-59.04, -44.56) * mm});
            skLineSegment(sketch, "E2694", {"start": v(-59.04, -44.56) * mm, "end": v(-59.26, -44.87) * mm});
            skLineSegment(sketch, "E2695", {"start": v(-59.26, -44.87) * mm, "end": v(-59.3, -44.89) * mm});
            skLineSegment(sketch, "E2696", {"start": v(-59.3, -44.89) * mm, "end": v(-59.33, -44.91) * mm});
            skLineSegment(sketch, "E2697", {"start": v(-59.33, -44.91) * mm, "end": v(-59.76, -44.91) * mm});
            skLineSegment(sketch, "E2698", {"start": v(-59.76, -44.91) * mm, "end": v(-59.8, -44.89) * mm});
            skLineSegment(sketch, "E2699", {"start": v(-59.8, -44.89) * mm, "end": v(-59.84, -44.87) * mm});
            skLineSegment(sketch, "E2700", {"start": v(-59.84, -44.87) * mm, "end": v(-60.06, -44.55) * mm});
            skLineSegment(sketch, "E2701", {"start": v(-60.06, -44.55) * mm, "end": v(-60.06, -44.45) * mm});
            skLineSegment(sketch, "E2702", {"start": v(-60.06, -44.45) * mm, "end": v(-60.06, -44.34) * mm});
            skLineSegment(sketch, "E2703", {"start": v(-60.06, -44.34) * mm, "end": v(-59.84, -44.03) * mm});
            skLineSegment(sketch, "E2704", {"start": v(-59.84, -44.03) * mm, "end": v(-59.8, -44.01) * mm});
            skLineSegment(sketch, "E2705", {"start": v(-59.8, -44.01) * mm, "end": v(-59.76, -43.99) * mm});
            skLineSegment(sketch, "E2706", {"start": v(-59.76, -43.99) * mm, "end": v(-59.33, -43.99) * mm});
            skLineSegment(sketch, "E2707", {"start": v(-59.33, -43.99) * mm, "end": v(-59.3, -44.01) * mm});
            skLineSegment(sketch, "E2708", {"start": v(-59.3, -44.01) * mm, "end": v(-59.26, -44.03) * mm});
            skLineSegment(sketch, "E2709", {"start": v(-59.26, -44.03) * mm, "end": v(-59.04, -44.35) * mm});
            skLineSegment(sketch, "E2710", {"start": v(-59.04, -44.35) * mm, "end": v(-59.04, -44.45) * mm});
            skLineSegment(sketch, "E2711", {"start": v(-61.58, -46.99) * mm, "end": v(-61.58, -47.1) * mm});
            skLineSegment(sketch, "E2712", {"start": v(-61.58, -47.1) * mm, "end": v(-61.8, -47.4) * mm});
            skLineSegment(sketch, "E2713", {"start": v(-61.8, -47.4) * mm, "end": v(-61.83, -47.43) * mm});
            skLineSegment(sketch, "E2714", {"start": v(-61.83, -47.43) * mm, "end": v(-61.87, -47.45) * mm});
            skLineSegment(sketch, "E2715", {"start": v(-61.87, -47.45) * mm, "end": v(-62.3, -47.45) * mm});
            skLineSegment(sketch, "E2716", {"start": v(-62.3, -47.45) * mm, "end": v(-62.34, -47.43) * mm});
            skLineSegment(sketch, "E2717", {"start": v(-62.34, -47.43) * mm, "end": v(-62.38, -47.4) * mm});
            skLineSegment(sketch, "E2718", {"start": v(-62.38, -47.4) * mm, "end": v(-62.6, -47.1) * mm});
            skLineSegment(sketch, "E2719", {"start": v(-62.6, -47.1) * mm, "end": v(-62.6, -46.99) * mm});
            skLineSegment(sketch, "E2720", {"start": v(-62.6, -46.99) * mm, "end": v(-62.6, -46.88) * mm});
            skLineSegment(sketch, "E2721", {"start": v(-62.6, -46.88) * mm, "end": v(-62.38, -46.57) * mm});
            skLineSegment(sketch, "E2722", {"start": v(-62.38, -46.57) * mm, "end": v(-62.34, -46.55) * mm});
            skLineSegment(sketch, "E2723", {"start": v(-62.34, -46.55) * mm, "end": v(-62.3, -46.53) * mm});
            skLineSegment(sketch, "E2724", {"start": v(-62.3, -46.53) * mm, "end": v(-61.87, -46.53) * mm});
            skLineSegment(sketch, "E2725", {"start": v(-61.87, -46.53) * mm, "end": v(-61.83, -46.55) * mm});
            skLineSegment(sketch, "E2726", {"start": v(-61.83, -46.55) * mm, "end": v(-61.8, -46.57) * mm});
            skLineSegment(sketch, "E2727", {"start": v(-61.8, -46.57) * mm, "end": v(-61.58, -46.88) * mm});
            skLineSegment(sketch, "E2728", {"start": v(-61.58, -46.88) * mm, "end": v(-61.58, -46.99) * mm});
            skLineSegment(sketch, "E2729", {"start": v(-59.04, -46.99) * mm, "end": v(-59.04, -47.1) * mm});
            skLineSegment(sketch, "E2730", {"start": v(-59.04, -47.1) * mm, "end": v(-59.26, -47.4) * mm});
            skLineSegment(sketch, "E2731", {"start": v(-59.26, -47.4) * mm, "end": v(-59.3, -47.43) * mm});
            skLineSegment(sketch, "E2732", {"start": v(-59.3, -47.43) * mm, "end": v(-59.33, -47.45) * mm});
            skLineSegment(sketch, "E2733", {"start": v(-59.33, -47.45) * mm, "end": v(-59.76, -47.45) * mm});
            skLineSegment(sketch, "E2734", {"start": v(-59.76, -47.45) * mm, "end": v(-59.8, -47.43) * mm});
            skLineSegment(sketch, "E2735", {"start": v(-59.8, -47.43) * mm, "end": v(-59.84, -47.4) * mm});
            skLineSegment(sketch, "E2736", {"start": v(-59.84, -47.4) * mm, "end": v(-60.06, -47.1) * mm});
            skLineSegment(sketch, "E2737", {"start": v(-60.06, -47.1) * mm, "end": v(-60.06, -46.99) * mm});
            skLineSegment(sketch, "E2738", {"start": v(-60.06, -46.99) * mm, "end": v(-60.06, -46.88) * mm});
            skLineSegment(sketch, "E2739", {"start": v(-60.06, -46.88) * mm, "end": v(-59.84, -46.57) * mm});
            skLineSegment(sketch, "E2740", {"start": v(-59.84, -46.57) * mm, "end": v(-59.8, -46.55) * mm});
            skLineSegment(sketch, "E2741", {"start": v(-59.8, -46.55) * mm, "end": v(-59.76, -46.53) * mm});
            skLineSegment(sketch, "E2742", {"start": v(-59.76, -46.53) * mm, "end": v(-59.33, -46.53) * mm});
            skLineSegment(sketch, "E2743", {"start": v(-59.33, -46.53) * mm, "end": v(-59.3, -46.55) * mm});
            skLineSegment(sketch, "E2744", {"start": v(-59.3, -46.55) * mm, "end": v(-59.26, -46.57) * mm});
            skLineSegment(sketch, "E2745", {"start": v(-59.26, -46.57) * mm, "end": v(-59.04, -46.88) * mm});
            skLineSegment(sketch, "E2746", {"start": v(-59.04, -46.88) * mm, "end": v(-59.04, -46.99) * mm});
            skLineSegment(sketch, "E2747", {"start": v(-61.58, -49.53) * mm, "end": v(-61.58, -49.64) * mm});
            skLineSegment(sketch, "E2748", {"start": v(-61.58, -49.64) * mm, "end": v(-61.8, -49.95) * mm});
            skLineSegment(sketch, "E2749", {"start": v(-61.8, -49.95) * mm, "end": v(-61.83, -49.97) * mm});
            skLineSegment(sketch, "E2750", {"start": v(-61.83, -49.97) * mm, "end": v(-61.87, -50) * mm});
            skLineSegment(sketch, "E2751", {"start": v(-61.87, -50) * mm, "end": v(-62.3, -50) * mm});
            skLineSegment(sketch, "E2752", {"start": v(-62.3, -50) * mm, "end": v(-62.34, -49.97) * mm});
            skLineSegment(sketch, "E2753", {"start": v(-62.34, -49.97) * mm, "end": v(-62.38, -49.95) * mm});
            skLineSegment(sketch, "E2754", {"start": v(-62.38, -49.95) * mm, "end": v(-62.6, -49.63) * mm});
            skLineSegment(sketch, "E2755", {"start": v(-62.6, -49.63) * mm, "end": v(-62.6, -49.53) * mm});
            skLineSegment(sketch, "E2756", {"start": v(-62.6, -49.53) * mm, "end": v(-62.6, -49.42) * mm});
            skLineSegment(sketch, "E2757", {"start": v(-62.6, -49.42) * mm, "end": v(-62.38, -49.11) * mm});
            skLineSegment(sketch, "E2758", {"start": v(-62.38, -49.11) * mm, "end": v(-62.34, -49.09) * mm});
            skLineSegment(sketch, "E2759", {"start": v(-62.34, -49.09) * mm, "end": v(-62.3, -49.07) * mm});
            skLineSegment(sketch, "E2760", {"start": v(-62.3, -49.07) * mm, "end": v(-61.87, -49.07) * mm});
            skLineSegment(sketch, "E2761", {"start": v(-61.87, -49.07) * mm, "end": v(-61.83, -49.09) * mm});
            skLineSegment(sketch, "E2762", {"start": v(-61.83, -49.09) * mm, "end": v(-61.8, -49.11) * mm});
            skLineSegment(sketch, "E2763", {"start": v(-61.8, -49.11) * mm, "end": v(-61.58, -49.42) * mm});
            skLineSegment(sketch, "E2764", {"start": v(-61.58, -49.42) * mm, "end": v(-61.58, -49.53) * mm});
            skLineSegment(sketch, "E2765", {"start": v(-59.04, -49.53) * mm, "end": v(-59.04, -49.64) * mm});
            skLineSegment(sketch, "E2766", {"start": v(-59.04, -49.64) * mm, "end": v(-59.26, -49.95) * mm});
            skLineSegment(sketch, "E2767", {"start": v(-59.26, -49.95) * mm, "end": v(-59.3, -49.97) * mm});
            skLineSegment(sketch, "E2768", {"start": v(-59.3, -49.97) * mm, "end": v(-59.33, -50) * mm});
            skLineSegment(sketch, "E2769", {"start": v(-59.33, -50) * mm, "end": v(-59.76, -50) * mm});
            skLineSegment(sketch, "E2770", {"start": v(-59.76, -50) * mm, "end": v(-59.8, -49.97) * mm});
            skLineSegment(sketch, "E2771", {"start": v(-59.8, -49.97) * mm, "end": v(-59.84, -49.95) * mm});
            skLineSegment(sketch, "E2772", {"start": v(-59.84, -49.95) * mm, "end": v(-60.06, -49.63) * mm});
            skLineSegment(sketch, "E2773", {"start": v(-60.06, -49.63) * mm, "end": v(-60.06, -49.53) * mm});
            skLineSegment(sketch, "E2774", {"start": v(-60.06, -49.53) * mm, "end": v(-60.06, -49.42) * mm});
            skLineSegment(sketch, "E2775", {"start": v(-60.06, -49.42) * mm, "end": v(-59.84, -49.11) * mm});
            skLineSegment(sketch, "E2776", {"start": v(-59.84, -49.11) * mm, "end": v(-59.8, -49.09) * mm});
            skLineSegment(sketch, "E2777", {"start": v(-59.8, -49.09) * mm, "end": v(-59.76, -49.07) * mm});
            skLineSegment(sketch, "E2778", {"start": v(-59.76, -49.07) * mm, "end": v(-59.33, -49.07) * mm});
            skLineSegment(sketch, "E2779", {"start": v(-59.33, -49.07) * mm, "end": v(-59.3, -49.09) * mm});
            skLineSegment(sketch, "E2780", {"start": v(-59.3, -49.09) * mm, "end": v(-59.26, -49.11) * mm});
            skLineSegment(sketch, "E2781", {"start": v(-59.26, -49.11) * mm, "end": v(-59.04, -49.42) * mm});
            skLineSegment(sketch, "E2782", {"start": v(-59.04, -49.42) * mm, "end": v(-59.04, -49.53) * mm});
            skLineSegment(sketch, "E2783", {"start": v(-61.58, -52.07) * mm, "end": v(-61.58, -52.18) * mm});
            skLineSegment(sketch, "E2784", {"start": v(-61.58, -52.18) * mm, "end": v(-61.8, -52.49) * mm});
            skLineSegment(sketch, "E2785", {"start": v(-61.8, -52.49) * mm, "end": v(-61.83, -52.51) * mm});
            skLineSegment(sketch, "E2786", {"start": v(-61.83, -52.51) * mm, "end": v(-61.87, -52.53) * mm});
            skLineSegment(sketch, "E2787", {"start": v(-61.87, -52.53) * mm, "end": v(-62.3, -52.53) * mm});
            skLineSegment(sketch, "E2788", {"start": v(-62.3, -52.53) * mm, "end": v(-62.34, -52.51) * mm});
            skLineSegment(sketch, "E2789", {"start": v(-62.34, -52.51) * mm, "end": v(-62.38, -52.49) * mm});
            skLineSegment(sketch, "E2790", {"start": v(-62.38, -52.49) * mm, "end": v(-62.6, -52.17) * mm});
            skLineSegment(sketch, "E2791", {"start": v(-62.6, -52.17) * mm, "end": v(-62.6, -52.07) * mm});
            skLineSegment(sketch, "E2792", {"start": v(-62.6, -52.07) * mm, "end": v(-62.6, -51.96) * mm});
            skLineSegment(sketch, "E2793", {"start": v(-62.6, -51.96) * mm, "end": v(-62.38, -51.65) * mm});
            skLineSegment(sketch, "E2794", {"start": v(-62.38, -51.65) * mm, "end": v(-62.34, -51.63) * mm});
            skLineSegment(sketch, "E2795", {"start": v(-62.34, -51.63) * mm, "end": v(-62.3, -51.6) * mm});
            skLineSegment(sketch, "E2796", {"start": v(-62.3, -51.6) * mm, "end": v(-61.87, -51.6) * mm});
            skLineSegment(sketch, "E2797", {"start": v(-61.87, -51.6) * mm, "end": v(-61.83, -51.63) * mm});
            skLineSegment(sketch, "E2798", {"start": v(-61.83, -51.63) * mm, "end": v(-61.8, -51.65) * mm});
            skLineSegment(sketch, "E2799", {"start": v(-61.8, -51.65) * mm, "end": v(-61.58, -51.97) * mm});
            skLineSegment(sketch, "E2800", {"start": v(-61.58, -51.97) * mm, "end": v(-61.58, -52.07) * mm});
            skLineSegment(sketch, "E2801", {"start": v(-59.04, -52.07) * mm, "end": v(-59.04, -52.18) * mm});
            skLineSegment(sketch, "E2802", {"start": v(-59.04, -52.18) * mm, "end": v(-59.26, -52.49) * mm});
            skLineSegment(sketch, "E2803", {"start": v(-59.26, -52.49) * mm, "end": v(-59.3, -52.51) * mm});
            skLineSegment(sketch, "E2804", {"start": v(-59.3, -52.51) * mm, "end": v(-59.33, -52.53) * mm});
            skLineSegment(sketch, "E2805", {"start": v(-59.33, -52.53) * mm, "end": v(-59.76, -52.53) * mm});
            skLineSegment(sketch, "E2806", {"start": v(-59.76, -52.53) * mm, "end": v(-59.8, -52.51) * mm});
            skLineSegment(sketch, "E2807", {"start": v(-59.8, -52.51) * mm, "end": v(-59.84, -52.49) * mm});
            skLineSegment(sketch, "E2808", {"start": v(-59.84, -52.49) * mm, "end": v(-60.06, -52.17) * mm});
            skLineSegment(sketch, "E2809", {"start": v(-60.06, -52.17) * mm, "end": v(-60.06, -52.07) * mm});
            skLineSegment(sketch, "E2810", {"start": v(-60.06, -52.07) * mm, "end": v(-60.06, -51.96) * mm});
            skLineSegment(sketch, "E2811", {"start": v(-60.06, -51.96) * mm, "end": v(-59.84, -51.65) * mm});
            skLineSegment(sketch, "E2812", {"start": v(-59.84, -51.65) * mm, "end": v(-59.8, -51.63) * mm});
            skLineSegment(sketch, "E2813", {"start": v(-59.8, -51.63) * mm, "end": v(-59.76, -51.6) * mm});
            skLineSegment(sketch, "E2814", {"start": v(-59.76, -51.6) * mm, "end": v(-59.33, -51.6) * mm});
            skLineSegment(sketch, "E2815", {"start": v(-59.33, -51.6) * mm, "end": v(-59.3, -51.63) * mm});
            skLineSegment(sketch, "E2816", {"start": v(-59.3, -51.63) * mm, "end": v(-59.26, -51.65) * mm});
            skLineSegment(sketch, "E2817", {"start": v(-59.26, -51.65) * mm, "end": v(-59.04, -51.97) * mm});
            skLineSegment(sketch, "E2818", {"start": v(-59.04, -51.97) * mm, "end": v(-59.04, -52.07) * mm});
            skLineSegment(sketch, "E2819", {"start": v(-61.58, -54.61) * mm, "end": v(-61.58, -54.72) * mm});
            skLineSegment(sketch, "E2820", {"start": v(-61.58, -54.72) * mm, "end": v(-61.8, -55.03) * mm});
            skLineSegment(sketch, "E2821", {"start": v(-61.8, -55.03) * mm, "end": v(-61.83, -55.05) * mm});
            skLineSegment(sketch, "E2822", {"start": v(-61.83, -55.05) * mm, "end": v(-61.87, -55.07) * mm});
            skLineSegment(sketch, "E2823", {"start": v(-61.87, -55.07) * mm, "end": v(-62.3, -55.07) * mm});
            skLineSegment(sketch, "E2824", {"start": v(-62.3, -55.07) * mm, "end": v(-62.34, -55.05) * mm});
            skLineSegment(sketch, "E2825", {"start": v(-62.34, -55.05) * mm, "end": v(-62.38, -55.03) * mm});
            skLineSegment(sketch, "E2826", {"start": v(-62.38, -55.03) * mm, "end": v(-62.6, -54.71) * mm});
            skLineSegment(sketch, "E2827", {"start": v(-62.6, -54.71) * mm, "end": v(-62.6, -54.61) * mm});
            skLineSegment(sketch, "E2828", {"start": v(-62.6, -54.61) * mm, "end": v(-62.6, -54.5) * mm});
            skLineSegment(sketch, "E2829", {"start": v(-62.6, -54.5) * mm, "end": v(-62.38, -54.2) * mm});
            skLineSegment(sketch, "E2830", {"start": v(-62.38, -54.2) * mm, "end": v(-62.34, -54.17) * mm});
            skLineSegment(sketch, "E2831", {"start": v(-62.34, -54.17) * mm, "end": v(-62.3, -54.15) * mm});
            skLineSegment(sketch, "E2832", {"start": v(-62.3, -54.15) * mm, "end": v(-61.87, -54.15) * mm});
            skLineSegment(sketch, "E2833", {"start": v(-61.87, -54.15) * mm, "end": v(-61.83, -54.17) * mm});
            skLineSegment(sketch, "E2834", {"start": v(-61.83, -54.17) * mm, "end": v(-61.8, -54.2) * mm});
            skLineSegment(sketch, "E2835", {"start": v(-61.8, -54.2) * mm, "end": v(-61.58, -54.5) * mm});
            skLineSegment(sketch, "E2836", {"start": v(-61.58, -54.5) * mm, "end": v(-61.58, -54.61) * mm});
            skLineSegment(sketch, "E2837", {"start": v(-59.04, -54.61) * mm, "end": v(-59.04, -54.72) * mm});
            skLineSegment(sketch, "E2838", {"start": v(-59.04, -54.72) * mm, "end": v(-59.26, -55.03) * mm});
            skLineSegment(sketch, "E2839", {"start": v(-59.26, -55.03) * mm, "end": v(-59.3, -55.05) * mm});
            skLineSegment(sketch, "E2840", {"start": v(-59.3, -55.05) * mm, "end": v(-59.33, -55.07) * mm});
            skLineSegment(sketch, "E2841", {"start": v(-59.33, -55.07) * mm, "end": v(-59.76, -55.07) * mm});
            skLineSegment(sketch, "E2842", {"start": v(-59.76, -55.07) * mm, "end": v(-59.8, -55.05) * mm});
            skLineSegment(sketch, "E2843", {"start": v(-59.8, -55.05) * mm, "end": v(-59.84, -55.03) * mm});
            skLineSegment(sketch, "E2844", {"start": v(-59.84, -55.03) * mm, "end": v(-60.06, -54.71) * mm});
            skLineSegment(sketch, "E2845", {"start": v(-60.06, -54.71) * mm, "end": v(-60.06, -54.61) * mm});
            skLineSegment(sketch, "E2846", {"start": v(-60.06, -54.61) * mm, "end": v(-60.06, -54.5) * mm});
            skLineSegment(sketch, "E2847", {"start": v(-60.06, -54.5) * mm, "end": v(-59.84, -54.2) * mm});
            skLineSegment(sketch, "E2848", {"start": v(-59.84, -54.2) * mm, "end": v(-59.8, -54.17) * mm});
            skLineSegment(sketch, "E2849", {"start": v(-59.8, -54.17) * mm, "end": v(-59.76, -54.15) * mm});
            skLineSegment(sketch, "E2850", {"start": v(-59.76, -54.15) * mm, "end": v(-59.33, -54.15) * mm});
            skLineSegment(sketch, "E2851", {"start": v(-59.33, -54.15) * mm, "end": v(-59.3, -54.17) * mm});
            skLineSegment(sketch, "E2852", {"start": v(-59.3, -54.17) * mm, "end": v(-59.26, -54.2) * mm});
            skLineSegment(sketch, "E2853", {"start": v(-59.26, -54.2) * mm, "end": v(-59.04, -54.5) * mm});
            skLineSegment(sketch, "E2854", {"start": v(-59.04, -54.5) * mm, "end": v(-59.04, -54.61) * mm});
            skLineSegment(sketch, "E2855", {"start": v(-61.58, -57.15) * mm, "end": v(-61.58, -57.26) * mm});
            skLineSegment(sketch, "E2856", {"start": v(-61.58, -57.26) * mm, "end": v(-61.8, -57.57) * mm});
            skLineSegment(sketch, "E2857", {"start": v(-61.8, -57.57) * mm, "end": v(-61.83, -57.59) * mm});
            skLineSegment(sketch, "E2858", {"start": v(-61.83, -57.59) * mm, "end": v(-61.87, -57.61) * mm});
            skLineSegment(sketch, "E2859", {"start": v(-61.87, -57.61) * mm, "end": v(-62.3, -57.61) * mm});
            skLineSegment(sketch, "E2860", {"start": v(-62.3, -57.61) * mm, "end": v(-62.34, -57.59) * mm});
            skLineSegment(sketch, "E2861", {"start": v(-62.34, -57.59) * mm, "end": v(-62.38, -57.57) * mm});
            skLineSegment(sketch, "E2862", {"start": v(-62.38, -57.57) * mm, "end": v(-62.6, -57.25) * mm});
            skLineSegment(sketch, "E2863", {"start": v(-62.6, -57.25) * mm, "end": v(-62.6, -57.15) * mm});
            skLineSegment(sketch, "E2864", {"start": v(-62.6, -57.15) * mm, "end": v(-62.6, -57.04) * mm});
            skLineSegment(sketch, "E2865", {"start": v(-62.6, -57.04) * mm, "end": v(-62.38, -56.73) * mm});
            skLineSegment(sketch, "E2866", {"start": v(-62.38, -56.73) * mm, "end": v(-62.34, -56.71) * mm});
            skLineSegment(sketch, "E2867", {"start": v(-62.34, -56.71) * mm, "end": v(-62.3, -56.69) * mm});
            skLineSegment(sketch, "E2868", {"start": v(-62.3, -56.69) * mm, "end": v(-61.87, -56.69) * mm});
            skLineSegment(sketch, "E2869", {"start": v(-61.87, -56.69) * mm, "end": v(-61.83, -56.71) * mm});
            skLineSegment(sketch, "E2870", {"start": v(-61.83, -56.71) * mm, "end": v(-61.8, -56.73) * mm});
            skLineSegment(sketch, "E2871", {"start": v(-61.8, -56.73) * mm, "end": v(-61.58, -57.05) * mm});
            skLineSegment(sketch, "E2872", {"start": v(-61.58, -57.05) * mm, "end": v(-61.58, -57.15) * mm});
            skLineSegment(sketch, "E2873", {"start": v(-59.04, -57.15) * mm, "end": v(-59.04, -57.26) * mm});
            skLineSegment(sketch, "E2874", {"start": v(-59.04, -57.26) * mm, "end": v(-59.26, -57.57) * mm});
            skLineSegment(sketch, "E2875", {"start": v(-59.26, -57.57) * mm, "end": v(-59.3, -57.59) * mm});
            skLineSegment(sketch, "E2876", {"start": v(-59.3, -57.59) * mm, "end": v(-59.33, -57.61) * mm});
            skLineSegment(sketch, "E2877", {"start": v(-59.33, -57.61) * mm, "end": v(-59.76, -57.61) * mm});
            skLineSegment(sketch, "E2878", {"start": v(-59.76, -57.61) * mm, "end": v(-59.8, -57.59) * mm});
            skLineSegment(sketch, "E2879", {"start": v(-59.8, -57.59) * mm, "end": v(-59.84, -57.57) * mm});
            skLineSegment(sketch, "E2880", {"start": v(-59.84, -57.57) * mm, "end": v(-60.06, -57.25) * mm});
            skLineSegment(sketch, "E2881", {"start": v(-60.06, -57.25) * mm, "end": v(-60.06, -57.15) * mm});
            skLineSegment(sketch, "E2882", {"start": v(-60.06, -57.15) * mm, "end": v(-60.06, -57.04) * mm});
            skLineSegment(sketch, "E2883", {"start": v(-60.06, -57.04) * mm, "end": v(-59.84, -56.73) * mm});
            skLineSegment(sketch, "E2884", {"start": v(-59.84, -56.73) * mm, "end": v(-59.8, -56.71) * mm});
            skLineSegment(sketch, "E2885", {"start": v(-59.8, -56.71) * mm, "end": v(-59.76, -56.69) * mm});
            skLineSegment(sketch, "E2886", {"start": v(-59.76, -56.69) * mm, "end": v(-59.33, -56.69) * mm});
            skLineSegment(sketch, "E2887", {"start": v(-59.33, -56.69) * mm, "end": v(-59.3, -56.71) * mm});
            skLineSegment(sketch, "E2888", {"start": v(-59.3, -56.71) * mm, "end": v(-59.26, -56.73) * mm});
            skLineSegment(sketch, "E2889", {"start": v(-59.26, -56.73) * mm, "end": v(-59.04, -57.05) * mm});
            skLineSegment(sketch, "E2890", {"start": v(-59.04, -57.05) * mm, "end": v(-59.04, -57.15) * mm});
            skLineSegment(sketch, "E2891", {"start": v(-61.58, -59.69) * mm, "end": v(-61.58, -59.8) * mm});
            skLineSegment(sketch, "E2892", {"start": v(-61.58, -59.8) * mm, "end": v(-61.8, -60.1) * mm});
            skLineSegment(sketch, "E2893", {"start": v(-61.8, -60.1) * mm, "end": v(-61.83, -60.13) * mm});
            skLineSegment(sketch, "E2894", {"start": v(-61.83, -60.13) * mm, "end": v(-61.87, -60.15) * mm});
            skLineSegment(sketch, "E2895", {"start": v(-61.87, -60.15) * mm, "end": v(-62.3, -60.15) * mm});
            skLineSegment(sketch, "E2896", {"start": v(-62.3, -60.15) * mm, "end": v(-62.34, -60.13) * mm});
            skLineSegment(sketch, "E2897", {"start": v(-62.34, -60.13) * mm, "end": v(-62.38, -60.1) * mm});
            skLineSegment(sketch, "E2898", {"start": v(-62.38, -60.1) * mm, "end": v(-62.6, -59.8) * mm});
            skLineSegment(sketch, "E2899", {"start": v(-62.6, -59.8) * mm, "end": v(-62.6, -59.69) * mm});
            skLineSegment(sketch, "E2900", {"start": v(-62.6, -59.69) * mm, "end": v(-62.6, -59.58) * mm});
            skLineSegment(sketch, "E2901", {"start": v(-62.6, -59.58) * mm, "end": v(-62.38, -59.27) * mm});
            skLineSegment(sketch, "E2902", {"start": v(-62.38, -59.27) * mm, "end": v(-62.34, -59.25) * mm});
            skLineSegment(sketch, "E2903", {"start": v(-62.34, -59.25) * mm, "end": v(-62.3, -59.23) * mm});
            skLineSegment(sketch, "E2904", {"start": v(-62.3, -59.23) * mm, "end": v(-61.87, -59.23) * mm});
            skLineSegment(sketch, "E2905", {"start": v(-61.87, -59.23) * mm, "end": v(-61.83, -59.25) * mm});
            skLineSegment(sketch, "E2906", {"start": v(-61.83, -59.25) * mm, "end": v(-61.8, -59.27) * mm});
            skLineSegment(sketch, "E2907", {"start": v(-61.8, -59.27) * mm, "end": v(-61.58, -59.58) * mm});
            skLineSegment(sketch, "E2908", {"start": v(-61.58, -59.58) * mm, "end": v(-61.58, -59.69) * mm});
            skLineSegment(sketch, "E2909", {"start": v(-59.04, -59.69) * mm, "end": v(-59.04, -59.8) * mm});
            skLineSegment(sketch, "E2910", {"start": v(-59.04, -59.8) * mm, "end": v(-59.26, -60.1) * mm});
            skLineSegment(sketch, "E2911", {"start": v(-59.26, -60.1) * mm, "end": v(-59.3, -60.13) * mm});
            skLineSegment(sketch, "E2912", {"start": v(-59.3, -60.13) * mm, "end": v(-59.33, -60.15) * mm});
            skLineSegment(sketch, "E2913", {"start": v(-59.33, -60.15) * mm, "end": v(-59.76, -60.15) * mm});
            skLineSegment(sketch, "E2914", {"start": v(-59.76, -60.15) * mm, "end": v(-59.8, -60.13) * mm});
            skLineSegment(sketch, "E2915", {"start": v(-59.8, -60.13) * mm, "end": v(-59.84, -60.1) * mm});
            skLineSegment(sketch, "E2916", {"start": v(-59.84, -60.1) * mm, "end": v(-60.06, -59.8) * mm});
            skLineSegment(sketch, "E2917", {"start": v(-60.06, -59.8) * mm, "end": v(-60.06, -59.69) * mm});
            skLineSegment(sketch, "E2918", {"start": v(-60.06, -59.69) * mm, "end": v(-60.06, -59.58) * mm});
            skLineSegment(sketch, "E2919", {"start": v(-60.06, -59.58) * mm, "end": v(-59.84, -59.27) * mm});
            skLineSegment(sketch, "E2920", {"start": v(-59.84, -59.27) * mm, "end": v(-59.8, -59.25) * mm});
            skLineSegment(sketch, "E2921", {"start": v(-59.8, -59.25) * mm, "end": v(-59.76, -59.23) * mm});
            skLineSegment(sketch, "E2922", {"start": v(-59.76, -59.23) * mm, "end": v(-59.33, -59.23) * mm});
            skLineSegment(sketch, "E2923", {"start": v(-59.33, -59.23) * mm, "end": v(-59.3, -59.25) * mm});
            skLineSegment(sketch, "E2924", {"start": v(-59.3, -59.25) * mm, "end": v(-59.26, -59.27) * mm});
            skLineSegment(sketch, "E2925", {"start": v(-59.26, -59.27) * mm, "end": v(-59.04, -59.58) * mm});
            skLineSegment(sketch, "E2926", {"start": v(-59.04, -59.58) * mm, "end": v(-59.04, -59.69) * mm});
            skLineSegment(sketch, "E2927", {"start": v(-61.58, -62.23) * mm, "end": v(-61.58, -62.34) * mm});
            skLineSegment(sketch, "E2928", {"start": v(-61.58, -62.34) * mm, "end": v(-61.8, -62.65) * mm});
            skLineSegment(sketch, "E2929", {"start": v(-61.8, -62.65) * mm, "end": v(-61.83, -62.67) * mm});
            skLineSegment(sketch, "E2930", {"start": v(-61.83, -62.67) * mm, "end": v(-61.87, -62.7) * mm});
            skLineSegment(sketch, "E2931", {"start": v(-61.87, -62.7) * mm, "end": v(-62.3, -62.7) * mm});
            skLineSegment(sketch, "E2932", {"start": v(-62.3, -62.7) * mm, "end": v(-62.34, -62.67) * mm});
            skLineSegment(sketch, "E2933", {"start": v(-62.34, -62.67) * mm, "end": v(-62.38, -62.65) * mm});
            skLineSegment(sketch, "E2934", {"start": v(-62.38, -62.65) * mm, "end": v(-62.6, -62.33) * mm});
            skLineSegment(sketch, "E2935", {"start": v(-62.6, -62.33) * mm, "end": v(-62.6, -62.23) * mm});
            skLineSegment(sketch, "E2936", {"start": v(-62.6, -62.23) * mm, "end": v(-62.6, -62.12) * mm});
            skLineSegment(sketch, "E2937", {"start": v(-62.6, -62.12) * mm, "end": v(-62.38, -61.81) * mm});
            skLineSegment(sketch, "E2938", {"start": v(-62.38, -61.81) * mm, "end": v(-62.34, -61.79) * mm});
            skLineSegment(sketch, "E2939", {"start": v(-62.34, -61.79) * mm, "end": v(-62.3, -61.77) * mm});
            skLineSegment(sketch, "E2940", {"start": v(-62.3, -61.77) * mm, "end": v(-61.87, -61.77) * mm});
            skLineSegment(sketch, "E2941", {"start": v(-61.87, -61.77) * mm, "end": v(-61.83, -61.79) * mm});
            skLineSegment(sketch, "E2942", {"start": v(-61.83, -61.79) * mm, "end": v(-61.8, -61.81) * mm});
            skLineSegment(sketch, "E2943", {"start": v(-61.8, -61.81) * mm, "end": v(-61.58, -62.12) * mm});
            skLineSegment(sketch, "E2944", {"start": v(-61.58, -62.12) * mm, "end": v(-61.58, -62.23) * mm});
            skLineSegment(sketch, "E2945", {"start": v(-59.04, -62.23) * mm, "end": v(-59.04, -62.34) * mm});
            skLineSegment(sketch, "E2946", {"start": v(-59.04, -62.34) * mm, "end": v(-59.26, -62.65) * mm});
            skLineSegment(sketch, "E2947", {"start": v(-59.26, -62.65) * mm, "end": v(-59.3, -62.67) * mm});
            skLineSegment(sketch, "E2948", {"start": v(-59.3, -62.67) * mm, "end": v(-59.33, -62.7) * mm});
            skLineSegment(sketch, "E2949", {"start": v(-59.33, -62.7) * mm, "end": v(-59.76, -62.7) * mm});
            skLineSegment(sketch, "E2950", {"start": v(-59.76, -62.7) * mm, "end": v(-59.8, -62.67) * mm});
            skLineSegment(sketch, "E2951", {"start": v(-59.8, -62.67) * mm, "end": v(-59.84, -62.65) * mm});
            skLineSegment(sketch, "E2952", {"start": v(-59.84, -62.65) * mm, "end": v(-60.06, -62.33) * mm});
            skLineSegment(sketch, "E2953", {"start": v(-60.06, -62.33) * mm, "end": v(-60.06, -62.23) * mm});
            skLineSegment(sketch, "E2954", {"start": v(-60.06, -62.23) * mm, "end": v(-60.06, -62.12) * mm});
            skLineSegment(sketch, "E2955", {"start": v(-60.06, -62.12) * mm, "end": v(-59.84, -61.81) * mm});
            skLineSegment(sketch, "E2956", {"start": v(-59.84, -61.81) * mm, "end": v(-59.8, -61.79) * mm});
            skLineSegment(sketch, "E2957", {"start": v(-59.8, -61.79) * mm, "end": v(-59.76, -61.77) * mm});
            skLineSegment(sketch, "E2958", {"start": v(-59.76, -61.77) * mm, "end": v(-59.33, -61.77) * mm});
            skLineSegment(sketch, "E2959", {"start": v(-59.33, -61.77) * mm, "end": v(-59.3, -61.79) * mm});
            skLineSegment(sketch, "E2960", {"start": v(-59.3, -61.79) * mm, "end": v(-59.26, -61.81) * mm});
            skLineSegment(sketch, "E2961", {"start": v(-59.26, -61.81) * mm, "end": v(-59.04, -62.12) * mm});
            skLineSegment(sketch, "E2962", {"start": v(-59.04, -62.12) * mm, "end": v(-59.04, -62.23) * mm});
            skLineSegment(sketch, "E2963", {"start": v(51.3, 40.66) * mm, "end": v(51.3, 40.52) * mm});
            skLineSegment(sketch, "E2964", {"start": v(51.3, 40.52) * mm, "end": v(51.16, 40.1) * mm});
            skLineSegment(sketch, "E2965", {"start": v(51.16, 40.1) * mm, "end": v(50.84, 39.75) * mm});
            skLineSegment(sketch, "E2966", {"start": v(50.84, 39.75) * mm, "end": v(50.75, 39.7) * mm});
            skLineSegment(sketch, "E2967", {"start": v(50.75, 39.7) * mm, "end": v(50.67, 39.66) * mm});
            skLineSegment(sketch, "E2968", {"start": v(50.67, 39.66) * mm, "end": v(50.2, 39.56) * mm});
            skLineSegment(sketch, "E2969", {"start": v(50.2, 39.56) * mm, "end": v(49.74, 39.66) * mm});
            skLineSegment(sketch, "E2970", {"start": v(49.74, 39.66) * mm, "end": v(49.65, 39.7) * mm});
            skLineSegment(sketch, "E2971", {"start": v(49.65, 39.7) * mm, "end": v(49.57, 39.75) * mm});
            skLineSegment(sketch, "E2972", {"start": v(49.57, 39.75) * mm, "end": v(49.25, 40.1) * mm});
            skLineSegment(sketch, "E2973", {"start": v(49.25, 40.1) * mm, "end": v(49.1, 40.52) * mm});
            skLineSegment(sketch, "E2974", {"start": v(49.1, 40.52) * mm, "end": v(49.1, 40.66) * mm});
            skLineSegment(sketch, "E2975", {"start": v(49.1, 40.66) * mm, "end": v(49.1, 40.8) * mm});
            skLineSegment(sketch, "E2976", {"start": v(49.1, 40.8) * mm, "end": v(49.25, 41.2) * mm});
            skLineSegment(sketch, "E2977", {"start": v(49.25, 41.2) * mm, "end": v(49.57, 41.56) * mm});
            skLineSegment(sketch, "E2978", {"start": v(49.57, 41.56) * mm, "end": v(49.65, 41.6) * mm});
            skLineSegment(sketch, "E2979", {"start": v(49.65, 41.6) * mm, "end": v(49.74, 41.66) * mm});
            skLineSegment(sketch, "E2980", {"start": v(49.74, 41.66) * mm, "end": v(50.2, 41.76) * mm});
            skLineSegment(sketch, "E2981", {"start": v(50.2, 41.76) * mm, "end": v(50.67, 41.66) * mm});
            skLineSegment(sketch, "E2982", {"start": v(50.67, 41.66) * mm, "end": v(50.75, 41.6) * mm});
            skLineSegment(sketch, "E2983", {"start": v(50.75, 41.6) * mm, "end": v(50.84, 41.56) * mm});
            skLineSegment(sketch, "E2984", {"start": v(50.84, 41.56) * mm, "end": v(51.16, 41.2) * mm});
            skLineSegment(sketch, "E2985", {"start": v(51.16, 41.2) * mm, "end": v(51.3, 40.8) * mm});
            skLineSegment(sketch, "E2986", {"start": v(51.3, 40.8) * mm, "end": v(51.3, 40.66) * mm});
            skLineSegment(sketch, "E2987", {"start": v(51.3, 30.46) * mm, "end": v(51.3, 30.32) * mm});
            skLineSegment(sketch, "E2988", {"start": v(51.3, 30.32) * mm, "end": v(51.16, 29.91) * mm});
            skLineSegment(sketch, "E2989", {"start": v(51.16, 29.91) * mm, "end": v(50.84, 29.56) * mm});
            skLineSegment(sketch, "E2990", {"start": v(50.84, 29.56) * mm, "end": v(50.75, 29.5) * mm});
            skLineSegment(sketch, "E2991", {"start": v(50.75, 29.5) * mm, "end": v(50.67, 29.46) * mm});
            skLineSegment(sketch, "E2992", {"start": v(50.67, 29.46) * mm, "end": v(50.2, 29.36) * mm});
            skLineSegment(sketch, "E2993", {"start": v(50.2, 29.36) * mm, "end": v(49.74, 29.46) * mm});
            skLineSegment(sketch, "E2994", {"start": v(49.74, 29.46) * mm, "end": v(49.65, 29.5) * mm});
            skLineSegment(sketch, "E2995", {"start": v(49.65, 29.5) * mm, "end": v(49.57, 29.56) * mm});
            skLineSegment(sketch, "E2996", {"start": v(49.57, 29.56) * mm, "end": v(49.25, 29.91) * mm});
            skLineSegment(sketch, "E2997", {"start": v(49.25, 29.91) * mm, "end": v(49.1, 30.32) * mm});
            skLineSegment(sketch, "E2998", {"start": v(49.1, 30.32) * mm, "end": v(49.1, 30.46) * mm});
            skLineSegment(sketch, "E2999", {"start": v(49.1, 30.46) * mm, "end": v(49.1, 30.6) * mm});
            skLineSegment(sketch, "E3000", {"start": v(49.1, 30.6) * mm, "end": v(49.25, 31) * mm});
            skLineSegment(sketch, "E3001", {"start": v(49.25, 31) * mm, "end": v(49.57, 31.36) * mm});
            skLineSegment(sketch, "E3002", {"start": v(49.57, 31.36) * mm, "end": v(49.65, 31.41) * mm});
            skLineSegment(sketch, "E3003", {"start": v(49.65, 31.41) * mm, "end": v(49.74, 31.46) * mm});
            skLineSegment(sketch, "E3004", {"start": v(49.74, 31.46) * mm, "end": v(50.2, 31.56) * mm});
            skLineSegment(sketch, "E3005", {"start": v(50.2, 31.56) * mm, "end": v(50.67, 31.46) * mm});
            skLineSegment(sketch, "E3006", {"start": v(50.67, 31.46) * mm, "end": v(50.75, 31.41) * mm});
            skLineSegment(sketch, "E3007", {"start": v(50.75, 31.41) * mm, "end": v(50.84, 31.36) * mm});
            skLineSegment(sketch, "E3008", {"start": v(50.84, 31.36) * mm, "end": v(51.16, 31) * mm});
            skLineSegment(sketch, "E3009", {"start": v(51.16, 31) * mm, "end": v(51.3, 30.6) * mm});
            skLineSegment(sketch, "E3010", {"start": v(51.3, 30.6) * mm, "end": v(51.3, 30.46) * mm});
            skLineSegment(sketch, "E3011", {"start": v(46.44, 35.56) * mm, "end": v(46.44, 35.45) * mm});
            skLineSegment(sketch, "E3012", {"start": v(46.44, 35.45) * mm, "end": v(46.23, 35.15) * mm});
            skLineSegment(sketch, "E3013", {"start": v(46.23, 35.15) * mm, "end": v(46.19, 35.13) * mm});
            skLineSegment(sketch, "E3014", {"start": v(46.19, 35.13) * mm, "end": v(46.15, 35.1) * mm});
            skLineSegment(sketch, "E3015", {"start": v(46.15, 35.1) * mm, "end": v(45.73, 35.1) * mm});
            skLineSegment(sketch, "E3016", {"start": v(45.73, 35.1) * mm, "end": v(45.69, 35.13) * mm});
            skLineSegment(sketch, "E3017", {"start": v(45.69, 35.13) * mm, "end": v(45.65, 35.15) * mm});
            skLineSegment(sketch, "E3018", {"start": v(45.65, 35.15) * mm, "end": v(45.44, 35.46) * mm});
            skLineSegment(sketch, "E3019", {"start": v(45.44, 35.46) * mm, "end": v(45.44, 35.56) * mm});
            skLineSegment(sketch, "E3020", {"start": v(45.44, 35.56) * mm, "end": v(45.44, 35.67) * mm});
            skLineSegment(sketch, "E3021", {"start": v(45.44, 35.67) * mm, "end": v(45.65, 35.97) * mm});
            skLineSegment(sketch, "E3022", {"start": v(45.65, 35.97) * mm, "end": v(45.69, 36) * mm});
            skLineSegment(sketch, "E3023", {"start": v(45.69, 36) * mm, "end": v(45.73, 36.02) * mm});
            skLineSegment(sketch, "E3024", {"start": v(45.73, 36.02) * mm, "end": v(46.15, 36.02) * mm});
            skLineSegment(sketch, "E3025", {"start": v(46.15, 36.02) * mm, "end": v(46.19, 36) * mm});
            skLineSegment(sketch, "E3026", {"start": v(46.19, 36) * mm, "end": v(46.23, 35.97) * mm});
            skLineSegment(sketch, "E3027", {"start": v(46.23, 35.97) * mm, "end": v(46.44, 35.66) * mm});
            skLineSegment(sketch, "E3028", {"start": v(46.44, 35.66) * mm, "end": v(46.44, 35.56) * mm});
            skLineSegment(sketch, "E3029", {"start": v(46.44, 38.06) * mm, "end": v(46.44, 37.95) * mm});
            skLineSegment(sketch, "E3030", {"start": v(46.44, 37.95) * mm, "end": v(46.23, 37.65) * mm});
            skLineSegment(sketch, "E3031", {"start": v(46.23, 37.65) * mm, "end": v(46.19, 37.63) * mm});
            skLineSegment(sketch, "E3032", {"start": v(46.19, 37.63) * mm, "end": v(46.15, 37.6) * mm});
            skLineSegment(sketch, "E3033", {"start": v(46.15, 37.6) * mm, "end": v(45.73, 37.6) * mm});
            skLineSegment(sketch, "E3034", {"start": v(45.73, 37.6) * mm, "end": v(45.69, 37.63) * mm});
            skLineSegment(sketch, "E3035", {"start": v(45.69, 37.63) * mm, "end": v(45.65, 37.65) * mm});
            skLineSegment(sketch, "E3036", {"start": v(45.65, 37.65) * mm, "end": v(45.44, 37.96) * mm});
            skLineSegment(sketch, "E3037", {"start": v(45.44, 37.96) * mm, "end": v(45.44, 38.06) * mm});
            skLineSegment(sketch, "E3038", {"start": v(45.44, 38.06) * mm, "end": v(45.44, 38.17) * mm});
            skLineSegment(sketch, "E3039", {"start": v(45.44, 38.17) * mm, "end": v(45.65, 38.47) * mm});
            skLineSegment(sketch, "E3040", {"start": v(45.65, 38.47) * mm, "end": v(45.69, 38.5) * mm});
            skLineSegment(sketch, "E3041", {"start": v(45.69, 38.5) * mm, "end": v(45.73, 38.52) * mm});
            skLineSegment(sketch, "E3042", {"start": v(45.73, 38.52) * mm, "end": v(46.15, 38.52) * mm});
            skLineSegment(sketch, "E3043", {"start": v(46.15, 38.52) * mm, "end": v(46.19, 38.5) * mm});
            skLineSegment(sketch, "E3044", {"start": v(46.19, 38.5) * mm, "end": v(46.23, 38.47) * mm});
            skLineSegment(sketch, "E3045", {"start": v(46.23, 38.47) * mm, "end": v(46.44, 38.16) * mm});
            skLineSegment(sketch, "E3046", {"start": v(46.44, 38.16) * mm, "end": v(46.44, 38.06) * mm});
            skLineSegment(sketch, "E3047", {"start": v(-60.42, 43.76) * mm, "end": v(-60.42, 43.7) * mm});
            skLineSegment(sketch, "E3048", {"start": v(-60.42, 43.7) * mm, "end": v(-60.54, 43.48) * mm});
            skLineSegment(sketch, "E3049", {"start": v(-60.54, 43.48) * mm, "end": v(-60.75, 43.36) * mm});
            skLineSegment(sketch, "E3050", {"start": v(-60.75, 43.36) * mm, "end": v(-60.82, 43.36) * mm});
            skLineSegment(sketch, "E3051", {"start": v(-60.82, 43.36) * mm, "end": v(-60.9, 43.36) * mm});
            skLineSegment(sketch, "E3052", {"start": v(-60.9, 43.36) * mm, "end": v(-61.1, 43.48) * mm});
            skLineSegment(sketch, "E3053", {"start": v(-61.1, 43.48) * mm, "end": v(-61.22, 43.7) * mm});
            skLineSegment(sketch, "E3054", {"start": v(-61.22, 43.7) * mm, "end": v(-61.22, 43.76) * mm});
            skLineSegment(sketch, "E3055", {"start": v(-61.22, 43.76) * mm, "end": v(-61.22, 43.84) * mm});
            skLineSegment(sketch, "E3056", {"start": v(-61.22, 43.84) * mm, "end": v(-61.1, 44.05) * mm});
            skLineSegment(sketch, "E3057", {"start": v(-61.1, 44.05) * mm, "end": v(-60.9, 44.16) * mm});
            skLineSegment(sketch, "E3058", {"start": v(-60.9, 44.16) * mm, "end": v(-60.82, 44.16) * mm});
            skLineSegment(sketch, "E3059", {"start": v(-60.82, 44.16) * mm, "end": v(-60.75, 44.16) * mm});
            skLineSegment(sketch, "E3060", {"start": v(-60.75, 44.16) * mm, "end": v(-60.54, 44.05) * mm});
            skLineSegment(sketch, "E3061", {"start": v(-60.54, 44.05) * mm, "end": v(-60.42, 43.84) * mm});
            skLineSegment(sketch, "E3062", {"start": v(-60.42, 43.84) * mm, "end": v(-60.42, 43.76) * mm});
            skLineSegment(sketch, "E3063", {"start": v(-60.42, 41.76) * mm, "end": v(-60.42, 41.7) * mm});
            skLineSegment(sketch, "E3064", {"start": v(-60.42, 41.7) * mm, "end": v(-60.54, 41.48) * mm});
            skLineSegment(sketch, "E3065", {"start": v(-60.54, 41.48) * mm, "end": v(-60.75, 41.36) * mm});
            skLineSegment(sketch, "E3066", {"start": v(-60.75, 41.36) * mm, "end": v(-60.82, 41.36) * mm});
            skLineSegment(sketch, "E3067", {"start": v(-60.82, 41.36) * mm, "end": v(-60.9, 41.36) * mm});
            skLineSegment(sketch, "E3068", {"start": v(-60.9, 41.36) * mm, "end": v(-61.1, 41.48) * mm});
            skLineSegment(sketch, "E3069", {"start": v(-61.1, 41.48) * mm, "end": v(-61.22, 41.7) * mm});
            skLineSegment(sketch, "E3070", {"start": v(-61.22, 41.7) * mm, "end": v(-61.22, 41.76) * mm});
            skLineSegment(sketch, "E3071", {"start": v(-61.22, 41.76) * mm, "end": v(-61.22, 41.84) * mm});
            skLineSegment(sketch, "E3072", {"start": v(-61.22, 41.84) * mm, "end": v(-61.1, 42.05) * mm});
            skLineSegment(sketch, "E3073", {"start": v(-61.1, 42.05) * mm, "end": v(-60.9, 42.16) * mm});
            skLineSegment(sketch, "E3074", {"start": v(-60.9, 42.16) * mm, "end": v(-60.82, 42.16) * mm});
            skLineSegment(sketch, "E3075", {"start": v(-60.82, 42.16) * mm, "end": v(-60.75, 42.16) * mm});
            skLineSegment(sketch, "E3076", {"start": v(-60.75, 42.16) * mm, "end": v(-60.54, 42.05) * mm});
            skLineSegment(sketch, "E3077", {"start": v(-60.54, 42.05) * mm, "end": v(-60.42, 41.84) * mm});
            skLineSegment(sketch, "E3078", {"start": v(-60.42, 41.84) * mm, "end": v(-60.42, 41.76) * mm});
            skLineSegment(sketch, "E3079", {"start": v(-60.42, 52.8) * mm, "end": v(-60.42, 52.73) * mm});
            skLineSegment(sketch, "E3080", {"start": v(-60.42, 52.73) * mm, "end": v(-60.54, 52.52) * mm});
            skLineSegment(sketch, "E3081", {"start": v(-60.54, 52.52) * mm, "end": v(-60.75, 52.4) * mm});
            skLineSegment(sketch, "E3082", {"start": v(-60.75, 52.4) * mm, "end": v(-60.82, 52.4) * mm});
            skLineSegment(sketch, "E3083", {"start": v(-60.82, 52.4) * mm, "end": v(-60.9, 52.4) * mm});
            skLineSegment(sketch, "E3084", {"start": v(-60.9, 52.4) * mm, "end": v(-61.1, 52.52) * mm});
            skLineSegment(sketch, "E3085", {"start": v(-61.1, 52.52) * mm, "end": v(-61.22, 52.73) * mm});
            skLineSegment(sketch, "E3086", {"start": v(-61.22, 52.73) * mm, "end": v(-61.22, 52.8) * mm});
            skLineSegment(sketch, "E3087", {"start": v(-61.22, 52.8) * mm, "end": v(-61.22, 52.87) * mm});
            skLineSegment(sketch, "E3088", {"start": v(-61.22, 52.87) * mm, "end": v(-61.1, 53.08) * mm});
            skLineSegment(sketch, "E3089", {"start": v(-61.1, 53.08) * mm, "end": v(-60.9, 53.2) * mm});
            skLineSegment(sketch, "E3090", {"start": v(-60.9, 53.2) * mm, "end": v(-60.82, 53.2) * mm});
            skLineSegment(sketch, "E3091", {"start": v(-60.82, 53.2) * mm, "end": v(-60.75, 53.2) * mm});
            skLineSegment(sketch, "E3092", {"start": v(-60.75, 53.2) * mm, "end": v(-60.54, 53.08) * mm});
            skLineSegment(sketch, "E3093", {"start": v(-60.54, 53.08) * mm, "end": v(-60.42, 52.87) * mm});
            skLineSegment(sketch, "E3094", {"start": v(-60.42, 52.87) * mm, "end": v(-60.42, 52.8) * mm});
            skLineSegment(sketch, "E3095", {"start": v(-5.66, -52.07) * mm, "end": v(-5.66, -52.38) * mm});
            skLineSegment(sketch, "E3096", {"start": v(-5.66, -52.38) * mm, "end": v(-6, -53.32) * mm});
            skLineSegment(sketch, "E3097", {"start": v(-6, -53.32) * mm, "end": v(-6.72, -54.12) * mm});
            skLineSegment(sketch, "E3098", {"start": v(-6.72, -54.12) * mm, "end": v(-6.91, -54.24) * mm});
            skLineSegment(sketch, "E3099", {"start": v(-6.91, -54.24) * mm, "end": v(-7.1, -54.35) * mm});
            skLineSegment(sketch, "E3100", {"start": v(-7.1, -54.35) * mm, "end": v(-8.16, -54.57) * mm});
            skLineSegment(sketch, "E3101", {"start": v(-8.16, -54.57) * mm, "end": v(-9.22, -54.35) * mm});
            skLineSegment(sketch, "E3102", {"start": v(-9.22, -54.35) * mm, "end": v(-9.41, -54.24) * mm});
            skLineSegment(sketch, "E3103", {"start": v(-9.41, -54.24) * mm, "end": v(-9.6, -54.12) * mm});
            skLineSegment(sketch, "E3104", {"start": v(-9.6, -54.12) * mm, "end": v(-10.33, -53.32) * mm});
            skLineSegment(sketch, "E3105", {"start": v(-10.33, -53.32) * mm, "end": v(-10.66, -52.38) * mm});
            skLineSegment(sketch, "E3106", {"start": v(-10.66, -52.38) * mm, "end": v(-10.66, -52.07) * mm});
            skLineSegment(sketch, "E3107", {"start": v(-10.66, -52.07) * mm, "end": v(-10.66, -51.76) * mm});
            skLineSegment(sketch, "E3108", {"start": v(-10.66, -51.76) * mm, "end": v(-10.33, -50.82) * mm});
            skLineSegment(sketch, "E3109", {"start": v(-10.33, -50.82) * mm, "end": v(-9.6, -50.02) * mm});
            skLineSegment(sketch, "E3110", {"start": v(-9.6, -50.02) * mm, "end": v(-9.41, -49.9) * mm});
            skLineSegment(sketch, "E3111", {"start": v(-9.41, -49.9) * mm, "end": v(-9.22, -49.8) * mm});
            skLineSegment(sketch, "E3112", {"start": v(-9.22, -49.8) * mm, "end": v(-8.16, -49.57) * mm});
            skLineSegment(sketch, "E3113", {"start": v(-8.16, -49.57) * mm, "end": v(-7.1, -49.8) * mm});
            skLineSegment(sketch, "E3114", {"start": v(-7.1, -49.8) * mm, "end": v(-6.91, -49.9) * mm});
            skLineSegment(sketch, "E3115", {"start": v(-6.91, -49.9) * mm, "end": v(-6.72, -50.02) * mm});
            skLineSegment(sketch, "E3116", {"start": v(-6.72, -50.02) * mm, "end": v(-6, -50.82) * mm});
            skLineSegment(sketch, "E3117", {"start": v(-6, -50.82) * mm, "end": v(-5.66, -51.76) * mm});
            skLineSegment(sketch, "E3118", {"start": v(-5.66, -51.76) * mm, "end": v(-5.66, -52.07) * mm});
            skLineSegment(sketch, "E3119", {"start": v(-24.67, -52.07) * mm, "end": v(-24.67, -52.38) * mm});
            skLineSegment(sketch, "E3120", {"start": v(-24.67, -52.38) * mm, "end": v(-25, -53.32) * mm});
            skLineSegment(sketch, "E3121", {"start": v(-25, -53.32) * mm, "end": v(-25.72, -54.12) * mm});
            skLineSegment(sketch, "E3122", {"start": v(-25.72, -54.12) * mm, "end": v(-25.91, -54.24) * mm});
            skLineSegment(sketch, "E3123", {"start": v(-25.91, -54.24) * mm, "end": v(-26.1, -54.35) * mm});
            skLineSegment(sketch, "E3124", {"start": v(-26.1, -54.35) * mm, "end": v(-27.16, -54.57) * mm});
            skLineSegment(sketch, "E3125", {"start": v(-27.16, -54.57) * mm, "end": v(-28.22, -54.35) * mm});
            skLineSegment(sketch, "E3126", {"start": v(-28.22, -54.35) * mm, "end": v(-28.41, -54.24) * mm});
            skLineSegment(sketch, "E3127", {"start": v(-28.41, -54.24) * mm, "end": v(-28.6, -54.12) * mm});
            skLineSegment(sketch, "E3128", {"start": v(-28.6, -54.12) * mm, "end": v(-29.33, -53.32) * mm});
            skLineSegment(sketch, "E3129", {"start": v(-29.33, -53.32) * mm, "end": v(-29.66, -52.38) * mm});
            skLineSegment(sketch, "E3130", {"start": v(-29.66, -52.38) * mm, "end": v(-29.66, -52.07) * mm});
            skLineSegment(sketch, "E3131", {"start": v(-29.66, -52.07) * mm, "end": v(-29.66, -51.76) * mm});
            skLineSegment(sketch, "E3132", {"start": v(-29.66, -51.76) * mm, "end": v(-29.33, -50.82) * mm});
            skLineSegment(sketch, "E3133", {"start": v(-29.33, -50.82) * mm, "end": v(-28.6, -50.02) * mm});
            skLineSegment(sketch, "E3134", {"start": v(-28.6, -50.02) * mm, "end": v(-28.41, -49.9) * mm});
            skLineSegment(sketch, "E3135", {"start": v(-28.41, -49.9) * mm, "end": v(-28.22, -49.8) * mm});
            skLineSegment(sketch, "E3136", {"start": v(-28.22, -49.8) * mm, "end": v(-27.16, -49.57) * mm});
            skLineSegment(sketch, "E3137", {"start": v(-27.16, -49.57) * mm, "end": v(-26.1, -49.8) * mm});
            skLineSegment(sketch, "E3138", {"start": v(-26.1, -49.8) * mm, "end": v(-25.91, -49.9) * mm});
            skLineSegment(sketch, "E3139", {"start": v(-25.91, -49.9) * mm, "end": v(-25.72, -50.02) * mm});
            skLineSegment(sketch, "E3140", {"start": v(-25.72, -50.02) * mm, "end": v(-25, -50.82) * mm});
            skLineSegment(sketch, "E3141", {"start": v(-25, -50.82) * mm, "end": v(-24.67, -51.76) * mm});
            skLineSegment(sketch, "E3142", {"start": v(-24.67, -51.76) * mm, "end": v(-24.67, -52.07) * mm});
            skLineSegment(sketch, "E3143", {"start": v(51.3, 5.1) * mm, "end": v(51.3, 4.96) * mm});
            skLineSegment(sketch, "E3144", {"start": v(51.3, 4.96) * mm, "end": v(51.16, 4.55) * mm});
            skLineSegment(sketch, "E3145", {"start": v(51.16, 4.55) * mm, "end": v(50.84, 4.2) * mm});
            skLineSegment(sketch, "E3146", {"start": v(50.84, 4.2) * mm, "end": v(50.75, 4.15) * mm});
            skLineSegment(sketch, "E3147", {"start": v(50.75, 4.15) * mm, "end": v(50.67, 4.1) * mm});
            skLineSegment(sketch, "E3148", {"start": v(50.67, 4.1) * mm, "end": v(50.2, 4) * mm});
            skLineSegment(sketch, "E3149", {"start": v(50.2, 4) * mm, "end": v(49.74, 4.1) * mm});
            skLineSegment(sketch, "E3150", {"start": v(49.74, 4.1) * mm, "end": v(49.65, 4.15) * mm});
            skLineSegment(sketch, "E3151", {"start": v(49.65, 4.15) * mm, "end": v(49.57, 4.2) * mm});
            skLineSegment(sketch, "E3152", {"start": v(49.57, 4.2) * mm, "end": v(49.25, 4.55) * mm});
            skLineSegment(sketch, "E3153", {"start": v(49.25, 4.55) * mm, "end": v(49.1, 4.96) * mm});
            skLineSegment(sketch, "E3154", {"start": v(49.1, 4.96) * mm, "end": v(49.1, 5.1) * mm});
            skLineSegment(sketch, "E3155", {"start": v(49.1, 5.1) * mm, "end": v(49.1, 5.24) * mm});
            skLineSegment(sketch, "E3156", {"start": v(49.1, 5.24) * mm, "end": v(49.25, 5.65) * mm});
            skLineSegment(sketch, "E3157", {"start": v(49.25, 5.65) * mm, "end": v(49.57, 6) * mm});
            skLineSegment(sketch, "E3158", {"start": v(49.57, 6) * mm, "end": v(49.65, 6.05) * mm});
            skLineSegment(sketch, "E3159", {"start": v(49.65, 6.05) * mm, "end": v(49.74, 6.1) * mm});
            skLineSegment(sketch, "E3160", {"start": v(49.74, 6.1) * mm, "end": v(50.2, 6.2) * mm});
            skLineSegment(sketch, "E3161", {"start": v(50.2, 6.2) * mm, "end": v(50.67, 6.1) * mm});
            skLineSegment(sketch, "E3162", {"start": v(50.67, 6.1) * mm, "end": v(50.75, 6.05) * mm});
            skLineSegment(sketch, "E3163", {"start": v(50.75, 6.05) * mm, "end": v(50.84, 6) * mm});
            skLineSegment(sketch, "E3164", {"start": v(50.84, 6) * mm, "end": v(51.16, 5.65) * mm});
            skLineSegment(sketch, "E3165", {"start": v(51.16, 5.65) * mm, "end": v(51.3, 5.24) * mm});
            skLineSegment(sketch, "E3166", {"start": v(51.3, 5.24) * mm, "end": v(51.3, 5.1) * mm});
            skLineSegment(sketch, "E3167", {"start": v(51.3, -5.1) * mm, "end": v(51.3, -5.24) * mm});
            skLineSegment(sketch, "E3168", {"start": v(51.3, -5.24) * mm, "end": v(51.16, -5.65) * mm});
            skLineSegment(sketch, "E3169", {"start": v(51.16, -5.65) * mm, "end": v(50.84, -6) * mm});
            skLineSegment(sketch, "E3170", {"start": v(50.84, -6) * mm, "end": v(50.75, -6.05) * mm});
            skLineSegment(sketch, "E3171", {"start": v(50.75, -6.05) * mm, "end": v(50.67, -6.1) * mm});
            skLineSegment(sketch, "E3172", {"start": v(50.67, -6.1) * mm, "end": v(50.2, -6.2) * mm});
            skLineSegment(sketch, "E3173", {"start": v(50.2, -6.2) * mm, "end": v(49.74, -6.1) * mm});
            skLineSegment(sketch, "E3174", {"start": v(49.74, -6.1) * mm, "end": v(49.65, -6.05) * mm});
            skLineSegment(sketch, "E3175", {"start": v(49.65, -6.05) * mm, "end": v(49.57, -6) * mm});
            skLineSegment(sketch, "E3176", {"start": v(49.57, -6) * mm, "end": v(49.25, -5.65) * mm});
            skLineSegment(sketch, "E3177", {"start": v(49.25, -5.65) * mm, "end": v(49.1, -5.24) * mm});
            skLineSegment(sketch, "E3178", {"start": v(49.1, -5.24) * mm, "end": v(49.1, -5.1) * mm});
            skLineSegment(sketch, "E3179", {"start": v(49.1, -5.1) * mm, "end": v(49.1, -4.96) * mm});
            skLineSegment(sketch, "E3180", {"start": v(49.1, -4.96) * mm, "end": v(49.25, -4.55) * mm});
            skLineSegment(sketch, "E3181", {"start": v(49.25, -4.55) * mm, "end": v(49.57, -4.2) * mm});
            skLineSegment(sketch, "E3182", {"start": v(49.57, -4.2) * mm, "end": v(49.65, -4.15) * mm});
            skLineSegment(sketch, "E3183", {"start": v(49.65, -4.15) * mm, "end": v(49.74, -4.1) * mm});
            skLineSegment(sketch, "E3184", {"start": v(49.74, -4.1) * mm, "end": v(50.2, -4) * mm});
            skLineSegment(sketch, "E3185", {"start": v(50.2, -4) * mm, "end": v(50.67, -4.1) * mm});
            skLineSegment(sketch, "E3186", {"start": v(50.67, -4.1) * mm, "end": v(50.75, -4.15) * mm});
            skLineSegment(sketch, "E3187", {"start": v(50.75, -4.15) * mm, "end": v(50.84, -4.2) * mm});
            skLineSegment(sketch, "E3188", {"start": v(50.84, -4.2) * mm, "end": v(51.16, -4.55) * mm});
            skLineSegment(sketch, "E3189", {"start": v(51.16, -4.55) * mm, "end": v(51.3, -4.96) * mm});
            skLineSegment(sketch, "E3190", {"start": v(51.3, -4.96) * mm, "end": v(51.3, -5.1) * mm});
            skLineSegment(sketch, "E3191", {"start": v(46.44, 0) * mm, "end": v(46.44, -0.1) * mm});
            skLineSegment(sketch, "E3192", {"start": v(46.44, -0.1) * mm, "end": v(46.23, -0.41) * mm});
            skLineSegment(sketch, "E3193", {"start": v(46.23, -0.41) * mm, "end": v(46.19, -0.43) * mm});
            skLineSegment(sketch, "E3194", {"start": v(46.19, -0.43) * mm, "end": v(46.15, -0.45) * mm});
            skLineSegment(sketch, "E3195", {"start": v(46.15, -0.45) * mm, "end": v(45.73, -0.45) * mm});
            skLineSegment(sketch, "E3196", {"start": v(45.73, -0.45) * mm, "end": v(45.69, -0.43) * mm});
            skLineSegment(sketch, "E3197", {"start": v(45.69, -0.43) * mm, "end": v(45.65, -0.41) * mm});
            skLineSegment(sketch, "E3198", {"start": v(45.65, -0.41) * mm, "end": v(45.44, -0.1) * mm});
            skLineSegment(sketch, "E3199", {"start": v(45.44, -0.1) * mm, "end": v(45.44, 0) * mm});
            skLineSegment(sketch, "E3200", {"start": v(45.44, 0) * mm, "end": v(45.44, 0.1) * mm});
            skLineSegment(sketch, "E3201", {"start": v(45.44, 0.1) * mm, "end": v(45.65, 0.41) * mm});
            skLineSegment(sketch, "E3202", {"start": v(45.65, 0.41) * mm, "end": v(45.69, 0.43) * mm});
            skLineSegment(sketch, "E3203", {"start": v(45.69, 0.43) * mm, "end": v(45.73, 0.46) * mm});
            skLineSegment(sketch, "E3204", {"start": v(45.73, 0.46) * mm, "end": v(46.15, 0.46) * mm});
            skLineSegment(sketch, "E3205", {"start": v(46.15, 0.46) * mm, "end": v(46.19, 0.43) * mm});
            skLineSegment(sketch, "E3206", {"start": v(46.19, 0.43) * mm, "end": v(46.23, 0.41) * mm});
            skLineSegment(sketch, "E3207", {"start": v(46.23, 0.41) * mm, "end": v(46.44, 0.1) * mm});
            skLineSegment(sketch, "E3208", {"start": v(46.44, 0.1) * mm, "end": v(46.44, 0) * mm});
            skLineSegment(sketch, "E3209", {"start": v(46.44, 2.5) * mm, "end": v(46.44, 2.4) * mm});
            skLineSegment(sketch, "E3210", {"start": v(46.44, 2.4) * mm, "end": v(46.23, 2.09) * mm});
            skLineSegment(sketch, "E3211", {"start": v(46.23, 2.09) * mm, "end": v(46.19, 2.07) * mm});
            skLineSegment(sketch, "E3212", {"start": v(46.19, 2.07) * mm, "end": v(46.15, 2.04) * mm});
            skLineSegment(sketch, "E3213", {"start": v(46.15, 2.04) * mm, "end": v(45.73, 2.04) * mm});
            skLineSegment(sketch, "E3214", {"start": v(45.73, 2.04) * mm, "end": v(45.69, 2.07) * mm});
            skLineSegment(sketch, "E3215", {"start": v(45.69, 2.07) * mm, "end": v(45.65, 2.09) * mm});
            skLineSegment(sketch, "E3216", {"start": v(45.65, 2.09) * mm, "end": v(45.44, 2.4) * mm});
            skLineSegment(sketch, "E3217", {"start": v(45.44, 2.4) * mm, "end": v(45.44, 2.5) * mm});
            skLineSegment(sketch, "E3218", {"start": v(45.44, 2.5) * mm, "end": v(45.44, 2.6) * mm});
            skLineSegment(sketch, "E3219", {"start": v(45.44, 2.6) * mm, "end": v(45.65, 2.91) * mm});
            skLineSegment(sketch, "E3220", {"start": v(45.65, 2.91) * mm, "end": v(45.69, 2.93) * mm});
            skLineSegment(sketch, "E3221", {"start": v(45.69, 2.93) * mm, "end": v(45.73, 2.96) * mm});
            skLineSegment(sketch, "E3222", {"start": v(45.73, 2.96) * mm, "end": v(46.15, 2.96) * mm});
            skLineSegment(sketch, "E3223", {"start": v(46.15, 2.96) * mm, "end": v(46.19, 2.93) * mm});
            skLineSegment(sketch, "E3224", {"start": v(46.19, 2.93) * mm, "end": v(46.23, 2.91) * mm});
            skLineSegment(sketch, "E3225", {"start": v(46.23, 2.91) * mm, "end": v(46.44, 2.6) * mm});
            skLineSegment(sketch, "E3226", {"start": v(46.44, 2.6) * mm, "end": v(46.44, 2.5) * mm});
            skLineSegment(sketch, "E3227", {"start": v(-22.61, 13.9) * mm, "end": v(-22.61, 13.81) * mm});
            skLineSegment(sketch, "E3228", {"start": v(-22.61, 13.81) * mm, "end": v(-22.78, 13.58) * mm});
            skLineSegment(sketch, "E3229", {"start": v(-22.78, 13.58) * mm, "end": v(-22.8, 13.57) * mm});
            skLineSegment(sketch, "E3230", {"start": v(-22.8, 13.57) * mm, "end": v(-22.83, 13.55) * mm});
            skLineSegment(sketch, "E3231", {"start": v(-22.83, 13.55) * mm, "end": v(-23.16, 13.55) * mm});
            skLineSegment(sketch, "E3232", {"start": v(-23.16, 13.55) * mm, "end": v(-23.18, 13.57) * mm});
            skLineSegment(sketch, "E3233", {"start": v(-23.18, 13.57) * mm, "end": v(-23.21, 13.58) * mm});
            skLineSegment(sketch, "E3234", {"start": v(-23.21, 13.58) * mm, "end": v(-23.37, 13.82) * mm});
            skLineSegment(sketch, "E3235", {"start": v(-23.37, 13.82) * mm, "end": v(-23.37, 13.9) * mm});
            skLineSegment(sketch, "E3236", {"start": v(-23.37, 13.9) * mm, "end": v(-23.37, 13.98) * mm});
            skLineSegment(sketch, "E3237", {"start": v(-23.37, 13.98) * mm, "end": v(-23.21, 14.2) * mm});
            skLineSegment(sketch, "E3238", {"start": v(-23.21, 14.2) * mm, "end": v(-23.18, 14.23) * mm});
            skLineSegment(sketch, "E3239", {"start": v(-23.18, 14.23) * mm, "end": v(-23.16, 14.24) * mm});
            skLineSegment(sketch, "E3240", {"start": v(-23.16, 14.24) * mm, "end": v(-22.83, 14.24) * mm});
            skLineSegment(sketch, "E3241", {"start": v(-22.83, 14.24) * mm, "end": v(-22.8, 14.23) * mm});
            skLineSegment(sketch, "E3242", {"start": v(-22.8, 14.23) * mm, "end": v(-22.78, 14.2) * mm});
            skLineSegment(sketch, "E3243", {"start": v(-22.78, 14.2) * mm, "end": v(-22.61, 13.97) * mm});
            skLineSegment(sketch, "E3244", {"start": v(-22.61, 13.97) * mm, "end": v(-22.61, 13.9) * mm});
            skLineSegment(sketch, "E3245", {"start": v(-22.23, 12.44) * mm, "end": v(-22.23, 12.35) * mm});
            skLineSegment(sketch, "E3246", {"start": v(-22.23, 12.35) * mm, "end": v(-22.4, 12.12) * mm});
            skLineSegment(sketch, "E3247", {"start": v(-22.4, 12.12) * mm, "end": v(-22.42, 12.1) * mm});
            skLineSegment(sketch, "E3248", {"start": v(-22.42, 12.1) * mm, "end": v(-22.45, 12.09) * mm});
            skLineSegment(sketch, "E3249", {"start": v(-22.45, 12.09) * mm, "end": v(-22.78, 12.09) * mm});
            skLineSegment(sketch, "E3250", {"start": v(-22.78, 12.09) * mm, "end": v(-22.8, 12.1) * mm});
            skLineSegment(sketch, "E3251", {"start": v(-22.8, 12.1) * mm, "end": v(-22.83, 12.12) * mm});
            skLineSegment(sketch, "E3252", {"start": v(-22.83, 12.12) * mm, "end": v(-23, 12.36) * mm});
            skLineSegment(sketch, "E3253", {"start": v(-23, 12.36) * mm, "end": v(-23, 12.44) * mm});
            skLineSegment(sketch, "E3254", {"start": v(-23, 12.44) * mm, "end": v(-23, 12.52) * mm});
            skLineSegment(sketch, "E3255", {"start": v(-23, 12.52) * mm, "end": v(-22.83, 12.75) * mm});
            skLineSegment(sketch, "E3256", {"start": v(-22.83, 12.75) * mm, "end": v(-22.8, 12.76) * mm});
            skLineSegment(sketch, "E3257", {"start": v(-22.8, 12.76) * mm, "end": v(-22.78, 12.78) * mm});
            skLineSegment(sketch, "E3258", {"start": v(-22.78, 12.78) * mm, "end": v(-22.45, 12.78) * mm});
            skLineSegment(sketch, "E3259", {"start": v(-22.45, 12.78) * mm, "end": v(-22.42, 12.76) * mm});
            skLineSegment(sketch, "E3260", {"start": v(-22.42, 12.76) * mm, "end": v(-22.4, 12.75) * mm});
            skLineSegment(sketch, "E3261", {"start": v(-22.4, 12.75) * mm, "end": v(-22.23, 12.51) * mm});
            skLineSegment(sketch, "E3262", {"start": v(-22.23, 12.51) * mm, "end": v(-22.23, 12.44) * mm});
            skLineSegment(sketch, "E3263", {"start": v(5.07, 12.63) * mm, "end": v(5.07, 12.54) * mm});
            skLineSegment(sketch, "E3264", {"start": v(5.07, 12.54) * mm, "end": v(4.91, 12.31) * mm});
            skLineSegment(sketch, "E3265", {"start": v(4.91, 12.31) * mm, "end": v(4.88, 12.3) * mm});
            skLineSegment(sketch, "E3266", {"start": v(4.88, 12.3) * mm, "end": v(4.85, 12.28) * mm});
            skLineSegment(sketch, "E3267", {"start": v(4.85, 12.28) * mm, "end": v(4.53, 12.28) * mm});
            skLineSegment(sketch, "E3268", {"start": v(4.53, 12.28) * mm, "end": v(4.5, 12.3) * mm});
            skLineSegment(sketch, "E3269", {"start": v(4.5, 12.3) * mm, "end": v(4.47, 12.31) * mm});
            skLineSegment(sketch, "E3270", {"start": v(4.47, 12.31) * mm, "end": v(4.31, 12.55) * mm});
            skLineSegment(sketch, "E3271", {"start": v(4.31, 12.55) * mm, "end": v(4.31, 12.63) * mm});
            skLineSegment(sketch, "E3272", {"start": v(4.31, 12.63) * mm, "end": v(4.31, 12.7) * mm});
            skLineSegment(sketch, "E3273", {"start": v(4.31, 12.7) * mm, "end": v(4.47, 12.94) * mm});
            skLineSegment(sketch, "E3274", {"start": v(4.47, 12.94) * mm, "end": v(4.5, 12.96) * mm});
            skLineSegment(sketch, "E3275", {"start": v(4.5, 12.96) * mm, "end": v(4.53, 12.97) * mm});
            skLineSegment(sketch, "E3276", {"start": v(4.53, 12.97) * mm, "end": v(4.85, 12.97) * mm});
            skLineSegment(sketch, "E3277", {"start": v(4.85, 12.97) * mm, "end": v(4.88, 12.96) * mm});
            skLineSegment(sketch, "E3278", {"start": v(4.88, 12.96) * mm, "end": v(4.91, 12.94) * mm});
            skLineSegment(sketch, "E3279", {"start": v(4.91, 12.94) * mm, "end": v(5.07, 12.7) * mm});
            skLineSegment(sketch, "E3280", {"start": v(5.07, 12.7) * mm, "end": v(5.07, 12.63) * mm});
            skLineSegment(sketch, "E3281", {"start": v(0.68, 17.98) * mm, "end": v(0.68, 17.9) * mm});
            skLineSegment(sketch, "E3282", {"start": v(0.68, 17.9) * mm, "end": v(0.52, 17.67) * mm});
            skLineSegment(sketch, "E3283", {"start": v(0.52, 17.67) * mm, "end": v(0.49, 17.66) * mm});
            skLineSegment(sketch, "E3284", {"start": v(0.49, 17.66) * mm, "end": v(0.46, 17.64) * mm});
            skLineSegment(sketch, "E3285", {"start": v(0.46, 17.64) * mm, "end": v(0.14, 17.64) * mm});
            skLineSegment(sketch, "E3286", {"start": v(0.14, 17.64) * mm, "end": v(0.1, 17.66) * mm});
            skLineSegment(sketch, "E3287", {"start": v(0.1, 17.66) * mm, "end": v(0.08, 17.67) * mm});
            skLineSegment(sketch, "E3288", {"start": v(0.08, 17.67) * mm, "end": v(-0.08, 17.9) * mm});
            skLineSegment(sketch, "E3289", {"start": v(-0.08, 17.9) * mm, "end": v(-0.08, 17.98) * mm});
            skLineSegment(sketch, "E3290", {"start": v(-0.08, 17.98) * mm, "end": v(-0.08, 18.05) * mm});
            skLineSegment(sketch, "E3291", {"start": v(-0.08, 18.05) * mm, "end": v(0.03, 18.25) * mm});
            skLineSegment(sketch, "E3292", {"start": v(0.03, 18.25) * mm, "end": v(0.23, 18.37) * mm});
            skLineSegment(sketch, "E3293", {"start": v(0.23, 18.37) * mm, "end": v(0.3, 18.37) * mm});
            skLineSegment(sketch, "E3294", {"start": v(0.3, 18.37) * mm, "end": v(0.36, 18.37) * mm});
            skLineSegment(sketch, "E3295", {"start": v(0.36, 18.37) * mm, "end": v(0.57, 18.25) * mm});
            skLineSegment(sketch, "E3296", {"start": v(0.57, 18.25) * mm, "end": v(0.68, 18.05) * mm});
            skLineSegment(sketch, "E3297", {"start": v(0.68, 18.05) * mm, "end": v(0.68, 17.98) * mm});
            skLineSegment(sketch, "E3298", {"start": v(-1.4, 19.93) * mm, "end": v(-1.4, 19.85) * mm});
            skLineSegment(sketch, "E3299", {"start": v(-1.4, 19.85) * mm, "end": v(-1.57, 19.62) * mm});
            skLineSegment(sketch, "E3300", {"start": v(-1.57, 19.62) * mm, "end": v(-1.6, 19.6) * mm});
            skLineSegment(sketch, "E3301", {"start": v(-1.6, 19.6) * mm, "end": v(-1.63, 19.58) * mm});
            skLineSegment(sketch, "E3302", {"start": v(-1.63, 19.58) * mm, "end": v(-1.95, 19.58) * mm});
            skLineSegment(sketch, "E3303", {"start": v(-1.95, 19.58) * mm, "end": v(-1.98, 19.6) * mm});
            skLineSegment(sketch, "E3304", {"start": v(-1.98, 19.6) * mm, "end": v(-2, 19.62) * mm});
            skLineSegment(sketch, "E3305", {"start": v(-2, 19.62) * mm, "end": v(-2.17, 19.85) * mm});
            skLineSegment(sketch, "E3306", {"start": v(-2.17, 19.85) * mm, "end": v(-2.17, 19.93) * mm});
            skLineSegment(sketch, "E3307", {"start": v(-2.17, 19.93) * mm, "end": v(-2.17, 20.01) * mm});
            skLineSegment(sketch, "E3308", {"start": v(-2.17, 20.01) * mm, "end": v(-2, 20.24) * mm});
            skLineSegment(sketch, "E3309", {"start": v(-2, 20.24) * mm, "end": v(-1.98, 20.26) * mm});
            skLineSegment(sketch, "E3310", {"start": v(-1.98, 20.26) * mm, "end": v(-1.95, 20.28) * mm});
            skLineSegment(sketch, "E3311", {"start": v(-1.95, 20.28) * mm, "end": v(-1.63, 20.28) * mm});
            skLineSegment(sketch, "E3312", {"start": v(-1.63, 20.28) * mm, "end": v(-1.6, 20.26) * mm});
            skLineSegment(sketch, "E3313", {"start": v(-1.6, 20.26) * mm, "end": v(-1.57, 20.24) * mm});
            skLineSegment(sketch, "E3314", {"start": v(-1.57, 20.24) * mm, "end": v(-1.4, 20) * mm});
            skLineSegment(sketch, "E3315", {"start": v(-1.4, 20) * mm, "end": v(-1.4, 19.93) * mm});
            skLineSegment(sketch, "E3316", {"start": v(2.6, 21.77) * mm, "end": v(2.6, 21.69) * mm});
            skLineSegment(sketch, "E3317", {"start": v(2.6, 21.69) * mm, "end": v(2.43, 21.46) * mm});
            skLineSegment(sketch, "E3318", {"start": v(2.43, 21.46) * mm, "end": v(2.4, 21.44) * mm});
            skLineSegment(sketch, "E3319", {"start": v(2.4, 21.44) * mm, "end": v(2.38, 21.42) * mm});
            skLineSegment(sketch, "E3320", {"start": v(2.38, 21.42) * mm, "end": v(2.05, 21.42) * mm});
            skLineSegment(sketch, "E3321", {"start": v(2.05, 21.42) * mm, "end": v(2.03, 21.44) * mm});
            skLineSegment(sketch, "E3322", {"start": v(2.03, 21.44) * mm, "end": v(2, 21.46) * mm});
            skLineSegment(sketch, "E3323", {"start": v(2, 21.46) * mm, "end": v(1.84, 21.7) * mm});
            skLineSegment(sketch, "E3324", {"start": v(1.84, 21.7) * mm, "end": v(1.84, 21.77) * mm});
            skLineSegment(sketch, "E3325", {"start": v(1.84, 21.77) * mm, "end": v(1.84, 21.85) * mm});
            skLineSegment(sketch, "E3326", {"start": v(1.84, 21.85) * mm, "end": v(2, 22.08) * mm});
            skLineSegment(sketch, "E3327", {"start": v(2, 22.08) * mm, "end": v(2.03, 22.1) * mm});
            skLineSegment(sketch, "E3328", {"start": v(2.03, 22.1) * mm, "end": v(2.05, 22.12) * mm});
            skLineSegment(sketch, "E3329", {"start": v(2.05, 22.12) * mm, "end": v(2.38, 22.12) * mm});
            skLineSegment(sketch, "E3330", {"start": v(2.38, 22.12) * mm, "end": v(2.4, 22.1) * mm});
            skLineSegment(sketch, "E3331", {"start": v(2.4, 22.1) * mm, "end": v(2.43, 22.08) * mm});
            skLineSegment(sketch, "E3332", {"start": v(2.43, 22.08) * mm, "end": v(2.6, 21.85) * mm});
            skLineSegment(sketch, "E3333", {"start": v(2.6, 21.85) * mm, "end": v(2.6, 21.77) * mm});
            skLineSegment(sketch, "E3334", {"start": v(12.44, 12.88) * mm, "end": v(12.44, 12.8) * mm});
            skLineSegment(sketch, "E3335", {"start": v(12.44, 12.8) * mm, "end": v(12.28, 12.57) * mm});
            skLineSegment(sketch, "E3336", {"start": v(12.28, 12.57) * mm, "end": v(12.25, 12.55) * mm});
            skLineSegment(sketch, "E3337", {"start": v(12.25, 12.55) * mm, "end": v(12.22, 12.53) * mm});
            skLineSegment(sketch, "E3338", {"start": v(12.22, 12.53) * mm, "end": v(11.9, 12.53) * mm});
            skLineSegment(sketch, "E3339", {"start": v(11.9, 12.53) * mm, "end": v(11.87, 12.55) * mm});
            skLineSegment(sketch, "E3340", {"start": v(11.87, 12.55) * mm, "end": v(11.84, 12.57) * mm});
            skLineSegment(sketch, "E3341", {"start": v(11.84, 12.57) * mm, "end": v(11.68, 12.8) * mm});
            skLineSegment(sketch, "E3342", {"start": v(11.68, 12.8) * mm, "end": v(11.68, 12.88) * mm});
            skLineSegment(sketch, "E3343", {"start": v(11.68, 12.88) * mm, "end": v(11.68, 12.96) * mm});
            skLineSegment(sketch, "E3344", {"start": v(11.68, 12.96) * mm, "end": v(11.84, 13.2) * mm});
            skLineSegment(sketch, "E3345", {"start": v(11.84, 13.2) * mm, "end": v(11.87, 13.2) * mm});
            skLineSegment(sketch, "E3346", {"start": v(11.87, 13.2) * mm, "end": v(11.9, 13.23) * mm});
            skLineSegment(sketch, "E3347", {"start": v(11.9, 13.23) * mm, "end": v(12.22, 13.23) * mm});
            skLineSegment(sketch, "E3348", {"start": v(12.22, 13.23) * mm, "end": v(12.25, 13.2) * mm});
            skLineSegment(sketch, "E3349", {"start": v(12.25, 13.2) * mm, "end": v(12.28, 13.2) * mm});
            skLineSegment(sketch, "E3350", {"start": v(12.28, 13.2) * mm, "end": v(12.44, 12.96) * mm});
            skLineSegment(sketch, "E3351", {"start": v(12.44, 12.96) * mm, "end": v(12.44, 12.88) * mm});
            skLineSegment(sketch, "E3352", {"start": v(8.25, 22.79) * mm, "end": v(8.25, 22.7) * mm});
            skLineSegment(sketch, "E3353", {"start": v(8.25, 22.7) * mm, "end": v(8.09, 22.47) * mm});
            skLineSegment(sketch, "E3354", {"start": v(8.09, 22.47) * mm, "end": v(8.06, 22.46) * mm});
            skLineSegment(sketch, "E3355", {"start": v(8.06, 22.46) * mm, "end": v(8.03, 22.44) * mm});
            skLineSegment(sketch, "E3356", {"start": v(8.03, 22.44) * mm, "end": v(7.7, 22.44) * mm});
            skLineSegment(sketch, "E3357", {"start": v(7.7, 22.44) * mm, "end": v(7.68, 22.46) * mm});
            skLineSegment(sketch, "E3358", {"start": v(7.68, 22.46) * mm, "end": v(7.65, 22.47) * mm});
            skLineSegment(sketch, "E3359", {"start": v(7.65, 22.47) * mm, "end": v(7.49, 22.7) * mm});
            skLineSegment(sketch, "E3360", {"start": v(7.49, 22.7) * mm, "end": v(7.49, 22.79) * mm});
            skLineSegment(sketch, "E3361", {"start": v(7.49, 22.79) * mm, "end": v(7.49, 22.87) * mm});
            skLineSegment(sketch, "E3362", {"start": v(7.49, 22.87) * mm, "end": v(7.65, 23.1) * mm});
            skLineSegment(sketch, "E3363", {"start": v(7.65, 23.1) * mm, "end": v(7.68, 23.12) * mm});
            skLineSegment(sketch, "E3364", {"start": v(7.68, 23.12) * mm, "end": v(7.7, 23.13) * mm});
            skLineSegment(sketch, "E3365", {"start": v(7.7, 23.13) * mm, "end": v(8.03, 23.13) * mm});
            skLineSegment(sketch, "E3366", {"start": v(8.03, 23.13) * mm, "end": v(8.06, 23.12) * mm});
            skLineSegment(sketch, "E3367", {"start": v(8.06, 23.12) * mm, "end": v(8.09, 23.1) * mm});
            skLineSegment(sketch, "E3368", {"start": v(8.09, 23.1) * mm, "end": v(8.25, 22.86) * mm});
            skLineSegment(sketch, "E3369", {"start": v(8.25, 22.86) * mm, "end": v(8.25, 22.79) * mm});
            skLineSegment(sketch, "E3370", {"start": v(0.82, 23.3) * mm, "end": v(0.82, 23.21) * mm});
            skLineSegment(sketch, "E3371", {"start": v(0.82, 23.21) * mm, "end": v(0.66, 22.98) * mm});
            skLineSegment(sketch, "E3372", {"start": v(0.66, 22.98) * mm, "end": v(0.63, 22.96) * mm});
            skLineSegment(sketch, "E3373", {"start": v(0.63, 22.96) * mm, "end": v(0.6, 22.95) * mm});
            skLineSegment(sketch, "E3374", {"start": v(0.6, 22.95) * mm, "end": v(0.28, 22.95) * mm});
            skLineSegment(sketch, "E3375", {"start": v(0.28, 22.95) * mm, "end": v(0.25, 22.96) * mm});
            skLineSegment(sketch, "E3376", {"start": v(0.25, 22.96) * mm, "end": v(0.22, 22.98) * mm});
            skLineSegment(sketch, "E3377", {"start": v(0.22, 22.98) * mm, "end": v(0.06, 23.22) * mm});
            skLineSegment(sketch, "E3378", {"start": v(0.06, 23.22) * mm, "end": v(0.06, 23.3) * mm});
            skLineSegment(sketch, "E3379", {"start": v(0.06, 23.3) * mm, "end": v(0.06, 23.38) * mm});
            skLineSegment(sketch, "E3380", {"start": v(0.06, 23.38) * mm, "end": v(0.22, 23.6) * mm});
            skLineSegment(sketch, "E3381", {"start": v(0.22, 23.6) * mm, "end": v(0.25, 23.62) * mm});
            skLineSegment(sketch, "E3382", {"start": v(0.25, 23.62) * mm, "end": v(0.28, 23.64) * mm});
            skLineSegment(sketch, "E3383", {"start": v(0.28, 23.64) * mm, "end": v(0.6, 23.64) * mm});
            skLineSegment(sketch, "E3384", {"start": v(0.6, 23.64) * mm, "end": v(0.63, 23.62) * mm});
            skLineSegment(sketch, "E3385", {"start": v(0.63, 23.62) * mm, "end": v(0.66, 23.6) * mm});
            skLineSegment(sketch, "E3386", {"start": v(0.66, 23.6) * mm, "end": v(0.82, 23.37) * mm});
            skLineSegment(sketch, "E3387", {"start": v(0.82, 23.37) * mm, "end": v(0.82, 23.3) * mm});
            skLineSegment(sketch, "E3388", {"start": v(-3.25, 17.83) * mm, "end": v(-3.25, 17.75) * mm});
            skLineSegment(sketch, "E3389", {"start": v(-3.25, 17.75) * mm, "end": v(-3.4, 17.52) * mm});
            skLineSegment(sketch, "E3390", {"start": v(-3.4, 17.52) * mm, "end": v(-3.44, 17.5) * mm});
            skLineSegment(sketch, "E3391", {"start": v(-3.44, 17.5) * mm, "end": v(-3.47, 17.49) * mm});
            skLineSegment(sketch, "E3392", {"start": v(-3.47, 17.49) * mm, "end": v(-3.79, 17.49) * mm});
            skLineSegment(sketch, "E3393", {"start": v(-3.79, 17.49) * mm, "end": v(-3.82, 17.5) * mm});
            skLineSegment(sketch, "E3394", {"start": v(-3.82, 17.5) * mm, "end": v(-3.85, 17.52) * mm});
            skLineSegment(sketch, "E3395", {"start": v(-3.85, 17.52) * mm, "end": v(-4, 17.76) * mm});
            skLineSegment(sketch, "E3396", {"start": v(-4, 17.76) * mm, "end": v(-4, 17.83) * mm});
            skLineSegment(sketch, "E3397", {"start": v(-4, 17.83) * mm, "end": v(-4, 17.9) * mm});
            skLineSegment(sketch, "E3398", {"start": v(-4, 17.9) * mm, "end": v(-3.9, 18.1) * mm});
            skLineSegment(sketch, "E3399", {"start": v(-3.9, 18.1) * mm, "end": v(-3.7, 18.21) * mm});
            skLineSegment(sketch, "E3400", {"start": v(-3.7, 18.21) * mm, "end": v(-3.63, 18.21) * mm});
            skLineSegment(sketch, "E3401", {"start": v(-3.63, 18.21) * mm, "end": v(-3.56, 18.21) * mm});
            skLineSegment(sketch, "E3402", {"start": v(-3.56, 18.21) * mm, "end": v(-3.36, 18.1) * mm});
            skLineSegment(sketch, "E3403", {"start": v(-3.36, 18.1) * mm, "end": v(-3.25, 17.9) * mm});
            skLineSegment(sketch, "E3404", {"start": v(-3.25, 17.9) * mm, "end": v(-3.25, 17.83) * mm});
            skLineSegment(sketch, "E3405", {"start": v(-20.7, 16.18) * mm, "end": v(-20.7, 16.1) * mm});
            skLineSegment(sketch, "E3406", {"start": v(-20.7, 16.1) * mm, "end": v(-20.87, 15.87) * mm});
            skLineSegment(sketch, "E3407", {"start": v(-20.87, 15.87) * mm, "end": v(-20.9, 15.85) * mm});
            skLineSegment(sketch, "E3408", {"start": v(-20.9, 15.85) * mm, "end": v(-20.93, 15.84) * mm});
            skLineSegment(sketch, "E3409", {"start": v(-20.93, 15.84) * mm, "end": v(-21.25, 15.84) * mm});
            skLineSegment(sketch, "E3410", {"start": v(-21.25, 15.84) * mm, "end": v(-21.28, 15.85) * mm});
            skLineSegment(sketch, "E3411", {"start": v(-21.28, 15.85) * mm, "end": v(-21.31, 15.87) * mm});
            skLineSegment(sketch, "E3412", {"start": v(-21.31, 15.87) * mm, "end": v(-21.47, 16.1) * mm});
            skLineSegment(sketch, "E3413", {"start": v(-21.47, 16.1) * mm, "end": v(-21.47, 16.18) * mm});
            skLineSegment(sketch, "E3414", {"start": v(-21.47, 16.18) * mm, "end": v(-21.47, 16.26) * mm});
            skLineSegment(sketch, "E3415", {"start": v(-21.47, 16.26) * mm, "end": v(-21.31, 16.5) * mm});
            skLineSegment(sketch, "E3416", {"start": v(-21.31, 16.5) * mm, "end": v(-21.28, 16.51) * mm});
            skLineSegment(sketch, "E3417", {"start": v(-21.28, 16.51) * mm, "end": v(-21.25, 16.53) * mm});
            skLineSegment(sketch, "E3418", {"start": v(-21.25, 16.53) * mm, "end": v(-20.93, 16.53) * mm});
            skLineSegment(sketch, "E3419", {"start": v(-20.93, 16.53) * mm, "end": v(-20.9, 16.51) * mm});
            skLineSegment(sketch, "E3420", {"start": v(-20.9, 16.51) * mm, "end": v(-20.87, 16.5) * mm});
            skLineSegment(sketch, "E3421", {"start": v(-20.87, 16.5) * mm, "end": v(-20.7, 16.26) * mm});
            skLineSegment(sketch, "E3422", {"start": v(-20.7, 16.26) * mm, "end": v(-20.7, 16.18) * mm});
            skLineSegment(sketch, "E3423", {"start": v(-12.07, 14.66) * mm, "end": v(-12.07, 14.58) * mm});
            skLineSegment(sketch, "E3424", {"start": v(-12.07, 14.58) * mm, "end": v(-12.23, 14.35) * mm});
            skLineSegment(sketch, "E3425", {"start": v(-12.23, 14.35) * mm, "end": v(-12.26, 14.33) * mm});
            skLineSegment(sketch, "E3426", {"start": v(-12.26, 14.33) * mm, "end": v(-12.3, 14.31) * mm});
            skLineSegment(sketch, "E3427", {"start": v(-12.3, 14.31) * mm, "end": v(-12.62, 14.31) * mm});
            skLineSegment(sketch, "E3428", {"start": v(-12.62, 14.31) * mm, "end": v(-12.64, 14.33) * mm});
            skLineSegment(sketch, "E3429", {"start": v(-12.64, 14.33) * mm, "end": v(-12.67, 14.35) * mm});
            skLineSegment(sketch, "E3430", {"start": v(-12.67, 14.35) * mm, "end": v(-12.83, 14.58) * mm});
            skLineSegment(sketch, "E3431", {"start": v(-12.83, 14.58) * mm, "end": v(-12.83, 14.66) * mm});
            skLineSegment(sketch, "E3432", {"start": v(-12.83, 14.66) * mm, "end": v(-12.83, 14.74) * mm});
            skLineSegment(sketch, "E3433", {"start": v(-12.83, 14.74) * mm, "end": v(-12.67, 14.97) * mm});
            skLineSegment(sketch, "E3434", {"start": v(-12.67, 14.97) * mm, "end": v(-12.64, 14.99) * mm});
            skLineSegment(sketch, "E3435", {"start": v(-12.64, 14.99) * mm, "end": v(-12.62, 15) * mm});
            skLineSegment(sketch, "E3436", {"start": v(-12.62, 15) * mm, "end": v(-12.3, 15) * mm});
            skLineSegment(sketch, "E3437", {"start": v(-12.3, 15) * mm, "end": v(-12.26, 14.99) * mm});
            skLineSegment(sketch, "E3438", {"start": v(-12.26, 14.99) * mm, "end": v(-12.23, 14.97) * mm});
            skLineSegment(sketch, "E3439", {"start": v(-12.23, 14.97) * mm, "end": v(-12.07, 14.74) * mm});
            skLineSegment(sketch, "E3440", {"start": v(-12.07, 14.74) * mm, "end": v(-12.07, 14.66) * mm});
            skLineSegment(sketch, "E3441", {"start": v(-7.5, 17.13) * mm, "end": v(-7.5, 17.05) * mm});
            skLineSegment(sketch, "E3442", {"start": v(-7.5, 17.05) * mm, "end": v(-7.66, 16.82) * mm});
            skLineSegment(sketch, "E3443", {"start": v(-7.66, 16.82) * mm, "end": v(-7.69, 16.8) * mm});
            skLineSegment(sketch, "E3444", {"start": v(-7.69, 16.8) * mm, "end": v(-7.72, 16.79) * mm});
            skLineSegment(sketch, "E3445", {"start": v(-7.72, 16.79) * mm, "end": v(-8.04, 16.79) * mm});
            skLineSegment(sketch, "E3446", {"start": v(-8.04, 16.79) * mm, "end": v(-8.07, 16.8) * mm});
            skLineSegment(sketch, "E3447", {"start": v(-8.07, 16.8) * mm, "end": v(-8.1, 16.82) * mm});
            skLineSegment(sketch, "E3448", {"start": v(-8.1, 16.82) * mm, "end": v(-8.26, 17.06) * mm});
            skLineSegment(sketch, "E3449", {"start": v(-8.26, 17.06) * mm, "end": v(-8.26, 17.13) * mm});
            skLineSegment(sketch, "E3450", {"start": v(-8.26, 17.13) * mm, "end": v(-8.26, 17.22) * mm});
            skLineSegment(sketch, "E3451", {"start": v(-8.26, 17.22) * mm, "end": v(-8.1, 17.45) * mm});
            skLineSegment(sketch, "E3452", {"start": v(-8.1, 17.45) * mm, "end": v(-8.07, 17.46) * mm});
            skLineSegment(sketch, "E3453", {"start": v(-8.07, 17.46) * mm, "end": v(-8.04, 17.48) * mm});
            skLineSegment(sketch, "E3454", {"start": v(-8.04, 17.48) * mm, "end": v(-7.72, 17.48) * mm});
            skLineSegment(sketch, "E3455", {"start": v(-7.72, 17.48) * mm, "end": v(-7.69, 17.46) * mm});
            skLineSegment(sketch, "E3456", {"start": v(-7.69, 17.46) * mm, "end": v(-7.66, 17.45) * mm});
            skLineSegment(sketch, "E3457", {"start": v(-7.66, 17.45) * mm, "end": v(-7.5, 17.21) * mm});
            skLineSegment(sketch, "E3458", {"start": v(-7.5, 17.21) * mm, "end": v(-7.5, 17.13) * mm});
            skLineSegment(sketch, "E3459", {"start": v(-11.06, 18.98) * mm, "end": v(-11.06, 18.9) * mm});
            skLineSegment(sketch, "E3460", {"start": v(-11.06, 18.9) * mm, "end": v(-11.22, 18.66) * mm});
            skLineSegment(sketch, "E3461", {"start": v(-11.22, 18.66) * mm, "end": v(-11.25, 18.65) * mm});
            skLineSegment(sketch, "E3462", {"start": v(-11.25, 18.65) * mm, "end": v(-11.28, 18.63) * mm});
            skLineSegment(sketch, "E3463", {"start": v(-11.28, 18.63) * mm, "end": v(-11.6, 18.63) * mm});
            skLineSegment(sketch, "E3464", {"start": v(-11.6, 18.63) * mm, "end": v(-11.63, 18.65) * mm});
            skLineSegment(sketch, "E3465", {"start": v(-11.63, 18.65) * mm, "end": v(-11.66, 18.66) * mm});
            skLineSegment(sketch, "E3466", {"start": v(-11.66, 18.66) * mm, "end": v(-11.82, 18.9) * mm});
            skLineSegment(sketch, "E3467", {"start": v(-11.82, 18.9) * mm, "end": v(-11.82, 18.98) * mm});
            skLineSegment(sketch, "E3468", {"start": v(-11.82, 18.98) * mm, "end": v(-11.82, 19.04) * mm});
            skLineSegment(sketch, "E3469", {"start": v(-11.82, 19.04) * mm, "end": v(-11.7, 19.25) * mm});
            skLineSegment(sketch, "E3470", {"start": v(-11.7, 19.25) * mm, "end": v(-11.5, 19.36) * mm});
            skLineSegment(sketch, "E3471", {"start": v(-11.5, 19.36) * mm, "end": v(-11.44, 19.36) * mm});
            skLineSegment(sketch, "E3472", {"start": v(-11.44, 19.36) * mm, "end": v(-11.37, 19.36) * mm});
            skLineSegment(sketch, "E3473", {"start": v(-11.37, 19.36) * mm, "end": v(-11.17, 19.25) * mm});
            skLineSegment(sketch, "E3474", {"start": v(-11.17, 19.25) * mm, "end": v(-11.06, 19.04) * mm});
            skLineSegment(sketch, "E3475", {"start": v(-11.06, 19.04) * mm, "end": v(-11.06, 18.98) * mm});
            skLineSegment(sketch, "E3476", {"start": v(-6.3, 18.91) * mm, "end": v(-6.3, 18.83) * mm});
            skLineSegment(sketch, "E3477", {"start": v(-6.3, 18.83) * mm, "end": v(-6.46, 18.6) * mm});
            skLineSegment(sketch, "E3478", {"start": v(-6.46, 18.6) * mm, "end": v(-6.48, 18.58) * mm});
            skLineSegment(sketch, "E3479", {"start": v(-6.48, 18.58) * mm, "end": v(-6.51, 18.57) * mm});
            skLineSegment(sketch, "E3480", {"start": v(-6.51, 18.57) * mm, "end": v(-6.84, 18.57) * mm});
            skLineSegment(sketch, "E3481", {"start": v(-6.84, 18.57) * mm, "end": v(-6.86, 18.58) * mm});
            skLineSegment(sketch, "E3482", {"start": v(-6.86, 18.58) * mm, "end": v(-6.9, 18.6) * mm});
            skLineSegment(sketch, "E3483", {"start": v(-6.9, 18.6) * mm, "end": v(-7.06, 18.84) * mm});
            skLineSegment(sketch, "E3484", {"start": v(-7.06, 18.84) * mm, "end": v(-7.06, 18.91) * mm});
            skLineSegment(sketch, "E3485", {"start": v(-7.06, 18.91) * mm, "end": v(-7.06, 18.98) * mm});
            skLineSegment(sketch, "E3486", {"start": v(-7.06, 18.98) * mm, "end": v(-6.94, 19.18) * mm});
            skLineSegment(sketch, "E3487", {"start": v(-6.94, 19.18) * mm, "end": v(-6.74, 19.3) * mm});
            skLineSegment(sketch, "E3488", {"start": v(-6.74, 19.3) * mm, "end": v(-6.67, 19.3) * mm});
            skLineSegment(sketch, "E3489", {"start": v(-6.67, 19.3) * mm, "end": v(-6.6, 19.3) * mm});
            skLineSegment(sketch, "E3490", {"start": v(-6.6, 19.3) * mm, "end": v(-6.4, 19.18) * mm});
            skLineSegment(sketch, "E3491", {"start": v(-6.4, 19.18) * mm, "end": v(-6.3, 18.98) * mm});
            skLineSegment(sketch, "E3492", {"start": v(-6.3, 18.98) * mm, "end": v(-6.3, 18.91) * mm});
            skLineSegment(sketch, "E3493", {"start": v(12.95, 22.66) * mm, "end": v(12.95, 22.58) * mm});
            skLineSegment(sketch, "E3494", {"start": v(12.95, 22.58) * mm, "end": v(12.78, 22.35) * mm});
            skLineSegment(sketch, "E3495", {"start": v(12.78, 22.35) * mm, "end": v(12.76, 22.33) * mm});
            skLineSegment(sketch, "E3496", {"start": v(12.76, 22.33) * mm, "end": v(12.73, 22.31) * mm});
            skLineSegment(sketch, "E3497", {"start": v(12.73, 22.31) * mm, "end": v(12.4, 22.31) * mm});
            skLineSegment(sketch, "E3498", {"start": v(12.4, 22.31) * mm, "end": v(12.38, 22.33) * mm});
            skLineSegment(sketch, "E3499", {"start": v(12.38, 22.33) * mm, "end": v(12.35, 22.35) * mm});
            skLineSegment(sketch, "E3500", {"start": v(12.35, 22.35) * mm, "end": v(12.19, 22.58) * mm});
            skLineSegment(sketch, "E3501", {"start": v(12.19, 22.58) * mm, "end": v(12.19, 22.66) * mm});
            skLineSegment(sketch, "E3502", {"start": v(12.19, 22.66) * mm, "end": v(12.19, 22.73) * mm});
            skLineSegment(sketch, "E3503", {"start": v(12.19, 22.73) * mm, "end": v(12.3, 22.93) * mm});
            skLineSegment(sketch, "E3504", {"start": v(12.3, 22.93) * mm, "end": v(12.5, 23.04) * mm});
            skLineSegment(sketch, "E3505", {"start": v(12.5, 23.04) * mm, "end": v(12.57, 23.04) * mm});
            skLineSegment(sketch, "E3506", {"start": v(12.57, 23.04) * mm, "end": v(12.63, 23.04) * mm});
            skLineSegment(sketch, "E3507", {"start": v(12.63, 23.04) * mm, "end": v(12.83, 22.93) * mm});
            skLineSegment(sketch, "E3508", {"start": v(12.83, 22.93) * mm, "end": v(12.95, 22.73) * mm});
            skLineSegment(sketch, "E3509", {"start": v(12.95, 22.73) * mm, "end": v(12.95, 22.66) * mm});
            skLineSegment(sketch, "E3510", {"start": v(-8.83, 22.21) * mm, "end": v(-8.83, 22.13) * mm});
            skLineSegment(sketch, "E3511", {"start": v(-8.83, 22.13) * mm, "end": v(-9, 21.9) * mm});
            skLineSegment(sketch, "E3512", {"start": v(-9, 21.9) * mm, "end": v(-9.02, 21.88) * mm});
            skLineSegment(sketch, "E3513", {"start": v(-9.02, 21.88) * mm, "end": v(-9.05, 21.87) * mm});
            skLineSegment(sketch, "E3514", {"start": v(-9.05, 21.87) * mm, "end": v(-9.38, 21.87) * mm});
            skLineSegment(sketch, "E3515", {"start": v(-9.38, 21.87) * mm, "end": v(-9.4, 21.88) * mm});
            skLineSegment(sketch, "E3516", {"start": v(-9.4, 21.88) * mm, "end": v(-9.44, 21.9) * mm});
            skLineSegment(sketch, "E3517", {"start": v(-9.44, 21.9) * mm, "end": v(-9.6, 22.14) * mm});
            skLineSegment(sketch, "E3518", {"start": v(-9.6, 22.14) * mm, "end": v(-9.6, 22.21) * mm});
            skLineSegment(sketch, "E3519", {"start": v(-9.6, 22.21) * mm, "end": v(-9.6, 22.3) * mm});
            skLineSegment(sketch, "E3520", {"start": v(-9.6, 22.3) * mm, "end": v(-9.44, 22.53) * mm});
            skLineSegment(sketch, "E3521", {"start": v(-9.44, 22.53) * mm, "end": v(-9.4, 22.54) * mm});
            skLineSegment(sketch, "E3522", {"start": v(-9.4, 22.54) * mm, "end": v(-9.38, 22.56) * mm});
            skLineSegment(sketch, "E3523", {"start": v(-9.38, 22.56) * mm, "end": v(-9.05, 22.56) * mm});
            skLineSegment(sketch, "E3524", {"start": v(-9.05, 22.56) * mm, "end": v(-9.02, 22.54) * mm});
            skLineSegment(sketch, "E3525", {"start": v(-9.02, 22.54) * mm, "end": v(-9, 22.53) * mm});
            skLineSegment(sketch, "E3526", {"start": v(-9, 22.53) * mm, "end": v(-8.83, 22.3) * mm});
            skLineSegment(sketch, "E3527", {"start": v(-8.83, 22.3) * mm, "end": v(-8.83, 22.21) * mm});
            skLineSegment(sketch, "E3528", {"start": v(-12.39, 21.7) * mm, "end": v(-12.39, 21.62) * mm});
            skLineSegment(sketch, "E3529", {"start": v(-12.39, 21.62) * mm, "end": v(-12.55, 21.4) * mm});
            skLineSegment(sketch, "E3530", {"start": v(-12.55, 21.4) * mm, "end": v(-12.58, 21.38) * mm});
            skLineSegment(sketch, "E3531", {"start": v(-12.58, 21.38) * mm, "end": v(-12.61, 21.36) * mm});
            skLineSegment(sketch, "E3532", {"start": v(-12.61, 21.36) * mm, "end": v(-12.93, 21.36) * mm});
            skLineSegment(sketch, "E3533", {"start": v(-12.93, 21.36) * mm, "end": v(-12.96, 21.38) * mm});
            skLineSegment(sketch, "E3534", {"start": v(-12.96, 21.38) * mm, "end": v(-13, 21.4) * mm});
            skLineSegment(sketch, "E3535", {"start": v(-13, 21.4) * mm, "end": v(-13.15, 21.63) * mm});
            skLineSegment(sketch, "E3536", {"start": v(-13.15, 21.63) * mm, "end": v(-13.15, 21.7) * mm});
            skLineSegment(sketch, "E3537", {"start": v(-13.15, 21.7) * mm, "end": v(-13.15, 21.77) * mm});
            skLineSegment(sketch, "E3538", {"start": v(-13.15, 21.77) * mm, "end": v(-13.04, 21.98) * mm});
            skLineSegment(sketch, "E3539", {"start": v(-13.04, 21.98) * mm, "end": v(-12.84, 22.09) * mm});
            skLineSegment(sketch, "E3540", {"start": v(-12.84, 22.09) * mm, "end": v(-12.77, 22.09) * mm});
            skLineSegment(sketch, "E3541", {"start": v(-12.77, 22.09) * mm, "end": v(-12.7, 22.09) * mm});
            skLineSegment(sketch, "E3542", {"start": v(-12.7, 22.09) * mm, "end": v(-12.5, 21.98) * mm});
            skLineSegment(sketch, "E3543", {"start": v(-12.5, 21.98) * mm, "end": v(-12.39, 21.77) * mm});
            skLineSegment(sketch, "E3544", {"start": v(-12.39, 21.77) * mm, "end": v(-12.39, 21.7) * mm});
            skLineSegment(sketch, "E3545", {"start": v(-22.36, 21.7) * mm, "end": v(-22.36, 21.62) * mm});
            skLineSegment(sketch, "E3546", {"start": v(-22.36, 21.62) * mm, "end": v(-22.52, 21.4) * mm});
            skLineSegment(sketch, "E3547", {"start": v(-22.52, 21.4) * mm, "end": v(-22.55, 21.38) * mm});
            skLineSegment(sketch, "E3548", {"start": v(-22.55, 21.38) * mm, "end": v(-22.58, 21.36) * mm});
            skLineSegment(sketch, "E3549", {"start": v(-22.58, 21.36) * mm, "end": v(-22.9, 21.36) * mm});
            skLineSegment(sketch, "E3550", {"start": v(-22.9, 21.36) * mm, "end": v(-22.93, 21.38) * mm});
            skLineSegment(sketch, "E3551", {"start": v(-22.93, 21.38) * mm, "end": v(-22.96, 21.4) * mm});
            skLineSegment(sketch, "E3552", {"start": v(-22.96, 21.4) * mm, "end": v(-23.12, 21.63) * mm});
            skLineSegment(sketch, "E3553", {"start": v(-23.12, 21.63) * mm, "end": v(-23.12, 21.7) * mm});
            skLineSegment(sketch, "E3554", {"start": v(-23.12, 21.7) * mm, "end": v(-23.12, 21.79) * mm});
            skLineSegment(sketch, "E3555", {"start": v(-23.12, 21.79) * mm, "end": v(-22.96, 22.02) * mm});
            skLineSegment(sketch, "E3556", {"start": v(-22.96, 22.02) * mm, "end": v(-22.93, 22.04) * mm});
            skLineSegment(sketch, "E3557", {"start": v(-22.93, 22.04) * mm, "end": v(-22.9, 22.05) * mm});
            skLineSegment(sketch, "E3558", {"start": v(-22.9, 22.05) * mm, "end": v(-22.58, 22.05) * mm});
            skLineSegment(sketch, "E3559", {"start": v(-22.58, 22.05) * mm, "end": v(-22.55, 22.04) * mm});
            skLineSegment(sketch, "E3560", {"start": v(-22.55, 22.04) * mm, "end": v(-22.52, 22.02) * mm});
            skLineSegment(sketch, "E3561", {"start": v(-22.52, 22.02) * mm, "end": v(-22.36, 21.79) * mm});
            skLineSegment(sketch, "E3562", {"start": v(-22.36, 21.79) * mm, "end": v(-22.36, 21.7) * mm});
            skLineSegment(sketch, "E3563", {"start": v(-22.23, 19.67) * mm, "end": v(-22.23, 19.6) * mm});
            skLineSegment(sketch, "E3564", {"start": v(-22.23, 19.6) * mm, "end": v(-22.4, 19.36) * mm});
            skLineSegment(sketch, "E3565", {"start": v(-22.4, 19.36) * mm, "end": v(-22.42, 19.34) * mm});
            skLineSegment(sketch, "E3566", {"start": v(-22.42, 19.34) * mm, "end": v(-22.45, 19.33) * mm});
            skLineSegment(sketch, "E3567", {"start": v(-22.45, 19.33) * mm, "end": v(-22.78, 19.33) * mm});
            skLineSegment(sketch, "E3568", {"start": v(-22.78, 19.33) * mm, "end": v(-22.8, 19.34) * mm});
            skLineSegment(sketch, "E3569", {"start": v(-22.8, 19.34) * mm, "end": v(-22.83, 19.36) * mm});
            skLineSegment(sketch, "E3570", {"start": v(-22.83, 19.36) * mm, "end": v(-23, 19.6) * mm});
            skLineSegment(sketch, "E3571", {"start": v(-23, 19.6) * mm, "end": v(-23, 19.67) * mm});
            skLineSegment(sketch, "E3572", {"start": v(-23, 19.67) * mm, "end": v(-23, 19.76) * mm});
            skLineSegment(sketch, "E3573", {"start": v(-23, 19.76) * mm, "end": v(-22.83, 19.99) * mm});
            skLineSegment(sketch, "E3574", {"start": v(-22.83, 19.99) * mm, "end": v(-22.8, 20) * mm});
            skLineSegment(sketch, "E3575", {"start": v(-22.8, 20) * mm, "end": v(-22.78, 20.02) * mm});
            skLineSegment(sketch, "E3576", {"start": v(-22.78, 20.02) * mm, "end": v(-22.45, 20.02) * mm});
            skLineSegment(sketch, "E3577", {"start": v(-22.45, 20.02) * mm, "end": v(-22.42, 20) * mm});
            skLineSegment(sketch, "E3578", {"start": v(-22.42, 20) * mm, "end": v(-22.4, 19.99) * mm});
            skLineSegment(sketch, "E3579", {"start": v(-22.4, 19.99) * mm, "end": v(-22.23, 19.75) * mm});
            skLineSegment(sketch, "E3580", {"start": v(-22.23, 19.75) * mm, "end": v(-22.23, 19.67) * mm});
            skLineSegment(sketch, "E3581", {"start": v(-22.49, 23.42) * mm, "end": v(-22.49, 23.34) * mm});
            skLineSegment(sketch, "E3582", {"start": v(-22.49, 23.34) * mm, "end": v(-22.65, 23.1) * mm});
            skLineSegment(sketch, "E3583", {"start": v(-22.65, 23.1) * mm, "end": v(-22.68, 23.1) * mm});
            skLineSegment(sketch, "E3584", {"start": v(-22.68, 23.1) * mm, "end": v(-22.7, 23.07) * mm});
            skLineSegment(sketch, "E3585", {"start": v(-22.7, 23.07) * mm, "end": v(-23.03, 23.07) * mm});
            skLineSegment(sketch, "E3586", {"start": v(-23.03, 23.07) * mm, "end": v(-23.06, 23.1) * mm});
            skLineSegment(sketch, "E3587", {"start": v(-23.06, 23.1) * mm, "end": v(-23.09, 23.1) * mm});
            skLineSegment(sketch, "E3588", {"start": v(-23.09, 23.1) * mm, "end": v(-23.25, 23.34) * mm});
            skLineSegment(sketch, "E3589", {"start": v(-23.25, 23.34) * mm, "end": v(-23.25, 23.42) * mm});
            skLineSegment(sketch, "E3590", {"start": v(-23.25, 23.42) * mm, "end": v(-23.25, 23.49) * mm});
            skLineSegment(sketch, "E3591", {"start": v(-23.25, 23.49) * mm, "end": v(-23.14, 23.69) * mm});
            skLineSegment(sketch, "E3592", {"start": v(-23.14, 23.69) * mm, "end": v(-22.94, 23.8) * mm});
            skLineSegment(sketch, "E3593", {"start": v(-22.94, 23.8) * mm, "end": v(-22.87, 23.8) * mm});
            skLineSegment(sketch, "E3594", {"start": v(-22.87, 23.8) * mm, "end": v(-22.8, 23.8) * mm});
            skLineSegment(sketch, "E3595", {"start": v(-22.8, 23.8) * mm, "end": v(-22.6, 23.69) * mm});
            skLineSegment(sketch, "E3596", {"start": v(-22.6, 23.69) * mm, "end": v(-22.49, 23.49) * mm});
            skLineSegment(sketch, "E3597", {"start": v(-22.49, 23.49) * mm, "end": v(-22.49, 23.42) * mm});
            skLineSegment(sketch, "E3598", {"start": v(-52.56, 15.24) * mm, "end": v(-52.56, 15.12) * mm});
            skLineSegment(sketch, "E3599", {"start": v(-52.56, 15.12) * mm, "end": v(-52.7, 14.74) * mm});
            skLineSegment(sketch, "E3600", {"start": v(-52.7, 14.74) * mm, "end": v(-52.98, 14.42) * mm});
            skLineSegment(sketch, "E3601", {"start": v(-52.98, 14.42) * mm, "end": v(-53.06, 14.37) * mm});
            skLineSegment(sketch, "E3602", {"start": v(-53.06, 14.37) * mm, "end": v(-53.14, 14.33) * mm});
            skLineSegment(sketch, "E3603", {"start": v(-53.14, 14.33) * mm, "end": v(-53.56, 14.24) * mm});
            skLineSegment(sketch, "E3604", {"start": v(-53.56, 14.24) * mm, "end": v(-53.98, 14.33) * mm});
            skLineSegment(sketch, "E3605", {"start": v(-53.98, 14.33) * mm, "end": v(-54.06, 14.37) * mm});
            skLineSegment(sketch, "E3606", {"start": v(-54.06, 14.37) * mm, "end": v(-54.14, 14.42) * mm});
            skLineSegment(sketch, "E3607", {"start": v(-54.14, 14.42) * mm, "end": v(-54.42, 14.74) * mm});
            skLineSegment(sketch, "E3608", {"start": v(-54.42, 14.74) * mm, "end": v(-54.56, 15.12) * mm});
            skLineSegment(sketch, "E3609", {"start": v(-54.56, 15.12) * mm, "end": v(-54.56, 15.24) * mm});
            skLineSegment(sketch, "E3610", {"start": v(-54.56, 15.24) * mm, "end": v(-54.56, 15.37) * mm});
            skLineSegment(sketch, "E3611", {"start": v(-54.56, 15.37) * mm, "end": v(-54.42, 15.74) * mm});
            skLineSegment(sketch, "E3612", {"start": v(-54.42, 15.74) * mm, "end": v(-54.14, 16.06) * mm});
            skLineSegment(sketch, "E3613", {"start": v(-54.14, 16.06) * mm, "end": v(-54.06, 16.1) * mm});
            skLineSegment(sketch, "E3614", {"start": v(-54.06, 16.1) * mm, "end": v(-53.98, 16.15) * mm});
            skLineSegment(sketch, "E3615", {"start": v(-53.98, 16.15) * mm, "end": v(-53.56, 16.24) * mm});
            skLineSegment(sketch, "E3616", {"start": v(-53.56, 16.24) * mm, "end": v(-53.14, 16.15) * mm});
            skLineSegment(sketch, "E3617", {"start": v(-53.14, 16.15) * mm, "end": v(-53.06, 16.1) * mm});
            skLineSegment(sketch, "E3618", {"start": v(-53.06, 16.1) * mm, "end": v(-52.98, 16.06) * mm});
            skLineSegment(sketch, "E3619", {"start": v(-52.98, 16.06) * mm, "end": v(-52.7, 15.74) * mm});
            skLineSegment(sketch, "E3620", {"start": v(-52.7, 15.74) * mm, "end": v(-52.56, 15.37) * mm});
            skLineSegment(sketch, "E3621", {"start": v(-52.56, 15.37) * mm, "end": v(-52.56, 15.24) * mm});
            skLineSegment(sketch, "E3622", {"start": v(-52.56, 7.34) * mm, "end": v(-52.56, 7.22) * mm});
            skLineSegment(sketch, "E3623", {"start": v(-52.56, 7.22) * mm, "end": v(-52.7, 6.84) * mm});
            skLineSegment(sketch, "E3624", {"start": v(-52.7, 6.84) * mm, "end": v(-52.98, 6.52) * mm});
            skLineSegment(sketch, "E3625", {"start": v(-52.98, 6.52) * mm, "end": v(-53.06, 6.47) * mm});
            skLineSegment(sketch, "E3626", {"start": v(-53.06, 6.47) * mm, "end": v(-53.14, 6.43) * mm});
            skLineSegment(sketch, "E3627", {"start": v(-53.14, 6.43) * mm, "end": v(-53.56, 6.34) * mm});
            skLineSegment(sketch, "E3628", {"start": v(-53.56, 6.34) * mm, "end": v(-53.98, 6.43) * mm});
            skLineSegment(sketch, "E3629", {"start": v(-53.98, 6.43) * mm, "end": v(-54.06, 6.47) * mm});
            skLineSegment(sketch, "E3630", {"start": v(-54.06, 6.47) * mm, "end": v(-54.14, 6.52) * mm});
            skLineSegment(sketch, "E3631", {"start": v(-54.14, 6.52) * mm, "end": v(-54.42, 6.84) * mm});
            skLineSegment(sketch, "E3632", {"start": v(-54.42, 6.84) * mm, "end": v(-54.56, 7.22) * mm});
            skLineSegment(sketch, "E3633", {"start": v(-54.56, 7.22) * mm, "end": v(-54.56, 7.34) * mm});
            skLineSegment(sketch, "E3634", {"start": v(-54.56, 7.34) * mm, "end": v(-54.56, 7.46) * mm});
            skLineSegment(sketch, "E3635", {"start": v(-54.56, 7.46) * mm, "end": v(-54.42, 7.84) * mm});
            skLineSegment(sketch, "E3636", {"start": v(-54.42, 7.84) * mm, "end": v(-54.14, 8.16) * mm});
            skLineSegment(sketch, "E3637", {"start": v(-54.14, 8.16) * mm, "end": v(-54.06, 8.2) * mm});
            skLineSegment(sketch, "E3638", {"start": v(-54.06, 8.2) * mm, "end": v(-53.98, 8.25) * mm});
            skLineSegment(sketch, "E3639", {"start": v(-53.98, 8.25) * mm, "end": v(-53.56, 8.34) * mm});
            skLineSegment(sketch, "E3640", {"start": v(-53.56, 8.34) * mm, "end": v(-53.14, 8.25) * mm});
            skLineSegment(sketch, "E3641", {"start": v(-53.14, 8.25) * mm, "end": v(-53.06, 8.2) * mm});
            skLineSegment(sketch, "E3642", {"start": v(-53.06, 8.2) * mm, "end": v(-52.98, 8.16) * mm});
            skLineSegment(sketch, "E3643", {"start": v(-52.98, 8.16) * mm, "end": v(-52.7, 7.84) * mm});
            skLineSegment(sketch, "E3644", {"start": v(-52.7, 7.84) * mm, "end": v(-52.56, 7.46) * mm});
            skLineSegment(sketch, "E3645", {"start": v(-52.56, 7.46) * mm, "end": v(-52.56, 7.34) * mm});
            skLineSegment(sketch, "E3646", {"start": v(39.5, -40.64) * mm, "end": v(39.5, -40.76) * mm});
            skLineSegment(sketch, "E3647", {"start": v(39.5, -40.76) * mm, "end": v(39.4, -41.13) * mm});
            skLineSegment(sketch, "E3648", {"start": v(39.4, -41.13) * mm, "end": v(39.12, -41.52) * mm});
            skLineSegment(sketch, "E3649", {"start": v(39.12, -41.52) * mm, "end": v(38.73, -41.8) * mm});
            skLineSegment(sketch, "E3650", {"start": v(38.73, -41.8) * mm, "end": v(38.36, -41.89) * mm});
            skLineSegment(sketch, "E3651", {"start": v(38.36, -41.89) * mm, "end": v(38.24, -41.89) * mm});
            skLineSegment(sketch, "E3652", {"start": v(38.24, -41.89) * mm, "end": v(38.12, -41.89) * mm});
            skLineSegment(sketch, "E3653", {"start": v(38.12, -41.89) * mm, "end": v(37.75, -41.8) * mm});
            skLineSegment(sketch, "E3654", {"start": v(37.75, -41.8) * mm, "end": v(37.36, -41.52) * mm});
            skLineSegment(sketch, "E3655", {"start": v(37.36, -41.52) * mm, "end": v(37.09, -41.13) * mm});
            skLineSegment(sketch, "E3656", {"start": v(37.09, -41.13) * mm, "end": v(37, -40.76) * mm});
            skLineSegment(sketch, "E3657", {"start": v(37, -40.76) * mm, "end": v(37, -40.64) * mm});
            skLineSegment(sketch, "E3658", {"start": v(37, -40.64) * mm, "end": v(37, -40.48) * mm});
            skLineSegment(sketch, "E3659", {"start": v(37, -40.48) * mm, "end": v(37.16, -40.01) * mm});
            skLineSegment(sketch, "E3660", {"start": v(37.16, -40.01) * mm, "end": v(37.52, -39.61) * mm});
            skLineSegment(sketch, "E3661", {"start": v(37.52, -39.61) * mm, "end": v(37.62, -39.56) * mm});
            skLineSegment(sketch, "E3662", {"start": v(37.62, -39.56) * mm, "end": v(37.71, -39.5) * mm});
            skLineSegment(sketch, "E3663", {"start": v(37.71, -39.5) * mm, "end": v(38.24, -39.39) * mm});
            skLineSegment(sketch, "E3664", {"start": v(38.24, -39.39) * mm, "end": v(38.77, -39.5) * mm});
            skLineSegment(sketch, "E3665", {"start": v(38.77, -39.5) * mm, "end": v(38.87, -39.56) * mm});
            skLineSegment(sketch, "E3666", {"start": v(38.87, -39.56) * mm, "end": v(38.96, -39.61) * mm});
            skLineSegment(sketch, "E3667", {"start": v(38.96, -39.61) * mm, "end": v(39.32, -40.01) * mm});
            skLineSegment(sketch, "E3668", {"start": v(39.32, -40.01) * mm, "end": v(39.5, -40.48) * mm});
            skLineSegment(sketch, "E3669", {"start": v(39.5, -40.48) * mm, "end": v(39.5, -40.64) * mm});
            skLineSegment(sketch, "E3670", {"start": v(-36.7, -40.64) * mm, "end": v(-36.7, -40.8) * mm});
            skLineSegment(sketch, "E3671", {"start": v(-36.7, -40.8) * mm, "end": v(-36.88, -41.26) * mm});
            skLineSegment(sketch, "E3672", {"start": v(-36.88, -41.26) * mm, "end": v(-37.24, -41.67) * mm});
            skLineSegment(sketch, "E3673", {"start": v(-37.24, -41.67) * mm, "end": v(-37.33, -41.72) * mm});
            skLineSegment(sketch, "E3674", {"start": v(-37.33, -41.72) * mm, "end": v(-37.43, -41.78) * mm});
            skLineSegment(sketch, "E3675", {"start": v(-37.43, -41.78) * mm, "end": v(-37.96, -41.89) * mm});
            skLineSegment(sketch, "E3676", {"start": v(-37.96, -41.89) * mm, "end": v(-38.49, -41.78) * mm});
            skLineSegment(sketch, "E3677", {"start": v(-38.49, -41.78) * mm, "end": v(-38.58, -41.72) * mm});
            skLineSegment(sketch, "E3678", {"start": v(-38.58, -41.72) * mm, "end": v(-38.68, -41.67) * mm});
            skLineSegment(sketch, "E3679", {"start": v(-38.68, -41.67) * mm, "end": v(-39.04, -41.26) * mm});
            skLineSegment(sketch, "E3680", {"start": v(-39.04, -41.26) * mm, "end": v(-39.2, -40.8) * mm});
            skLineSegment(sketch, "E3681", {"start": v(-39.2, -40.8) * mm, "end": v(-39.2, -40.64) * mm});
            skLineSegment(sketch, "E3682", {"start": v(-39.2, -40.64) * mm, "end": v(-39.2, -40.48) * mm});
            skLineSegment(sketch, "E3683", {"start": v(-39.2, -40.48) * mm, "end": v(-39.04, -40.01) * mm});
            skLineSegment(sketch, "E3684", {"start": v(-39.04, -40.01) * mm, "end": v(-38.68, -39.61) * mm});
            skLineSegment(sketch, "E3685", {"start": v(-38.68, -39.61) * mm, "end": v(-38.58, -39.56) * mm});
            skLineSegment(sketch, "E3686", {"start": v(-38.58, -39.56) * mm, "end": v(-38.49, -39.5) * mm});
            skLineSegment(sketch, "E3687", {"start": v(-38.49, -39.5) * mm, "end": v(-37.96, -39.39) * mm});
            skLineSegment(sketch, "E3688", {"start": v(-37.96, -39.39) * mm, "end": v(-37.43, -39.5) * mm});
            skLineSegment(sketch, "E3689", {"start": v(-37.43, -39.5) * mm, "end": v(-37.33, -39.56) * mm});
            skLineSegment(sketch, "E3690", {"start": v(-37.33, -39.56) * mm, "end": v(-37.24, -39.61) * mm});
            skLineSegment(sketch, "E3691", {"start": v(-37.24, -39.61) * mm, "end": v(-36.88, -40.01) * mm});
            skLineSegment(sketch, "E3692", {"start": v(-36.88, -40.01) * mm, "end": v(-36.7, -40.48) * mm});
            skLineSegment(sketch, "E3693", {"start": v(-36.7, -40.48) * mm, "end": v(-36.7, -40.64) * mm});
            skLineSegment(sketch, "E3694", {"start": v(39.5, 35.56) * mm, "end": v(39.5, 35.44) * mm});
            skLineSegment(sketch, "E3695", {"start": v(39.5, 35.44) * mm, "end": v(39.4, 35.07) * mm});
            skLineSegment(sketch, "E3696", {"start": v(39.4, 35.07) * mm, "end": v(39.12, 34.68) * mm});
            skLineSegment(sketch, "E3697", {"start": v(39.12, 34.68) * mm, "end": v(38.73, 34.4) * mm});
            skLineSegment(sketch, "E3698", {"start": v(38.73, 34.4) * mm, "end": v(38.36, 34.31) * mm});
            skLineSegment(sketch, "E3699", {"start": v(38.36, 34.31) * mm, "end": v(38.24, 34.31) * mm});
            skLineSegment(sketch, "E3700", {"start": v(38.24, 34.31) * mm, "end": v(38.12, 34.31) * mm});
            skLineSegment(sketch, "E3701", {"start": v(38.12, 34.31) * mm, "end": v(37.75, 34.4) * mm});
            skLineSegment(sketch, "E3702", {"start": v(37.75, 34.4) * mm, "end": v(37.36, 34.68) * mm});
            skLineSegment(sketch, "E3703", {"start": v(37.36, 34.68) * mm, "end": v(37.09, 35.07) * mm});
            skLineSegment(sketch, "E3704", {"start": v(37.09, 35.07) * mm, "end": v(37, 35.44) * mm});
            skLineSegment(sketch, "E3705", {"start": v(37, 35.44) * mm, "end": v(37, 35.56) * mm});
            skLineSegment(sketch, "E3706", {"start": v(37, 35.56) * mm, "end": v(37, 35.72) * mm});
            skLineSegment(sketch, "E3707", {"start": v(37, 35.72) * mm, "end": v(37.16, 36.19) * mm});
            skLineSegment(sketch, "E3708", {"start": v(37.16, 36.19) * mm, "end": v(37.52, 36.59) * mm});
            skLineSegment(sketch, "E3709", {"start": v(37.52, 36.59) * mm, "end": v(37.62, 36.64) * mm});
            skLineSegment(sketch, "E3710", {"start": v(37.62, 36.64) * mm, "end": v(37.71, 36.7) * mm});
            skLineSegment(sketch, "E3711", {"start": v(37.71, 36.7) * mm, "end": v(38.24, 36.81) * mm});
            skLineSegment(sketch, "E3712", {"start": v(38.24, 36.81) * mm, "end": v(38.77, 36.7) * mm});
            skLineSegment(sketch, "E3713", {"start": v(38.77, 36.7) * mm, "end": v(38.87, 36.64) * mm});
            skLineSegment(sketch, "E3714", {"start": v(38.87, 36.64) * mm, "end": v(38.96, 36.59) * mm});
            skLineSegment(sketch, "E3715", {"start": v(38.96, 36.59) * mm, "end": v(39.32, 36.19) * mm});
            skLineSegment(sketch, "E3716", {"start": v(39.32, 36.19) * mm, "end": v(39.5, 35.72) * mm});
            skLineSegment(sketch, "E3717", {"start": v(39.5, 35.72) * mm, "end": v(39.5, 35.56) * mm});
            skLineSegment(sketch, "E3718", {"start": v(51.3, 23.26) * mm, "end": v(51.3, 23.12) * mm});
            skLineSegment(sketch, "E3719", {"start": v(51.3, 23.12) * mm, "end": v(51.16, 22.71) * mm});
            skLineSegment(sketch, "E3720", {"start": v(51.16, 22.71) * mm, "end": v(50.84, 22.36) * mm});
            skLineSegment(sketch, "E3721", {"start": v(50.84, 22.36) * mm, "end": v(50.75, 22.3) * mm});
            skLineSegment(sketch, "E3722", {"start": v(50.75, 22.3) * mm, "end": v(50.67, 22.26) * mm});
            skLineSegment(sketch, "E3723", {"start": v(50.67, 22.26) * mm, "end": v(50.2, 22.16) * mm});
            skLineSegment(sketch, "E3724", {"start": v(50.2, 22.16) * mm, "end": v(49.74, 22.26) * mm});
            skLineSegment(sketch, "E3725", {"start": v(49.74, 22.26) * mm, "end": v(49.65, 22.3) * mm});
            skLineSegment(sketch, "E3726", {"start": v(49.65, 22.3) * mm, "end": v(49.57, 22.36) * mm});
            skLineSegment(sketch, "E3727", {"start": v(49.57, 22.36) * mm, "end": v(49.25, 22.71) * mm});
            skLineSegment(sketch, "E3728", {"start": v(49.25, 22.71) * mm, "end": v(49.1, 23.12) * mm});
            skLineSegment(sketch, "E3729", {"start": v(49.1, 23.12) * mm, "end": v(49.1, 23.26) * mm});
            skLineSegment(sketch, "E3730", {"start": v(49.1, 23.26) * mm, "end": v(49.1, 23.4) * mm});
            skLineSegment(sketch, "E3731", {"start": v(49.1, 23.4) * mm, "end": v(49.25, 23.8) * mm});
            skLineSegment(sketch, "E3732", {"start": v(49.25, 23.8) * mm, "end": v(49.57, 24.16) * mm});
            skLineSegment(sketch, "E3733", {"start": v(49.57, 24.16) * mm, "end": v(49.65, 24.21) * mm});
            skLineSegment(sketch, "E3734", {"start": v(49.65, 24.21) * mm, "end": v(49.74, 24.26) * mm});
            skLineSegment(sketch, "E3735", {"start": v(49.74, 24.26) * mm, "end": v(50.2, 24.36) * mm});
            skLineSegment(sketch, "E3736", {"start": v(50.2, 24.36) * mm, "end": v(50.67, 24.26) * mm});
            skLineSegment(sketch, "E3737", {"start": v(50.67, 24.26) * mm, "end": v(50.75, 24.21) * mm});
            skLineSegment(sketch, "E3738", {"start": v(50.75, 24.21) * mm, "end": v(50.84, 24.16) * mm});
            skLineSegment(sketch, "E3739", {"start": v(50.84, 24.16) * mm, "end": v(51.16, 23.8) * mm});
            skLineSegment(sketch, "E3740", {"start": v(51.16, 23.8) * mm, "end": v(51.3, 23.4) * mm});
            skLineSegment(sketch, "E3741", {"start": v(51.3, 23.4) * mm, "end": v(51.3, 23.26) * mm});
            skLineSegment(sketch, "E3742", {"start": v(51.3, 13.06) * mm, "end": v(51.3, 12.92) * mm});
            skLineSegment(sketch, "E3743", {"start": v(51.3, 12.92) * mm, "end": v(51.16, 12.51) * mm});
            skLineSegment(sketch, "E3744", {"start": v(51.16, 12.51) * mm, "end": v(50.84, 12.16) * mm});
            skLineSegment(sketch, "E3745", {"start": v(50.84, 12.16) * mm, "end": v(50.75, 12.1) * mm});
            skLineSegment(sketch, "E3746", {"start": v(50.75, 12.1) * mm, "end": v(50.67, 12.06) * mm});
            skLineSegment(sketch, "E3747", {"start": v(50.67, 12.06) * mm, "end": v(50.2, 11.96) * mm});
            skLineSegment(sketch, "E3748", {"start": v(50.2, 11.96) * mm, "end": v(49.74, 12.06) * mm});
            skLineSegment(sketch, "E3749", {"start": v(49.74, 12.06) * mm, "end": v(49.65, 12.1) * mm});
            skLineSegment(sketch, "E3750", {"start": v(49.65, 12.1) * mm, "end": v(49.57, 12.16) * mm});
            skLineSegment(sketch, "E3751", {"start": v(49.57, 12.16) * mm, "end": v(49.25, 12.51) * mm});
            skLineSegment(sketch, "E3752", {"start": v(49.25, 12.51) * mm, "end": v(49.1, 12.92) * mm});
            skLineSegment(sketch, "E3753", {"start": v(49.1, 12.92) * mm, "end": v(49.1, 13.06) * mm});
            skLineSegment(sketch, "E3754", {"start": v(49.1, 13.06) * mm, "end": v(49.1, 13.2) * mm});
            skLineSegment(sketch, "E3755", {"start": v(49.1, 13.2) * mm, "end": v(49.25, 13.61) * mm});
            skLineSegment(sketch, "E3756", {"start": v(49.25, 13.61) * mm, "end": v(49.57, 13.96) * mm});
            skLineSegment(sketch, "E3757", {"start": v(49.57, 13.96) * mm, "end": v(49.65, 14.01) * mm});
            skLineSegment(sketch, "E3758", {"start": v(49.65, 14.01) * mm, "end": v(49.74, 14.06) * mm});
            skLineSegment(sketch, "E3759", {"start": v(49.74, 14.06) * mm, "end": v(50.2, 14.16) * mm});
            skLineSegment(sketch, "E3760", {"start": v(50.2, 14.16) * mm, "end": v(50.67, 14.06) * mm});
            skLineSegment(sketch, "E3761", {"start": v(50.67, 14.06) * mm, "end": v(50.75, 14.01) * mm});
            skLineSegment(sketch, "E3762", {"start": v(50.75, 14.01) * mm, "end": v(50.84, 13.96) * mm});
            skLineSegment(sketch, "E3763", {"start": v(50.84, 13.96) * mm, "end": v(51.16, 13.61) * mm});
            skLineSegment(sketch, "E3764", {"start": v(51.16, 13.61) * mm, "end": v(51.3, 13.2) * mm});
            skLineSegment(sketch, "E3765", {"start": v(51.3, 13.2) * mm, "end": v(51.3, 13.06) * mm});
            skLineSegment(sketch, "E3766", {"start": v(46.44, 18.16) * mm, "end": v(46.44, 18.05) * mm});
            skLineSegment(sketch, "E3767", {"start": v(46.44, 18.05) * mm, "end": v(46.23, 17.75) * mm});
            skLineSegment(sketch, "E3768", {"start": v(46.23, 17.75) * mm, "end": v(46.19, 17.73) * mm});
            skLineSegment(sketch, "E3769", {"start": v(46.19, 17.73) * mm, "end": v(46.15, 17.7) * mm});
            skLineSegment(sketch, "E3770", {"start": v(46.15, 17.7) * mm, "end": v(45.73, 17.7) * mm});
            skLineSegment(sketch, "E3771", {"start": v(45.73, 17.7) * mm, "end": v(45.69, 17.73) * mm});
            skLineSegment(sketch, "E3772", {"start": v(45.69, 17.73) * mm, "end": v(45.65, 17.75) * mm});
            skLineSegment(sketch, "E3773", {"start": v(45.65, 17.75) * mm, "end": v(45.44, 18.06) * mm});
            skLineSegment(sketch, "E3774", {"start": v(45.44, 18.06) * mm, "end": v(45.44, 18.16) * mm});
            skLineSegment(sketch, "E3775", {"start": v(45.44, 18.16) * mm, "end": v(45.44, 18.27) * mm});
            skLineSegment(sketch, "E3776", {"start": v(45.44, 18.27) * mm, "end": v(45.65, 18.57) * mm});
            skLineSegment(sketch, "E3777", {"start": v(45.65, 18.57) * mm, "end": v(45.69, 18.6) * mm});
            skLineSegment(sketch, "E3778", {"start": v(45.69, 18.6) * mm, "end": v(45.73, 18.62) * mm});
            skLineSegment(sketch, "E3779", {"start": v(45.73, 18.62) * mm, "end": v(46.15, 18.62) * mm});
            skLineSegment(sketch, "E3780", {"start": v(46.15, 18.62) * mm, "end": v(46.19, 18.6) * mm});
            skLineSegment(sketch, "E3781", {"start": v(46.19, 18.6) * mm, "end": v(46.23, 18.57) * mm});
            skLineSegment(sketch, "E3782", {"start": v(46.23, 18.57) * mm, "end": v(46.44, 18.26) * mm});
            skLineSegment(sketch, "E3783", {"start": v(46.44, 18.26) * mm, "end": v(46.44, 18.16) * mm});
            skLineSegment(sketch, "E3784", {"start": v(46.44, 20.66) * mm, "end": v(46.44, 20.55) * mm});
            skLineSegment(sketch, "E3785", {"start": v(46.44, 20.55) * mm, "end": v(46.23, 20.25) * mm});
            skLineSegment(sketch, "E3786", {"start": v(46.23, 20.25) * mm, "end": v(46.19, 20.23) * mm});
            skLineSegment(sketch, "E3787", {"start": v(46.19, 20.23) * mm, "end": v(46.15, 20.2) * mm});
            skLineSegment(sketch, "E3788", {"start": v(46.15, 20.2) * mm, "end": v(45.73, 20.2) * mm});
            skLineSegment(sketch, "E3789", {"start": v(45.73, 20.2) * mm, "end": v(45.69, 20.23) * mm});
            skLineSegment(sketch, "E3790", {"start": v(45.69, 20.23) * mm, "end": v(45.65, 20.25) * mm});
            skLineSegment(sketch, "E3791", {"start": v(45.65, 20.25) * mm, "end": v(45.44, 20.56) * mm});
            skLineSegment(sketch, "E3792", {"start": v(45.44, 20.56) * mm, "end": v(45.44, 20.66) * mm});
            skLineSegment(sketch, "E3793", {"start": v(45.44, 20.66) * mm, "end": v(45.44, 20.77) * mm});
            skLineSegment(sketch, "E3794", {"start": v(45.44, 20.77) * mm, "end": v(45.65, 21.07) * mm});
            skLineSegment(sketch, "E3795", {"start": v(45.65, 21.07) * mm, "end": v(45.69, 21.1) * mm});
            skLineSegment(sketch, "E3796", {"start": v(45.69, 21.1) * mm, "end": v(45.73, 21.12) * mm});
            skLineSegment(sketch, "E3797", {"start": v(45.73, 21.12) * mm, "end": v(46.15, 21.12) * mm});
            skLineSegment(sketch, "E3798", {"start": v(46.15, 21.12) * mm, "end": v(46.19, 21.1) * mm});
            skLineSegment(sketch, "E3799", {"start": v(46.19, 21.1) * mm, "end": v(46.23, 21.07) * mm});
            skLineSegment(sketch, "E3800", {"start": v(46.23, 21.07) * mm, "end": v(46.44, 20.76) * mm});
            skLineSegment(sketch, "E3801", {"start": v(46.44, 20.76) * mm, "end": v(46.44, 20.66) * mm});
            skLineSegment(sketch, "E3802", {"start": v(21.15, -2.25) * mm, "end": v(21.15, -2.34) * mm});
            skLineSegment(sketch, "E3803", {"start": v(21.15, -2.34) * mm, "end": v(20.98, -2.58) * mm});
            skLineSegment(sketch, "E3804", {"start": v(20.98, -2.58) * mm, "end": v(20.95, -2.6) * mm});
            skLineSegment(sketch, "E3805", {"start": v(20.95, -2.6) * mm, "end": v(20.92, -2.62) * mm});
            skLineSegment(sketch, "E3806", {"start": v(20.92, -2.62) * mm, "end": v(20.58, -2.62) * mm});
            skLineSegment(sketch, "E3807", {"start": v(20.58, -2.62) * mm, "end": v(20.55, -2.6) * mm});
            skLineSegment(sketch, "E3808", {"start": v(20.55, -2.6) * mm, "end": v(20.52, -2.58) * mm});
            skLineSegment(sketch, "E3809", {"start": v(20.52, -2.58) * mm, "end": v(20.35, -2.34) * mm});
            skLineSegment(sketch, "E3810", {"start": v(20.35, -2.34) * mm, "end": v(20.35, -2.25) * mm});
            skLineSegment(sketch, "E3811", {"start": v(20.35, -2.25) * mm, "end": v(20.35, -2.17) * mm});
            skLineSegment(sketch, "E3812", {"start": v(20.35, -2.17) * mm, "end": v(20.52, -1.93) * mm});
            skLineSegment(sketch, "E3813", {"start": v(20.52, -1.93) * mm, "end": v(20.55, -1.9) * mm});
            skLineSegment(sketch, "E3814", {"start": v(20.55, -1.9) * mm, "end": v(20.58, -1.89) * mm});
            skLineSegment(sketch, "E3815", {"start": v(20.58, -1.89) * mm, "end": v(20.92, -1.89) * mm});
            skLineSegment(sketch, "E3816", {"start": v(20.92, -1.89) * mm, "end": v(20.95, -1.9) * mm});
            skLineSegment(sketch, "E3817", {"start": v(20.95, -1.9) * mm, "end": v(20.98, -1.93) * mm});
            skLineSegment(sketch, "E3818", {"start": v(20.98, -1.93) * mm, "end": v(21.15, -2.17) * mm});
            skLineSegment(sketch, "E3819", {"start": v(21.15, -2.17) * mm, "end": v(21.15, -2.25) * mm});
            skLineSegment(sketch, "E3820", {"start": v(-24.6, 23.72) * mm, "end": v(-24.6, 23.61) * mm});
            skLineSegment(sketch, "E3821", {"start": v(-24.6, 23.61) * mm, "end": v(-24.81, 23.3) * mm});
            skLineSegment(sketch, "E3822", {"start": v(-24.81, 23.3) * mm, "end": v(-24.85, 23.28) * mm});
            skLineSegment(sketch, "E3823", {"start": v(-24.85, 23.28) * mm, "end": v(-24.9, 23.26) * mm});
            skLineSegment(sketch, "E3824", {"start": v(-24.9, 23.26) * mm, "end": v(-25.32, 23.26) * mm});
            skLineSegment(sketch, "E3825", {"start": v(-25.32, 23.26) * mm, "end": v(-25.36, 23.28) * mm});
            skLineSegment(sketch, "E3826", {"start": v(-25.36, 23.28) * mm, "end": v(-25.4, 23.3) * mm});
            skLineSegment(sketch, "E3827", {"start": v(-25.4, 23.3) * mm, "end": v(-25.61, 23.62) * mm});
            skLineSegment(sketch, "E3828", {"start": v(-25.61, 23.62) * mm, "end": v(-25.61, 23.72) * mm});
            skLineSegment(sketch, "E3829", {"start": v(-25.61, 23.72) * mm, "end": v(-25.61, 23.83) * mm});
            skLineSegment(sketch, "E3830", {"start": v(-25.61, 23.83) * mm, "end": v(-25.4, 24.14) * mm});
            skLineSegment(sketch, "E3831", {"start": v(-25.4, 24.14) * mm, "end": v(-25.36, 24.16) * mm});
            skLineSegment(sketch, "E3832", {"start": v(-25.36, 24.16) * mm, "end": v(-25.32, 24.19) * mm});
            skLineSegment(sketch, "E3833", {"start": v(-25.32, 24.19) * mm, "end": v(-24.9, 24.19) * mm});
            skLineSegment(sketch, "E3834", {"start": v(-24.9, 24.19) * mm, "end": v(-24.85, 24.16) * mm});
            skLineSegment(sketch, "E3835", {"start": v(-24.85, 24.16) * mm, "end": v(-24.81, 24.14) * mm});
            skLineSegment(sketch, "E3836", {"start": v(-24.81, 24.14) * mm, "end": v(-24.6, 23.83) * mm});
            skLineSegment(sketch, "E3837", {"start": v(-24.6, 23.83) * mm, "end": v(-24.6, 23.72) * mm});
            skLineSegment(sketch, "E3838", {"start": v(-24.45, 14.58) * mm, "end": v(-24.45, 14.47) * mm});
            skLineSegment(sketch, "E3839", {"start": v(-24.45, 14.47) * mm, "end": v(-24.66, 14.16) * mm});
            skLineSegment(sketch, "E3840", {"start": v(-24.66, 14.16) * mm, "end": v(-24.7, 14.14) * mm});
            skLineSegment(sketch, "E3841", {"start": v(-24.7, 14.14) * mm, "end": v(-24.74, 14.12) * mm});
            skLineSegment(sketch, "E3842", {"start": v(-24.74, 14.12) * mm, "end": v(-25.17, 14.12) * mm});
            skLineSegment(sketch, "E3843", {"start": v(-25.17, 14.12) * mm, "end": v(-25.2, 14.14) * mm});
            skLineSegment(sketch, "E3844", {"start": v(-25.2, 14.14) * mm, "end": v(-25.25, 14.16) * mm});
            skLineSegment(sketch, "E3845", {"start": v(-25.25, 14.16) * mm, "end": v(-25.46, 14.48) * mm});
            skLineSegment(sketch, "E3846", {"start": v(-25.46, 14.48) * mm, "end": v(-25.46, 14.58) * mm});
            skLineSegment(sketch, "E3847", {"start": v(-25.46, 14.58) * mm, "end": v(-25.46, 14.7) * mm});
            skLineSegment(sketch, "E3848", {"start": v(-25.46, 14.7) * mm, "end": v(-25.25, 15) * mm});
            skLineSegment(sketch, "E3849", {"start": v(-25.25, 15) * mm, "end": v(-25.2, 15.02) * mm});
            skLineSegment(sketch, "E3850", {"start": v(-25.2, 15.02) * mm, "end": v(-25.17, 15.04) * mm});
            skLineSegment(sketch, "E3851", {"start": v(-25.17, 15.04) * mm, "end": v(-24.74, 15.04) * mm});
            skLineSegment(sketch, "E3852", {"start": v(-24.74, 15.04) * mm, "end": v(-24.7, 15.02) * mm});
            skLineSegment(sketch, "E3853", {"start": v(-24.7, 15.02) * mm, "end": v(-24.66, 15) * mm});
            skLineSegment(sketch, "E3854", {"start": v(-24.66, 15) * mm, "end": v(-24.45, 14.68) * mm});
            skLineSegment(sketch, "E3855", {"start": v(-24.45, 14.68) * mm, "end": v(-24.45, 14.58) * mm});
            skLineSegment(sketch, "E3856", {"start": v(-24.5, 11.74) * mm, "end": v(-24.5, 11.63) * mm});
            skLineSegment(sketch, "E3857", {"start": v(-24.5, 11.63) * mm, "end": v(-24.71, 11.32) * mm});
            skLineSegment(sketch, "E3858", {"start": v(-24.71, 11.32) * mm, "end": v(-24.75, 11.3) * mm});
            skLineSegment(sketch, "E3859", {"start": v(-24.75, 11.3) * mm, "end": v(-24.8, 11.27) * mm});
            skLineSegment(sketch, "E3860", {"start": v(-24.8, 11.27) * mm, "end": v(-25.22, 11.27) * mm});
            skLineSegment(sketch, "E3861", {"start": v(-25.22, 11.27) * mm, "end": v(-25.26, 11.3) * mm});
            skLineSegment(sketch, "E3862", {"start": v(-25.26, 11.3) * mm, "end": v(-25.3, 11.32) * mm});
            skLineSegment(sketch, "E3863", {"start": v(-25.3, 11.32) * mm, "end": v(-25.51, 11.63) * mm});
            skLineSegment(sketch, "E3864", {"start": v(-25.51, 11.63) * mm, "end": v(-25.51, 11.74) * mm});
            skLineSegment(sketch, "E3865", {"start": v(-25.51, 11.74) * mm, "end": v(-25.51, 11.85) * mm});
            skLineSegment(sketch, "E3866", {"start": v(-25.51, 11.85) * mm, "end": v(-25.3, 12.15) * mm});
            skLineSegment(sketch, "E3867", {"start": v(-25.3, 12.15) * mm, "end": v(-25.26, 12.18) * mm});
            skLineSegment(sketch, "E3868", {"start": v(-25.26, 12.18) * mm, "end": v(-25.22, 12.2) * mm});
            skLineSegment(sketch, "E3869", {"start": v(-25.22, 12.2) * mm, "end": v(-24.8, 12.2) * mm});
            skLineSegment(sketch, "E3870", {"start": v(-24.8, 12.2) * mm, "end": v(-24.75, 12.18) * mm});
            skLineSegment(sketch, "E3871", {"start": v(-24.75, 12.18) * mm, "end": v(-24.71, 12.15) * mm});
            skLineSegment(sketch, "E3872", {"start": v(-24.71, 12.15) * mm, "end": v(-24.5, 11.84) * mm});
            skLineSegment(sketch, "E3873", {"start": v(-24.5, 11.84) * mm, "end": v(-24.5, 11.74) * mm});
            skLineSegment(sketch, "E3874", {"start": v(-33.76, 15.24) * mm, "end": v(-33.76, 14.97) * mm});
            skLineSegment(sketch, "E3875", {"start": v(-33.76, 14.97) * mm, "end": v(-33.9, 14.14) * mm});
            skLineSegment(sketch, "E3876", {"start": v(-33.9, 14.14) * mm, "end": v(-34.32, 13.14) * mm});
            skLineSegment(sketch, "E3877", {"start": v(-34.32, 13.14) * mm, "end": v(-34.98, 12.28) * mm});
            skLineSegment(sketch, "E3878", {"start": v(-34.98, 12.28) * mm, "end": v(-35.62, 11.74) * mm});
            skLineSegment(sketch, "E3879", {"start": v(-35.62, 11.74) * mm, "end": v(-35.86, 11.6) * mm});
            skLineSegment(sketch, "E3880", {"start": v(-35.86, 11.6) * mm, "end": v(-36.1, 11.47) * mm});
            skLineSegment(sketch, "E3881", {"start": v(-36.1, 11.47) * mm, "end": v(-36.88, 11.18) * mm});
            skLineSegment(sketch, "E3882", {"start": v(-36.88, 11.18) * mm, "end": v(-37.96, 11.04) * mm});
            skLineSegment(sketch, "E3883", {"start": v(-37.96, 11.04) * mm, "end": v(-39.04, 11.18) * mm});
            skLineSegment(sketch, "E3884", {"start": v(-39.04, 11.18) * mm, "end": v(-39.82, 11.47) * mm});
            skLineSegment(sketch, "E3885", {"start": v(-39.82, 11.47) * mm, "end": v(-40.06, 11.6) * mm});
            skLineSegment(sketch, "E3886", {"start": v(-40.06, 11.6) * mm, "end": v(-40.3, 11.74) * mm});
            skLineSegment(sketch, "E3887", {"start": v(-40.3, 11.74) * mm, "end": v(-40.94, 12.28) * mm});
            skLineSegment(sketch, "E3888", {"start": v(-40.94, 12.28) * mm, "end": v(-41.6, 13.14) * mm});
            skLineSegment(sketch, "E3889", {"start": v(-41.6, 13.14) * mm, "end": v(-42.01, 14.14) * mm});
            skLineSegment(sketch, "E3890", {"start": v(-42.01, 14.14) * mm, "end": v(-42.16, 14.97) * mm});
            skLineSegment(sketch, "E3891", {"start": v(-42.16, 14.97) * mm, "end": v(-42.16, 15.24) * mm});
            skLineSegment(sketch, "E3892", {"start": v(-42.16, 15.24) * mm, "end": v(-42.16, 15.51) * mm});
            skLineSegment(sketch, "E3893", {"start": v(-42.16, 15.51) * mm, "end": v(-42.01, 16.34) * mm});
            skLineSegment(sketch, "E3894", {"start": v(-42.01, 16.34) * mm, "end": v(-41.6, 17.34) * mm});
            skLineSegment(sketch, "E3895", {"start": v(-41.6, 17.34) * mm, "end": v(-40.94, 18.2) * mm});
            skLineSegment(sketch, "E3896", {"start": v(-40.94, 18.2) * mm, "end": v(-40.3, 18.74) * mm});
            skLineSegment(sketch, "E3897", {"start": v(-40.3, 18.74) * mm, "end": v(-40.06, 18.88) * mm});
            skLineSegment(sketch, "E3898", {"start": v(-40.06, 18.88) * mm, "end": v(-39.82, 19.02) * mm});
            skLineSegment(sketch, "E3899", {"start": v(-39.82, 19.02) * mm, "end": v(-39.04, 19.3) * mm});
            skLineSegment(sketch, "E3900", {"start": v(-39.04, 19.3) * mm, "end": v(-37.96, 19.44) * mm});
            skLineSegment(sketch, "E3901", {"start": v(-37.96, 19.44) * mm, "end": v(-36.88, 19.3) * mm});
            skLineSegment(sketch, "E3902", {"start": v(-36.88, 19.3) * mm, "end": v(-36.1, 19.02) * mm});
            skLineSegment(sketch, "E3903", {"start": v(-36.1, 19.02) * mm, "end": v(-35.86, 18.88) * mm});
            skLineSegment(sketch, "E3904", {"start": v(-35.86, 18.88) * mm, "end": v(-35.62, 18.74) * mm});
            skLineSegment(sketch, "E3905", {"start": v(-35.62, 18.74) * mm, "end": v(-34.98, 18.2) * mm});
            skLineSegment(sketch, "E3906", {"start": v(-34.98, 18.2) * mm, "end": v(-34.32, 17.34) * mm});
            skLineSegment(sketch, "E3907", {"start": v(-34.32, 17.34) * mm, "end": v(-33.9, 16.34) * mm});
            skLineSegment(sketch, "E3908", {"start": v(-33.9, 16.34) * mm, "end": v(-33.76, 15.51) * mm});
            skLineSegment(sketch, "E3909", {"start": v(-33.76, 15.51) * mm, "end": v(-33.76, 15.24) * mm});
            skLineSegment(sketch, "E3910", {"start": v(34.82, -20.32) * mm, "end": v(34.82, -20.6) * mm});
            skLineSegment(sketch, "E3911", {"start": v(34.82, -20.6) * mm, "end": v(34.67, -21.41) * mm});
            skLineSegment(sketch, "E3912", {"start": v(34.67, -21.41) * mm, "end": v(34.26, -22.42) * mm});
            skLineSegment(sketch, "E3913", {"start": v(34.26, -22.42) * mm, "end": v(33.6, -23.28) * mm});
            skLineSegment(sketch, "E3914", {"start": v(33.6, -23.28) * mm, "end": v(32.96, -23.82) * mm});
            skLineSegment(sketch, "E3915", {"start": v(32.96, -23.82) * mm, "end": v(32.72, -23.96) * mm});
            skLineSegment(sketch, "E3916", {"start": v(32.72, -23.96) * mm, "end": v(32.48, -24.1) * mm});
            skLineSegment(sketch, "E3917", {"start": v(32.48, -24.1) * mm, "end": v(31.7, -24.38) * mm});
            skLineSegment(sketch, "E3918", {"start": v(31.7, -24.38) * mm, "end": v(30.62, -24.52) * mm});
            skLineSegment(sketch, "E3919", {"start": v(30.62, -24.52) * mm, "end": v(29.54, -24.38) * mm});
            skLineSegment(sketch, "E3920", {"start": v(29.54, -24.38) * mm, "end": v(28.76, -24.1) * mm});
            skLineSegment(sketch, "E3921", {"start": v(28.76, -24.1) * mm, "end": v(28.52, -23.96) * mm});
            skLineSegment(sketch, "E3922", {"start": v(28.52, -23.96) * mm, "end": v(28.28, -23.82) * mm});
            skLineSegment(sketch, "E3923", {"start": v(28.28, -23.82) * mm, "end": v(27.64, -23.28) * mm});
            skLineSegment(sketch, "E3924", {"start": v(27.64, -23.28) * mm, "end": v(26.98, -22.42) * mm});
            skLineSegment(sketch, "E3925", {"start": v(26.98, -22.42) * mm, "end": v(26.56, -21.41) * mm});
            skLineSegment(sketch, "E3926", {"start": v(26.56, -21.41) * mm, "end": v(26.42, -20.6) * mm});
            skLineSegment(sketch, "E3927", {"start": v(26.42, -20.6) * mm, "end": v(26.42, -20.32) * mm});
            skLineSegment(sketch, "E3928", {"start": v(26.42, -20.32) * mm, "end": v(26.42, -20.05) * mm});
            skLineSegment(sketch, "E3929", {"start": v(26.42, -20.05) * mm, "end": v(26.56, -19.22) * mm});
            skLineSegment(sketch, "E3930", {"start": v(26.56, -19.22) * mm, "end": v(26.98, -18.22) * mm});
            skLineSegment(sketch, "E3931", {"start": v(26.98, -18.22) * mm, "end": v(27.64, -17.36) * mm});
            skLineSegment(sketch, "E3932", {"start": v(27.64, -17.36) * mm, "end": v(28.28, -16.82) * mm});
            skLineSegment(sketch, "E3933", {"start": v(28.28, -16.82) * mm, "end": v(28.52, -16.68) * mm});
            skLineSegment(sketch, "E3934", {"start": v(28.52, -16.68) * mm, "end": v(28.76, -16.54) * mm});
            skLineSegment(sketch, "E3935", {"start": v(28.76, -16.54) * mm, "end": v(29.54, -16.26) * mm});
            skLineSegment(sketch, "E3936", {"start": v(29.54, -16.26) * mm, "end": v(30.62, -16.12) * mm});
            skLineSegment(sketch, "E3937", {"start": v(30.62, -16.12) * mm, "end": v(31.7, -16.26) * mm});
            skLineSegment(sketch, "E3938", {"start": v(31.7, -16.26) * mm, "end": v(32.48, -16.54) * mm});
            skLineSegment(sketch, "E3939", {"start": v(32.48, -16.54) * mm, "end": v(32.72, -16.68) * mm});
            skLineSegment(sketch, "E3940", {"start": v(32.72, -16.68) * mm, "end": v(32.96, -16.82) * mm});
            skLineSegment(sketch, "E3941", {"start": v(32.96, -16.82) * mm, "end": v(33.6, -17.36) * mm});
            skLineSegment(sketch, "E3942", {"start": v(33.6, -17.36) * mm, "end": v(34.26, -18.22) * mm});
            skLineSegment(sketch, "E3943", {"start": v(34.26, -18.22) * mm, "end": v(34.67, -19.22) * mm});
            skLineSegment(sketch, "E3944", {"start": v(34.67, -19.22) * mm, "end": v(34.82, -20.05) * mm});
            skLineSegment(sketch, "E3945", {"start": v(34.82, -20.05) * mm, "end": v(34.82, -20.32) * mm});
            skLineSegment(sketch, "E3946", {"start": v(-13.44, -20.32) * mm, "end": v(-13.44, -20.6) * mm});
            skLineSegment(sketch, "E3947", {"start": v(-13.44, -20.6) * mm, "end": v(-13.59, -21.41) * mm});
            skLineSegment(sketch, "E3948", {"start": v(-13.59, -21.41) * mm, "end": v(-14, -22.42) * mm});
            skLineSegment(sketch, "E3949", {"start": v(-14, -22.42) * mm, "end": v(-14.66, -23.28) * mm});
            skLineSegment(sketch, "E3950", {"start": v(-14.66, -23.28) * mm, "end": v(-15.3, -23.82) * mm});
            skLineSegment(sketch, "E3951", {"start": v(-15.3, -23.82) * mm, "end": v(-15.54, -23.96) * mm});
            skLineSegment(sketch, "E3952", {"start": v(-15.54, -23.96) * mm, "end": v(-15.78, -24.1) * mm});
            skLineSegment(sketch, "E3953", {"start": v(-15.78, -24.1) * mm, "end": v(-16.56, -24.38) * mm});
            skLineSegment(sketch, "E3954", {"start": v(-16.56, -24.38) * mm, "end": v(-17.64, -24.52) * mm});
            skLineSegment(sketch, "E3955", {"start": v(-17.64, -24.52) * mm, "end": v(-18.72, -24.38) * mm});
            skLineSegment(sketch, "E3956", {"start": v(-18.72, -24.38) * mm, "end": v(-19.5, -24.1) * mm});
            skLineSegment(sketch, "E3957", {"start": v(-19.5, -24.1) * mm, "end": v(-19.74, -23.96) * mm});
            skLineSegment(sketch, "E3958", {"start": v(-19.74, -23.96) * mm, "end": v(-19.98, -23.82) * mm});
            skLineSegment(sketch, "E3959", {"start": v(-19.98, -23.82) * mm, "end": v(-20.62, -23.28) * mm});
            skLineSegment(sketch, "E3960", {"start": v(-20.62, -23.28) * mm, "end": v(-21.28, -22.42) * mm});
            skLineSegment(sketch, "E3961", {"start": v(-21.28, -22.42) * mm, "end": v(-21.7, -21.41) * mm});
            skLineSegment(sketch, "E3962", {"start": v(-21.7, -21.41) * mm, "end": v(-21.84, -20.6) * mm});
            skLineSegment(sketch, "E3963", {"start": v(-21.84, -20.6) * mm, "end": v(-21.84, -20.32) * mm});
            skLineSegment(sketch, "E3964", {"start": v(-21.84, -20.32) * mm, "end": v(-21.84, -20.05) * mm});
            skLineSegment(sketch, "E3965", {"start": v(-21.84, -20.05) * mm, "end": v(-21.7, -19.22) * mm});
            skLineSegment(sketch, "E3966", {"start": v(-21.7, -19.22) * mm, "end": v(-21.28, -18.22) * mm});
            skLineSegment(sketch, "E3967", {"start": v(-21.28, -18.22) * mm, "end": v(-20.62, -17.36) * mm});
            skLineSegment(sketch, "E3968", {"start": v(-20.62, -17.36) * mm, "end": v(-19.98, -16.82) * mm});
            skLineSegment(sketch, "E3969", {"start": v(-19.98, -16.82) * mm, "end": v(-19.74, -16.68) * mm});
            skLineSegment(sketch, "E3970", {"start": v(-19.74, -16.68) * mm, "end": v(-19.5, -16.54) * mm});
            skLineSegment(sketch, "E3971", {"start": v(-19.5, -16.54) * mm, "end": v(-18.72, -16.26) * mm});
            skLineSegment(sketch, "E3972", {"start": v(-18.72, -16.26) * mm, "end": v(-17.64, -16.12) * mm});
            skLineSegment(sketch, "E3973", {"start": v(-17.64, -16.12) * mm, "end": v(-16.56, -16.26) * mm});
            skLineSegment(sketch, "E3974", {"start": v(-16.56, -16.26) * mm, "end": v(-15.78, -16.54) * mm});
            skLineSegment(sketch, "E3975", {"start": v(-15.78, -16.54) * mm, "end": v(-15.54, -16.68) * mm});
            skLineSegment(sketch, "E3976", {"start": v(-15.54, -16.68) * mm, "end": v(-15.3, -16.82) * mm});
            skLineSegment(sketch, "E3977", {"start": v(-15.3, -16.82) * mm, "end": v(-14.66, -17.36) * mm});
            skLineSegment(sketch, "E3978", {"start": v(-14.66, -17.36) * mm, "end": v(-14, -18.22) * mm});
            skLineSegment(sketch, "E3979", {"start": v(-14, -18.22) * mm, "end": v(-13.59, -19.22) * mm});
            skLineSegment(sketch, "E3980", {"start": v(-13.59, -19.22) * mm, "end": v(-13.44, -20.05) * mm});
            skLineSegment(sketch, "E3981", {"start": v(-13.44, -20.05) * mm, "end": v(-13.44, -20.32) * mm});
            skLineSegment(sketch, "E3982", {"start": v(34.82, 48.26) * mm, "end": v(34.82, 47.99) * mm});
            skLineSegment(sketch, "E3983", {"start": v(34.82, 47.99) * mm, "end": v(34.67, 47.16) * mm});
            skLineSegment(sketch, "E3984", {"start": v(34.67, 47.16) * mm, "end": v(34.26, 46.16) * mm});
            skLineSegment(sketch, "E3985", {"start": v(34.26, 46.16) * mm, "end": v(33.6, 45.3) * mm});
            skLineSegment(sketch, "E3986", {"start": v(33.6, 45.3) * mm, "end": v(32.96, 44.76) * mm});
            skLineSegment(sketch, "E3987", {"start": v(32.96, 44.76) * mm, "end": v(32.72, 44.62) * mm});
            skLineSegment(sketch, "E3988", {"start": v(32.72, 44.62) * mm, "end": v(32.48, 44.49) * mm});
            skLineSegment(sketch, "E3989", {"start": v(32.48, 44.49) * mm, "end": v(31.7, 44.2) * mm});
            skLineSegment(sketch, "E3990", {"start": v(31.7, 44.2) * mm, "end": v(30.62, 44.06) * mm});
            skLineSegment(sketch, "E3991", {"start": v(30.62, 44.06) * mm, "end": v(29.54, 44.2) * mm});
            skLineSegment(sketch, "E3992", {"start": v(29.54, 44.2) * mm, "end": v(28.76, 44.49) * mm});
            skLineSegment(sketch, "E3993", {"start": v(28.76, 44.49) * mm, "end": v(28.52, 44.62) * mm});
            skLineSegment(sketch, "E3994", {"start": v(28.52, 44.62) * mm, "end": v(28.28, 44.76) * mm});
            skLineSegment(sketch, "E3995", {"start": v(28.28, 44.76) * mm, "end": v(27.64, 45.3) * mm});
            skLineSegment(sketch, "E3996", {"start": v(27.64, 45.3) * mm, "end": v(26.98, 46.16) * mm});
            skLineSegment(sketch, "E3997", {"start": v(26.98, 46.16) * mm, "end": v(26.56, 47.16) * mm});
            skLineSegment(sketch, "E3998", {"start": v(26.56, 47.16) * mm, "end": v(26.42, 47.99) * mm});
            skLineSegment(sketch, "E3999", {"start": v(26.42, 47.99) * mm, "end": v(26.42, 48.26) * mm});
            skLineSegment(sketch, "E4000", {"start": v(26.42, 48.26) * mm, "end": v(26.42, 48.53) * mm});
            skLineSegment(sketch, "E4001", {"start": v(26.42, 48.53) * mm, "end": v(26.56, 49.36) * mm});
            skLineSegment(sketch, "E4002", {"start": v(26.56, 49.36) * mm, "end": v(26.98, 50.36) * mm});
            skLineSegment(sketch, "E4003", {"start": v(26.98, 50.36) * mm, "end": v(27.64, 51.22) * mm});
            skLineSegment(sketch, "E4004", {"start": v(27.64, 51.22) * mm, "end": v(28.28, 51.76) * mm});
            skLineSegment(sketch, "E4005", {"start": v(28.28, 51.76) * mm, "end": v(28.52, 51.9) * mm});
            skLineSegment(sketch, "E4006", {"start": v(28.52, 51.9) * mm, "end": v(28.76, 52.03) * mm});
            skLineSegment(sketch, "E4007", {"start": v(28.76, 52.03) * mm, "end": v(29.54, 52.32) * mm});
            skLineSegment(sketch, "E4008", {"start": v(29.54, 52.32) * mm, "end": v(30.62, 52.46) * mm});
            skLineSegment(sketch, "E4009", {"start": v(30.62, 52.46) * mm, "end": v(31.7, 52.32) * mm});
            skLineSegment(sketch, "E4010", {"start": v(31.7, 52.32) * mm, "end": v(32.48, 52.03) * mm});
            skLineSegment(sketch, "E4011", {"start": v(32.48, 52.03) * mm, "end": v(32.72, 51.9) * mm});
            skLineSegment(sketch, "E4012", {"start": v(32.72, 51.9) * mm, "end": v(32.96, 51.76) * mm});
            skLineSegment(sketch, "E4013", {"start": v(32.96, 51.76) * mm, "end": v(33.6, 51.22) * mm});
            skLineSegment(sketch, "E4014", {"start": v(33.6, 51.22) * mm, "end": v(34.26, 50.36) * mm});
            skLineSegment(sketch, "E4015", {"start": v(34.26, 50.36) * mm, "end": v(34.67, 49.36) * mm});
            skLineSegment(sketch, "E4016", {"start": v(34.67, 49.36) * mm, "end": v(34.82, 48.53) * mm});
            skLineSegment(sketch, "E4017", {"start": v(34.82, 48.53) * mm, "end": v(34.82, 48.26) * mm});
            skLineSegment(sketch, "E4018", {"start": v(38.24, -40.64) * mm, "end": v(38.24, -41.73) * mm});
            skLineSegment(sketch, "E4019", {"start": v(38.24, 35.56) * mm, "end": v(38.24, 35.13) * mm});
            skLineSegment(sketch, "E4020", {"start": v(-37.96, -40.64) * mm, "end": v(-37.05, -41.55) * mm});
            skLineSegment(sketch, "E4021", {"start": v(30.62, 48.26) * mm, "end": v(30.62, 43.92) * mm});
            skLineSegment(sketch, "E4022", {"start": v(-37.96, 15.24) * mm, "end": v(-37.96, 11.35) * mm});
            skLineSegment(sketch, "E4023", {"start": v(30.62, -20.32) * mm, "end": v(29.4, -20.32) * mm});
            skLineSegment(sketch, "E4024", {"start": v(-17.64, -20.32) * mm, "end": v(-21.27, -20.32) * mm});
            skLineSegment(sketch, "E4025", {"start": v(-59.55, 13.97) * mm, "end": v(-59.55, -13.97) * mm});
            skLineSegment(sketch, "E4026", {"start": v(-42.4, -47.26) * mm, "end": v(-42.4, -46.2) * mm});
            skLineSegment(sketch, "E4027", {"start": v(-42.4, -46.2) * mm, "end": v(-43.04, -45.56) * mm});
            skLineSegment(sketch, "E4028", {"start": v(-42.4, -47.26) * mm, "end": v(-42.4, -49.46) * mm});
            skLineSegment(sketch, "E4029", {"start": v(-42.4, -49.46) * mm, "end": v(-42.2, -49.66) * mm});
            skLineSegment(sketch, "E4030", {"start": v(-31.23, 49.2) * mm, "end": v(-41.42, 49.2) * mm});
            skLineSegment(sketch, "E4031", {"start": v(-41.42, 49.2) * mm, "end": v(-52.7, 37.93) * mm});
            skLineSegment(sketch, "E4032", {"start": v(-52.7, 37.93) * mm, "end": v(-52.7, 30.02) * mm});
            skLineSegment(sketch, "E4033", {"start": v(12.06, 12.88) * mm, "end": v(15.38, 9.56) * mm});
            skLineSegment(sketch, "E4034", {"start": v(15.38, 9.56) * mm, "end": v(15.38, -55.48) * mm});
            skLineSegment(sketch, "E4035", {"start": v(15.38, -55.48) * mm, "end": v(15.23, -55.63) * mm});
            skLineSegment(sketch, "E4036", {"start": v(-27.17, -52.07) * mm, "end": v(-20.69, -58.55) * mm});
            skLineSegment(sketch, "E4037", {"start": v(-20.69, -58.55) * mm, "end": v(12.31, -58.55) * mm});
            skLineSegment(sketch, "E4038", {"start": v(12.31, -58.55) * mm, "end": v(15.23, -55.63) * mm});
            skLineSegment(sketch, "E4039", {"start": v(52.24, -59.36) * mm, "end": v(52.24, -59.2) * mm});
            skLineSegment(sketch, "E4040", {"start": v(52.24, -59.2) * mm, "end": v(48.65, -55.63) * mm});
            skLineSegment(sketch, "E4041", {"start": v(48.65, -55.63) * mm, "end": v(15.23, -55.63) * mm});
            skLineSegment(sketch, "E4042", {"start": v(-46.67, -56.56) * mm, "end": v(-46.47, -56.56) * mm});
            skLineSegment(sketch, "E4043", {"start": v(-46.47, -56.56) * mm, "end": v(-44.9, -58.12) * mm});
            skLineSegment(sketch, "E4044", {"start": v(-44.9, -58.12) * mm, "end": v(-33.22, -58.12) * mm});
            skLineSegment(sketch, "E4045", {"start": v(-33.22, -58.12) * mm, "end": v(-32.16, -57.07) * mm});
            skLineSegment(sketch, "E4046", {"start": v(-32.16, -57.07) * mm, "end": v(-27.17, -52.07) * mm});
            skLineSegment(sketch, "E4047", {"start": v(44.02, 8.86) * mm, "end": v(43.94, 8.95) * mm});
            skLineSegment(sketch, "E4048", {"start": v(43.94, 8.95) * mm, "end": v(43.94, 22.2) * mm});
            skLineSegment(sketch, "E4049", {"start": v(43.94, 22.2) * mm, "end": v(50.2, 28.46) * mm});
            skLineSegment(sketch, "E4050", {"start": v(50.2, 28.46) * mm, "end": v(50.2, 30.46) * mm});
            skLineSegment(sketch, "E4051", {"start": v(22.75, -1.32) * mm, "end": v(19.13, 2.29) * mm});
            skLineSegment(sketch, "E4052", {"start": v(19.13, 2.29) * mm, "end": v(15.23, 2.29) * mm});
            skLineSegment(sketch, "E4053", {"start": v(-46.4, -46.48) * mm, "end": v(-46.35, -46.43) * mm});
            skLineSegment(sketch, "E4054", {"start": v(-46.35, -45.86) * mm, "end": v(-46.35, -45.71) * mm});
            skLineSegment(sketch, "E4055", {"start": v(-46.35, -46.43) * mm, "end": v(-46.35, -45.86) * mm});
            skLineSegment(sketch, "E4056", {"start": v(-46.4, -46.2) * mm, "end": v(-46.4, -47.26) * mm});
            skLineSegment(sketch, "E4057", {"start": v(35.59, 17.3) * mm, "end": v(16.47, 17.3) * mm});
            skLineSegment(sketch, "E4058", {"start": v(16.47, 17.3) * mm, "end": v(12.06, 12.88) * mm});
            skLineSegment(sketch, "E4059", {"start": v(44.02, 8.86) * mm, "end": v(35.59, 17.3) * mm});
            skLineSegment(sketch, "E4060", {"start": v(50.2, 40.66) * mm, "end": v(48.54, 40.66) * mm});
            skLineSegment(sketch, "E4061", {"start": v(48.54, 40.66) * mm, "end": v(46.74, 38.86) * mm});
            skLineSegment(sketch, "E4062", {"start": v(46.74, 38.86) * mm, "end": v(45.94, 38.06) * mm});
            skLineSegment(sketch, "E4063", {"start": v(50.2, 58.44) * mm, "end": v(48.54, 58.44) * mm});
            skLineSegment(sketch, "E4064", {"start": v(48.54, 58.44) * mm, "end": v(45.94, 55.84) * mm});
            skLineSegment(sketch, "E4065", {"start": v(50.2, 48.24) * mm, "end": v(50.2, 58.44) * mm});
            skLineSegment(sketch, "E4066", {"start": v(50.2, 40.66) * mm, "end": v(50.2, 48.24) * mm});
            skLineSegment(sketch, "E4067", {"start": v(50.2, 32.46) * mm, "end": v(50.2, 40.66) * mm});
            skLineSegment(sketch, "E4068", {"start": v(50.2, 30.46) * mm, "end": v(50.2, 32.46) * mm});
            skLineSegment(sketch, "E4069", {"start": v(-48.5, -51.96) * mm, "end": v(-48.5, -49.37) * mm});
            skLineSegment(sketch, "E4070", {"start": v(-48.5, -49.37) * mm, "end": v(-46.4, -47.26) * mm});
            skLineSegment(sketch, "E4071", {"start": v(-48.5, -51.96) * mm, "end": v(-42.2, -51.96) * mm});
            skLineSegment(sketch, "E4072", {"start": v(-46.67, -56.56) * mm, "end": v(-46.67, -53.79) * mm});
            skLineSegment(sketch, "E4073", {"start": v(-46.67, -53.79) * mm, "end": v(-48.5, -51.96) * mm});
            skLineSegment(sketch, "E4074", {"start": v(7.28, -45.67) * mm, "end": v(7.28, 10.04) * mm});
            skLineSegment(sketch, "E4075", {"start": v(7.28, 10.04) * mm, "end": v(5.08, 12.24) * mm});
            skLineSegment(sketch, "E4076", {"start": v(45.94, 20.66) * mm, "end": v(44.88, 19.6) * mm});
            skLineSegment(sketch, "E4077", {"start": v(44.88, 19.6) * mm, "end": v(44.88, 17.63) * mm});
            skLineSegment(sketch, "E4078", {"start": v(44.88, 17.63) * mm, "end": v(49.45, 13.06) * mm});
            skLineSegment(sketch, "E4079", {"start": v(49.45, 13.06) * mm, "end": v(50.2, 13.06) * mm});
            skLineSegment(sketch, "E4080", {"start": v(50.2, 23.26) * mm, "end": v(48.54, 23.26) * mm});
            skLineSegment(sketch, "E4081", {"start": v(48.54, 23.26) * mm, "end": v(46.74, 21.46) * mm});
            skLineSegment(sketch, "E4082", {"start": v(46.74, 21.46) * mm, "end": v(45.94, 20.66) * mm});
            skLineSegment(sketch, "E4083", {"start": v(49.99, 13.06) * mm, "end": v(50.74, 13.06) * mm});
            skLineSegment(sketch, "E4084", {"start": v(49.07, 23.26) * mm, "end": v(50.74, 23.26) * mm});
            skLineSegment(sketch, "E4085", {"start": v(49.99, 13.06) * mm, "end": v(46.51, 9.59) * mm});
            skLineSegment(sketch, "E4086", {"start": v(46.51, 9.59) * mm, "end": v(46.51, 8.74) * mm});
            skLineSegment(sketch, "E4087", {"start": v(53.48, -34.29) * mm, "end": v(53.48, 10.32) * mm});
            skLineSegment(sketch, "E4088", {"start": v(53.48, 10.32) * mm, "end": v(53.5, 10.33) * mm});
            skLineSegment(sketch, "E4089", {"start": v(53.5, 10.33) * mm, "end": v(53.5, 11.06) * mm});
            skLineSegment(sketch, "E4090", {"start": v(53.5, 11.06) * mm, "end": v(51.49, 13.06) * mm});
            skLineSegment(sketch, "E4091", {"start": v(51.49, 13.06) * mm, "end": v(50.74, 13.06) * mm});
            skLineSegment(sketch, "E4092", {"start": v(7.28, -45.67) * mm, "end": v(8.38, -45.67) * mm});
            skLineSegment(sketch, "E4093", {"start": v(8.38, -45.67) * mm, "end": v(13.6, -40.44) * mm});
            skLineSegment(sketch, "E4094", {"start": v(13.6, -40.44) * mm, "end": v(13.6, -40.39) * mm});
            skLineSegment(sketch, "E4095", {"start": v(-17.41, 35.33) * mm, "end": v(-17.41, 58.2) * mm});
            skLineSegment(sketch, "E4096", {"start": v(-17.41, 58.2) * mm, "end": v(-17.64, 58.42) * mm});
            skLineSegment(sketch, "E4097", {"start": v(-17.7, 58.37) * mm, "end": v(-17.64, 58.42) * mm});
            skLineSegment(sketch, "E4098", {"start": v(-42.67, -56.56) * mm, "end": v(-42.67, -54.73) * mm});
            skLineSegment(sketch, "E4099", {"start": v(-42.67, -54.73) * mm, "end": v(-42.2, -54.26) * mm});
            skLineSegment(sketch, "E4100", {"start": v(-42.2, -54.26) * mm, "end": v(-39.93, -54.26) * mm});
            skLineSegment(sketch, "E4101", {"start": v(-39.93, -54.26) * mm, "end": v(-31.98, -46.3) * mm});
            skLineSegment(sketch, "E4102", {"start": v(-13.93, -46.3) * mm, "end": v(-13.25, -46.99) * mm});
            skLineSegment(sketch, "E4103", {"start": v(-31.98, -46.3) * mm, "end": v(-13.93, -46.3) * mm});
            skLineSegment(sketch, "E4104", {"start": v(4.7, 12.63) * mm, "end": v(7.28, 10.04) * mm});
            skLineSegment(sketch, "E4105", {"start": v(-23, 13.9) * mm, "end": v(-24.27, 13.9) * mm});
            skLineSegment(sketch, "E4106", {"start": v(-24.27, 13.9) * mm, "end": v(-24.96, 14.58) * mm});
            skLineSegment(sketch, "E4107", {"start": v(-25, 11.74) * mm, "end": v(-23.31, 11.74) * mm});
            skLineSegment(sketch, "E4108", {"start": v(-23.31, 11.74) * mm, "end": v(-22.61, 12.44) * mm});
            skLineSegment(sketch, "E4109", {"start": v(-43.78, 57.1) * mm, "end": v(-43.78, 52.48) * mm});
            skLineSegment(sketch, "E4110", {"start": v(12.57, 22.66) * mm, "end": v(33.04, 22.66) * mm});
            skLineSegment(sketch, "E4111", {"start": v(41.93, 25.4) * mm, "end": v(41.48, 25.4) * mm});
            skLineSegment(sketch, "E4112", {"start": v(41.48, 25.4) * mm, "end": v(38.73, 22.66) * mm});
            skLineSegment(sketch, "E4113", {"start": v(38.73, 22.66) * mm, "end": v(32.9, 22.66) * mm});
            skLineSegment(sketch, "E4114", {"start": v(-21.1, 16.18) * mm, "end": v(-21.1, 17) * mm});
            skLineSegment(sketch, "E4115", {"start": v(-21.1, 17) * mm, "end": v(-23.38, 19.28) * mm});
            skLineSegment(sketch, "E4116", {"start": v(-4.39, 18.15) * mm, "end": v(-4.39, 17.47) * mm});
            skLineSegment(sketch, "E4117", {"start": v(-5.8, 59.28) * mm, "end": v(-4.94, 58.42) * mm});
            skLineSegment(sketch, "E4118", {"start": v(-23.38, 19.28) * mm, "end": v(-23.38, 20.04) * mm});
            skLineSegment(sketch, "E4119", {"start": v(-23.38, 20.04) * mm, "end": v(-22.47, 20.94) * mm});
            skLineSegment(sketch, "E4120", {"start": v(-22.47, 20.94) * mm, "end": v(-22.37, 20.94) * mm});
            skLineSegment(sketch, "E4121", {"start": v(-22.37, 20.94) * mm, "end": v(-15.33, 13.9) * mm});
            skLineSegment(sketch, "E4122", {"start": v(-15.33, 13.9) * mm, "end": v(-12.09, 13.9) * mm});
            skLineSegment(sketch, "E4123", {"start": v(-12.09, 13.9) * mm, "end": v(-11.7, 14.3) * mm});
            skLineSegment(sketch, "E4124", {"start": v(-11.7, 14.3) * mm, "end": v(-11.7, 18.1) * mm});
            skLineSegment(sketch, "E4125", {"start": v(-11.7, 18.1) * mm, "end": v(-12.4, 18.82) * mm});
            skLineSegment(sketch, "E4126", {"start": v(-12.4, 18.82) * mm, "end": v(-12.4, 20.94) * mm});
            skLineSegment(sketch, "E4127", {"start": v(-12.4, 20.94) * mm, "end": v(-12, 21.34) * mm});
            skLineSegment(sketch, "E4128", {"start": v(-2.87, 19.34) * mm, "end": v(-16.54, 33) * mm});
            skLineSegment(sketch, "E4129", {"start": v(-12, 21.34) * mm, "end": v(-7.58, 21.34) * mm});
            skLineSegment(sketch, "E4130", {"start": v(-7.58, 21.34) * mm, "end": v(-4.39, 18.15) * mm});
            skLineSegment(sketch, "E4131", {"start": v(-11.5, 60.45) * mm, "end": v(-10.53, 59.47) * mm});
            skLineSegment(sketch, "E4132", {"start": v(-4.39, 17.47) * mm, "end": v(-4, 17.07) * mm});
            skLineSegment(sketch, "E4133", {"start": v(-15.6, 62.01) * mm, "end": v(-14.6, 62.01) * mm});
            skLineSegment(sketch, "E4134", {"start": v(-4, 17.07) * mm, "end": v(-3.26, 17.07) * mm});
            skLineSegment(sketch, "E4135", {"start": v(-14.05, 61.47) * mm, "end": v(-14.05, 61.04) * mm});
            skLineSegment(sketch, "E4136", {"start": v(-3.26, 17.07) * mm, "end": v(-2.87, 17.47) * mm});
            skLineSegment(sketch, "E4137", {"start": v(-2.87, 17.47) * mm, "end": v(-2.87, 19.34) * mm});
            skLineSegment(sketch, "E4138", {"start": v(-16.54, 33) * mm, "end": v(-16.54, 61.09) * mm});
            skLineSegment(sketch, "E4139", {"start": v(-16.54, 61.09) * mm, "end": v(-15.6, 62.01) * mm});
            skLineSegment(sketch, "E4140", {"start": v(-14.6, 62.01) * mm, "end": v(-14.05, 61.47) * mm});
            skLineSegment(sketch, "E4141", {"start": v(-14.05, 61.04) * mm, "end": v(-13.07, 62.01) * mm});
            skLineSegment(sketch, "E4142", {"start": v(-13.07, 62.01) * mm, "end": v(-12.05, 62.01) * mm});
            skLineSegment(sketch, "E4143", {"start": v(-12.05, 62.01) * mm, "end": v(-11.5, 61.47) * mm});
            skLineSegment(sketch, "E4144", {"start": v(-11.5, 61.47) * mm, "end": v(-11.5, 60.45) * mm});
            skLineSegment(sketch, "E4145", {"start": v(-10.53, 59.47) * mm, "end": v(-6, 59.47) * mm});
            skLineSegment(sketch, "E4146", {"start": v(-6, 59.47) * mm, "end": v(-5.8, 59.28) * mm});
            skLineSegment(sketch, "E4147", {"start": v(-59.55, -62.23) * mm, "end": v(-53.96, -56.64) * mm});
            skLineSegment(sketch, "E4148", {"start": v(-53.96, -56.64) * mm, "end": v(-53.96, -17.27) * mm});
            skLineSegment(sketch, "E4149", {"start": v(-15.82, 12.88) * mm, "end": v(-15.88, 12.88) * mm});
            skLineSegment(sketch, "E4150", {"start": v(-15.88, 12.88) * mm, "end": v(-45.78, -17.02) * mm});
            skLineSegment(sketch, "E4151", {"start": v(-45.78, -17.02) * mm, "end": v(-54.07, -17.02) * mm});
            skLineSegment(sketch, "E4152", {"start": v(-54.07, -17.02) * mm, "end": v(-58.24, -21.2) * mm});
            skLineSegment(sketch, "E4153", {"start": v(-58.69, -58.83) * mm, "end": v(-59.55, -59.69) * mm});
            skLineSegment(sketch, "E4154", {"start": v(-58.24, -21.2) * mm, "end": v(-58.24, -58.38) * mm});
            skLineSegment(sketch, "E4155", {"start": v(-58.24, -58.38) * mm, "end": v(-58.69, -58.83) * mm});
            skLineSegment(sketch, "E4156", {"start": v(12.79, 20.7) * mm, "end": v(10.85, 20.7) * mm});
            skLineSegment(sketch, "E4157", {"start": v(10.85, 20.7) * mm, "end": v(3.02, 12.88) * mm});
            skLineSegment(sketch, "E4158", {"start": v(3.02, 12.88) * mm, "end": v(-15.82, 12.88) * mm});
            skLineSegment(sketch, "E4159", {"start": v(-15.82, 12.88) * mm, "end": v(-22.04, 19.1) * mm});
            skLineSegment(sketch, "E4160", {"start": v(-22.04, 19.1) * mm, "end": v(-22.61, 19.67) * mm});
            skLineSegment(sketch, "E4161", {"start": v(-62.1, -16.51) * mm, "end": v(-61.04, -15.46) * mm});
            skLineSegment(sketch, "E4162", {"start": v(-61.04, -15.46) * mm, "end": v(-61.04, -8.67) * mm});
            skLineSegment(sketch, "E4163", {"start": v(-61.04, -8.67) * mm, "end": v(-62.1, -7.62) * mm});
            skLineSegment(sketch, "E4164", {"start": v(2.22, 57.87) * mm, "end": v(-2, 62.08) * mm});
            skLineSegment(sketch, "E4165", {"start": v(-2, 62.08) * mm, "end": v(-8.9, 62.08) * mm});
            skLineSegment(sketch, "E4166", {"start": v(-8.9, 62.08) * mm, "end": v(-9.16, 61.82) * mm});
            skLineSegment(sketch, "E4167", {"start": v(-9.16, 61.82) * mm, "end": v(-10.02, 60.96) * mm});
            skLineSegment(sketch, "E4168", {"start": v(2.22, 21.77) * mm, "end": v(2.22, 57.87) * mm});
            skLineSegment(sketch, "E4169", {"start": v(-51.93, -23.62) * mm, "end": v(-15.81, 12.5) * mm});
            skLineSegment(sketch, "E4170", {"start": v(-15.81, 12.5) * mm, "end": v(3.18, 12.5) * mm});
            skLineSegment(sketch, "E4171", {"start": v(3.18, 12.5) * mm, "end": v(11, 20.32) * mm});
            skLineSegment(sketch, "E4172", {"start": v(11, 20.32) * mm, "end": v(12.95, 20.32) * mm});
            skLineSegment(sketch, "E4173", {"start": v(12.95, 20.32) * mm, "end": v(13.17, 20.54) * mm});
            skLineSegment(sketch, "E4174", {"start": v(13.17, 20.54) * mm, "end": v(13.17, 20.86) * mm});
            skLineSegment(sketch, "E4175", {"start": v(13.17, 20.86) * mm, "end": v(12.95, 21.08) * mm});
            skLineSegment(sketch, "E4176", {"start": v(12.95, 21.08) * mm, "end": v(3.4, 21.08) * mm});
            skLineSegment(sketch, "E4177", {"start": v(0.87, 18.56) * mm, "end": v(0.3, 17.99) * mm});
            skLineSegment(sketch, "E4178", {"start": v(3.4, 21.08) * mm, "end": v(0.87, 18.56) * mm});
            skLineSegment(sketch, "E4179", {"start": v(0.3, 17.99) * mm, "end": v(1.26, 18.95) * mm});
            skLineSegment(sketch, "E4180", {"start": v(-4.59, 59.84) * mm, "end": v(-6.36, 59.84) * mm});
            skLineSegment(sketch, "E4181", {"start": v(1.26, 18.95) * mm, "end": v(1.26, 54) * mm});
            skLineSegment(sketch, "E4182", {"start": v(1.26, 54) * mm, "end": v(-4.59, 59.84) * mm});
            skLineSegment(sketch, "E4183", {"start": v(-6.36, 59.84) * mm, "end": v(-7.48, 60.96) * mm});
            skLineSegment(sketch, "E4184", {"start": v(-58.5, 14.06) * mm, "end": v(-58.5, -17.63) * mm});
            skLineSegment(sketch, "E4185", {"start": v(-59.05, -20.1) * mm, "end": v(-58.5, -20.65) * mm});
            skLineSegment(sketch, "E4186", {"start": v(-60.06, -20.1) * mm, "end": v(-59.05, -20.1) * mm});
            skLineSegment(sketch, "E4187", {"start": v(-58.5, -20.65) * mm, "end": v(-58.5, -23.08) * mm});
            skLineSegment(sketch, "E4188", {"start": v(-52.7, 19.86) * mm, "end": v(-58.5, 14.06) * mm});
            skLineSegment(sketch, "E4189", {"start": v(-60.6, -18.54) * mm, "end": v(-60.6, -19.56) * mm});
            skLineSegment(sketch, "E4190", {"start": v(-58.5, -23.08) * mm, "end": v(-58.69, -23.27) * mm});
            skLineSegment(sketch, "E4191", {"start": v(-58.69, -23.27) * mm, "end": v(-59.55, -24.13) * mm});
            skLineSegment(sketch, "E4192", {"start": v(-58.5, -17.63) * mm, "end": v(-59.7, -17.63) * mm});
            skLineSegment(sketch, "E4193", {"start": v(-59.7, -17.63) * mm, "end": v(-60.6, -18.54) * mm});
            skLineSegment(sketch, "E4194", {"start": v(-60.6, -19.56) * mm, "end": v(-60.06, -20.1) * mm});
            skLineSegment(sketch, "E4195", {"start": v(-52.7, 19.86) * mm, "end": v(-44.16, 19.86) * mm});
            skLineSegment(sketch, "E4196", {"start": v(-44.16, 19.86) * mm, "end": v(-31.66, 32.36) * mm});
            skLineSegment(sketch, "E4197", {"start": v(0.44, 23.3) * mm, "end": v(-0.96, 21.9) * mm});
            skLineSegment(sketch, "E4198", {"start": v(-0.96, 21.9) * mm, "end": v(-0.96, 19.53) * mm});
            skLineSegment(sketch, "E4199", {"start": v(-0.96, 19.53) * mm, "end": v(-1.39, 19.1) * mm});
            skLineSegment(sketch, "E4200", {"start": v(-16.22, 33.14) * mm, "end": v(-16.22, 59.84) * mm});
            skLineSegment(sketch, "E4201", {"start": v(-1.39, 19.1) * mm, "end": v(-2.18, 19.1) * mm});
            skLineSegment(sketch, "E4202", {"start": v(-2.18, 19.1) * mm, "end": v(-16.22, 33.14) * mm});
            skLineSegment(sketch, "E4203", {"start": v(-16.22, 59.84) * mm, "end": v(-15.1, 60.96) * mm});
            skLineSegment(sketch, "E4204", {"start": v(-60.86, -20.28) * mm, "end": v(-60.41, -20.73) * mm});
            skLineSegment(sketch, "E4205", {"start": v(-60.86, -18.44) * mm, "end": v(-60.86, -20.28) * mm});
            skLineSegment(sketch, "E4206", {"start": v(-52.7, 22.4) * mm, "end": v(-60.6, 14.49) * mm});
            skLineSegment(sketch, "E4207", {"start": v(-60.6, 14.49) * mm, "end": v(-60.6, -18.18) * mm});
            skLineSegment(sketch, "E4208", {"start": v(-60.6, -18.18) * mm, "end": v(-60.86, -18.44) * mm});
            skLineSegment(sketch, "E4209", {"start": v(-60.41, -20.73) * mm, "end": v(-59.55, -21.59) * mm});
            skLineSegment(sketch, "E4210", {"start": v(-1.79, 19.93) * mm, "end": v(-1.79, 54.4) * mm});
            skLineSegment(sketch, "E4211", {"start": v(-52.7, 22.4) * mm, "end": v(-43.93, 22.4) * mm});
            skLineSegment(sketch, "E4212", {"start": v(-43.93, 22.4) * mm, "end": v(-31.76, 34.57) * mm});
            skLineSegment(sketch, "E4213", {"start": v(-1.79, 54.4) * mm, "end": v(-4.69, 57.3) * mm});
            skLineSegment(sketch, "E4214", {"start": v(-4.69, 57.3) * mm, "end": v(-13.1, 57.3) * mm});
            skLineSegment(sketch, "E4215", {"start": v(-13.68, 57.88) * mm, "end": v(-13.68, 59.84) * mm});
            skLineSegment(sketch, "E4216", {"start": v(-13.1, 57.3) * mm, "end": v(-13.68, 57.88) * mm});
            skLineSegment(sketch, "E4217", {"start": v(-13.68, 59.84) * mm, "end": v(-12.56, 60.96) * mm});
            skLineSegment(sketch, "E4218", {"start": v(-3.63, 17.83) * mm, "end": v(-18.76, 32.96) * mm});
            skLineSegment(sketch, "E4219", {"start": v(-18.76, 32.96) * mm, "end": v(-18.76, 59.84) * mm});
            skLineSegment(sketch, "E4220", {"start": v(-18.76, 59.84) * mm, "end": v(-18.5, 60.1) * mm});
            skLineSegment(sketch, "E4221", {"start": v(-18.5, 60.1) * mm, "end": v(-17.64, 60.96) * mm});
            skLineSegment(sketch, "E4222", {"start": v(-12.45, 14.66) * mm, "end": v(-29.84, 32.05) * mm});
            skLineSegment(sketch, "E4223", {"start": v(-21.04, 61.82) * mm, "end": v(-20.18, 60.96) * mm});
            skLineSegment(sketch, "E4224", {"start": v(-29.84, 32.05) * mm, "end": v(-29.84, 60.48) * mm});
            skLineSegment(sketch, "E4225", {"start": v(-29.84, 60.48) * mm, "end": v(-27.93, 62.4) * mm});
            skLineSegment(sketch, "E4226", {"start": v(-27.93, 62.4) * mm, "end": v(-21.62, 62.4) * mm});
            skLineSegment(sketch, "E4227", {"start": v(-21.62, 62.4) * mm, "end": v(-21.04, 61.82) * mm});
            skLineSegment(sketch, "E4228", {"start": v(-12.77, 21.7) * mm, "end": v(-12.77, 22.52) * mm});
            skLineSegment(sketch, "E4229", {"start": v(-12.77, 22.52) * mm, "end": v(-28.92, 38.66) * mm});
            skLineSegment(sketch, "E4230", {"start": v(-28.92, 38.66) * mm, "end": v(-28.92, 59.49) * mm});
            skLineSegment(sketch, "E4231", {"start": v(-28.92, 59.49) * mm, "end": v(-28.87, 59.54) * mm});
            skLineSegment(sketch, "E4232", {"start": v(-28.87, 59.54) * mm, "end": v(-27.27, 59.54) * mm});
            skLineSegment(sketch, "E4233", {"start": v(-27.27, 59.54) * mm, "end": v(-26.38, 60.42) * mm});
            skLineSegment(sketch, "E4234", {"start": v(-26.38, 60.42) * mm, "end": v(-26.38, 61.5) * mm});
            skLineSegment(sketch, "E4235", {"start": v(-26.38, 61.5) * mm, "end": v(-25.8, 62.08) * mm});
            skLineSegment(sketch, "E4236", {"start": v(-25.8, 62.08) * mm, "end": v(-23.84, 62.08) * mm});
            skLineSegment(sketch, "E4237", {"start": v(-23.84, 62.08) * mm, "end": v(-23.58, 61.82) * mm});
            skLineSegment(sketch, "E4238", {"start": v(-23.58, 61.82) * mm, "end": v(-22.72, 60.96) * mm});
            skLineSegment(sketch, "E4239", {"start": v(-9.22, 22.22) * mm, "end": v(-26.38, 39.38) * mm});
            skLineSegment(sketch, "E4240", {"start": v(-26.38, 39.38) * mm, "end": v(-26.38, 59.84) * mm});
            skLineSegment(sketch, "E4241", {"start": v(-26.38, 59.84) * mm, "end": v(-25.26, 60.96) * mm});
            skLineSegment(sketch, "E4242", {"start": v(45.94, 0) * mm, "end": v(47, 1.05) * mm});
            skLineSegment(sketch, "E4243", {"start": v(47, 1.05) * mm, "end": v(47, 6.14) * mm});
            skLineSegment(sketch, "E4244", {"start": v(47, 6.14) * mm, "end": v(44.92, 8.2) * mm});
            skLineSegment(sketch, "E4245", {"start": v(44.92, 8.2) * mm, "end": v(44.92, 8.76) * mm});
            skLineSegment(sketch, "E4246", {"start": v(-8.17, -52.07) * mm, "end": v(7.08, -52.07) * mm});
            skLineSegment(sketch, "E4247", {"start": v(7.08, -52.07) * mm, "end": v(7.28, -51.87) * mm});
            skLineSegment(sketch, "E4248", {"start": v(55.26, -32) * mm, "end": v(55.26, 12.13) * mm});
            skLineSegment(sketch, "E4249", {"start": v(55.26, 12.13) * mm, "end": v(49.22, 18.16) * mm});
            skLineSegment(sketch, "E4250", {"start": v(49.22, 18.16) * mm, "end": v(46.47, 18.16) * mm});
            skLineSegment(sketch, "E4251", {"start": v(7.28, -48.49) * mm, "end": v(13.86, -41.91) * mm});
            skLineSegment(sketch, "E4252", {"start": v(7.28, -51.87) * mm, "end": v(7.28, -48.49) * mm});
            skLineSegment(sketch, "E4253", {"start": v(-13.25, -46.99) * mm, "end": v(-8.17, -52.07) * mm});
            skLineSegment(sketch, "E4254", {"start": v(42.83, 25.4) * mm, "end": v(42.83, 32.45) * mm});
            skLineSegment(sketch, "E4255", {"start": v(42.83, 32.45) * mm, "end": v(45.94, 35.56) * mm});
            skLineSegment(sketch, "E4256", {"start": v(-57.91, -62.17) * mm, "end": v(-57.92, -62.16) * mm});
            skLineSegment(sketch, "E4257", {"start": v(-57.92, -62.16) * mm, "end": v(-57.94, -62.16) * mm});
            skLineSegment(sketch, "E4258", {"start": v(-57.94, -62.16) * mm, "end": v(-57.96, -62.17) * mm});
            skLineSegment(sketch, "E4259", {"start": v(-57.96, -62.17) * mm, "end": v(-57.97, -62.18) * mm});
            skLineSegment(sketch, "E4260", {"start": v(-57.97, -62.18) * mm, "end": v(-57.98, -62.19) * mm});
            skLineSegment(sketch, "E4261", {"start": v(-57.98, -62.19) * mm, "end": v(-57.98, -62.21) * mm});
            skLineSegment(sketch, "E4262", {"start": v(-57.98, -62.21) * mm, "end": v(-57.98, -62.23) * mm});
            skLineSegment(sketch, "E4263", {"start": v(-57.98, -62.23) * mm, "end": v(-57.98, -62.26) * mm});
            skLineSegment(sketch, "E4264", {"start": v(-57.98, -62.26) * mm, "end": v(-57.97, -62.27) * mm});
            skLineSegment(sketch, "E4265", {"start": v(-57.97, -62.27) * mm, "end": v(-57.96, -62.28) * mm});
            skLineSegment(sketch, "E4266", {"start": v(-57.96, -62.28) * mm, "end": v(-57.94, -62.29) * mm});
            skLineSegment(sketch, "E4267", {"start": v(-57.94, -62.29) * mm, "end": v(-57.93, -62.29) * mm});
            skLineSegment(sketch, "E4268", {"start": v(-57.93, -62.29) * mm, "end": v(-57.91, -62.28) * mm});
            skLineSegment(sketch, "E4269", {"start": v(-57.91, -62.28) * mm, "end": v(-57.9, -62.27) * mm});
            skLineSegment(sketch, "E4270", {"start": v(-57.9, -62.27) * mm, "end": v(-57.9, -62.23) * mm});
            skLineSegment(sketch, "E4271", {"start": v(-57.9, -62.23) * mm, "end": v(-57.93, -62.23) * mm});
            skLineSegment(sketch, "E4272", {"start": v(-51.04, 57.59) * mm, "end": v(-50.28, 57.59) * mm});
            skLineSegment(sketch, "E4273", {"start": v(-28.15, 56.15) * mm, "end": v(-28.16, 56.16) * mm});
            skLineSegment(sketch, "E4274", {"start": v(-28.16, 56.16) * mm, "end": v(-28.18, 56.16) * mm});
            skLineSegment(sketch, "E4275", {"start": v(-28.18, 56.16) * mm, "end": v(-28.2, 56.15) * mm});
            skLineSegment(sketch, "E4276", {"start": v(-28.2, 56.15) * mm, "end": v(-28.21, 56.14) * mm});
            skLineSegment(sketch, "E4277", {"start": v(-28.21, 56.14) * mm, "end": v(-28.22, 56.12) * mm});
            skLineSegment(sketch, "E4278", {"start": v(-28.22, 56.12) * mm, "end": v(-28.22, 56.1) * mm});
            skLineSegment(sketch, "E4279", {"start": v(-28.22, 56.1) * mm, "end": v(-28.22, 56.08) * mm});
            skLineSegment(sketch, "E4280", {"start": v(-28.22, 56.08) * mm, "end": v(-28.22, 56.06) * mm});
            skLineSegment(sketch, "E4281", {"start": v(-28.22, 56.06) * mm, "end": v(-28.21, 56.04) * mm});
            skLineSegment(sketch, "E4282", {"start": v(-28.21, 56.04) * mm, "end": v(-28.2, 56.03) * mm});
            skLineSegment(sketch, "E4283", {"start": v(-28.2, 56.03) * mm, "end": v(-28.18, 56.03) * mm});
            skLineSegment(sketch, "E4284", {"start": v(-28.18, 56.03) * mm, "end": v(-28.17, 56.03) * mm});
            skLineSegment(sketch, "E4285", {"start": v(-28.17, 56.03) * mm, "end": v(-28.15, 56.03) * mm});
            skLineSegment(sketch, "E4286", {"start": v(-28.15, 56.03) * mm, "end": v(-28.15, 56.04) * mm});
            skLineSegment(sketch, "E4287", {"start": v(-28.15, 56.04) * mm, "end": v(-28.15, 56.08) * mm});
            skLineSegment(sketch, "E4288", {"start": v(-28.15, 56.08) * mm, "end": v(-28.17, 56.08) * mm});
            skLineSegment(sketch, "E4289", {"start": v(-28.1, 56.03) * mm, "end": v(-28.1, 56.15) * mm});
            skLineSegment(sketch, "E4290", {"start": v(-28.1, 56.15) * mm, "end": v(-28.02, 56.03) * mm});
            skLineSegment(sketch, "E4291", {"start": v(-28.02, 56.03) * mm, "end": v(-28.02, 56.15) * mm});
            skLineSegment(sketch, "E4292", {"start": v(-27.96, 56.03) * mm, "end": v(-27.96, 56.15) * mm});
            skLineSegment(sketch, "E4293", {"start": v(-27.96, 56.15) * mm, "end": v(-27.93, 56.15) * mm});
            skLineSegment(sketch, "E4294", {"start": v(-27.93, 56.15) * mm, "end": v(-27.91, 56.15) * mm});
            skLineSegment(sketch, "E4295", {"start": v(-27.91, 56.15) * mm, "end": v(-27.9, 56.14) * mm});
            skLineSegment(sketch, "E4296", {"start": v(-27.9, 56.14) * mm, "end": v(-27.9, 56.12) * mm});
            skLineSegment(sketch, "E4297", {"start": v(-27.9, 56.12) * mm, "end": v(-27.88, 56.1) * mm});
            skLineSegment(sketch, "E4298", {"start": v(-27.88, 56.1) * mm, "end": v(-27.88, 56.08) * mm});
            skLineSegment(sketch, "E4299", {"start": v(-27.88, 56.08) * mm, "end": v(-27.9, 56.06) * mm});
            skLineSegment(sketch, "E4300", {"start": v(-27.9, 56.06) * mm, "end": v(-27.9, 56.04) * mm});
            skLineSegment(sketch, "E4301", {"start": v(-27.9, 56.04) * mm, "end": v(-27.91, 56.03) * mm});
            skLineSegment(sketch, "E4302", {"start": v(-27.91, 56.03) * mm, "end": v(-27.93, 56.03) * mm});
            skLineSegment(sketch, "E4303", {"start": v(-27.93, 56.03) * mm, "end": v(-27.96, 56.03) * mm});
            skLineSegment(sketch, "E4304", {"start": v(-23.04, 56.74) * mm, "end": v(-22.94, 56.74) * mm});
            skLineSegment(sketch, "E4305", {"start": v(-22.99, 56.7) * mm, "end": v(-22.99, 56.79) * mm});
            skLineSegment(sketch, "E4306", {"start": v(-22.82, 56.82) * mm, "end": v(-22.88, 56.82) * mm});
            skLineSegment(sketch, "E4307", {"start": v(-22.88, 56.82) * mm, "end": v(-22.89, 56.76) * mm});
            skLineSegment(sketch, "E4308", {"start": v(-22.89, 56.76) * mm, "end": v(-22.88, 56.77) * mm});
            skLineSegment(sketch, "E4309", {"start": v(-22.88, 56.77) * mm, "end": v(-22.87, 56.77) * mm});
            skLineSegment(sketch, "E4310", {"start": v(-22.87, 56.77) * mm, "end": v(-22.84, 56.77) * mm});
            skLineSegment(sketch, "E4311", {"start": v(-22.84, 56.77) * mm, "end": v(-22.83, 56.77) * mm});
            skLineSegment(sketch, "E4312", {"start": v(-22.83, 56.77) * mm, "end": v(-22.82, 56.76) * mm});
            skLineSegment(sketch, "E4313", {"start": v(-22.82, 56.76) * mm, "end": v(-22.81, 56.75) * mm});
            skLineSegment(sketch, "E4314", {"start": v(-22.81, 56.75) * mm, "end": v(-22.81, 56.72) * mm});
            skLineSegment(sketch, "E4315", {"start": v(-22.81, 56.72) * mm, "end": v(-22.82, 56.7) * mm});
            skLineSegment(sketch, "E4316", {"start": v(-22.82, 56.7) * mm, "end": v(-22.83, 56.7) * mm});
            skLineSegment(sketch, "E4317", {"start": v(-22.83, 56.7) * mm, "end": v(-22.84, 56.7) * mm});
            skLineSegment(sketch, "E4318", {"start": v(-22.84, 56.7) * mm, "end": v(-22.87, 56.7) * mm});
            skLineSegment(sketch, "E4319", {"start": v(-22.87, 56.7) * mm, "end": v(-22.88, 56.7) * mm});
            skLineSegment(sketch, "E4320", {"start": v(-22.88, 56.7) * mm, "end": v(-22.89, 56.7) * mm});
            skLineSegment(sketch, "E4321", {"start": v(-22.78, 56.82) * mm, "end": v(-22.73, 56.7) * mm});
            skLineSegment(sketch, "E4322", {"start": v(-22.73, 56.7) * mm, "end": v(-22.7, 56.82) * mm});
            skLineSegment(sketch, "E4323", {"start": v(-17.81, 56.76) * mm, "end": v(-17.8, 56.75) * mm});
            skLineSegment(sketch, "E4324", {"start": v(-17.8, 56.75) * mm, "end": v(-17.79, 56.75) * mm});
            skLineSegment(sketch, "E4325", {"start": v(-17.79, 56.75) * mm, "end": v(-17.78, 56.74) * mm});
            skLineSegment(sketch, "E4326", {"start": v(-17.78, 56.74) * mm, "end": v(-17.78, 56.72) * mm});
            skLineSegment(sketch, "E4327", {"start": v(-17.78, 56.72) * mm, "end": v(-17.79, 56.7) * mm});
            skLineSegment(sketch, "E4328", {"start": v(-17.79, 56.7) * mm, "end": v(-17.8, 56.7) * mm});
            skLineSegment(sketch, "E4329", {"start": v(-17.8, 56.7) * mm, "end": v(-17.8, 56.7) * mm});
            skLineSegment(sketch, "E4330", {"start": v(-17.8, 56.7) * mm, "end": v(-17.85, 56.7) * mm});
            skLineSegment(sketch, "E4331", {"start": v(-17.85, 56.7) * mm, "end": v(-17.85, 56.82) * mm});
            skLineSegment(sketch, "E4332", {"start": v(-17.85, 56.82) * mm, "end": v(-17.81, 56.82) * mm});
            skLineSegment(sketch, "E4333", {"start": v(-17.81, 56.82) * mm, "end": v(-17.8, 56.82) * mm});
            skLineSegment(sketch, "E4334", {"start": v(-17.8, 56.82) * mm, "end": v(-17.8, 56.8) * mm});
            skLineSegment(sketch, "E4335", {"start": v(-17.8, 56.8) * mm, "end": v(-17.79, 56.8) * mm});
            skLineSegment(sketch, "E4336", {"start": v(-17.79, 56.8) * mm, "end": v(-17.79, 56.78) * mm});
            skLineSegment(sketch, "E4337", {"start": v(-17.79, 56.78) * mm, "end": v(-17.8, 56.77) * mm});
            skLineSegment(sketch, "E4338", {"start": v(-17.8, 56.77) * mm, "end": v(-17.8, 56.77) * mm});
            skLineSegment(sketch, "E4339", {"start": v(-17.8, 56.77) * mm, "end": v(-17.81, 56.76) * mm});
            skLineSegment(sketch, "E4340", {"start": v(-17.81, 56.76) * mm, "end": v(-17.85, 56.76) * mm});
            skLineSegment(sketch, "E4341", {"start": v(-17.73, 56.73) * mm, "end": v(-17.67, 56.73) * mm});
            skLineSegment(sketch, "E4342", {"start": v(-17.74, 56.7) * mm, "end": v(-17.7, 56.82) * mm});
            skLineSegment(sketch, "E4343", {"start": v(-17.7, 56.82) * mm, "end": v(-17.66, 56.7) * mm});
            skLineSegment(sketch, "E4344", {"start": v(-17.64, 56.82) * mm, "end": v(-17.56, 56.82) * mm});
            skLineSegment(sketch, "E4345", {"start": v(-17.6, 56.7) * mm, "end": v(-17.6, 56.82) * mm});
            skLineSegment(sketch, "E4346", {"start": v(-17.54, 56.82) * mm, "end": v(-17.46, 56.82) * mm});
            skLineSegment(sketch, "E4347", {"start": v(-17.5, 56.7) * mm, "end": v(-17.5, 56.82) * mm});
            skLineSegment(sketch, "E4348", {"start": v(-17.42, 56.74) * mm, "end": v(-17.33, 56.74) * mm});
            skLineSegment(sketch, "E4349", {"start": v(-17.37, 56.7) * mm, "end": v(-17.37, 56.79) * mm});
            skLineSegment(sketch, "E4350", {"start": v(-7.62, 56.76) * mm, "end": v(-7.6, 56.75) * mm});
            skLineSegment(sketch, "E4351", {"start": v(-7.6, 56.75) * mm, "end": v(-7.6, 56.75) * mm});
            skLineSegment(sketch, "E4352", {"start": v(-7.6, 56.75) * mm, "end": v(-7.58, 56.74) * mm});
            skLineSegment(sketch, "E4353", {"start": v(-7.58, 56.74) * mm, "end": v(-7.58, 56.72) * mm});
            skLineSegment(sketch, "E4354", {"start": v(-7.58, 56.72) * mm, "end": v(-7.6, 56.7) * mm});
            skLineSegment(sketch, "E4355", {"start": v(-7.6, 56.7) * mm, "end": v(-7.6, 56.7) * mm});
            skLineSegment(sketch, "E4356", {"start": v(-7.6, 56.7) * mm, "end": v(-7.61, 56.7) * mm});
            skLineSegment(sketch, "E4357", {"start": v(-7.61, 56.7) * mm, "end": v(-7.66, 56.7) * mm});
            skLineSegment(sketch, "E4358", {"start": v(-7.66, 56.7) * mm, "end": v(-7.66, 56.82) * mm});
            skLineSegment(sketch, "E4359", {"start": v(-7.66, 56.82) * mm, "end": v(-7.62, 56.82) * mm});
            skLineSegment(sketch, "E4360", {"start": v(-7.62, 56.82) * mm, "end": v(-7.6, 56.82) * mm});
            skLineSegment(sketch, "E4361", {"start": v(-7.6, 56.82) * mm, "end": v(-7.6, 56.8) * mm});
            skLineSegment(sketch, "E4362", {"start": v(-7.6, 56.8) * mm, "end": v(-7.6, 56.8) * mm});
            skLineSegment(sketch, "E4363", {"start": v(-7.6, 56.8) * mm, "end": v(-7.6, 56.78) * mm});
            skLineSegment(sketch, "E4364", {"start": v(-7.6, 56.78) * mm, "end": v(-7.6, 56.77) * mm});
            skLineSegment(sketch, "E4365", {"start": v(-7.6, 56.77) * mm, "end": v(-7.6, 56.77) * mm});
            skLineSegment(sketch, "E4366", {"start": v(-7.6, 56.77) * mm, "end": v(-7.62, 56.76) * mm});
            skLineSegment(sketch, "E4367", {"start": v(-7.62, 56.76) * mm, "end": v(-7.66, 56.76) * mm});
            skLineSegment(sketch, "E4368", {"start": v(-7.56, 56.68) * mm, "end": v(-7.47, 56.68) * mm});
            skLineSegment(sketch, "E4369", {"start": v(-7.37, 56.7) * mm, "end": v(-7.44, 56.7) * mm});
            skLineSegment(sketch, "E4370", {"start": v(-7.44, 56.7) * mm, "end": v(-7.44, 56.82) * mm});
            skLineSegment(sketch, "E4371", {"start": v(-7.33, 56.76) * mm, "end": v(-7.3, 56.76) * mm});
            skLineSegment(sketch, "E4372", {"start": v(-7.27, 56.7) * mm, "end": v(-7.33, 56.7) * mm});
            skLineSegment(sketch, "E4373", {"start": v(-7.33, 56.7) * mm, "end": v(-7.33, 56.82) * mm});
            skLineSegment(sketch, "E4374", {"start": v(-7.33, 56.82) * mm, "end": v(-7.27, 56.82) * mm});
            skLineSegment(sketch, "E4375", {"start": v(-7.22, 56.7) * mm, "end": v(-7.22, 56.82) * mm});
            skLineSegment(sketch, "E4376", {"start": v(-7.22, 56.82) * mm, "end": v(-7.19, 56.82) * mm});
            skLineSegment(sketch, "E4377", {"start": v(-7.19, 56.82) * mm, "end": v(-7.17, 56.82) * mm});
            skLineSegment(sketch, "E4378", {"start": v(-7.17, 56.82) * mm, "end": v(-7.16, 56.8) * mm});
            skLineSegment(sketch, "E4379", {"start": v(-7.16, 56.8) * mm, "end": v(-7.15, 56.79) * mm});
            skLineSegment(sketch, "E4380", {"start": v(-7.15, 56.79) * mm, "end": v(-7.15, 56.77) * mm});
            skLineSegment(sketch, "E4381", {"start": v(-7.15, 56.77) * mm, "end": v(-7.15, 56.75) * mm});
            skLineSegment(sketch, "E4382", {"start": v(-7.15, 56.75) * mm, "end": v(-7.15, 56.72) * mm});
            skLineSegment(sketch, "E4383", {"start": v(-7.15, 56.72) * mm, "end": v(-7.16, 56.71) * mm});
            skLineSegment(sketch, "E4384", {"start": v(-7.16, 56.71) * mm, "end": v(-7.17, 56.7) * mm});
            skLineSegment(sketch, "E4385", {"start": v(-7.17, 56.7) * mm, "end": v(-7.19, 56.7) * mm});
            skLineSegment(sketch, "E4386", {"start": v(-7.19, 56.7) * mm, "end": v(-7.22, 56.7) * mm});
            skLineSegment(sketch, "E4387", {"start": v(-5.1, 56.82) * mm, "end": v(-5.12, 56.82) * mm});
            skLineSegment(sketch, "E4388", {"start": v(-5.12, 56.82) * mm, "end": v(-5.13, 56.82) * mm});
            skLineSegment(sketch, "E4389", {"start": v(-5.13, 56.82) * mm, "end": v(-5.15, 56.82) * mm});
            skLineSegment(sketch, "E4390", {"start": v(-5.15, 56.82) * mm, "end": v(-5.16, 56.8) * mm});
            skLineSegment(sketch, "E4391", {"start": v(-5.16, 56.8) * mm, "end": v(-5.17, 56.79) * mm});
            skLineSegment(sketch, "E4392", {"start": v(-5.17, 56.79) * mm, "end": v(-5.17, 56.77) * mm});
            skLineSegment(sketch, "E4393", {"start": v(-5.17, 56.77) * mm, "end": v(-5.17, 56.75) * mm});
            skLineSegment(sketch, "E4394", {"start": v(-5.17, 56.75) * mm, "end": v(-5.17, 56.72) * mm});
            skLineSegment(sketch, "E4395", {"start": v(-5.17, 56.72) * mm, "end": v(-5.16, 56.71) * mm});
            skLineSegment(sketch, "E4396", {"start": v(-5.16, 56.71) * mm, "end": v(-5.15, 56.7) * mm});
            skLineSegment(sketch, "E4397", {"start": v(-5.15, 56.7) * mm, "end": v(-5.13, 56.7) * mm});
            skLineSegment(sketch, "E4398", {"start": v(-5.13, 56.7) * mm, "end": v(-5.12, 56.7) * mm});
            skLineSegment(sketch, "E4399", {"start": v(-5.12, 56.7) * mm, "end": v(-5.1, 56.7) * mm});
            skLineSegment(sketch, "E4400", {"start": v(-5.1, 56.7) * mm, "end": v(-5.1, 56.7) * mm});
            skLineSegment(sketch, "E4401", {"start": v(-5.1, 56.7) * mm, "end": v(-5.1, 56.75) * mm});
            skLineSegment(sketch, "E4402", {"start": v(-5.1, 56.75) * mm, "end": v(-5.12, 56.75) * mm});
            skLineSegment(sketch, "E4403", {"start": v(-5.07, 56.68) * mm, "end": v(-4.98, 56.68) * mm});
            skLineSegment(sketch, "E4404", {"start": v(-4.88, 56.7) * mm, "end": v(-4.94, 56.7) * mm});
            skLineSegment(sketch, "E4405", {"start": v(-4.94, 56.7) * mm, "end": v(-4.94, 56.82) * mm});
            skLineSegment(sketch, "E4406", {"start": v(-4.84, 56.76) * mm, "end": v(-4.8, 56.76) * mm});
            skLineSegment(sketch, "E4407", {"start": v(-4.78, 56.7) * mm, "end": v(-4.84, 56.7) * mm});
            skLineSegment(sketch, "E4408", {"start": v(-4.84, 56.7) * mm, "end": v(-4.84, 56.82) * mm});
            skLineSegment(sketch, "E4409", {"start": v(-4.84, 56.82) * mm, "end": v(-4.78, 56.82) * mm});
            skLineSegment(sketch, "E4410", {"start": v(-4.73, 56.7) * mm, "end": v(-4.73, 56.82) * mm});
            skLineSegment(sketch, "E4411", {"start": v(-4.73, 56.82) * mm, "end": v(-4.7, 56.82) * mm});
            skLineSegment(sketch, "E4412", {"start": v(-4.7, 56.82) * mm, "end": v(-4.68, 56.82) * mm});
            skLineSegment(sketch, "E4413", {"start": v(-4.68, 56.82) * mm, "end": v(-4.67, 56.8) * mm});
            skLineSegment(sketch, "E4414", {"start": v(-4.67, 56.8) * mm, "end": v(-4.66, 56.79) * mm});
            skLineSegment(sketch, "E4415", {"start": v(-4.66, 56.79) * mm, "end": v(-4.66, 56.77) * mm});
            skLineSegment(sketch, "E4416", {"start": v(-4.66, 56.77) * mm, "end": v(-4.66, 56.75) * mm});
            skLineSegment(sketch, "E4417", {"start": v(-4.66, 56.75) * mm, "end": v(-4.66, 56.72) * mm});
            skLineSegment(sketch, "E4418", {"start": v(-4.66, 56.72) * mm, "end": v(-4.67, 56.71) * mm});
            skLineSegment(sketch, "E4419", {"start": v(-4.67, 56.71) * mm, "end": v(-4.68, 56.7) * mm});
            skLineSegment(sketch, "E4420", {"start": v(-4.68, 56.7) * mm, "end": v(-4.7, 56.7) * mm});
            skLineSegment(sketch, "E4421", {"start": v(-4.7, 56.7) * mm, "end": v(-4.73, 56.7) * mm});
            skLineSegment(sketch, "E4422", {"start": v(-4.99, 62.52) * mm, "end": v(-5, 62.53) * mm});
            skLineSegment(sketch, "E4423", {"start": v(-5, 62.53) * mm, "end": v(-5.02, 62.53) * mm});
            skLineSegment(sketch, "E4424", {"start": v(-5.02, 62.53) * mm, "end": v(-5.03, 62.52) * mm});
            skLineSegment(sketch, "E4425", {"start": v(-5.03, 62.52) * mm, "end": v(-5.05, 62.51) * mm});
            skLineSegment(sketch, "E4426", {"start": v(-5.05, 62.51) * mm, "end": v(-5.05, 62.5) * mm});
            skLineSegment(sketch, "E4427", {"start": v(-5.05, 62.5) * mm, "end": v(-5.06, 62.48) * mm});
            skLineSegment(sketch, "E4428", {"start": v(-5.06, 62.48) * mm, "end": v(-5.06, 62.46) * mm});
            skLineSegment(sketch, "E4429", {"start": v(-5.06, 62.46) * mm, "end": v(-5.05, 62.43) * mm});
            skLineSegment(sketch, "E4430", {"start": v(-5.05, 62.43) * mm, "end": v(-5.05, 62.42) * mm});
            skLineSegment(sketch, "E4431", {"start": v(-5.05, 62.42) * mm, "end": v(-5.03, 62.4) * mm});
            skLineSegment(sketch, "E4432", {"start": v(-5.03, 62.4) * mm, "end": v(-5.02, 62.4) * mm});
            skLineSegment(sketch, "E4433", {"start": v(-5.02, 62.4) * mm, "end": v(-5, 62.4) * mm});
            skLineSegment(sketch, "E4434", {"start": v(-5, 62.4) * mm, "end": v(-4.99, 62.4) * mm});
            skLineSegment(sketch, "E4435", {"start": v(-4.99, 62.4) * mm, "end": v(-4.98, 62.42) * mm});
            skLineSegment(sketch, "E4436", {"start": v(-4.98, 62.42) * mm, "end": v(-4.98, 62.46) * mm});
            skLineSegment(sketch, "E4437", {"start": v(-4.98, 62.46) * mm, "end": v(-5, 62.46) * mm});
            skLineSegment(sketch, "E4438", {"start": v(-4.93, 62.4) * mm, "end": v(-4.93, 62.53) * mm});
            skLineSegment(sketch, "E4439", {"start": v(-4.93, 62.53) * mm, "end": v(-4.85, 62.4) * mm});
            skLineSegment(sketch, "E4440", {"start": v(-4.85, 62.4) * mm, "end": v(-4.85, 62.53) * mm});
            skLineSegment(sketch, "E4441", {"start": v(-4.8, 62.4) * mm, "end": v(-4.8, 62.53) * mm});
            skLineSegment(sketch, "E4442", {"start": v(-4.8, 62.53) * mm, "end": v(-4.76, 62.53) * mm});
            skLineSegment(sketch, "E4443", {"start": v(-4.76, 62.53) * mm, "end": v(-4.75, 62.52) * mm});
            skLineSegment(sketch, "E4444", {"start": v(-4.75, 62.52) * mm, "end": v(-4.73, 62.51) * mm});
            skLineSegment(sketch, "E4445", {"start": v(-4.73, 62.51) * mm, "end": v(-4.73, 62.5) * mm});
            skLineSegment(sketch, "E4446", {"start": v(-4.73, 62.5) * mm, "end": v(-4.72, 62.48) * mm});
            skLineSegment(sketch, "E4447", {"start": v(-4.72, 62.48) * mm, "end": v(-4.72, 62.46) * mm});
            skLineSegment(sketch, "E4448", {"start": v(-4.72, 62.46) * mm, "end": v(-4.73, 62.43) * mm});
            skLineSegment(sketch, "E4449", {"start": v(-4.73, 62.43) * mm, "end": v(-4.73, 62.42) * mm});
            skLineSegment(sketch, "E4450", {"start": v(-4.73, 62.42) * mm, "end": v(-4.75, 62.4) * mm});
            skLineSegment(sketch, "E4451", {"start": v(-4.75, 62.4) * mm, "end": v(-4.76, 62.4) * mm});
            skLineSegment(sketch, "E4452", {"start": v(-4.76, 62.4) * mm, "end": v(-4.8, 62.4) * mm});
            skLineSegment(sketch, "E4453", {"start": v(-7.73, 62.4) * mm, "end": v(-7.71, 62.4) * mm});
            skLineSegment(sketch, "E4454", {"start": v(-7.71, 62.4) * mm, "end": v(-7.68, 62.4) * mm});
            skLineSegment(sketch, "E4455", {"start": v(-7.68, 62.4) * mm, "end": v(-7.67, 62.4) * mm});
            skLineSegment(sketch, "E4456", {"start": v(-7.67, 62.4) * mm, "end": v(-7.67, 62.42) * mm});
            skLineSegment(sketch, "E4457", {"start": v(-7.67, 62.42) * mm, "end": v(-7.66, 62.43) * mm});
            skLineSegment(sketch, "E4458", {"start": v(-7.66, 62.43) * mm, "end": v(-7.66, 62.44) * mm});
            skLineSegment(sketch, "E4459", {"start": v(-7.66, 62.44) * mm, "end": v(-7.67, 62.45) * mm});
            skLineSegment(sketch, "E4460", {"start": v(-7.67, 62.45) * mm, "end": v(-7.67, 62.46) * mm});
            skLineSegment(sketch, "E4461", {"start": v(-7.67, 62.46) * mm, "end": v(-7.68, 62.46) * mm});
            skLineSegment(sketch, "E4462", {"start": v(-7.68, 62.46) * mm, "end": v(-7.7, 62.47) * mm});
            skLineSegment(sketch, "E4463", {"start": v(-7.7, 62.47) * mm, "end": v(-7.72, 62.48) * mm});
            skLineSegment(sketch, "E4464", {"start": v(-7.72, 62.48) * mm, "end": v(-7.73, 62.48) * mm});
            skLineSegment(sketch, "E4465", {"start": v(-7.73, 62.48) * mm, "end": v(-7.73, 62.5) * mm});
            skLineSegment(sketch, "E4466", {"start": v(-7.73, 62.5) * mm, "end": v(-7.73, 62.5) * mm});
            skLineSegment(sketch, "E4467", {"start": v(-7.73, 62.5) * mm, "end": v(-7.73, 62.52) * mm});
            skLineSegment(sketch, "E4468", {"start": v(-7.73, 62.52) * mm, "end": v(-7.72, 62.52) * mm});
            skLineSegment(sketch, "E4469", {"start": v(-7.72, 62.52) * mm, "end": v(-7.7, 62.53) * mm});
            skLineSegment(sketch, "E4470", {"start": v(-7.7, 62.53) * mm, "end": v(-7.68, 62.53) * mm});
            skLineSegment(sketch, "E4471", {"start": v(-7.68, 62.53) * mm, "end": v(-7.66, 62.52) * mm});
            skLineSegment(sketch, "E4472", {"start": v(-7.53, 62.42) * mm, "end": v(-7.54, 62.4) * mm});
            skLineSegment(sketch, "E4473", {"start": v(-7.54, 62.4) * mm, "end": v(-7.56, 62.4) * mm});
            skLineSegment(sketch, "E4474", {"start": v(-7.56, 62.4) * mm, "end": v(-7.57, 62.4) * mm});
            skLineSegment(sketch, "E4475", {"start": v(-7.57, 62.4) * mm, "end": v(-7.59, 62.4) * mm});
            skLineSegment(sketch, "E4476", {"start": v(-7.59, 62.4) * mm, "end": v(-7.6, 62.42) * mm});
            skLineSegment(sketch, "E4477", {"start": v(-7.6, 62.42) * mm, "end": v(-7.6, 62.43) * mm});
            skLineSegment(sketch, "E4478", {"start": v(-7.6, 62.43) * mm, "end": v(-7.61, 62.46) * mm});
            skLineSegment(sketch, "E4479", {"start": v(-7.61, 62.46) * mm, "end": v(-7.61, 62.48) * mm});
            skLineSegment(sketch, "E4480", {"start": v(-7.61, 62.48) * mm, "end": v(-7.6, 62.5) * mm});
            skLineSegment(sketch, "E4481", {"start": v(-7.6, 62.5) * mm, "end": v(-7.6, 62.51) * mm});
            skLineSegment(sketch, "E4482", {"start": v(-7.6, 62.51) * mm, "end": v(-7.59, 62.52) * mm});
            skLineSegment(sketch, "E4483", {"start": v(-7.59, 62.52) * mm, "end": v(-7.57, 62.53) * mm});
            skLineSegment(sketch, "E4484", {"start": v(-7.57, 62.53) * mm, "end": v(-7.56, 62.53) * mm});
            skLineSegment(sketch, "E4485", {"start": v(-7.56, 62.53) * mm, "end": v(-7.54, 62.52) * mm});
            skLineSegment(sketch, "E4486", {"start": v(-7.54, 62.52) * mm, "end": v(-7.53, 62.52) * mm});
            skLineSegment(sketch, "E4487", {"start": v(-7.42, 62.4) * mm, "end": v(-7.48, 62.4) * mm});
            skLineSegment(sketch, "E4488", {"start": v(-7.48, 62.4) * mm, "end": v(-7.48, 62.53) * mm});
            skLineSegment(sketch, "E4489", {"start": v(-10.2, 62.4) * mm, "end": v(-10.18, 62.4) * mm});
            skLineSegment(sketch, "E4490", {"start": v(-10.18, 62.4) * mm, "end": v(-10.15, 62.4) * mm});
            skLineSegment(sketch, "E4491", {"start": v(-10.15, 62.4) * mm, "end": v(-10.14, 62.4) * mm});
            skLineSegment(sketch, "E4492", {"start": v(-10.14, 62.4) * mm, "end": v(-10.13, 62.42) * mm});
            skLineSegment(sketch, "E4493", {"start": v(-10.13, 62.42) * mm, "end": v(-10.13, 62.43) * mm});
            skLineSegment(sketch, "E4494", {"start": v(-10.13, 62.43) * mm, "end": v(-10.13, 62.44) * mm});
            skLineSegment(sketch, "E4495", {"start": v(-10.13, 62.44) * mm, "end": v(-10.13, 62.45) * mm});
            skLineSegment(sketch, "E4496", {"start": v(-10.13, 62.45) * mm, "end": v(-10.14, 62.46) * mm});
            skLineSegment(sketch, "E4497", {"start": v(-10.14, 62.46) * mm, "end": v(-10.15, 62.46) * mm});
            skLineSegment(sketch, "E4498", {"start": v(-10.15, 62.46) * mm, "end": v(-10.17, 62.47) * mm});
            skLineSegment(sketch, "E4499", {"start": v(-10.17, 62.47) * mm, "end": v(-10.19, 62.48) * mm});
            skLineSegment(sketch, "E4500", {"start": v(-10.19, 62.48) * mm, "end": v(-10.2, 62.48) * mm});
            skLineSegment(sketch, "E4501", {"start": v(-10.2, 62.48) * mm, "end": v(-10.2, 62.5) * mm});
            skLineSegment(sketch, "E4502", {"start": v(-10.2, 62.5) * mm, "end": v(-10.2, 62.5) * mm});
            skLineSegment(sketch, "E4503", {"start": v(-10.2, 62.5) * mm, "end": v(-10.2, 62.52) * mm});
            skLineSegment(sketch, "E4504", {"start": v(-10.2, 62.52) * mm, "end": v(-10.19, 62.52) * mm});
            skLineSegment(sketch, "E4505", {"start": v(-10.19, 62.52) * mm, "end": v(-10.17, 62.53) * mm});
            skLineSegment(sketch, "E4506", {"start": v(-10.17, 62.53) * mm, "end": v(-10.14, 62.53) * mm});
            skLineSegment(sketch, "E4507", {"start": v(-10.14, 62.53) * mm, "end": v(-10.13, 62.52) * mm});
            skLineSegment(sketch, "E4508", {"start": v(-10.07, 62.4) * mm, "end": v(-10.07, 62.53) * mm});
            skLineSegment(sketch, "E4509", {"start": v(-10.07, 62.53) * mm, "end": v(-10.04, 62.53) * mm});
            skLineSegment(sketch, "E4510", {"start": v(-10.04, 62.53) * mm, "end": v(-10.03, 62.52) * mm});
            skLineSegment(sketch, "E4511", {"start": v(-10.03, 62.52) * mm, "end": v(-10.01, 62.51) * mm});
            skLineSegment(sketch, "E4512", {"start": v(-10.01, 62.51) * mm, "end": v(-10, 62.5) * mm});
            skLineSegment(sketch, "E4513", {"start": v(-10, 62.5) * mm, "end": v(-10, 62.48) * mm});
            skLineSegment(sketch, "E4514", {"start": v(-10, 62.48) * mm, "end": v(-10, 62.46) * mm});
            skLineSegment(sketch, "E4515", {"start": v(-10, 62.46) * mm, "end": v(-10, 62.43) * mm});
            skLineSegment(sketch, "E4516", {"start": v(-10, 62.43) * mm, "end": v(-10.01, 62.42) * mm});
            skLineSegment(sketch, "E4517", {"start": v(-10.01, 62.42) * mm, "end": v(-10.03, 62.4) * mm});
            skLineSegment(sketch, "E4518", {"start": v(-10.03, 62.4) * mm, "end": v(-10.04, 62.4) * mm});
            skLineSegment(sketch, "E4519", {"start": v(-10.04, 62.4) * mm, "end": v(-10.07, 62.4) * mm});
            skLineSegment(sketch, "E4520", {"start": v(-9.95, 62.44) * mm, "end": v(-9.9, 62.44) * mm});
            skLineSegment(sketch, "E4521", {"start": v(-9.96, 62.4) * mm, "end": v(-9.92, 62.53) * mm});
            skLineSegment(sketch, "E4522", {"start": v(-9.92, 62.53) * mm, "end": v(-9.88, 62.4) * mm});
            skLineSegment(sketch, "E4523", {"start": v(-12.58, 62.4) * mm, "end": v(-12.62, 62.46) * mm});
            skLineSegment(sketch, "E4524", {"start": v(-12.65, 62.4) * mm, "end": v(-12.65, 62.53) * mm});
            skLineSegment(sketch, "E4525", {"start": v(-12.65, 62.53) * mm, "end": v(-12.6, 62.53) * mm});
            skLineSegment(sketch, "E4526", {"start": v(-12.6, 62.53) * mm, "end": v(-12.6, 62.52) * mm});
            skLineSegment(sketch, "E4527", {"start": v(-12.6, 62.52) * mm, "end": v(-12.59, 62.52) * mm});
            skLineSegment(sketch, "E4528", {"start": v(-12.59, 62.52) * mm, "end": v(-12.58, 62.5) * mm});
            skLineSegment(sketch, "E4529", {"start": v(-12.58, 62.5) * mm, "end": v(-12.58, 62.49) * mm});
            skLineSegment(sketch, "E4530", {"start": v(-12.58, 62.49) * mm, "end": v(-12.59, 62.48) * mm});
            skLineSegment(sketch, "E4531", {"start": v(-12.59, 62.48) * mm, "end": v(-12.6, 62.47) * mm});
            skLineSegment(sketch, "E4532", {"start": v(-12.6, 62.47) * mm, "end": v(-12.6, 62.46) * mm});
            skLineSegment(sketch, "E4533", {"start": v(-12.6, 62.46) * mm, "end": v(-12.65, 62.46) * mm});
            skLineSegment(sketch, "E4534", {"start": v(-12.54, 62.53) * mm, "end": v(-12.45, 62.4) * mm});
            skLineSegment(sketch, "E4535", {"start": v(-12.45, 62.53) * mm, "end": v(-12.54, 62.4) * mm});
            skLineSegment(sketch, "E4536", {"start": v(-15.32, 62.53) * mm, "end": v(-15.25, 62.53) * mm});
            skLineSegment(sketch, "E4537", {"start": v(-15.29, 62.4) * mm, "end": v(-15.29, 62.53) * mm});
            skLineSegment(sketch, "E4538", {"start": v(-15.22, 62.53) * mm, "end": v(-15.14, 62.4) * mm});
            skLineSegment(sketch, "E4539", {"start": v(-15.14, 62.53) * mm, "end": v(-15.22, 62.4) * mm});
            skLineSegment(sketch, "E4540", {"start": v(-17.9, 62.47) * mm, "end": v(-17.94, 62.47) * mm});
            skLineSegment(sketch, "E4541", {"start": v(-17.94, 62.4) * mm, "end": v(-17.94, 62.53) * mm});
            skLineSegment(sketch, "E4542", {"start": v(-17.94, 62.53) * mm, "end": v(-17.88, 62.53) * mm});
            skLineSegment(sketch, "E4543", {"start": v(-17.83, 62.47) * mm, "end": v(-17.8, 62.47) * mm});
            skLineSegment(sketch, "E4544", {"start": v(-17.77, 62.4) * mm, "end": v(-17.83, 62.4) * mm});
            skLineSegment(sketch, "E4545", {"start": v(-17.83, 62.4) * mm, "end": v(-17.83, 62.53) * mm});
            skLineSegment(sketch, "E4546", {"start": v(-17.83, 62.53) * mm, "end": v(-17.77, 62.53) * mm});
            skLineSegment(sketch, "E4547", {"start": v(-17.74, 62.53) * mm, "end": v(-17.67, 62.53) * mm});
            skLineSegment(sketch, "E4548", {"start": v(-17.7, 62.4) * mm, "end": v(-17.7, 62.53) * mm});
            skLineSegment(sketch, "E4549", {"start": v(-17.65, 62.4) * mm, "end": v(-17.56, 62.4) * mm});
            skLineSegment(sketch, "E4550", {"start": v(-17.53, 62.4) * mm, "end": v(-17.53, 62.53) * mm});
            skLineSegment(sketch, "E4551", {"start": v(-17.46, 62.4) * mm, "end": v(-17.46, 62.53) * mm});
            skLineSegment(sketch, "E4552", {"start": v(-17.46, 62.53) * mm, "end": v(-17.4, 62.4) * mm});
            skLineSegment(sketch, "E4553", {"start": v(-17.4, 62.4) * mm, "end": v(-17.4, 62.53) * mm});
            skLineSegment(sketch, "E4554", {"start": v(-17.33, 62.45) * mm, "end": v(-17.24, 62.45) * mm});
            skLineSegment(sketch, "E4555", {"start": v(-17.29, 62.4) * mm, "end": v(-17.29, 62.5) * mm});
            skLineSegment(sketch, "E4556", {"start": v(-20.5, 62.4) * mm, "end": v(-20.48, 62.4) * mm});
            skLineSegment(sketch, "E4557", {"start": v(-20.48, 62.4) * mm, "end": v(-20.45, 62.4) * mm});
            skLineSegment(sketch, "E4558", {"start": v(-20.45, 62.4) * mm, "end": v(-20.44, 62.4) * mm});
            skLineSegment(sketch, "E4559", {"start": v(-20.44, 62.4) * mm, "end": v(-20.43, 62.42) * mm});
            skLineSegment(sketch, "E4560", {"start": v(-20.43, 62.42) * mm, "end": v(-20.42, 62.43) * mm});
            skLineSegment(sketch, "E4561", {"start": v(-20.42, 62.43) * mm, "end": v(-20.42, 62.44) * mm});
            skLineSegment(sketch, "E4562", {"start": v(-20.42, 62.44) * mm, "end": v(-20.43, 62.45) * mm});
            skLineSegment(sketch, "E4563", {"start": v(-20.43, 62.45) * mm, "end": v(-20.44, 62.46) * mm});
            skLineSegment(sketch, "E4564", {"start": v(-20.44, 62.46) * mm, "end": v(-20.45, 62.46) * mm});
            skLineSegment(sketch, "E4565", {"start": v(-20.45, 62.46) * mm, "end": v(-20.47, 62.47) * mm});
            skLineSegment(sketch, "E4566", {"start": v(-20.47, 62.47) * mm, "end": v(-20.49, 62.48) * mm});
            skLineSegment(sketch, "E4567", {"start": v(-20.49, 62.48) * mm, "end": v(-20.5, 62.48) * mm});
            skLineSegment(sketch, "E4568", {"start": v(-20.5, 62.48) * mm, "end": v(-20.5, 62.5) * mm});
            skLineSegment(sketch, "E4569", {"start": v(-20.5, 62.5) * mm, "end": v(-20.5, 62.5) * mm});
            skLineSegment(sketch, "E4570", {"start": v(-20.5, 62.5) * mm, "end": v(-20.5, 62.52) * mm});
            skLineSegment(sketch, "E4571", {"start": v(-20.5, 62.52) * mm, "end": v(-20.49, 62.52) * mm});
            skLineSegment(sketch, "E4572", {"start": v(-20.49, 62.52) * mm, "end": v(-20.47, 62.53) * mm});
            skLineSegment(sketch, "E4573", {"start": v(-20.47, 62.53) * mm, "end": v(-20.44, 62.53) * mm});
            skLineSegment(sketch, "E4574", {"start": v(-20.44, 62.53) * mm, "end": v(-20.42, 62.52) * mm});
            skLineSegment(sketch, "E4575", {"start": v(-20.3, 62.42) * mm, "end": v(-20.3, 62.4) * mm});
            skLineSegment(sketch, "E4576", {"start": v(-20.3, 62.4) * mm, "end": v(-20.32, 62.4) * mm});
            skLineSegment(sketch, "E4577", {"start": v(-20.32, 62.4) * mm, "end": v(-20.33, 62.4) * mm});
            skLineSegment(sketch, "E4578", {"start": v(-20.33, 62.4) * mm, "end": v(-20.35, 62.4) * mm});
            skLineSegment(sketch, "E4579", {"start": v(-20.35, 62.4) * mm, "end": v(-20.36, 62.42) * mm});
            skLineSegment(sketch, "E4580", {"start": v(-20.36, 62.42) * mm, "end": v(-20.37, 62.43) * mm});
            skLineSegment(sketch, "E4581", {"start": v(-20.37, 62.43) * mm, "end": v(-20.38, 62.46) * mm});
            skLineSegment(sketch, "E4582", {"start": v(-20.38, 62.46) * mm, "end": v(-20.38, 62.48) * mm});
            skLineSegment(sketch, "E4583", {"start": v(-20.38, 62.48) * mm, "end": v(-20.37, 62.5) * mm});
            skLineSegment(sketch, "E4584", {"start": v(-20.37, 62.5) * mm, "end": v(-20.36, 62.51) * mm});
            skLineSegment(sketch, "E4585", {"start": v(-20.36, 62.51) * mm, "end": v(-20.35, 62.52) * mm});
            skLineSegment(sketch, "E4586", {"start": v(-20.35, 62.52) * mm, "end": v(-20.33, 62.53) * mm});
            skLineSegment(sketch, "E4587", {"start": v(-20.33, 62.53) * mm, "end": v(-20.32, 62.53) * mm});
            skLineSegment(sketch, "E4588", {"start": v(-20.32, 62.53) * mm, "end": v(-20.3, 62.52) * mm});
            skLineSegment(sketch, "E4589", {"start": v(-20.3, 62.52) * mm, "end": v(-20.3, 62.52) * mm});
            skLineSegment(sketch, "E4590", {"start": v(-20.18, 62.4) * mm, "end": v(-20.24, 62.4) * mm});
            skLineSegment(sketch, "E4591", {"start": v(-20.24, 62.4) * mm, "end": v(-20.24, 62.53) * mm});
            skLineSegment(sketch, "E4592", {"start": v(-20.14, 62.4) * mm, "end": v(-20.14, 62.53) * mm});
            skLineSegment(sketch, "E4593", {"start": v(-20.07, 62.4) * mm, "end": v(-20.12, 62.48) * mm});
            skLineSegment(sketch, "E4594", {"start": v(-20.07, 62.53) * mm, "end": v(-20.14, 62.46) * mm});
            skLineSegment(sketch, "E4595", {"start": v(-22.85, 62.4) * mm, "end": v(-22.83, 62.4) * mm});
            skLineSegment(sketch, "E4596", {"start": v(-22.83, 62.4) * mm, "end": v(-22.8, 62.4) * mm});
            skLineSegment(sketch, "E4597", {"start": v(-22.8, 62.4) * mm, "end": v(-22.79, 62.4) * mm});
            skLineSegment(sketch, "E4598", {"start": v(-22.79, 62.4) * mm, "end": v(-22.78, 62.42) * mm});
            skLineSegment(sketch, "E4599", {"start": v(-22.78, 62.42) * mm, "end": v(-22.78, 62.43) * mm});
            skLineSegment(sketch, "E4600", {"start": v(-22.78, 62.43) * mm, "end": v(-22.78, 62.44) * mm});
            skLineSegment(sketch, "E4601", {"start": v(-22.78, 62.44) * mm, "end": v(-22.78, 62.45) * mm});
            skLineSegment(sketch, "E4602", {"start": v(-22.78, 62.45) * mm, "end": v(-22.79, 62.46) * mm});
            skLineSegment(sketch, "E4603", {"start": v(-22.79, 62.46) * mm, "end": v(-22.8, 62.46) * mm});
            skLineSegment(sketch, "E4604", {"start": v(-22.8, 62.46) * mm, "end": v(-22.83, 62.47) * mm});
            skLineSegment(sketch, "E4605", {"start": v(-22.83, 62.47) * mm, "end": v(-22.84, 62.48) * mm});
            skLineSegment(sketch, "E4606", {"start": v(-22.84, 62.48) * mm, "end": v(-22.84, 62.48) * mm});
            skLineSegment(sketch, "E4607", {"start": v(-22.84, 62.48) * mm, "end": v(-22.85, 62.5) * mm});
            skLineSegment(sketch, "E4608", {"start": v(-22.85, 62.5) * mm, "end": v(-22.85, 62.5) * mm});
            skLineSegment(sketch, "E4609", {"start": v(-22.85, 62.5) * mm, "end": v(-22.84, 62.52) * mm});
            skLineSegment(sketch, "E4610", {"start": v(-22.84, 62.52) * mm, "end": v(-22.84, 62.52) * mm});
            skLineSegment(sketch, "E4611", {"start": v(-22.84, 62.52) * mm, "end": v(-22.83, 62.53) * mm});
            skLineSegment(sketch, "E4612", {"start": v(-22.83, 62.53) * mm, "end": v(-22.8, 62.53) * mm});
            skLineSegment(sketch, "E4613", {"start": v(-22.8, 62.53) * mm, "end": v(-22.78, 62.52) * mm});
            skLineSegment(sketch, "E4614", {"start": v(-22.72, 62.4) * mm, "end": v(-22.72, 62.53) * mm});
            skLineSegment(sketch, "E4615", {"start": v(-22.72, 62.53) * mm, "end": v(-22.7, 62.53) * mm});
            skLineSegment(sketch, "E4616", {"start": v(-22.7, 62.53) * mm, "end": v(-22.67, 62.52) * mm});
            skLineSegment(sketch, "E4617", {"start": v(-22.67, 62.52) * mm, "end": v(-22.66, 62.51) * mm});
            skLineSegment(sketch, "E4618", {"start": v(-22.66, 62.51) * mm, "end": v(-22.66, 62.5) * mm});
            skLineSegment(sketch, "E4619", {"start": v(-22.66, 62.5) * mm, "end": v(-22.65, 62.48) * mm});
            skLineSegment(sketch, "E4620", {"start": v(-22.65, 62.48) * mm, "end": v(-22.65, 62.46) * mm});
            skLineSegment(sketch, "E4621", {"start": v(-22.65, 62.46) * mm, "end": v(-22.66, 62.43) * mm});
            skLineSegment(sketch, "E4622", {"start": v(-22.66, 62.43) * mm, "end": v(-22.66, 62.42) * mm});
            skLineSegment(sketch, "E4623", {"start": v(-22.66, 62.42) * mm, "end": v(-22.67, 62.4) * mm});
            skLineSegment(sketch, "E4624", {"start": v(-22.67, 62.4) * mm, "end": v(-22.7, 62.4) * mm});
            skLineSegment(sketch, "E4625", {"start": v(-22.7, 62.4) * mm, "end": v(-22.72, 62.4) * mm});
            skLineSegment(sketch, "E4626", {"start": v(-22.6, 62.4) * mm, "end": v(-22.6, 62.53) * mm});
            skLineSegment(sketch, "E4627", {"start": v(-25.5, 62.4) * mm, "end": v(-25.48, 62.4) * mm});
            skLineSegment(sketch, "E4628", {"start": v(-25.48, 62.4) * mm, "end": v(-25.45, 62.4) * mm});
            skLineSegment(sketch, "E4629", {"start": v(-25.45, 62.4) * mm, "end": v(-25.44, 62.4) * mm});
            skLineSegment(sketch, "E4630", {"start": v(-25.44, 62.4) * mm, "end": v(-25.44, 62.42) * mm});
            skLineSegment(sketch, "E4631", {"start": v(-25.44, 62.42) * mm, "end": v(-25.43, 62.43) * mm});
            skLineSegment(sketch, "E4632", {"start": v(-25.43, 62.43) * mm, "end": v(-25.43, 62.44) * mm});
            skLineSegment(sketch, "E4633", {"start": v(-25.43, 62.44) * mm, "end": v(-25.44, 62.45) * mm});
            skLineSegment(sketch, "E4634", {"start": v(-25.44, 62.45) * mm, "end": v(-25.44, 62.46) * mm});
            skLineSegment(sketch, "E4635", {"start": v(-25.44, 62.46) * mm, "end": v(-25.45, 62.46) * mm});
            skLineSegment(sketch, "E4636", {"start": v(-25.45, 62.46) * mm, "end": v(-25.48, 62.47) * mm});
            skLineSegment(sketch, "E4637", {"start": v(-25.48, 62.47) * mm, "end": v(-25.5, 62.48) * mm});
            skLineSegment(sketch, "E4638", {"start": v(-25.5, 62.48) * mm, "end": v(-25.5, 62.48) * mm});
            skLineSegment(sketch, "E4639", {"start": v(-25.5, 62.48) * mm, "end": v(-25.5, 62.5) * mm});
            skLineSegment(sketch, "E4640", {"start": v(-25.5, 62.5) * mm, "end": v(-25.5, 62.5) * mm});
            skLineSegment(sketch, "E4641", {"start": v(-25.5, 62.5) * mm, "end": v(-25.5, 62.52) * mm});
            skLineSegment(sketch, "E4642", {"start": v(-25.5, 62.52) * mm, "end": v(-25.5, 62.52) * mm});
            skLineSegment(sketch, "E4643", {"start": v(-25.5, 62.52) * mm, "end": v(-25.48, 62.53) * mm});
            skLineSegment(sketch, "E4644", {"start": v(-25.48, 62.53) * mm, "end": v(-25.45, 62.53) * mm});
            skLineSegment(sketch, "E4645", {"start": v(-25.45, 62.53) * mm, "end": v(-25.43, 62.52) * mm});
            skLineSegment(sketch, "E4646", {"start": v(-25.37, 62.4) * mm, "end": v(-25.37, 62.53) * mm});
            skLineSegment(sketch, "E4647", {"start": v(-25.37, 62.53) * mm, "end": v(-25.35, 62.53) * mm});
            skLineSegment(sketch, "E4648", {"start": v(-25.35, 62.53) * mm, "end": v(-25.33, 62.52) * mm});
            skLineSegment(sketch, "E4649", {"start": v(-25.33, 62.52) * mm, "end": v(-25.32, 62.51) * mm});
            skLineSegment(sketch, "E4650", {"start": v(-25.32, 62.51) * mm, "end": v(-25.3, 62.5) * mm});
            skLineSegment(sketch, "E4651", {"start": v(-25.3, 62.5) * mm, "end": v(-25.3, 62.48) * mm});
            skLineSegment(sketch, "E4652", {"start": v(-25.3, 62.48) * mm, "end": v(-25.3, 62.46) * mm});
            skLineSegment(sketch, "E4653", {"start": v(-25.3, 62.46) * mm, "end": v(-25.3, 62.43) * mm});
            skLineSegment(sketch, "E4654", {"start": v(-25.3, 62.43) * mm, "end": v(-25.32, 62.42) * mm});
            skLineSegment(sketch, "E4655", {"start": v(-25.32, 62.42) * mm, "end": v(-25.33, 62.4) * mm});
            skLineSegment(sketch, "E4656", {"start": v(-25.33, 62.4) * mm, "end": v(-25.35, 62.4) * mm});
            skLineSegment(sketch, "E4657", {"start": v(-25.35, 62.4) * mm, "end": v(-25.37, 62.4) * mm});
            skLineSegment(sketch, "E4658", {"start": v(-25.22, 62.53) * mm, "end": v(-25.2, 62.53) * mm});
            skLineSegment(sketch, "E4659", {"start": v(-25.2, 62.53) * mm, "end": v(-25.19, 62.52) * mm});
            skLineSegment(sketch, "E4660", {"start": v(-25.19, 62.52) * mm, "end": v(-25.18, 62.51) * mm});
            skLineSegment(sketch, "E4661", {"start": v(-25.18, 62.51) * mm, "end": v(-25.17, 62.49) * mm});
            skLineSegment(sketch, "E4662", {"start": v(-25.17, 62.49) * mm, "end": v(-25.17, 62.45) * mm});
            skLineSegment(sketch, "E4663", {"start": v(-25.17, 62.45) * mm, "end": v(-25.18, 62.42) * mm});
            skLineSegment(sketch, "E4664", {"start": v(-25.18, 62.42) * mm, "end": v(-25.19, 62.4) * mm});
            skLineSegment(sketch, "E4665", {"start": v(-25.19, 62.4) * mm, "end": v(-25.2, 62.4) * mm});
            skLineSegment(sketch, "E4666", {"start": v(-25.2, 62.4) * mm, "end": v(-25.22, 62.4) * mm});
            skLineSegment(sketch, "E4667", {"start": v(-25.22, 62.4) * mm, "end": v(-25.24, 62.4) * mm});
            skLineSegment(sketch, "E4668", {"start": v(-25.24, 62.4) * mm, "end": v(-25.25, 62.42) * mm});
            skLineSegment(sketch, "E4669", {"start": v(-25.25, 62.42) * mm, "end": v(-25.26, 62.45) * mm});
            skLineSegment(sketch, "E4670", {"start": v(-25.26, 62.45) * mm, "end": v(-25.26, 62.49) * mm});
            skLineSegment(sketch, "E4671", {"start": v(-25.26, 62.49) * mm, "end": v(-25.25, 62.51) * mm});
            skLineSegment(sketch, "E4672", {"start": v(-25.25, 62.51) * mm, "end": v(-25.24, 62.52) * mm});
            skLineSegment(sketch, "E4673", {"start": v(-25.24, 62.52) * mm, "end": v(-25.22, 62.53) * mm});
            skLineSegment(sketch, "E4674", {"start": v(-25.92, 11.6) * mm, "end": v(18.53, 11.6) * mm});
            skLineSegment(sketch, "E4675", {"start": v(18.53, 24.3) * mm, "end": v(18.53, 11.6) * mm});
            skLineSegment(sketch, "E4676", {"start": v(-23.42, 12.62) * mm, "end": v(-23.33, 12.62) * mm});
            skLineSegment(sketch, "E4677", {"start": v(-23.42, 14.14) * mm, "end": v(-23.33, 14.14) * mm});
            skLineSegment(sketch, "E4678", {"start": v(-23.38, 14.1) * mm, "end": v(-23.38, 14.2) * mm});
            skLineSegment(sketch, "E4679", {"start": v(-25.92, 11.6) * mm, "end": v(-25.92, 24.3) * mm});
            skLineSegment(sketch, "E4680", {"start": v(-23.64, 22.13) * mm, "end": v(-23.64, 20.57) * mm});
            skLineSegment(sketch, "E4681", {"start": v(-26.73, 20.57) * mm, "end": v(-26.73, 22.13) * mm});
            skLineSegment(sketch, "E4682", {"start": v(-26.73, 22.13) * mm, "end": v(-23.64, 22.13) * mm});
            skLineSegment(sketch, "E4683", {"start": v(-45.4, -48.29) * mm, "end": v(-43.4, -48.29) * mm});
            skLineSegment(sketch, "E4684", {"start": v(-43.4, -46.24) * mm, "end": v(-45.4, -46.24) * mm});
            skLineSegment(sketch, "E4685", {"start": v(-3.67, 62.23) * mm, "end": v(-29.07, 62.23) * mm});
            skLineSegment(sketch, "E4686", {"start": v(-26.53, 57.15) * mm, "end": v(-3.67, 57.15) * mm});
            skLineSegment(sketch, "E4687", {"start": v(-3.67, 62.23) * mm, "end": v(-3.67, 57.15) * mm});
            skLineSegment(sketch, "E4688", {"start": v(-29.07, 62.23) * mm, "end": v(-29.07, 59.69) * mm});
            skLineSegment(sketch, "E4689", {"start": v(-29.35, 58.42) * mm, "end": v(-29.35, 56.87) * mm});
            skLineSegment(sketch, "E4690", {"start": v(-29.07, 59.69) * mm, "end": v(-26.53, 59.69) * mm});
            skLineSegment(sketch, "E4691", {"start": v(-26.53, 59.69) * mm, "end": v(-26.53, 57.15) * mm});
            skLineSegment(sketch, "E4692", {"start": v(-29.35, 56.87) * mm, "end": v(-27.8, 56.87) * mm});
            skLineSegment(sketch, "E4693", {"start": v(43.74, 61.14) * mm, "end": v(58.14, 61.14) * mm});
            skLineSegment(sketch, "E4694", {"start": v(58.14, 61.14) * mm, "end": v(58.14, 45.54) * mm});
            skLineSegment(sketch, "E4695", {"start": v(58.14, 45.54) * mm, "end": v(43.74, 45.54) * mm});
            skLineSegment(sketch, "E4696", {"start": v(43.74, 45.54) * mm, "end": v(43.74, 61.14) * mm});
            skLineSegment(sketch, "E4697", {"start": v(-58.28, -63.5) * mm, "end": v(-58.28, -12.7) * mm});
            skLineSegment(sketch, "E4698", {"start": v(-63.36, -15.24) * mm, "end": v(-63.36, -63.5) * mm});
            skLineSegment(sketch, "E4699", {"start": v(-58.28, -63.5) * mm, "end": v(-63.36, -63.5) * mm});
            skLineSegment(sketch, "E4700", {"start": v(-58.28, -12.7) * mm, "end": v(-60.82, -12.7) * mm});
            skLineSegment(sketch, "E4701", {"start": v(-62.1, -12.42) * mm, "end": v(-63.64, -12.42) * mm});
            skLineSegment(sketch, "E4702", {"start": v(-60.82, -12.7) * mm, "end": v(-60.82, -15.24) * mm});
            skLineSegment(sketch, "E4703", {"start": v(-60.82, -15.24) * mm, "end": v(-63.36, -15.24) * mm});
            skLineSegment(sketch, "E4704", {"start": v(-63.64, -12.42) * mm, "end": v(-63.64, -13.97) * mm});
            skLineSegment(sketch, "E4705", {"start": v(43.74, 43.36) * mm, "end": v(58.14, 43.36) * mm});
            skLineSegment(sketch, "E4706", {"start": v(58.14, 43.36) * mm, "end": v(58.14, 27.76) * mm});
            skLineSegment(sketch, "E4707", {"start": v(58.14, 27.76) * mm, "end": v(43.74, 27.76) * mm});
            skLineSegment(sketch, "E4708", {"start": v(43.74, 27.76) * mm, "end": v(43.74, 43.36) * mm});
            skLineSegment(sketch, "E4709", {"start": v(-61.82, 42.77) * mm, "end": v(-59.82, 42.77) * mm});
            skLineSegment(sketch, "E4710", {"start": v(-59.82, 42.77) * mm, "end": v(-59.82, 40.77) * mm});
            skLineSegment(sketch, "E4711", {"start": v(-59.82, 40.77) * mm, "end": v(-61.82, 40.77) * mm});
            skLineSegment(sketch, "E4712", {"start": v(-61.82, 40.77) * mm, "end": v(-61.82, 42.77) * mm});
            skLineSegment(sketch, "E4713", {"start": v(-62.32, 43.76) * mm, "end": v(-62.32, 45.27) * mm});
            skLineSegment(sketch, "E4714", {"start": v(-62.32, 45.27) * mm, "end": v(-60.82, 45.27) * mm});
            skLineSegment(sketch, "E4715", {"start": v(-61.82, 53.8) * mm, "end": v(-59.82, 53.8) * mm});
            skLineSegment(sketch, "E4716", {"start": v(-59.82, 53.8) * mm, "end": v(-59.82, 51.8) * mm});
            skLineSegment(sketch, "E4717", {"start": v(-59.82, 51.8) * mm, "end": v(-61.82, 51.8) * mm});
            skLineSegment(sketch, "E4718", {"start": v(-61.82, 51.8) * mm, "end": v(-61.82, 53.8) * mm});
            skLineSegment(sketch, "E4719", {"start": v(-47.26, -48.55) * mm, "end": v(-47.26, -49.8) * mm});
            skLineSegment(sketch, "E4720", {"start": v(-43.5, -48.55) * mm, "end": v(-47.26, -48.55) * mm});
            skLineSegment(sketch, "E4721", {"start": v(-41.25, -55.37) * mm, "end": v(-47.26, -55.37) * mm});
            skLineSegment(sketch, "E4722", {"start": v(43.74, 7.8) * mm, "end": v(58.14, 7.8) * mm});
            skLineSegment(sketch, "E4723", {"start": v(58.14, 7.8) * mm, "end": v(58.14, -7.8) * mm});
            skLineSegment(sketch, "E4724", {"start": v(58.14, -7.8) * mm, "end": v(43.74, -7.8) * mm});
            skLineSegment(sketch, "E4725", {"start": v(43.74, -7.8) * mm, "end": v(43.74, 7.8) * mm});
            skLineSegment(sketch, "E4726", {"start": v(43.74, 25.96) * mm, "end": v(58.14, 25.96) * mm});
            skLineSegment(sketch, "E4727", {"start": v(58.14, 25.96) * mm, "end": v(58.14, 10.36) * mm});
            skLineSegment(sketch, "E4728", {"start": v(58.14, 10.36) * mm, "end": v(43.74, 10.36) * mm});
            skLineSegment(sketch, "E4729", {"start": v(43.74, 10.36) * mm, "end": v(43.74, 25.96) * mm});
            skLineSegment(sketch, "E4730", {"start": v(5.45, -51.37) * mm, "end": v(5.45, -46.17) * mm});
            skLineSegment(sketch, "E4731", {"start": v(9.1, -46.17) * mm, "end": v(9.1, -51.37) * mm});
            skLineSegment(sketch, "E4732", {"start": v(19.75, -1.25) * mm, "end": v(21.74, -1.25) * mm});
            skLineSegment(sketch, "E4733", {"start": v(21.74, -1.25) * mm, "end": v(21.74, -3.25) * mm});
            skLineSegment(sketch, "E4734", {"start": v(21.74, -3.25) * mm, "end": v(19.75, -3.25) * mm});
            skLineSegment(sketch, "E4735", {"start": v(19.75, -3.25) * mm, "end": v(19.75, -1.25) * mm});
            skLineSegment(sketch, "E4736", {"start": v(-23.56, 25.28) * mm, "end": v(-23.56, 23.72) * mm});
            skLineSegment(sketch, "E4737", {"start": v(-26.66, 23.72) * mm, "end": v(-26.66, 25.28) * mm});
            skLineSegment(sketch, "E4738", {"start": v(-26.66, 25.28) * mm, "end": v(-23.56, 25.28) * mm});
            skLineSegment(sketch, "E4739", {"start": v(-26.38, 22.45) * mm, "end": v(-23.84, 22.45) * mm});
            skLineSegment(sketch, "E4740", {"start": v(-23.4, 16.13) * mm, "end": v(-23.4, 14.58) * mm});
            skLineSegment(sketch, "E4741", {"start": v(-26.5, 14.58) * mm, "end": v(-26.5, 16.13) * mm});
            skLineSegment(sketch, "E4742", {"start": v(-26.5, 16.13) * mm, "end": v(-23.4, 16.13) * mm});
            skLineSegment(sketch, "E4743", {"start": v(-26.23, 13.3) * mm, "end": v(-23.68, 13.3) * mm});
            skLineSegment(sketch, "E4744", {"start": v(-23.46, 13.29) * mm, "end": v(-23.46, 11.74) * mm});
            skLineSegment(sketch, "E4745", {"start": v(-26.56, 11.74) * mm, "end": v(-26.56, 13.29) * mm});
            skLineSegment(sketch, "E4746", {"start": v(-26.56, 13.29) * mm, "end": v(-23.46, 13.29) * mm});
            skLineSegment(sketch, "E4747", {"start": v(-26.28, 10.46) * mm, "end": v(-23.74, 10.46) * mm});
            skLineSegment(sketch, "E4748", {"start": v(-56.2, -9.62) * mm, "end": v(-56.2, -8.86) * mm});
            skLineSegment(sketch, "E4749", {"start": v(-56.09, -1.65) * mm, "end": v(-56.09, -0.89) * mm});
            skLineSegment(sketch, "E4750", {"start": v(-55.7, -1.27) * mm, "end": v(-56.47, -1.27) * mm});
            skLineSegment(sketch, "E4751", {"start": v(-56.2, 6.89) * mm, "end": v(-56.2, 7.65) * mm});
            skLineSegment(sketch, "E4752", {"start": v(-56.09, 14.86) * mm, "end": v(-56.09, 15.62) * mm});
            skLineSegment(sketch, "E4753", {"start": v(-55.7, 15.24) * mm, "end": v(-56.47, 15.24) * mm});
            skLineSegment(sketch, "E4754", {"start": v(-63.36, 63.5) * mm, "end": v(63.64, 63.5) * mm});
            skLineSegment(sketch, "E4755", {"start": v(-63.36, 63.5) * mm, "end": v(-63.36, -63.5) * mm});
            skLineSegment(sketch, "E4756", {"start": v(-63.36, -63.5) * mm, "end": v(63.64, -63.5) * mm});
            skLineSegment(sketch, "E4757", {"start": v(63.64, 63.5) * mm, "end": v(63.64, -63.5) * mm});
            skSolve(sketch);
        }
        {
            var Q0;
            Q0=qCreatedBy(makeId("Top.planeOp"),FACE);
            var sketch = newSketch(context, id + "F1", { "sketchPlane" : qUnion([Q0])});
            skPoint(sketch, "E4758.0", {"position": v(-63.36, -63.5) * mm});
            skPoint(sketch, "E4758.1", {"position": v(63.64, -63.5) * mm});
            skPoint(sketch, "E4758.2", {"position": v(63.64, 63.5) * mm});
            skPoint(sketch, "E4758.3", {"position": v(-63.36, 63.5) * mm});
            skLineSegment(sketch, "E4759.bottom", {"start": v(63.64, -63.5) * mm, "end": v(-63.36, -63.5) * mm});
            skLineSegment(sketch, "E4759.top", {"start": v(63.64, 63.5) * mm, "end": v(-63.36, 63.5) * mm});
            skLineSegment(sketch, "E4759.left", {"start": v(63.64, -63.5) * mm, "end": v(63.64, 63.5) * mm});
            skLineSegment(sketch, "E4759.right", {"start": v(-63.36, -63.5) * mm, "end": v(-63.36, 63.5) * mm});
            skSolve(sketch);
        }
        {
            var Q0;
            Q0 = qSketchRegion(id + "F1", true);
            extrude(context, id + "F2", {"entities" : qUnion([Q0]), "oppositeDirection" : true, "depth" : 10.16 * mm, "offsetDistance" : 25.4 * mm});
        }
        {
            var Q0;
            Q0=makeQuery(id+"F2.opExtrude","CAP_FACE",FACE,{"disambiguationData":[OSD([sQuery(id+"F1.wireOp",EDGE,"E4759.bottom"),sQuery(id+"F1.wireOp",EDGE,"E4759.top"),sQuery(id+"F1.wireOp",EDGE,"E4759.left"),sQuery(id+"F1.wireOp",EDGE,"E4759.right")])],"isStart":false});
            var sketch = newSketch(context, id + "F3", { "sketchPlane" : qUnion([Q0])});
            skPoint(sketch, "E4760.0", {"position": v(-63.36, 63.5) * mm});
            skPoint(sketch, "E4760.1", {"position": v(63.64, 63.5) * mm});
            skPoint(sketch, "E4760.2", {"position": v(63.64, -63.5) * mm});
            skPoint(sketch, "E4760.3", {"position": v(-63.36, -63.5) * mm});
            skLineSegment(sketch, "E4761.0", {"start": v(-63.36, 63.5) * mm, "end": v(63.64, 63.5) * mm, "construction": true});
            skLineSegment(sketch, "E4761.1", {"start": v(63.64, -63.5) * mm, "end": v(63.64, 63.5) * mm, "construction": true});
            skLineSegment(sketch, "E4761.2", {"start": v(-63.36, -63.5) * mm, "end": v(-63.36, 63.5) * mm, "construction": true});
            skLineSegment(sketch, "E4761.3", {"start": v(-63.36, -63.5) * mm, "end": v(63.64, -63.5) * mm, "construction": true});
            skLineSegment(sketch, "E4762.0", {"start": v(-57.01, -57.15) * mm, "end": v(-57.01, 57.15) * mm});
            skLineSegment(sketch, "E4762.1", {"start": v(-57.01, -57.15) * mm, "end": v(57.29, -57.15) * mm});
            skLineSegment(sketch, "E4762.2", {"start": v(57.29, -57.15) * mm, "end": v(57.29, 57.15) * mm});
            skLineSegment(sketch, "E4762.3", {"start": v(-57.01, 57.15) * mm, "end": v(57.29, 57.15) * mm});
            skSolve(sketch);
        }
        {
            var Q0;
            Q0 = qSketchRegion(id + "F3", true);
            extrude(context, id + "F4", {"entities" : qUnion([Q0]), "operationType" : NewBodyOperationType.REMOVE, "endBound" : BoundingType.THROUGH_ALL, "oppositeDirection" : true, "depth" : 25.4 * mm, "offsetDistance" : 25.4 * mm});
        }
        {
            var Q0;
            Q0=makeQuery(id+"F2.opExtrude","CAP_FACE",FACE,{"disambiguationData":[OSD([sQuery(id+"F1.wireOp",EDGE,"E4759.bottom"),sQuery(id+"F1.wireOp",EDGE,"E4759.top"),sQuery(id+"F1.wireOp",EDGE,"E4759.left"),sQuery(id+"F1.wireOp",EDGE,"E4759.right")])],"isStart":false});
            var sketch = newSketch(context, id + "F5", { "sketchPlane" : qUnion([Q0])});
            skPoint(sketch, "E4763.0", {"position": v(-63.64, 12.42) * mm});
            skPoint(sketch, "E4763.1", {"position": v(-58.28, 63.5) * mm});
            skLineSegment(sketch, "E4764.bottom", {"start": v(-63.64, 12.42) * mm, "end": v(-53.2, 12.42) * mm});
            skLineSegment(sketch, "E4764.top", {"start": v(-63.64, 63.5) * mm, "end": v(-53.2, 63.5) * mm});
            skLineSegment(sketch, "E4764.left", {"start": v(-63.64, 12.42) * mm, "end": v(-63.64, 63.5) * mm});
            skLineSegment(sketch, "E4764.right", {"start": v(-53.2, 12.42) * mm, "end": v(-53.2, 63.5) * mm});
            skLineSegment(sketch, "E4765.bottom", {"start": v(-51.4, -57.15) * mm, "end": v(-36.16, -57.15) * mm});
            skLineSegment(sketch, "E4765.top", {"start": v(-51.4, -63.5) * mm, "end": v(-36.16, -63.5) * mm});
            skLineSegment(sketch, "E4765.left", {"start": v(-51.4, -57.15) * mm, "end": v(-51.4, -63.5) * mm});
            skLineSegment(sketch, "E4765.right", {"start": v(-36.16, -57.15) * mm, "end": v(-36.16, -63.5) * mm});
            skPoint(sketch, "E4766.0", {"position": v(-48.86, -56.77) * mm});
            skPoint(sketch, "E4766.1", {"position": v(-38.7, -56.77) * mm});
            skLineSegment(sketch, "E4767.bottom", {"start": v(44.1, 63.5) * mm, "end": v(63.64, 63.5) * mm});
            skLineSegment(sketch, "E4767.top", {"start": v(44.1, 57.15) * mm, "end": v(63.64, 57.15) * mm});
            skLineSegment(sketch, "E4767.left", {"start": v(44.1, 63.5) * mm, "end": v(44.1, 57.15) * mm});
            skLineSegment(sketch, "E4767.right", {"start": v(63.64, 63.5) * mm, "end": v(63.64, 57.15) * mm});
            skLineSegment(sketch, "E4768.0", {"start": v(-57.01, 57.15) * mm, "end": v(57.29, 57.15) * mm, "construction": true});
            skPoint(sketch, "E4769.0", {"position": v(46.65, 59.25) * mm});
            skSolve(sketch);
        }
        {
            var Q0;
            Q0 = qSketchRegion(id + "F5", true);
            extrude(context, id + "F6", {"entities" : qUnion([Q0]), "operationType" : NewBodyOperationType.REMOVE, "endBound" : BoundingType.THROUGH_ALL, "oppositeDirection" : true, "depth" : 25.4 * mm, "offsetDistance" : 25.4 * mm});
        }
        {
            var Q0;
            {var subQ0=sQuery(id+"F1.wireOp",EDGE,"E4759.left");var subQ1=sQuery(id+"F1.wireOp",EDGE,"E4759.top");Q0=makeQuery(id+"F6.boolean.opBoolean","SPLIT",FACE,{"disambiguationData":[TD([makeQuery(id+"F2.opExtrude","SWEPT_FACE",FACE,{"disambiguationData":[OSD([subQ0])]})])],"derivedFrom":makeQuery(id+"F2.opExtrude","CAP_FACE",FACE,{"disambiguationData":[OSD([sQuery(id+"F1.wireOp",EDGE,"E4759.bottom"),subQ1,subQ0,sQuery(id+"F1.wireOp",EDGE,"E4759.right")])],"isStart":false})});}
            var sketch = newSketch(context, id + "F7", { "sketchPlane" : qUnion([Q0])});
            skPoint(sketch, "E4770.0", {"position": v(-37.96, 41.89) * mm});
            skPoint(sketch, "E4770.1", {"position": v(-37.96, 39.39) * mm});
            skPoint(sketch, "E4771.0", {"position": v(38.24, 39.39) * mm});
            skPoint(sketch, "E4771.1", {"position": v(38.24, 41.89) * mm});
            skPoint(sketch, "E4772.0", {"position": v(37, -35.56) * mm});
            skPoint(sketch, "E4772.1", {"position": v(39.5, -35.56) * mm});
            skLineSegment(sketch, "E4773.left", {"start": v(38.24, 41.89) * mm, "end": v(38.24, 39.39) * mm, "construction": true});
            skPoint(sketch, "E4774.0", {"position": v(37, 40.64) * mm});
            skPoint(sketch, "E4774.1", {"position": v(39.5, 40.64) * mm});
            skLineSegment(sketch, "E4775.top", {"start": v(37, -35.56) * mm, "end": v(39.5, -35.56) * mm, "construction": true});
            skLineSegment(sketch, "E4776", {"start": v(38.24, 41.89) * mm, "end": v(57.29, 41.89) * mm, "construction": true});
            skPoint(sketch, "E4777.1", {"position": v(-39.2, 40.64) * mm});
            skPoint(sketch, "E4777.2", {"position": v(-36.7, 40.64) * mm});
            skLineSegment(sketch, "E4778.0", {"start": v(-53.2, 57.15) * mm, "end": v(44.1, 57.15) * mm, "construction": true});
            skLineSegment(sketch, "E4779", {"start": v(-36.63, 57.15) * mm, "end": v(-39.2, 57.15) * mm, "construction": true});
            skPoint(sketch, "E4780.0", {"position": v(38.24, -34.31) * mm});
            skPoint(sketch, "E4780.1", {"position": v(38.24, -36.81) * mm});
            skLineSegment(sketch, "E4781", {"start": v(39.5, -35.56) * mm, "end": v(39.5, -57.15) * mm, "construction": true});
            skLineSegment(sketch, "E4782.left", {"start": v(38.24, -34.31) * mm, "end": v(38.24, -36.81) * mm, "construction": true});
            skLineSegment(sketch, "E4783", {"start": v(-57.01, -36.81) * mm, "end": v(37, -36.81) * mm, "construction": true});
            skLineSegment(sketch, "E4784", {"start": v(39.5, -35.56) * mm, "end": v(39.5, 39.39) * mm, "construction": true});
            skLineSegment(sketch, "E4785", {"start": v(-57.01, -34.32) * mm, "end": v(37, -34.32) * mm, "construction": true});
            skLineSegment(sketch, "E4786", {"start": v(38.24, -34.31) * mm, "end": v(37, -34.32) * mm, "construction": true});
            skLineSegment(sketch, "E4787", {"start": v(37, -36.81) * mm, "end": v(37, -57.15) * mm, "construction": true});
            skLineSegment(sketch, "E4788", {"start": v(-39.2, 39.39) * mm, "end": v(-37.96, 39.39) * mm, "construction": true});
            skLineSegment(sketch, "E4789", {"start": v(-39.2, 39.39) * mm, "end": v(-39.2, 57.15) * mm, "construction": true});
            skLineSegment(sketch, "E4790", {"start": v(38.24, 41.89) * mm, "end": v(-36.63, 41.89) * mm, "construction": true});
            skLineSegment(sketch, "E4791", {"start": v(-36.63, 41.89) * mm, "end": v(-36.63, 57.15) * mm, "construction": true});
            skLineSegment(sketch, "E4792", {"start": v(37, -34.32) * mm, "end": v(37, 39.39) * mm, "construction": true});
            skLineSegment(sketch, "E4793", {"start": v(37, -57.15) * mm, "end": v(39.5, -57.15) * mm, "construction": true});
            skLineSegment(sketch, "E4794", {"start": v(57.29, 41.89) * mm, "end": v(57.29, 39.39) * mm, "construction": true});
            skLineSegment(sketch, "E4795", {"start": v(-39.2, 57.15) * mm, "end": v(-36.63, 57.15) * mm, "construction": true});
            skLineSegment(sketch, "E4796", {"start": v(-37.96, 39.39) * mm, "end": v(37, 39.39) * mm, "construction": true});
            skLineSegment(sketch, "E4797", {"start": v(39.5, 39.39) * mm, "end": v(57.29, 39.39) * mm, "construction": true});
            skLineSegment(sketch, "E4798.bottom", {"start": v(-37.87, 46.97) * mm, "end": v(57.29, 46.97) * mm});
            skLineSegment(sketch, "E4798.top", {"start": v(-37.87, 34.3) * mm, "end": v(57.29, 34.3) * mm});
            skLineSegment(sketch, "E4798.left", {"start": v(-37.87, 46.97) * mm, "end": v(-37.87, 34.3) * mm});
            skLineSegment(sketch, "E4798.right", {"start": v(57.29, 46.97) * mm, "end": v(57.29, 34.3) * mm});
            skLineSegment(sketch, "E4799.bottom", {"start": v(44.57, 34.3) * mm, "end": v(31.91, 34.3) * mm});
            skLineSegment(sketch, "E4799.top", {"start": v(44.57, -57.15) * mm, "end": v(31.91, -57.15) * mm});
            skLineSegment(sketch, "E4799.left", {"start": v(44.57, 34.3) * mm, "end": v(44.57, -57.15) * mm});
            skLineSegment(sketch, "E4799.right", {"start": v(31.91, 34.3) * mm, "end": v(31.91, -57.15) * mm});
            skLineSegment(sketch, "E4800.left", {"start": v(31.91, -29.24) * mm, "end": v(31.91, -41.9) * mm});
            skLineSegment(sketch, "E4801.bottom", {"start": v(-44.29, 57.15) * mm, "end": v(-31.55, 57.15) * mm});
            skLineSegment(sketch, "E4801.top", {"start": v(-44.29, 34.3) * mm, "end": v(-31.55, 34.3) * mm});
            skLineSegment(sketch, "E4801.left", {"start": v(-44.29, 57.15) * mm, "end": v(-44.29, 34.3) * mm});
            skLineSegment(sketch, "E4801.right", {"start": v(-31.55, 57.15) * mm, "end": v(-31.55, 34.3) * mm});
            skLineSegment(sketch, "E4802.0", {"start": v(-57.01, -57.15) * mm, "end": v(-57.01, 12.42) * mm, "construction": true});
            skPoint(sketch, "E4803.0", {"position": v(-43.78, -33.1) * mm});
            skPoint(sketch, "E4803.1", {"position": v(-37.96, -19.44) * mm});
            skPoint(sketch, "E4803.2", {"position": v(-44.42, -33.18) * mm});
            skLineSegment(sketch, "E4804.bottom", {"start": v(-57.01, -23.25) * mm, "end": v(31.91, -23.25) * mm});
            skLineSegment(sketch, "E4804.top", {"start": v(-57.01, -30.56) * mm, "end": v(31.91, -30.56) * mm});
            skLineSegment(sketch, "E4804.left", {"start": v(-57.01, -23.25) * mm, "end": v(-57.01, -30.56) * mm});
            skLineSegment(sketch, "E4804.right", {"start": v(31.91, -23.25) * mm, "end": v(31.91, -30.56) * mm});
            skSolve(sketch);
        }
        {
            var Q0;
            Q0 = qSketchRegion(id + "F7", true);
            extrude(context, id + "F8", {"entities" : qUnion([Q0]), "oppositeDirection" : true, "depth" : 10.16 * mm, "offsetDistance" : 25.4 * mm});
        }
        {
            var Q0;
            {var subQ10=sQuery(id+"F0.wireOp",EDGE,"E1281");Q0=makeQuery(id+"F0.imprint","IMPRINT",FACE,{"disambiguationData":[TD([[makeQuery(id+"F0.imprint","IMPRINT",EDGE,{"derivedFrom":subQ10}),-1.0]])]});}
            var sketch = newSketch(context, id + "F9", { "sketchPlane" : qUnion([Q0])});
            skLineSegment(sketch, "E4805.0", {"start": v(-63.36, 63.5) * mm, "end": v(-63.36, -63.5) * mm, "construction": true});
            skLineSegment(sketch, "E4805.1", {"start": v(-57.01, -12.42) * mm, "end": v(-57.01, 57.15) * mm, "construction": true});
            skPoint(sketch, "E4806.0", {"position": v(-59.82, 40.77) * mm});
            skPoint(sketch, "E4806.1", {"position": v(-59.82, 53.8) * mm});
            skLineSegment(sketch, "E4807.bottom", {"start": v(-63.36, 56.34) * mm, "end": v(-57.01, 56.34) * mm});
            skLineSegment(sketch, "E4807.top", {"start": v(-63.36, 38.23) * mm, "end": v(-57.01, 38.23) * mm});
            skLineSegment(sketch, "E4807.left", {"start": v(-63.36, 56.34) * mm, "end": v(-63.36, 38.23) * mm});
            skLineSegment(sketch, "E4807.right", {"start": v(-57.01, 56.34) * mm, "end": v(-57.01, 38.23) * mm});
            skLineSegment(sketch, "E4808.0", {"start": v(-63.36, 63.5) * mm, "end": v(63.64, 63.5) * mm, "construction": true});
            skLineSegment(sketch, "E4808.1", {"start": v(57.29, 57.15) * mm, "end": v(-36.16, 57.15) * mm, "construction": true});
            skPoint(sketch, "E4809.0", {"position": v(-29.07, 62.23) * mm});
            skPoint(sketch, "E4809.1", {"position": v(-3.67, 57.15) * mm});
            skLineSegment(sketch, "E4810.bottom", {"start": v(-31.61, 63.5) * mm, "end": v(-1.13, 63.5) * mm});
            skLineSegment(sketch, "E4810.top", {"start": v(-31.61, 57.15) * mm, "end": v(-1.13, 57.15) * mm});
            skLineSegment(sketch, "E4810.left", {"start": v(-31.61, 63.5) * mm, "end": v(-31.61, 57.15) * mm});
            skLineSegment(sketch, "E4810.right", {"start": v(-1.13, 63.5) * mm, "end": v(-1.13, 57.15) * mm});
            skPoint(sketch, "E4811.0", {"position": v(43.74, 61.14) * mm});
            skLineSegment(sketch, "E4812.bottom", {"start": v(43.74, 61.14) * mm, "end": v(51.91, 61.14) * mm});
            skLineSegment(sketch, "E4812.top", {"start": v(43.74, 57.15) * mm, "end": v(51.91, 57.15) * mm});
            skLineSegment(sketch, "E4812.left", {"start": v(43.74, 61.14) * mm, "end": v(43.74, 57.15) * mm});
            skLineSegment(sketch, "E4812.right", {"start": v(51.91, 61.14) * mm, "end": v(51.91, 57.15) * mm});
            skLineSegment(sketch, "E4813.0", {"start": v(44.1, -57.15) * mm, "end": v(-53.2, -57.15) * mm, "construction": true});
            skLineSegment(sketch, "E4814.0", {"start": v(-63.36, -63.5) * mm, "end": v(63.64, -63.5) * mm, "construction": true});
            skLineSegment(sketch, "E4815.bottom", {"start": v(-34.7, -57.15) * mm, "end": v(-0.54, -57.15) * mm, "construction": true});
            skLineSegment(sketch, "E4815.top", {"start": v(-34.7, -63.5) * mm, "end": v(-0.54, -63.5) * mm, "construction": true});
            skLineSegment(sketch, "E4815.left", {"start": v(-34.7, -57.15) * mm, "end": v(-34.7, -63.5) * mm, "construction": true});
            skLineSegment(sketch, "E4815.right", {"start": v(-0.54, -57.15) * mm, "end": v(-0.54, -63.5) * mm, "construction": true});
            skPoint(sketch, "E4816.0", {"position": v(-3.08, -52.07) * mm});
            skPoint(sketch, "E4816.1", {"position": v(-32.16, -52.07) * mm});
            skSolve(sketch);
        }
        {
            var Q0;
            Q0=sQuery(id+"F0.wireOp",VERTEX,"E4019.start");
            var Q1;
            Q1=sQuery(id+"F0.wireOp",VERTEX,"E4018.start");
            var Q2;
            Q2=sQuery(id+"F0.wireOp",VERTEX,"E4020.start");
            var Q3;
            Q3=makeQuery(id+"F8.opExtrude","SWEPT_BODY",BODY,{"disambiguationData":[OSD([sQuery(id+"F7.wireOp",EDGE,"E4798.bottom"),sQuery(id+"F7.wireOp",EDGE,"E4798.top"),sQuery(id+"F7.wireOp",EDGE,"E4798.right"),sQuery(id+"F7.wireOp",EDGE,"E4799.top"),sQuery(id+"F7.wireOp",EDGE,"E4799.left"),sQuery(id+"F7.wireOp",EDGE,"E4799.right"),sQuery(id+"F7.wireOp",EDGE,"E4800.bottom"),sQuery(id+"F7.wireOp",EDGE,"E4800.top"),sQuery(id+"F7.wireOp",EDGE,"E4800.right"),sQuery(id+"F7.wireOp",EDGE,"E4801.bottom"),sQuery(id+"F7.wireOp",EDGE,"E4801.top"),sQuery(id+"F7.wireOp",EDGE,"E4801.left"),sQuery(id+"F7.wireOp",EDGE,"E4801.right")])]});
            hole(context, id + "F10", {"style" : HoleStyle.SIMPLE, "endStyle" : HoleEndStyle.THROUGH, "standardTappedOrClearance" : lookupTablePath({ "standard" : "ANSI", "engagement" : "75%", "pitch" : "48 tpi", "size" : "#4", "type" : "Tapped" }), "standardBlindInLast" : lookupTablePath({ "standard" : "ANSI", "engagement" : "75%", "pitch" : "48 tpi", "size" : "#4", "type" : "Tapped" }), "holeDiameter" : 2.37 * mm, "majorDiameter" : 2.84 * mm, "showTappedDepth" : true, "isTappedThrough" : true, "tappedDepth" : 3.97 * mm, "tapClearance" : 3, "locations" : qUnion([Q0, Q1, Q2]), "scope" : qUnion([Q3])});
        }
        {
            var Q0;
            Q0=makeQuery(id+"F8.opExtrude","CAP_FACE",FACE,{"disambiguationData":[OSD([sQuery(id+"F7.wireOp",EDGE,"E4798.bottom"),sQuery(id+"F7.wireOp",EDGE,"E4798.top"),sQuery(id+"F7.wireOp",EDGE,"E4798.right"),sQuery(id+"F7.wireOp",EDGE,"E4799.top"),sQuery(id+"F7.wireOp",EDGE,"E4799.left"),sQuery(id+"F7.wireOp",EDGE,"E4799.right"),sQuery(id+"F7.wireOp",EDGE,"E4800.bottom"),sQuery(id+"F7.wireOp",EDGE,"E4800.top"),sQuery(id+"F7.wireOp",EDGE,"E4800.right"),sQuery(id+"F7.wireOp",EDGE,"E4801.bottom"),sQuery(id+"F7.wireOp",EDGE,"E4801.top"),sQuery(id+"F7.wireOp",EDGE,"E4801.left"),sQuery(id+"F7.wireOp",EDGE,"E4801.right")])],"isStart":true});
            var sketch = newSketch(context, id + "F11", { "sketchPlane" : qUnion([Q0])});
            skCircle(sketch, "E4817.0", {"center": v(-37.96, 40.64) * mm, "radius": 1.19 * mm});
            skCircle(sketch, "E4818.cCircle", {"center": v(-37.96, 40.64) * mm, "radius": 3.18 * mm, "construction": true});
            skLineSegment(sketch, "E4818.0", {"start": v(-36.17, 43.84) * mm, "end": v(-34.3, 40.7) * mm});
            skLineSegment(sketch, "E4818.1", {"start": v(-34.3, 40.7) * mm, "end": v(-36.08, 37.5) * mm});
            skLineSegment(sketch, "E4818.2", {"start": v(-36.08, 37.5) * mm, "end": v(-39.75, 37.44) * mm});
            skLineSegment(sketch, "E4818.3", {"start": v(-39.75, 37.44) * mm, "end": v(-41.63, 40.59) * mm});
            skLineSegment(sketch, "E4818.4", {"start": v(-41.63, 40.59) * mm, "end": v(-39.84, 43.79) * mm});
            skLineSegment(sketch, "E4818.5", {"start": v(-39.84, 43.79) * mm, "end": v(-36.17, 43.84) * mm});
            skPoint(sketch, "E4818.0.midPoint", {"position": v(-35.23, 42.27) * mm});
            skCircle(sketch, "E4819.0", {"center": v(38.24, 40.64) * mm, "radius": 1.19 * mm, "construction": true});
            skCircle(sketch, "E4819.1", {"center": v(38.24, -35.56) * mm, "radius": 1.19 * mm, "construction": true});
            skCircle(sketch, "E4820.cCircle", {"center": v(38.24, 40.64) * mm, "radius": 3.18 * mm, "construction": true});
            skLineSegment(sketch, "E4820.0", {"start": v(36.45, 37.44) * mm, "end": v(34.57, 40.59) * mm});
            skLineSegment(sketch, "E4820.1", {"start": v(34.57, 40.59) * mm, "end": v(36.36, 43.79) * mm});
            skLineSegment(sketch, "E4820.2", {"start": v(36.36, 43.79) * mm, "end": v(40.03, 43.84) * mm});
            skLineSegment(sketch, "E4820.3", {"start": v(40.03, 43.84) * mm, "end": v(41.9, 40.7) * mm});
            skLineSegment(sketch, "E4820.4", {"start": v(41.9, 40.7) * mm, "end": v(40.12, 37.5) * mm});
            skLineSegment(sketch, "E4820.5", {"start": v(40.12, 37.5) * mm, "end": v(36.45, 37.44) * mm});
            skPoint(sketch, "E4820.0.midPoint", {"position": v(35.51, 39.01) * mm});
            skCircle(sketch, "E4821.cCircle", {"center": v(38.24, -35.56) * mm, "radius": 3.18 * mm, "construction": true});
            skLineSegment(sketch, "E4821.0", {"start": v(34.57, -35.61) * mm, "end": v(36.36, -32.41) * mm});
            skLineSegment(sketch, "E4821.1", {"start": v(36.36, -32.41) * mm, "end": v(40.03, -32.36) * mm});
            skLineSegment(sketch, "E4821.2", {"start": v(40.03, -32.36) * mm, "end": v(41.9, -35.5) * mm});
            skLineSegment(sketch, "E4821.3", {"start": v(41.9, -35.5) * mm, "end": v(40.12, -38.7) * mm});
            skLineSegment(sketch, "E4821.4", {"start": v(40.12, -38.7) * mm, "end": v(36.45, -38.76) * mm});
            skLineSegment(sketch, "E4821.5", {"start": v(36.45, -38.76) * mm, "end": v(34.57, -35.61) * mm});
            skPoint(sketch, "E4821.0.midPoint", {"position": v(35.47, -34.01) * mm});
            skSolve(sketch);
        }
        {
            var Q0;
            Q0 = qSketchRegion(id + "F11", true);
            extrude(context, id + "F12", {"entities" : qUnion([Q0]), "operationType" : NewBodyOperationType.REMOVE, "oppositeDirection" : true, "depth" : 2.8 * mm, "offsetDistance" : 25.4 * mm});
        }
        {
            var Q0;
            {var subQ0=sQuery(id+"F1.wireOp",EDGE,"E4759.bottom");Q0=makeQuery(id+"F6.boolean.opBoolean","SPLIT",FACE,{"disambiguationData":[TD([makeQuery(id+"F2.opExtrude","SWEPT_FACE",FACE,{"disambiguationData":[OSD([subQ0])]})])],"derivedFrom":makeQuery(id+"F2.opExtrude","CAP_FACE",FACE,{"disambiguationData":[OSD([subQ0,sQuery(id+"F1.wireOp",EDGE,"E4759.top"),sQuery(id+"F1.wireOp",EDGE,"E4759.left"),sQuery(id+"F1.wireOp",EDGE,"E4759.right")])],"isStart":false})});}
            var sketch = newSketch(context, id + "F13", { "sketchPlane" : qUnion([Q0])});
            skLineSegment(sketch, "E4822", {"start": v(-53.2, 63.5) * mm, "end": v(44.1, 57.15) * mm, "construction": true});
            skLineSegment(sketch, "E4823", {"start": v(-53.2, 57.15) * mm, "end": v(44.1, 63.5) * mm, "construction": true});
            skPoint(sketch, "E4824", {"position": v(-4.55, 60.33) * mm});
            skLineSegment(sketch, "E4825.0", {"start": v(-57.01, -57.15) * mm, "end": v(-57.01, 12.42) * mm, "construction": true});
            skLineSegment(sketch, "E4825.1", {"start": v(-63.36, 12.42) * mm, "end": v(-63.36, -63.5) * mm, "construction": true});
            skLineSegment(sketch, "E4826", {"start": v(-63.36, -25.68) * mm, "end": v(-57.01, -25.68) * mm, "construction": true});
            skPoint(sketch, "E4827", {"position": v(-60.19, -25.68) * mm});
            skLineSegment(sketch, "E4828", {"start": v(-63.36, -50.8) * mm, "end": v(-57.01, -50.8) * mm, "construction": true});
            skPoint(sketch, "E4829", {"position": v(-60.19, -50.8) * mm});
            skLineSegment(sketch, "E4830.0", {"start": v(57.29, -57.15) * mm, "end": v(57.29, 57.15) * mm, "construction": true});
            skLineSegment(sketch, "E4830.1", {"start": v(63.64, 57.15) * mm, "end": v(63.64, -63.5) * mm, "construction": true});
            skLineSegment(sketch, "E4830.2", {"start": v(63.64, -63.5) * mm, "end": v(-36.16, -63.5) * mm, "construction": true});
            skLineSegment(sketch, "E4830.3", {"start": v(-36.16, -57.15) * mm, "end": v(57.29, -57.15) * mm, "construction": true});
            skLineSegment(sketch, "E4831", {"start": v(-10.76, -57.15) * mm, "end": v(38.24, -57.15) * mm, "construction": true});
            skLineSegment(sketch, "E4832", {"start": v(38.24, -57.15) * mm, "end": v(38.24, -63.5) * mm, "construction": true});
            skLineSegment(sketch, "E4833", {"start": v(38.24, -63.5) * mm, "end": v(63.64, -63.5) * mm, "construction": true});
            skLineSegment(sketch, "E4834", {"start": v(63.64, -38.1) * mm, "end": v(57.29, -38.1) * mm, "construction": true});
            skLineSegment(sketch, "E4835", {"start": v(57.29, -38.1) * mm, "end": v(57.29, 31.75) * mm, "construction": true});
            skLineSegment(sketch, "E4836", {"start": v(57.29, 31.75) * mm, "end": v(63.64, 31.75) * mm, "construction": true});
            skPoint(sketch, "E4837", {"position": v(38.24, -60.33) * mm});
            skPoint(sketch, "E4838", {"position": v(60.46, -38.1) * mm});
            skPoint(sketch, "E4839", {"position": v(60.46, 31.75) * mm});
            skPoint(sketch, "E4840.0", {"position": v(-31.55, 46.97) * mm});
            skPoint(sketch, "E4840.1", {"position": v(31.91, 34.3) * mm});
            skLineSegment(sketch, "E4841", {"start": v(-31.55, 46.97) * mm, "end": v(31.91, 34.3) * mm});
            skLineSegment(sketch, "E4842", {"start": v(31.91, 46.97) * mm, "end": v(-31.55, 34.3) * mm});
            skPoint(sketch, "E4843", {"position": v(0.18, 40.64) * mm});
            skSolve(sketch);
        }
        {
            var Q0;
            Q0=makeQuery(id+"F8.opExtrude","SWEPT_BODY",BODY,{"disambiguationData":[OSD([sQuery(id+"F7.wireOp",EDGE,"E4798.bottom"),sQuery(id+"F7.wireOp",EDGE,"E4798.top"),sQuery(id+"F7.wireOp",EDGE,"E4798.right"),sQuery(id+"F7.wireOp",EDGE,"E4799.top"),sQuery(id+"F7.wireOp",EDGE,"E4799.left"),sQuery(id+"F7.wireOp",EDGE,"E4799.right"),sQuery(id+"F7.wireOp",EDGE,"E4800.left"),sQuery(id+"F7.wireOp",EDGE,"E4801.bottom"),sQuery(id+"F7.wireOp",EDGE,"E4801.top"),sQuery(id+"F7.wireOp",EDGE,"E4801.left"),sQuery(id+"F7.wireOp",EDGE,"E4801.right"),sQuery(id+"F7.wireOp",EDGE,"E4804.bottom"),sQuery(id+"F7.wireOp",EDGE,"E4804.top"),sQuery(id+"F7.wireOp",EDGE,"E4804.left")])]});
            var Q1;
            Q1=makeQuery(id+"F6.boolean.opBoolean","SPLIT",BODY,{"disambiguationData":[OD(2.0)],"derivedFrom":makeQuery(id+"F2.opExtrude","SWEPT_BODY",BODY,{"disambiguationData":[OSD([sQuery(id+"F1.wireOp",EDGE,"E4759.bottom"),sQuery(id+"F1.wireOp",EDGE,"E4759.top"),sQuery(id+"F1.wireOp",EDGE,"E4759.left"),sQuery(id+"F1.wireOp",EDGE,"E4759.right")])]})});
            var Q2;
            Q2=makeQuery(id+"F6.boolean.opBoolean","SPLIT",BODY,{"disambiguationData":[OD(1.0)],"derivedFrom":makeQuery(id+"F2.opExtrude","SWEPT_BODY",BODY,{"disambiguationData":[OSD([sQuery(id+"F1.wireOp",EDGE,"E4759.bottom"),sQuery(id+"F1.wireOp",EDGE,"E4759.top"),sQuery(id+"F1.wireOp",EDGE,"E4759.left"),sQuery(id+"F1.wireOp",EDGE,"E4759.right")])]})});
            var Q3;
            Q3=makeQuery(id+"F6.boolean.opBoolean","SPLIT",BODY,{"disambiguationData":[OD(0.0)],"derivedFrom":makeQuery(id+"F2.opExtrude","SWEPT_BODY",BODY,{"disambiguationData":[OSD([sQuery(id+"F1.wireOp",EDGE,"E4759.bottom"),sQuery(id+"F1.wireOp",EDGE,"E4759.top"),sQuery(id+"F1.wireOp",EDGE,"E4759.left"),sQuery(id+"F1.wireOp",EDGE,"E4759.right")])]})});
            booleanBodies(context, id + "F14", {"operationType" : BooleanOperationType.UNION, "tools" : qUnion([Q0, Q1, Q2, Q3])});
        }
        {
            var Q0;
            {var subQ0=sQuery(id+"F1.wireOp",EDGE,"E4759.right");var subQ1=makeQuery(id+"F2.opExtrude","SWEPT_FACE",FACE,{"disambiguationData":[OSD([subQ0])]});var subQ3=makeQuery(id+"F6.opExtrude","SWEPT_FACE",FACE,{"disambiguationData":[OSD([sQuery(id+"F5.wireOp",EDGE,"E4764.bottom")])]});var subQ5=sQuery(id+"F1.wireOp",EDGE,"E4759.top");var subQ7=sQuery(id+"F1.wireOp",EDGE,"E4759.left");var subQ8=sQuery(id+"F1.wireOp",EDGE,"E4759.bottom");var subQ9=makeQuery(id+"F2.opExtrude","CAP_FACE",FACE,{"disambiguationData":[OSD([subQ8,subQ5,subQ7,subQ0])],"isStart":true});Q0=makeQuery(id+"F14.opBoolean","MERGE",FACE,{"derivedFrom":[makeQuery(id+"F6.boolean.opBoolean","SPLIT",FACE,{"disambiguationData":[TD([makeQuery(id+"F2.opExtrude","SWEPT_FACE",FACE,{"disambiguationData":[OSD([subQ8])]})])],"derivedFrom":subQ9}),makeQuery(id+"F6.boolean.opBoolean","SPLIT",FACE,{"disambiguationData":[TD([makeQuery(id+"F2.opExtrude","SWEPT_FACE",FACE,{"disambiguationData":[OSD([subQ7])]})])],"derivedFrom":subQ9}),makeQuery(id+"FKCReh4iLkf0LwH_2.boolean.opBoolean","SPLIT",FACE,{"disambiguationData":[TD([makeQuery(id+"F6.boolean.opBoolean","COPY",FACE,{"derivedFrom":subQ3})])],"derivedFrom":makeQuery(id+"F6.boolean.opBoolean","SPLIT",FACE,{"disambiguationData":[TD([subQ1])],"derivedFrom":subQ9})}),makeQuery(id+"F8.opExtrude","CAP_FACE",FACE,{"disambiguationData":[OSD([sQuery(id+"F7.wireOp",EDGE,"E4798.bottom"),sQuery(id+"F7.wireOp",EDGE,"E4798.top"),sQuery(id+"F7.wireOp",EDGE,"E4798.right"),sQuery(id+"F7.wireOp",EDGE,"E4799.top"),sQuery(id+"F7.wireOp",EDGE,"E4799.left"),sQuery(id+"F7.wireOp",EDGE,"E4799.right"),sQuery(id+"F7.wireOp",EDGE,"E4800.left"),sQuery(id+"F7.wireOp",EDGE,"E4801.bottom"),sQuery(id+"F7.wireOp",EDGE,"E4801.top"),sQuery(id+"F7.wireOp",EDGE,"E4801.left"),sQuery(id+"F7.wireOp",EDGE,"E4801.right"),sQuery(id+"F7.wireOp",EDGE,"E4804.bottom"),sQuery(id+"F7.wireOp",EDGE,"E4804.top"),sQuery(id+"F7.wireOp",EDGE,"E4804.left")])],"isStart":false})]});}
            var sketch = newSketch(context, id + "F15", { "sketchPlane" : qUnion([Q0])});
            skLineSegment(sketch, "E4844.bottom", {"start": v(-3.7, 57.15) * mm, "end": v(9, 57.15) * mm});
            skLineSegment(sketch, "E4844.top", {"start": v(-3.7, 30.56) * mm, "end": v(9, 30.56) * mm});
            skLineSegment(sketch, "E4844.left", {"start": v(-3.7, 57.15) * mm, "end": v(-3.7, 30.56) * mm});
            skLineSegment(sketch, "E4844.right", {"start": v(9, 57.15) * mm, "end": v(9, 30.56) * mm});
            skLineSegment(sketch, "E4845.bottom", {"start": v(44.1, -57.15) * mm, "end": v(31.4, -57.15) * mm});
            skLineSegment(sketch, "E4845.top", {"start": v(44.1, -46.97) * mm, "end": v(31.4, -46.97) * mm});
            skLineSegment(sketch, "E4845.left", {"start": v(44.1, -57.15) * mm, "end": v(44.1, -46.97) * mm});
            skLineSegment(sketch, "E4845.right", {"start": v(31.4, -57.15) * mm, "end": v(31.4, -46.97) * mm});
            skSolve(sketch);
        }
        {
            var Q0;
            Q0 = qSketchRegion(id + "F15", true);
            var Q1;
            {var subQ1=sQuery(id+"F1.wireOp",EDGE,"E4759.left");var subQ2=sQuery(id+"F1.wireOp",EDGE,"E4759.top");var subQ4=sQuery(id+"F1.wireOp",EDGE,"E4759.right");var subQ5=sQuery(id+"F1.wireOp",EDGE,"E4759.bottom");var subQ6=makeQuery(id+"F2.opExtrude","CAP_FACE",FACE,{"disambiguationData":[OSD([subQ5,subQ2,subQ1,subQ4])],"isStart":false});Q1=makeQuery(id+"F14.opBoolean","MERGE",FACE,{"derivedFrom":[makeQuery(id+"F6.boolean.opBoolean","SPLIT",FACE,{"disambiguationData":[TD([makeQuery(id+"F2.opExtrude","SWEPT_FACE",FACE,{"disambiguationData":[OSD([subQ5])]})])],"derivedFrom":subQ6}),makeQuery(id+"F8.opExtrude","CAP_FACE",FACE,{"disambiguationData":[OSD([sQuery(id+"F7.wireOp",EDGE,"E4798.bottom"),sQuery(id+"F7.wireOp",EDGE,"E4798.top"),sQuery(id+"F7.wireOp",EDGE,"E4798.right"),sQuery(id+"F7.wireOp",EDGE,"E4799.top"),sQuery(id+"F7.wireOp",EDGE,"E4799.left"),sQuery(id+"F7.wireOp",EDGE,"E4799.right"),sQuery(id+"F7.wireOp",EDGE,"E4800.left"),sQuery(id+"F7.wireOp",EDGE,"E4801.bottom"),sQuery(id+"F7.wireOp",EDGE,"E4801.top"),sQuery(id+"F7.wireOp",EDGE,"E4801.left"),sQuery(id+"F7.wireOp",EDGE,"E4801.right"),sQuery(id+"F7.wireOp",EDGE,"E4804.bottom"),sQuery(id+"F7.wireOp",EDGE,"E4804.top"),sQuery(id+"F7.wireOp",EDGE,"E4804.left")])],"isStart":true}),makeQuery(id+"F6.boolean.opBoolean","SPLIT",FACE,{"disambiguationData":[TD([makeQuery(id+"F2.opExtrude","SWEPT_FACE",FACE,{"disambiguationData":[OSD([subQ4])]})])],"derivedFrom":subQ6}),makeQuery(id+"F6.boolean.opBoolean","SPLIT",FACE,{"disambiguationData":[TD([makeQuery(id+"F2.opExtrude","SWEPT_FACE",FACE,{"disambiguationData":[OSD([subQ1])]})])],"derivedFrom":subQ6})]});}
            extrude(context, id + "F16", {"entities" : qUnion([Q0]), "endBound" : BoundingType.UP_TO_SURFACE, "oppositeDirection" : true, "depth" : 25.4 * mm, "endBoundEntityFace" : qUnion([Q1]), "offsetDistance" : 25.4 * mm});
        }
        {
            var Q0;
            Q0=makeQuery(id+"F16.opExtrude","SWEPT_BODY",BODY,{"disambiguationData":[OSD([sQuery(id+"F15.wireOp",EDGE,"E4844.bottom"),sQuery(id+"F15.wireOp",EDGE,"E4844.top"),sQuery(id+"F15.wireOp",EDGE,"E4844.left"),sQuery(id+"F15.wireOp",EDGE,"E4844.right")])]});
            var Q1;
            Q1=makeQuery(id+"F16.opExtrude","SWEPT_BODY",BODY,{"disambiguationData":[OSD([sQuery(id+"F15.wireOp",EDGE,"E4845.bottom"),sQuery(id+"F15.wireOp",EDGE,"E4845.top"),sQuery(id+"F15.wireOp",EDGE,"E4845.left"),sQuery(id+"F15.wireOp",EDGE,"E4845.right")])]});
            var Q2;
            Q2=makeQuery(id+"F8.opExtrude","SWEPT_BODY",BODY,{"disambiguationData":[OSD([sQuery(id+"F7.wireOp",EDGE,"E4798.bottom"),sQuery(id+"F7.wireOp",EDGE,"E4798.top"),sQuery(id+"F7.wireOp",EDGE,"E4798.right"),sQuery(id+"F7.wireOp",EDGE,"E4799.top"),sQuery(id+"F7.wireOp",EDGE,"E4799.left"),sQuery(id+"F7.wireOp",EDGE,"E4799.right"),sQuery(id+"F7.wireOp",EDGE,"E4800.left"),sQuery(id+"F7.wireOp",EDGE,"E4801.bottom"),sQuery(id+"F7.wireOp",EDGE,"E4801.top"),sQuery(id+"F7.wireOp",EDGE,"E4801.left"),sQuery(id+"F7.wireOp",EDGE,"E4801.right"),sQuery(id+"F7.wireOp",EDGE,"E4804.bottom"),sQuery(id+"F7.wireOp",EDGE,"E4804.top"),sQuery(id+"F7.wireOp",EDGE,"E4804.left")])]});
            booleanBodies(context, id + "F17", {"operationType" : BooleanOperationType.UNION, "tools" : qUnion([Q0, Q1, Q2])});
        }
        {
            var Q0;
            Q0=sQuery(id+"F13.wireOp",VERTEX,"E4843");
            var Q1;
            Q1=sQuery(id+"F13.wireOp",VERTEX,"E4824");
            var Q2;
            Q2=sQuery(id+"F13.wireOp",VERTEX,"E4827");
            var Q3;
            Q3=sQuery(id+"F13.wireOp",VERTEX,"27d94986-75c7-4895-be9d-b3400d40103f");
            var Q4;
            Q4=sQuery(id+"F13.wireOp",VERTEX,"E4837");
            var Q5;
            Q5=sQuery(id+"F13.wireOp",VERTEX,"E4838");
            var Q6;
            Q6=sQuery(id+"F13.wireOp",VERTEX,"E4839");
            var Q7;
            Q7=makeQuery(id+"F16.opExtrude","SWEPT_BODY",BODY,{"disambiguationData":[OSD([sQuery(id+"F15.wireOp",EDGE,"E4844.bottom"),sQuery(id+"F15.wireOp",EDGE,"E4844.top"),sQuery(id+"F15.wireOp",EDGE,"E4844.left"),sQuery(id+"F15.wireOp",EDGE,"E4844.right")])]});
            hole(context, id + "F18", {"style" : HoleStyle.SIMPLE, "endStyle" : HoleEndStyle.BLIND, "standardTappedOrClearance" : lookupTablePath({ "standard" : "ANSI", "engagement" : "75%", "pitch" : "32 tpi", "size" : "#8", "type" : "Tapped" }), "standardBlindInLast" : lookupTablePath({ "standard" : "ANSI", "engagement" : "75%", "pitch" : "32 tpi", "size" : "#8", "type" : "Tapped" }), "holeDiameter" : 3.45 * mm, "majorDiameter" : 4.17 * mm, "showTappedDepth" : true, "holeDepth" : 6.35 * mm, "isTappedThrough" : true, "tappedDepth" : 3.97 * mm, "tapClearance" : 3, "locations" : qUnion([Q0, Q1, Q2, Q3, Q4, Q5, Q6]), "scope" : qUnion([Q7])});
        }
        {
            var Q0;
            Q0 = qSketchRegion(id + "F9", true);
            extrude(context, id + "F19", {"entities" : qUnion([Q0]), "operationType" : NewBodyOperationType.REMOVE, "oppositeDirection" : true, "depth" : 3.8 * mm, "offsetDistance" : 25.4 * mm});
        }
        {
            var Q0;
            {var subQ0=sQuery(id+"F7.wireOp",EDGE,"E4804.bottom");var subQ1=sQuery(id+"F7.wireOp",EDGE,"E4800.left");var subQ2=sQuery(id+"F7.wireOp",EDGE,"E4799.right");var subQ3=sQuery(id+"F7.wireOp",EDGE,"E4798.top");var subQ4=sQuery(id+"F7.wireOp",EDGE,"E4801.top");var subQ6=sQuery(id+"F7.wireOp",EDGE,"E4804.top");var subQ8=sQuery(id+"F7.wireOp",EDGE,"E4801.right");var subQ9=sQuery(id+"F1.wireOp",EDGE,"E4759.right");var subQ10=makeQuery(id+"F2.opExtrude","SWEPT_FACE",FACE,{"disambiguationData":[OSD([subQ9])]});var subQ12=sQuery(id+"F7.wireOp",EDGE,"E4799.left");var subQ13=sQuery(id+"F1.wireOp",EDGE,"E4759.bottom");var subQ14=makeQuery(id+"F2.opExtrude","SWEPT_FACE",FACE,{"disambiguationData":[OSD([subQ13])]});var subQ15=sQuery(id+"F15.wireOp",EDGE,"E4845.right");var subQ16=sQuery(id+"F7.wireOp",EDGE,"E4801.left");var subQ17=sQuery(id+"F1.wireOp",EDGE,"E4759.left");var subQ18=makeQuery(id+"F2.opExtrude","SWEPT_FACE",FACE,{"disambiguationData":[OSD([subQ17])]});var subQ22=sQuery(id+"F7.wireOp",EDGE,"E4798.bottom");var subQ24=sQuery(id+"F1.wireOp",EDGE,"E4759.top");var subQ27=sQuery(id+"F15.wireOp",EDGE,"E4844.right");var subQ28=sQuery(id+"F15.wireOp",EDGE,"E4844.left");var subQ29=sQuery(id+"F15.wireOp",EDGE,"E4845.left");var subQ30=makeQuery(id+"F2.opExtrude","CAP_FACE",FACE,{"disambiguationData":[OSD([subQ13,subQ24,subQ17,subQ9])],"isStart":true});Q0=makeQuery(id+"FPYLqA7GtjiNf4D_3.boolean.opBoolean","MERGE",FACE,{"derivedFrom":[makeQuery(id+"F19.boolean.opBoolean","SPLIT",FACE,{"disambiguationData":[TD([subQ14])],"derivedFrom":makeQuery(id+"F17.opBoolean","MERGE",FACE,{"derivedFrom":[makeQuery(id+"F14.opBoolean","MERGE",FACE,{"derivedFrom":[makeQuery(id+"F6.boolean.opBoolean","SPLIT",FACE,{"disambiguationData":[TD([subQ14])],"derivedFrom":subQ30}),makeQuery(id+"F6.boolean.opBoolean","SPLIT",FACE,{"disambiguationData":[TD([subQ18])],"derivedFrom":subQ30}),makeQuery(id+"F6.boolean.opBoolean","SPLIT",FACE,{"disambiguationData":[TD([subQ10])],"derivedFrom":subQ30}),makeQuery(id+"F8.opExtrude","CAP_FACE",FACE,{"disambiguationData":[OSD([subQ22,subQ3,sQuery(id+"F7.wireOp",EDGE,"E4798.right"),sQuery(id+"F7.wireOp",EDGE,"E4799.top"),subQ12,subQ2,subQ1,sQuery(id+"F7.wireOp",EDGE,"E4801.bottom"),subQ4,subQ16,subQ8,subQ0,subQ6,sQuery(id+"F7.wireOp",EDGE,"E4804.left")])],"isStart":false})]}),makeQuery(id+"F16.opExtrude","CAP_FACE",FACE,{"disambiguationData":[OSD([sQuery(id+"F15.wireOp",EDGE,"E4844.bottom"),sQuery(id+"F15.wireOp",EDGE,"E4844.top"),subQ28,subQ27])],"isStart":true}),makeQuery(id+"F16.opExtrude","CAP_FACE",FACE,{"disambiguationData":[OSD([sQuery(id+"F15.wireOp",EDGE,"E4845.bottom"),sQuery(id+"F15.wireOp",EDGE,"E4845.top"),subQ29,subQ15])],"isStart":true})]})}),makeQuery(id+"FPYLqA7GtjiNf4D_3.opExtrude","CAP_FACE",FACE,{"disambiguationData":[OSD([sQuery(id+"FYnjf84aCbRyCxk_3.wireOp",EDGE,"5Sk2HiFE-O8BW-0VYy-KlGN-BMyJLsCqNalT.bottom"),sQuery(id+"FYnjf84aCbRyCxk_3.wireOp",EDGE,"5Sk2HiFE-O8BW-0VYy-KlGN-BMyJLsCqNalT.top"),sQuery(id+"FYnjf84aCbRyCxk_3.wireOp",EDGE,"5Sk2HiFE-O8BW-0VYy-KlGN-BMyJLsCqNalT.right"),sQuery(id+"FYnjf84aCbRyCxk_3.wireOp",EDGE,"2d492c23-d53a-4b99-8497-5823aa0174fd.0")])],"isStart":true})]});}
            var sketch = newSketch(context, id + "F20", { "sketchPlane" : qUnion([Q0])});
            skPoint(sketch, "E4846.0", {"position": v(-26.66, 25.28) * mm});
            skPoint(sketch, "E4846.1", {"position": v(18.53, 24.3) * mm});
            skLineSegment(sketch, "E4847.bottom", {"start": v(18.53, 24.3) * mm, "end": v(-27.12, 24.3) * mm});
            skLineSegment(sketch, "E4847.top", {"start": v(18.53, 23.25) * mm, "end": v(-27.12, 23.25) * mm});
            skLineSegment(sketch, "E4847.left", {"start": v(18.53, 24.3) * mm, "end": v(18.53, 23.25) * mm});
            skLineSegment(sketch, "E4847.right", {"start": v(-27.12, 24.3) * mm, "end": v(-27.12, 23.25) * mm});
            skSolve(sketch);
        }
        {
            var Q0;
            Q0 = qSketchRegion(id + "F20", true);
            extrude(context, id + "F21", {"entities" : qUnion([Q0]), "operationType" : NewBodyOperationType.REMOVE, "endBound" : BoundingType.THROUGH_ALL, "oppositeDirection" : true, "depth" : 2.54 * mm, "offsetDistance" : 25.4 * mm});
        }
        {
            var Q0;
            Q0=makeQuery(id+"F0.imprint","IMPRINT",FACE,{"disambiguationData":[TD([[makeQuery(id+"F0.imprint","IMPRINT",EDGE,{"derivedFrom":sQuery(id+"F0.wireOp",EDGE,"E102")}),1.0]])]});
            var sketch = newSketch(context, id + "F22", { "sketchPlane" : qUnion([Q0])});
            skLineSegment(sketch, "E4848.0", {"start": v(-57.01, 30.56) * mm, "end": v(-3.7, 30.56) * mm});
            skLineSegment(sketch, "E4849.0", {"start": v(-63.36, 63.5) * mm, "end": v(63.64, 63.5) * mm});
            skPoint(sketch, "E4850.0", {"position": v(-43.78, 40.6) * mm});
            skPoint(sketch, "E4851.0", {"position": v(-43.78, 52.02) * mm});
            skPoint(sketch, "E4852.0", {"position": v(-44.3, 59.49) * mm});
            skPoint(sketch, "E4853.0", {"position": v(-43.78, 59.6) * mm});
            skPoint(sketch, "E4854.0", {"position": v(-43.78, 35.6) * mm});
            skLineSegment(sketch, "E4855.0", {"start": v(-51.4, 63.5) * mm, "end": v(-51.4, 57.15) * mm});
            skPoint(sketch, "E4855.1", {"position": v(-36.16, 60.33) * mm});
            skLineSegment(sketch, "E4856.bottom", {"start": v(-51.4, 63.5) * mm, "end": v(-36.16, 63.5) * mm});
            skLineSegment(sketch, "E4856.top", {"start": v(-51.4, 60.87) * mm, "end": v(-36.16, 60.87) * mm});
            skLineSegment(sketch, "E4856.left", {"start": v(-51.4, 63.5) * mm, "end": v(-51.4, 60.87) * mm});
            skLineSegment(sketch, "E4856.right", {"start": v(-36.16, 63.5) * mm, "end": v(-36.16, 60.87) * mm});
            skLineSegment(sketch, "E4857.top", {"start": v(-57.01, 34.33) * mm, "end": v(-3.7, 34.33) * mm});
            skLineSegment(sketch, "E4857.left", {"start": v(-57.01, 30.56) * mm, "end": v(-57.01, 34.33) * mm});
            skLineSegment(sketch, "E4857.right", {"start": v(-3.7, 30.56) * mm, "end": v(-3.7, 34.33) * mm});
            skSolve(sketch);
        }
        {
            var Q0;
            Q0 = qSketchRegion(id + "F22", true);
            extrude(context, id + "F23", {"entities" : qUnion([Q0]), "operationType" : NewBodyOperationType.ADD, "oppositeDirection" : true, "depth" : 3.8 * mm, "offsetDistance" : 25.4 * mm});
        }
        {
            var Q0;
            {var subQ60=sQuery(id+"F0.wireOp",EDGE,"E1298");Q0=makeQuery(id+"F0.imprint","IMPRINT",FACE,{"disambiguationData":[TD([[makeQuery(id+"F0.imprint","IMPRINT",EDGE,{"derivedFrom":subQ60}),1.0]])]});}
            var sketch = newSketch(context, id + "F24", { "sketchPlane" : qUnion([Q0])});
            skLineSegment(sketch, "E4858.0", {"start": v(-31.55, -46.97) * mm, "end": v(31.4, -46.97) * mm});
            skLineSegment(sketch, "E4858.1", {"start": v(-44.29, -34.3) * mm, "end": v(31.91, -34.3) * mm});
            skLineSegment(sketch, "E4859.bottom", {"start": v(-20.9, -34.3) * mm, "end": v(-14.51, -34.3) * mm});
            skLineSegment(sketch, "E4859.top", {"start": v(-20.9, -46.97) * mm, "end": v(-14.51, -46.97) * mm});
            skLineSegment(sketch, "E4859.left", {"start": v(-20.9, -34.3) * mm, "end": v(-20.9, -46.97) * mm});
            skLineSegment(sketch, "E4859.right", {"start": v(-14.51, -34.3) * mm, "end": v(-14.51, -46.97) * mm});
            skPoint(sketch, "E4860.0", {"position": v(-22.16, -52.07) * mm});
            skPoint(sketch, "E4860.1", {"position": v(-13.24, -52.07) * mm});
            skSolve(sketch);
        }
        {
            var Q0;
            Q0 = qSketchRegion(id + "F24", true);
            extrude(context, id + "F25", {"entities" : qUnion([Q0]), "operationType" : NewBodyOperationType.REMOVE, "oppositeDirection" : true, "depth" : 2.54 * mm, "offsetDistance" : 25.4 * mm});
        }
    });
